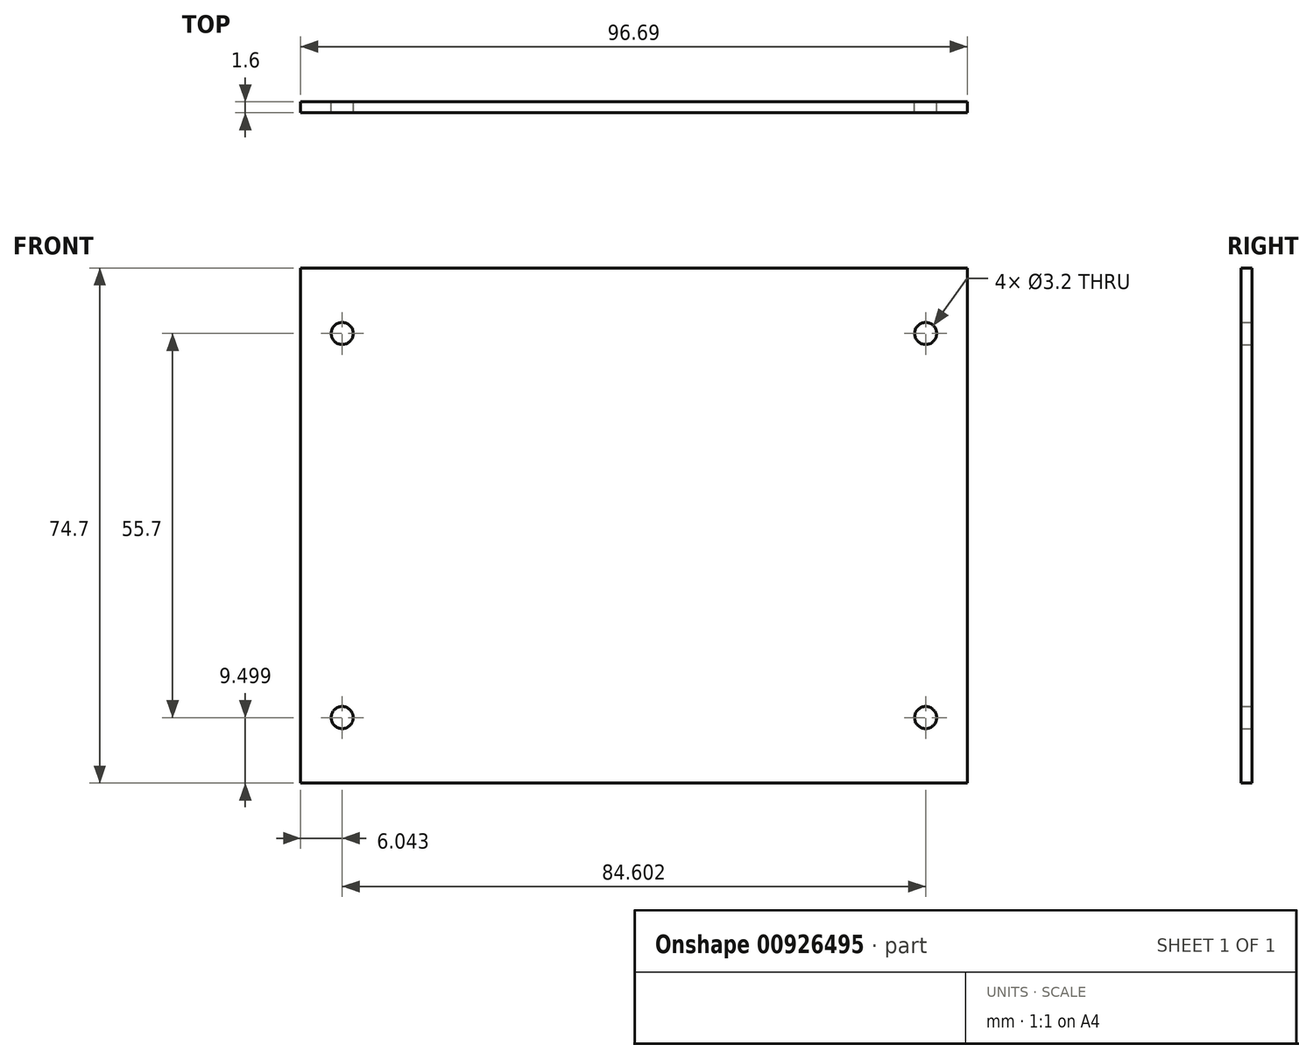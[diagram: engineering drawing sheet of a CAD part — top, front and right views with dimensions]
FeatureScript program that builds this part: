
annotation { "Feature Type Name" : "Feature", "Feature Type Description" : "" }
export const myFeature = defineFeature(function(context is Context, id is Id, definition is map)
    precondition{}
    {
        {
            var Q0;
            Q0=qCreatedBy(makeId("Front.planeOp"),FACE);
            var sketch = newSketch(context, id + "F0", { "sketchPlane" : qUnion([Q0])});
            skLineSegment(sketch, "E0", {"start": v(-1.9, -1.47) * mm, "end": v(-1.9, 1.47) * mm});
            skLineSegment(sketch, "E1", {"start": v(-1.9, 1.47) * mm, "end": v(1.9, 1.47) * mm});
            skLineSegment(sketch, "E2", {"start": v(1.9, 1.47) * mm, "end": v(1.9, -1.47) * mm});
            skLineSegment(sketch, "E3", {"start": v(1.9, -1.47) * mm, "end": v(-1.9, -1.47) * mm});
            skLineSegment(sketch, "E4", {"start": v(-1.73, -1.1) * mm, "end": v(-1.73, -1.1) * mm});
            skLineSegment(sketch, "E5", {"start": v(-1.73, -1.1) * mm, "end": v(-1.73, -1.09) * mm});
            skLineSegment(sketch, "E6", {"start": v(-1.73, -1.09) * mm, "end": v(-1.73, -1.08) * mm});
            skLineSegment(sketch, "E7", {"start": v(-1.73, -1.08) * mm, "end": v(-1.73, -1.08) * mm});
            skLineSegment(sketch, "E8", {"start": v(-1.73, -1.08) * mm, "end": v(-1.72, -1.07) * mm});
            skLineSegment(sketch, "E9", {"start": v(-1.72, -1.07) * mm, "end": v(-1.72, -1.07) * mm});
            skLineSegment(sketch, "E10", {"start": v(-1.72, -1.07) * mm, "end": v(-1.72, -1.06) * mm});
            skLineSegment(sketch, "E11", {"start": v(-1.72, -1.06) * mm, "end": v(-1.72, -1.06) * mm});
            skLineSegment(sketch, "E12", {"start": v(-1.72, -1.06) * mm, "end": v(-1.71, -1.06) * mm});
            skLineSegment(sketch, "E13", {"start": v(-1.71, -1.06) * mm, "end": v(-1.7, -1.05) * mm});
            skLineSegment(sketch, "E14", {"start": v(-1.7, -1.05) * mm, "end": v(-1.7, -1.05) * mm});
            skLineSegment(sketch, "E15", {"start": v(-1.7, -1.05) * mm, "end": v(-1.7, -1.04) * mm});
            skLineSegment(sketch, "E16", {"start": v(-1.7, -1.04) * mm, "end": v(-1.7, -1.04) * mm});
            skLineSegment(sketch, "E17", {"start": v(-1.7, -1.04) * mm, "end": v(-1.69, -1.04) * mm});
            skLineSegment(sketch, "E18", {"start": v(-1.69, -1.04) * mm, "end": v(-1.68, -1.04) * mm});
            skLineSegment(sketch, "E19", {"start": v(-1.68, -1.04) * mm, "end": v(-1.68, -1.03) * mm});
            skLineSegment(sketch, "E20", {"start": v(-1.68, -1.03) * mm, "end": v(-1.67, -1.03) * mm});
            skLineSegment(sketch, "E21", {"start": v(-1.67, -1.03) * mm, "end": v(-1.67, -1.03) * mm});
            skLineSegment(sketch, "E22", {"start": v(-1.67, -1.03) * mm, "end": v(-1.66, -1.03) * mm});
            skLineSegment(sketch, "E23", {"start": v(-1.66, -1.03) * mm, "end": v(-1.66, -1.03) * mm});
            skLineSegment(sketch, "E24", {"start": v(-1.66, -1.03) * mm, "end": v(-1.65, -1.03) * mm});
            skLineSegment(sketch, "E25", {"start": v(-1.65, -1.03) * mm, "end": v(-1.65, -1.04) * mm});
            skLineSegment(sketch, "E26", {"start": v(-1.65, -1.04) * mm, "end": v(-1.64, -1.04) * mm});
            skLineSegment(sketch, "E27", {"start": v(-1.64, -1.04) * mm, "end": v(-1.64, -1.04) * mm});
            skLineSegment(sketch, "E28", {"start": v(-1.64, -1.04) * mm, "end": v(-1.63, -1.04) * mm});
            skLineSegment(sketch, "E29", {"start": v(-1.63, -1.04) * mm, "end": v(-1.63, -1.05) * mm});
            skLineSegment(sketch, "E30", {"start": v(-1.63, -1.05) * mm, "end": v(-1.62, -1.05) * mm});
            skLineSegment(sketch, "E31", {"start": v(-1.62, -1.05) * mm, "end": v(-1.62, -1.05) * mm});
            skLineSegment(sketch, "E32", {"start": v(-1.62, -1.05) * mm, "end": v(-1.62, -1.06) * mm});
            skLineSegment(sketch, "E33", {"start": v(-1.62, -1.06) * mm, "end": v(-1.61, -1.06) * mm});
            skLineSegment(sketch, "E34", {"start": v(-1.61, -1.06) * mm, "end": v(-1.61, -1.07) * mm});
            skLineSegment(sketch, "E35", {"start": v(-1.61, -1.07) * mm, "end": v(-1.6, -1.07) * mm});
            skLineSegment(sketch, "E36", {"start": v(-1.6, -1.07) * mm, "end": v(-1.6, -1.07) * mm});
            skLineSegment(sketch, "E37", {"start": v(-1.6, -1.07) * mm, "end": v(-1.6, -1.08) * mm});
            skLineSegment(sketch, "E38", {"start": v(-1.6, -1.08) * mm, "end": v(-1.6, -1.08) * mm});
            skLineSegment(sketch, "E39", {"start": v(-1.6, -1.08) * mm, "end": v(-1.6, -1.09) * mm});
            skLineSegment(sketch, "E40", {"start": v(-1.6, -1.09) * mm, "end": v(-1.6, -1.1) * mm});
            skLineSegment(sketch, "E41", {"start": v(-1.6, -1.1) * mm, "end": v(-1.6, -1.1) * mm});
            skLineSegment(sketch, "E42", {"start": v(-1.6, -1.1) * mm, "end": v(-1.6, -1.11) * mm});
            skLineSegment(sketch, "E43", {"start": v(-1.6, -1.11) * mm, "end": v(-1.6, -1.12) * mm});
            skLineSegment(sketch, "E44", {"start": v(-1.6, -1.12) * mm, "end": v(-1.6, -1.12) * mm});
            skLineSegment(sketch, "E45", {"start": v(-1.6, -1.12) * mm, "end": v(-1.61, -1.13) * mm});
            skLineSegment(sketch, "E46", {"start": v(-1.61, -1.13) * mm, "end": v(-1.61, -1.13) * mm});
            skLineSegment(sketch, "E47", {"start": v(-1.61, -1.13) * mm, "end": v(-1.62, -1.14) * mm});
            skLineSegment(sketch, "E48", {"start": v(-1.62, -1.14) * mm, "end": v(-1.62, -1.14) * mm});
            skLineSegment(sketch, "E49", {"start": v(-1.62, -1.14) * mm, "end": v(-1.63, -1.15) * mm});
            skLineSegment(sketch, "E50", {"start": v(-1.63, -1.15) * mm, "end": v(-1.63, -1.15) * mm});
            skLineSegment(sketch, "E51", {"start": v(-1.63, -1.15) * mm, "end": v(-1.64, -1.15) * mm});
            skLineSegment(sketch, "E52", {"start": v(-1.64, -1.15) * mm, "end": v(-1.64, -1.15) * mm});
            skLineSegment(sketch, "E53", {"start": v(-1.64, -1.15) * mm, "end": v(-1.64, -1.16) * mm});
            skLineSegment(sketch, "E54", {"start": v(-1.64, -1.16) * mm, "end": v(-1.65, -1.16) * mm});
            skLineSegment(sketch, "E55", {"start": v(-1.65, -1.16) * mm, "end": v(-1.65, -1.16) * mm});
            skLineSegment(sketch, "E56", {"start": v(-1.65, -1.16) * mm, "end": v(-1.66, -1.16) * mm});
            skLineSegment(sketch, "E57", {"start": v(-1.66, -1.16) * mm, "end": v(-1.66, -1.16) * mm});
            skLineSegment(sketch, "E58", {"start": v(-1.66, -1.16) * mm, "end": v(-1.67, -1.16) * mm});
            skLineSegment(sketch, "E59", {"start": v(-1.67, -1.16) * mm, "end": v(-1.67, -1.16) * mm});
            skLineSegment(sketch, "E60", {"start": v(-1.67, -1.16) * mm, "end": v(-1.68, -1.16) * mm});
            skLineSegment(sketch, "E61", {"start": v(-1.68, -1.16) * mm, "end": v(-1.68, -1.16) * mm});
            skLineSegment(sketch, "E62", {"start": v(-1.68, -1.16) * mm, "end": v(-1.69, -1.16) * mm});
            skLineSegment(sketch, "E63", {"start": v(-1.69, -1.16) * mm, "end": v(-1.7, -1.15) * mm});
            skLineSegment(sketch, "E64", {"start": v(-1.7, -1.15) * mm, "end": v(-1.7, -1.15) * mm});
            skLineSegment(sketch, "E65", {"start": v(-1.7, -1.15) * mm, "end": v(-1.7, -1.14) * mm});
            skLineSegment(sketch, "E66", {"start": v(-1.7, -1.14) * mm, "end": v(-1.7, -1.14) * mm});
            skLineSegment(sketch, "E67", {"start": v(-1.7, -1.14) * mm, "end": v(-1.71, -1.14) * mm});
            skLineSegment(sketch, "E68", {"start": v(-1.71, -1.14) * mm, "end": v(-1.72, -1.13) * mm});
            skLineSegment(sketch, "E69", {"start": v(-1.72, -1.13) * mm, "end": v(-1.72, -1.13) * mm});
            skLineSegment(sketch, "E70", {"start": v(-1.72, -1.13) * mm, "end": v(-1.72, -1.12) * mm});
            skLineSegment(sketch, "E71", {"start": v(-1.72, -1.12) * mm, "end": v(-1.73, -1.12) * mm});
            skLineSegment(sketch, "E72", {"start": v(-1.73, -1.12) * mm, "end": v(-1.73, -1.11) * mm});
            skLineSegment(sketch, "E73", {"start": v(-1.73, -1.11) * mm, "end": v(-1.73, -1.1) * mm});
            skLineSegment(sketch, "E74", {"start": v(-1.73, 1.1) * mm, "end": v(-1.73, 1.1) * mm});
            skLineSegment(sketch, "E75", {"start": v(-1.73, 1.1) * mm, "end": v(-1.73, 1.11) * mm});
            skLineSegment(sketch, "E76", {"start": v(-1.73, 1.11) * mm, "end": v(-1.73, 1.12) * mm});
            skLineSegment(sketch, "E77", {"start": v(-1.73, 1.12) * mm, "end": v(-1.72, 1.12) * mm});
            skLineSegment(sketch, "E78", {"start": v(-1.72, 1.12) * mm, "end": v(-1.72, 1.13) * mm});
            skLineSegment(sketch, "E79", {"start": v(-1.72, 1.13) * mm, "end": v(-1.72, 1.13) * mm});
            skLineSegment(sketch, "E80", {"start": v(-1.72, 1.13) * mm, "end": v(-1.71, 1.14) * mm});
            skLineSegment(sketch, "E81", {"start": v(-1.71, 1.14) * mm, "end": v(-1.7, 1.14) * mm});
            skLineSegment(sketch, "E82", {"start": v(-1.7, 1.14) * mm, "end": v(-1.7, 1.14) * mm});
            skLineSegment(sketch, "E83", {"start": v(-1.7, 1.14) * mm, "end": v(-1.7, 1.15) * mm});
            skLineSegment(sketch, "E84", {"start": v(-1.7, 1.15) * mm, "end": v(-1.7, 1.15) * mm});
            skLineSegment(sketch, "E85", {"start": v(-1.7, 1.15) * mm, "end": v(-1.69, 1.16) * mm});
            skLineSegment(sketch, "E86", {"start": v(-1.69, 1.16) * mm, "end": v(-1.68, 1.16) * mm});
            skLineSegment(sketch, "E87", {"start": v(-1.68, 1.16) * mm, "end": v(-1.68, 1.16) * mm});
            skLineSegment(sketch, "E88", {"start": v(-1.68, 1.16) * mm, "end": v(-1.67, 1.16) * mm});
            skLineSegment(sketch, "E89", {"start": v(-1.67, 1.16) * mm, "end": v(-1.67, 1.16) * mm});
            skLineSegment(sketch, "E90", {"start": v(-1.67, 1.16) * mm, "end": v(-1.66, 1.16) * mm});
            skLineSegment(sketch, "E91", {"start": v(-1.66, 1.16) * mm, "end": v(-1.66, 1.16) * mm});
            skLineSegment(sketch, "E92", {"start": v(-1.66, 1.16) * mm, "end": v(-1.65, 1.16) * mm});
            skLineSegment(sketch, "E93", {"start": v(-1.65, 1.16) * mm, "end": v(-1.65, 1.16) * mm});
            skLineSegment(sketch, "E94", {"start": v(-1.65, 1.16) * mm, "end": v(-1.64, 1.16) * mm});
            skLineSegment(sketch, "E95", {"start": v(-1.64, 1.16) * mm, "end": v(-1.64, 1.15) * mm});
            skLineSegment(sketch, "E96", {"start": v(-1.64, 1.15) * mm, "end": v(-1.64, 1.15) * mm});
            skLineSegment(sketch, "E97", {"start": v(-1.64, 1.15) * mm, "end": v(-1.63, 1.15) * mm});
            skLineSegment(sketch, "E98", {"start": v(-1.63, 1.15) * mm, "end": v(-1.63, 1.15) * mm});
            skLineSegment(sketch, "E99", {"start": v(-1.63, 1.15) * mm, "end": v(-1.62, 1.14) * mm});
            skLineSegment(sketch, "E100", {"start": v(-1.62, 1.14) * mm, "end": v(-1.62, 1.14) * mm});
            skLineSegment(sketch, "E101", {"start": v(-1.62, 1.14) * mm, "end": v(-1.61, 1.13) * mm});
            skLineSegment(sketch, "E102", {"start": v(-1.61, 1.13) * mm, "end": v(-1.61, 1.13) * mm});
            skLineSegment(sketch, "E103", {"start": v(-1.61, 1.13) * mm, "end": v(-1.6, 1.12) * mm});
            skLineSegment(sketch, "E104", {"start": v(-1.6, 1.12) * mm, "end": v(-1.6, 1.12) * mm});
            skLineSegment(sketch, "E105", {"start": v(-1.6, 1.12) * mm, "end": v(-1.6, 1.11) * mm});
            skLineSegment(sketch, "E106", {"start": v(-1.6, 1.11) * mm, "end": v(-1.6, 1.1) * mm});
            skLineSegment(sketch, "E107", {"start": v(-1.6, 1.1) * mm, "end": v(-1.6, 1.1) * mm});
            skLineSegment(sketch, "E108", {"start": v(-1.6, 1.1) * mm, "end": v(-1.6, 1.09) * mm});
            skLineSegment(sketch, "E109", {"start": v(-1.6, 1.09) * mm, "end": v(-1.6, 1.08) * mm});
            skLineSegment(sketch, "E110", {"start": v(-1.6, 1.08) * mm, "end": v(-1.6, 1.08) * mm});
            skLineSegment(sketch, "E111", {"start": v(-1.6, 1.08) * mm, "end": v(-1.6, 1.07) * mm});
            skLineSegment(sketch, "E112", {"start": v(-1.6, 1.07) * mm, "end": v(-1.6, 1.07) * mm});
            skLineSegment(sketch, "E113", {"start": v(-1.6, 1.07) * mm, "end": v(-1.61, 1.07) * mm});
            skLineSegment(sketch, "E114", {"start": v(-1.61, 1.07) * mm, "end": v(-1.61, 1.06) * mm});
            skLineSegment(sketch, "E115", {"start": v(-1.61, 1.06) * mm, "end": v(-1.62, 1.06) * mm});
            skLineSegment(sketch, "E116", {"start": v(-1.62, 1.06) * mm, "end": v(-1.62, 1.05) * mm});
            skLineSegment(sketch, "E117", {"start": v(-1.62, 1.05) * mm, "end": v(-1.62, 1.05) * mm});
            skLineSegment(sketch, "E118", {"start": v(-1.62, 1.05) * mm, "end": v(-1.63, 1.05) * mm});
            skLineSegment(sketch, "E119", {"start": v(-1.63, 1.05) * mm, "end": v(-1.63, 1.04) * mm});
            skLineSegment(sketch, "E120", {"start": v(-1.63, 1.04) * mm, "end": v(-1.64, 1.04) * mm});
            skLineSegment(sketch, "E121", {"start": v(-1.64, 1.04) * mm, "end": v(-1.64, 1.04) * mm});
            skLineSegment(sketch, "E122", {"start": v(-1.64, 1.04) * mm, "end": v(-1.65, 1.04) * mm});
            skLineSegment(sketch, "E123", {"start": v(-1.65, 1.04) * mm, "end": v(-1.65, 1.03) * mm});
            skLineSegment(sketch, "E124", {"start": v(-1.65, 1.03) * mm, "end": v(-1.66, 1.03) * mm});
            skLineSegment(sketch, "E125", {"start": v(-1.66, 1.03) * mm, "end": v(-1.66, 1.03) * mm});
            skLineSegment(sketch, "E126", {"start": v(-1.66, 1.03) * mm, "end": v(-1.67, 1.03) * mm});
            skLineSegment(sketch, "E127", {"start": v(-1.67, 1.03) * mm, "end": v(-1.67, 1.03) * mm});
            skLineSegment(sketch, "E128", {"start": v(-1.67, 1.03) * mm, "end": v(-1.68, 1.03) * mm});
            skLineSegment(sketch, "E129", {"start": v(-1.68, 1.03) * mm, "end": v(-1.68, 1.04) * mm});
            skLineSegment(sketch, "E130", {"start": v(-1.68, 1.04) * mm, "end": v(-1.69, 1.04) * mm});
            skLineSegment(sketch, "E131", {"start": v(-1.69, 1.04) * mm, "end": v(-1.7, 1.04) * mm});
            skLineSegment(sketch, "E132", {"start": v(-1.7, 1.04) * mm, "end": v(-1.7, 1.04) * mm});
            skLineSegment(sketch, "E133", {"start": v(-1.7, 1.04) * mm, "end": v(-1.7, 1.05) * mm});
            skLineSegment(sketch, "E134", {"start": v(-1.7, 1.05) * mm, "end": v(-1.7, 1.05) * mm});
            skLineSegment(sketch, "E135", {"start": v(-1.7, 1.05) * mm, "end": v(-1.71, 1.06) * mm});
            skLineSegment(sketch, "E136", {"start": v(-1.71, 1.06) * mm, "end": v(-1.72, 1.06) * mm});
            skLineSegment(sketch, "E137", {"start": v(-1.72, 1.06) * mm, "end": v(-1.72, 1.06) * mm});
            skLineSegment(sketch, "E138", {"start": v(-1.72, 1.06) * mm, "end": v(-1.72, 1.07) * mm});
            skLineSegment(sketch, "E139", {"start": v(-1.72, 1.07) * mm, "end": v(-1.72, 1.07) * mm});
            skLineSegment(sketch, "E140", {"start": v(-1.72, 1.07) * mm, "end": v(-1.73, 1.08) * mm});
            skLineSegment(sketch, "E141", {"start": v(-1.73, 1.08) * mm, "end": v(-1.73, 1.08) * mm});
            skLineSegment(sketch, "E142", {"start": v(-1.73, 1.08) * mm, "end": v(-1.73, 1.09) * mm});
            skLineSegment(sketch, "E143", {"start": v(-1.73, 1.09) * mm, "end": v(-1.73, 1.1) * mm});
            skLineSegment(sketch, "E144", {"start": v(1.6, 1.1) * mm, "end": v(1.6, 1.1) * mm});
            skLineSegment(sketch, "E145", {"start": v(1.6, 1.1) * mm, "end": v(1.6, 1.11) * mm});
            skLineSegment(sketch, "E146", {"start": v(1.6, 1.11) * mm, "end": v(1.6, 1.12) * mm});
            skLineSegment(sketch, "E147", {"start": v(1.6, 1.12) * mm, "end": v(1.6, 1.12) * mm});
            skLineSegment(sketch, "E148", {"start": v(1.6, 1.12) * mm, "end": v(1.6, 1.13) * mm});
            skLineSegment(sketch, "E149", {"start": v(1.6, 1.13) * mm, "end": v(1.61, 1.13) * mm});
            skLineSegment(sketch, "E150", {"start": v(1.61, 1.13) * mm, "end": v(1.61, 1.13) * mm});
            skLineSegment(sketch, "E151", {"start": v(1.61, 1.13) * mm, "end": v(1.62, 1.14) * mm});
            skLineSegment(sketch, "E152", {"start": v(1.62, 1.14) * mm, "end": v(1.62, 1.14) * mm});
            skLineSegment(sketch, "E153", {"start": v(1.62, 1.14) * mm, "end": v(1.63, 1.14) * mm});
            skLineSegment(sketch, "E154", {"start": v(1.63, 1.14) * mm, "end": v(1.63, 1.15) * mm});
            skLineSegment(sketch, "E155", {"start": v(1.63, 1.15) * mm, "end": v(1.63, 1.15) * mm});
            skLineSegment(sketch, "E156", {"start": v(1.63, 1.15) * mm, "end": v(1.64, 1.15) * mm});
            skLineSegment(sketch, "E157", {"start": v(1.64, 1.15) * mm, "end": v(1.64, 1.16) * mm});
            skLineSegment(sketch, "E158", {"start": v(1.64, 1.16) * mm, "end": v(1.65, 1.16) * mm});
            skLineSegment(sketch, "E159", {"start": v(1.65, 1.16) * mm, "end": v(1.65, 1.16) * mm});
            skLineSegment(sketch, "E160", {"start": v(1.65, 1.16) * mm, "end": v(1.66, 1.16) * mm});
            skLineSegment(sketch, "E161", {"start": v(1.66, 1.16) * mm, "end": v(1.66, 1.16) * mm});
            skLineSegment(sketch, "E162", {"start": v(1.66, 1.16) * mm, "end": v(1.67, 1.16) * mm});
            skLineSegment(sketch, "E163", {"start": v(1.67, 1.16) * mm, "end": v(1.67, 1.16) * mm});
            skLineSegment(sketch, "E164", {"start": v(1.67, 1.16) * mm, "end": v(1.68, 1.16) * mm});
            skLineSegment(sketch, "E165", {"start": v(1.68, 1.16) * mm, "end": v(1.68, 1.16) * mm});
            skLineSegment(sketch, "E166", {"start": v(1.68, 1.16) * mm, "end": v(1.69, 1.16) * mm});
            skLineSegment(sketch, "E167", {"start": v(1.69, 1.16) * mm, "end": v(1.7, 1.15) * mm});
            skLineSegment(sketch, "E168", {"start": v(1.7, 1.15) * mm, "end": v(1.7, 1.15) * mm});
            skLineSegment(sketch, "E169", {"start": v(1.7, 1.15) * mm, "end": v(1.7, 1.14) * mm});
            skLineSegment(sketch, "E170", {"start": v(1.7, 1.14) * mm, "end": v(1.71, 1.14) * mm});
            skLineSegment(sketch, "E171", {"start": v(1.71, 1.14) * mm, "end": v(1.71, 1.14) * mm});
            skLineSegment(sketch, "E172", {"start": v(1.71, 1.14) * mm, "end": v(1.72, 1.13) * mm});
            skLineSegment(sketch, "E173", {"start": v(1.72, 1.13) * mm, "end": v(1.72, 1.13) * mm});
            skLineSegment(sketch, "E174", {"start": v(1.72, 1.13) * mm, "end": v(1.72, 1.12) * mm});
            skLineSegment(sketch, "E175", {"start": v(1.72, 1.12) * mm, "end": v(1.72, 1.12) * mm});
            skLineSegment(sketch, "E176", {"start": v(1.72, 1.12) * mm, "end": v(1.73, 1.11) * mm});
            skLineSegment(sketch, "E177", {"start": v(1.73, 1.11) * mm, "end": v(1.73, 1.1) * mm});
            skLineSegment(sketch, "E178", {"start": v(1.73, 1.1) * mm, "end": v(1.73, 1.1) * mm});
            skLineSegment(sketch, "E179", {"start": v(1.73, 1.1) * mm, "end": v(1.73, 1.09) * mm});
            skLineSegment(sketch, "E180", {"start": v(1.73, 1.09) * mm, "end": v(1.73, 1.08) * mm});
            skLineSegment(sketch, "E181", {"start": v(1.73, 1.08) * mm, "end": v(1.73, 1.08) * mm});
            skLineSegment(sketch, "E182", {"start": v(1.73, 1.08) * mm, "end": v(1.72, 1.07) * mm});
            skLineSegment(sketch, "E183", {"start": v(1.72, 1.07) * mm, "end": v(1.72, 1.07) * mm});
            skLineSegment(sketch, "E184", {"start": v(1.72, 1.07) * mm, "end": v(1.72, 1.06) * mm});
            skLineSegment(sketch, "E185", {"start": v(1.72, 1.06) * mm, "end": v(1.71, 1.06) * mm});
            skLineSegment(sketch, "E186", {"start": v(1.71, 1.06) * mm, "end": v(1.71, 1.05) * mm});
            skLineSegment(sketch, "E187", {"start": v(1.71, 1.05) * mm, "end": v(1.7, 1.05) * mm});
            skLineSegment(sketch, "E188", {"start": v(1.7, 1.05) * mm, "end": v(1.7, 1.05) * mm});
            skLineSegment(sketch, "E189", {"start": v(1.7, 1.05) * mm, "end": v(1.7, 1.04) * mm});
            skLineSegment(sketch, "E190", {"start": v(1.7, 1.04) * mm, "end": v(1.7, 1.04) * mm});
            skLineSegment(sketch, "E191", {"start": v(1.7, 1.04) * mm, "end": v(1.69, 1.04) * mm});
            skLineSegment(sketch, "E192", {"start": v(1.69, 1.04) * mm, "end": v(1.68, 1.04) * mm});
            skLineSegment(sketch, "E193", {"start": v(1.68, 1.04) * mm, "end": v(1.68, 1.03) * mm});
            skLineSegment(sketch, "E194", {"start": v(1.68, 1.03) * mm, "end": v(1.67, 1.03) * mm});
            skLineSegment(sketch, "E195", {"start": v(1.67, 1.03) * mm, "end": v(1.67, 1.03) * mm});
            skLineSegment(sketch, "E196", {"start": v(1.67, 1.03) * mm, "end": v(1.66, 1.03) * mm});
            skLineSegment(sketch, "E197", {"start": v(1.66, 1.03) * mm, "end": v(1.66, 1.03) * mm});
            skLineSegment(sketch, "E198", {"start": v(1.66, 1.03) * mm, "end": v(1.65, 1.03) * mm});
            skLineSegment(sketch, "E199", {"start": v(1.65, 1.03) * mm, "end": v(1.65, 1.04) * mm});
            skLineSegment(sketch, "E200", {"start": v(1.65, 1.04) * mm, "end": v(1.64, 1.04) * mm});
            skLineSegment(sketch, "E201", {"start": v(1.64, 1.04) * mm, "end": v(1.64, 1.04) * mm});
            skLineSegment(sketch, "E202", {"start": v(1.64, 1.04) * mm, "end": v(1.63, 1.04) * mm});
            skLineSegment(sketch, "E203", {"start": v(1.63, 1.04) * mm, "end": v(1.63, 1.05) * mm});
            skLineSegment(sketch, "E204", {"start": v(1.63, 1.05) * mm, "end": v(1.63, 1.05) * mm});
            skLineSegment(sketch, "E205", {"start": v(1.63, 1.05) * mm, "end": v(1.62, 1.05) * mm});
            skLineSegment(sketch, "E206", {"start": v(1.62, 1.05) * mm, "end": v(1.62, 1.06) * mm});
            skLineSegment(sketch, "E207", {"start": v(1.62, 1.06) * mm, "end": v(1.61, 1.06) * mm});
            skLineSegment(sketch, "E208", {"start": v(1.61, 1.06) * mm, "end": v(1.61, 1.06) * mm});
            skLineSegment(sketch, "E209", {"start": v(1.61, 1.06) * mm, "end": v(1.6, 1.07) * mm});
            skLineSegment(sketch, "E210", {"start": v(1.6, 1.07) * mm, "end": v(1.6, 1.07) * mm});
            skLineSegment(sketch, "E211", {"start": v(1.6, 1.07) * mm, "end": v(1.6, 1.08) * mm});
            skLineSegment(sketch, "E212", {"start": v(1.6, 1.08) * mm, "end": v(1.6, 1.08) * mm});
            skLineSegment(sketch, "E213", {"start": v(1.6, 1.08) * mm, "end": v(1.6, 1.09) * mm});
            skLineSegment(sketch, "E214", {"start": v(1.6, 1.09) * mm, "end": v(1.6, 1.1) * mm});
            skLineSegment(sketch, "E215", {"start": v(1.6, -1.1) * mm, "end": v(1.6, -1.1) * mm});
            skLineSegment(sketch, "E216", {"start": v(1.6, -1.1) * mm, "end": v(1.6, -1.09) * mm});
            skLineSegment(sketch, "E217", {"start": v(1.6, -1.09) * mm, "end": v(1.6, -1.08) * mm});
            skLineSegment(sketch, "E218", {"start": v(1.6, -1.08) * mm, "end": v(1.6, -1.08) * mm});
            skLineSegment(sketch, "E219", {"start": v(1.6, -1.08) * mm, "end": v(1.6, -1.07) * mm});
            skLineSegment(sketch, "E220", {"start": v(1.6, -1.07) * mm, "end": v(1.6, -1.07) * mm});
            skLineSegment(sketch, "E221", {"start": v(1.6, -1.07) * mm, "end": v(1.61, -1.06) * mm});
            skLineSegment(sketch, "E222", {"start": v(1.61, -1.06) * mm, "end": v(1.61, -1.06) * mm});
            skLineSegment(sketch, "E223", {"start": v(1.61, -1.06) * mm, "end": v(1.62, -1.06) * mm});
            skLineSegment(sketch, "E224", {"start": v(1.62, -1.06) * mm, "end": v(1.62, -1.05) * mm});
            skLineSegment(sketch, "E225", {"start": v(1.62, -1.05) * mm, "end": v(1.63, -1.05) * mm});
            skLineSegment(sketch, "E226", {"start": v(1.63, -1.05) * mm, "end": v(1.63, -1.05) * mm});
            skLineSegment(sketch, "E227", {"start": v(1.63, -1.05) * mm, "end": v(1.63, -1.04) * mm});
            skLineSegment(sketch, "E228", {"start": v(1.63, -1.04) * mm, "end": v(1.64, -1.04) * mm});
            skLineSegment(sketch, "E229", {"start": v(1.64, -1.04) * mm, "end": v(1.64, -1.04) * mm});
            skLineSegment(sketch, "E230", {"start": v(1.64, -1.04) * mm, "end": v(1.65, -1.04) * mm});
            skLineSegment(sketch, "E231", {"start": v(1.65, -1.04) * mm, "end": v(1.65, -1.03) * mm});
            skLineSegment(sketch, "E232", {"start": v(1.65, -1.03) * mm, "end": v(1.66, -1.03) * mm});
            skLineSegment(sketch, "E233", {"start": v(1.66, -1.03) * mm, "end": v(1.66, -1.03) * mm});
            skLineSegment(sketch, "E234", {"start": v(1.66, -1.03) * mm, "end": v(1.67, -1.03) * mm});
            skLineSegment(sketch, "E235", {"start": v(1.67, -1.03) * mm, "end": v(1.67, -1.03) * mm});
            skLineSegment(sketch, "E236", {"start": v(1.67, -1.03) * mm, "end": v(1.68, -1.03) * mm});
            skLineSegment(sketch, "E237", {"start": v(1.68, -1.03) * mm, "end": v(1.68, -1.04) * mm});
            skLineSegment(sketch, "E238", {"start": v(1.68, -1.04) * mm, "end": v(1.69, -1.04) * mm});
            skLineSegment(sketch, "E239", {"start": v(1.69, -1.04) * mm, "end": v(1.7, -1.04) * mm});
            skLineSegment(sketch, "E240", {"start": v(1.7, -1.04) * mm, "end": v(1.7, -1.04) * mm});
            skLineSegment(sketch, "E241", {"start": v(1.7, -1.04) * mm, "end": v(1.7, -1.05) * mm});
            skLineSegment(sketch, "E242", {"start": v(1.7, -1.05) * mm, "end": v(1.7, -1.05) * mm});
            skLineSegment(sketch, "E243", {"start": v(1.7, -1.05) * mm, "end": v(1.71, -1.05) * mm});
            skLineSegment(sketch, "E244", {"start": v(1.71, -1.05) * mm, "end": v(1.71, -1.06) * mm});
            skLineSegment(sketch, "E245", {"start": v(1.71, -1.06) * mm, "end": v(1.72, -1.06) * mm});
            skLineSegment(sketch, "E246", {"start": v(1.72, -1.06) * mm, "end": v(1.72, -1.07) * mm});
            skLineSegment(sketch, "E247", {"start": v(1.72, -1.07) * mm, "end": v(1.72, -1.07) * mm});
            skLineSegment(sketch, "E248", {"start": v(1.72, -1.07) * mm, "end": v(1.73, -1.08) * mm});
            skLineSegment(sketch, "E249", {"start": v(1.73, -1.08) * mm, "end": v(1.73, -1.08) * mm});
            skLineSegment(sketch, "E250", {"start": v(1.73, -1.08) * mm, "end": v(1.73, -1.09) * mm});
            skLineSegment(sketch, "E251", {"start": v(1.73, -1.09) * mm, "end": v(1.73, -1.1) * mm});
            skLineSegment(sketch, "E252", {"start": v(1.73, -1.1) * mm, "end": v(1.73, -1.1) * mm});
            skLineSegment(sketch, "E253", {"start": v(1.73, -1.1) * mm, "end": v(1.73, -1.11) * mm});
            skLineSegment(sketch, "E254", {"start": v(1.73, -1.11) * mm, "end": v(1.72, -1.12) * mm});
            skLineSegment(sketch, "E255", {"start": v(1.72, -1.12) * mm, "end": v(1.72, -1.12) * mm});
            skLineSegment(sketch, "E256", {"start": v(1.72, -1.12) * mm, "end": v(1.72, -1.13) * mm});
            skLineSegment(sketch, "E257", {"start": v(1.72, -1.13) * mm, "end": v(1.72, -1.13) * mm});
            skLineSegment(sketch, "E258", {"start": v(1.72, -1.13) * mm, "end": v(1.71, -1.14) * mm});
            skLineSegment(sketch, "E259", {"start": v(1.71, -1.14) * mm, "end": v(1.71, -1.14) * mm});
            skLineSegment(sketch, "E260", {"start": v(1.71, -1.14) * mm, "end": v(1.7, -1.14) * mm});
            skLineSegment(sketch, "E261", {"start": v(1.7, -1.14) * mm, "end": v(1.7, -1.15) * mm});
            skLineSegment(sketch, "E262", {"start": v(1.7, -1.15) * mm, "end": v(1.7, -1.15) * mm});
            skLineSegment(sketch, "E263", {"start": v(1.7, -1.15) * mm, "end": v(1.69, -1.16) * mm});
            skLineSegment(sketch, "E264", {"start": v(1.69, -1.16) * mm, "end": v(1.68, -1.16) * mm});
            skLineSegment(sketch, "E265", {"start": v(1.68, -1.16) * mm, "end": v(1.68, -1.16) * mm});
            skLineSegment(sketch, "E266", {"start": v(1.68, -1.16) * mm, "end": v(1.67, -1.16) * mm});
            skLineSegment(sketch, "E267", {"start": v(1.67, -1.16) * mm, "end": v(1.67, -1.16) * mm});
            skLineSegment(sketch, "E268", {"start": v(1.67, -1.16) * mm, "end": v(1.66, -1.16) * mm});
            skLineSegment(sketch, "E269", {"start": v(1.66, -1.16) * mm, "end": v(1.66, -1.16) * mm});
            skLineSegment(sketch, "E270", {"start": v(1.66, -1.16) * mm, "end": v(1.65, -1.16) * mm});
            skLineSegment(sketch, "E271", {"start": v(1.65, -1.16) * mm, "end": v(1.65, -1.16) * mm});
            skLineSegment(sketch, "E272", {"start": v(1.65, -1.16) * mm, "end": v(1.64, -1.16) * mm});
            skLineSegment(sketch, "E273", {"start": v(1.64, -1.16) * mm, "end": v(1.64, -1.15) * mm});
            skLineSegment(sketch, "E274", {"start": v(1.64, -1.15) * mm, "end": v(1.63, -1.15) * mm});
            skLineSegment(sketch, "E275", {"start": v(1.63, -1.15) * mm, "end": v(1.63, -1.15) * mm});
            skLineSegment(sketch, "E276", {"start": v(1.63, -1.15) * mm, "end": v(1.63, -1.14) * mm});
            skLineSegment(sketch, "E277", {"start": v(1.63, -1.14) * mm, "end": v(1.62, -1.14) * mm});
            skLineSegment(sketch, "E278", {"start": v(1.62, -1.14) * mm, "end": v(1.62, -1.14) * mm});
            skLineSegment(sketch, "E279", {"start": v(1.62, -1.14) * mm, "end": v(1.61, -1.13) * mm});
            skLineSegment(sketch, "E280", {"start": v(1.61, -1.13) * mm, "end": v(1.61, -1.13) * mm});
            skLineSegment(sketch, "E281", {"start": v(1.61, -1.13) * mm, "end": v(1.6, -1.13) * mm});
            skLineSegment(sketch, "E282", {"start": v(1.6, -1.13) * mm, "end": v(1.6, -1.12) * mm});
            skLineSegment(sketch, "E283", {"start": v(1.6, -1.12) * mm, "end": v(1.6, -1.12) * mm});
            skLineSegment(sketch, "E284", {"start": v(1.6, -1.12) * mm, "end": v(1.6, -1.11) * mm});
            skLineSegment(sketch, "E285", {"start": v(1.6, -1.11) * mm, "end": v(1.6, -1.1) * mm});
            skLineSegment(sketch, "E286", {"start": v(1.37, -0.95) * mm, "end": v(1.27, -0.95) * mm});
            skLineSegment(sketch, "E287", {"start": v(1.27, -0.95) * mm, "end": v(1.27, -0.89) * mm});
            skLineSegment(sketch, "E288", {"start": v(1.27, -0.89) * mm, "end": v(1.27, -0.82) * mm});
            skLineSegment(sketch, "E289", {"start": v(1.27, -0.82) * mm, "end": v(1.27, -0.69) * mm});
            skLineSegment(sketch, "E290", {"start": v(1.27, -0.69) * mm, "end": v(1.27, -0.62) * mm});
            skLineSegment(sketch, "E291", {"start": v(1.27, -0.62) * mm, "end": v(1.27, -0.55) * mm});
            skLineSegment(sketch, "E292", {"start": v(1.27, -0.55) * mm, "end": v(1.01, -0.55) * mm});
            skLineSegment(sketch, "E293", {"start": v(1.01, -0.55) * mm, "end": v(1, -0.55) * mm});
            skLineSegment(sketch, "E294", {"start": v(1, -0.55) * mm, "end": v(1, -0.95) * mm});
            skLineSegment(sketch, "E295", {"start": v(1, -0.95) * mm, "end": v(1.01, -0.95) * mm});
            skLineSegment(sketch, "E296", {"start": v(1.01, -0.95) * mm, "end": v(1.27, -0.95) * mm});
            skLineSegment(sketch, "E297", {"start": v(1.37, -0.95) * mm, "end": v(1.37, -0.55) * mm});
            skLineSegment(sketch, "E298", {"start": v(1.37, -0.55) * mm, "end": v(1.27, -0.55) * mm});
            skLineSegment(sketch, "E299", {"start": v(1.14, -0.65) * mm, "end": v(1.14, -0.65) * mm});
            skLineSegment(sketch, "E300", {"start": v(1.14, -0.65) * mm, "end": v(1.14, -0.64) * mm});
            skLineSegment(sketch, "E301", {"start": v(1.14, -0.64) * mm, "end": v(1.14, -0.64) * mm});
            skLineSegment(sketch, "E302", {"start": v(1.14, -0.64) * mm, "end": v(1.14, -0.63) * mm});
            skLineSegment(sketch, "E303", {"start": v(1.14, -0.63) * mm, "end": v(1.15, -0.63) * mm});
            skLineSegment(sketch, "E304", {"start": v(1.15, -0.63) * mm, "end": v(1.15, -0.62) * mm});
            skLineSegment(sketch, "E305", {"start": v(1.15, -0.62) * mm, "end": v(1.15, -0.62) * mm});
            skLineSegment(sketch, "E306", {"start": v(1.15, -0.62) * mm, "end": v(1.15, -0.61) * mm});
            skLineSegment(sketch, "E307", {"start": v(1.15, -0.61) * mm, "end": v(1.16, -0.61) * mm});
            skLineSegment(sketch, "E308", {"start": v(1.16, -0.61) * mm, "end": v(1.16, -0.6) * mm});
            skLineSegment(sketch, "E309", {"start": v(1.16, -0.6) * mm, "end": v(1.16, -0.6) * mm});
            skLineSegment(sketch, "E310", {"start": v(1.16, -0.6) * mm, "end": v(1.17, -0.6) * mm});
            skLineSegment(sketch, "E311", {"start": v(1.17, -0.6) * mm, "end": v(1.17, -0.6) * mm});
            skLineSegment(sketch, "E312", {"start": v(1.17, -0.6) * mm, "end": v(1.18, -0.6) * mm});
            skLineSegment(sketch, "E313", {"start": v(1.18, -0.6) * mm, "end": v(1.18, -0.6) * mm});
            skLineSegment(sketch, "E314", {"start": v(1.18, -0.6) * mm, "end": v(1.19, -0.6) * mm});
            skLineSegment(sketch, "E315", {"start": v(1.19, -0.6) * mm, "end": v(1.2, -0.6) * mm});
            skLineSegment(sketch, "E316", {"start": v(1.2, -0.6) * mm, "end": v(1.2, -0.6) * mm});
            skLineSegment(sketch, "E317", {"start": v(1.2, -0.6) * mm, "end": v(1.21, -0.6) * mm});
            skLineSegment(sketch, "E318", {"start": v(1.21, -0.6) * mm, "end": v(1.22, -0.6) * mm});
            skLineSegment(sketch, "E319", {"start": v(1.22, -0.6) * mm, "end": v(1.22, -0.6) * mm});
            skLineSegment(sketch, "E320", {"start": v(1.22, -0.6) * mm, "end": v(1.23, -0.6) * mm});
            skLineSegment(sketch, "E321", {"start": v(1.23, -0.6) * mm, "end": v(1.23, -0.6) * mm});
            skLineSegment(sketch, "E322", {"start": v(1.23, -0.6) * mm, "end": v(1.24, -0.6) * mm});
            skLineSegment(sketch, "E323", {"start": v(1.24, -0.6) * mm, "end": v(1.24, -0.6) * mm});
            skLineSegment(sketch, "E324", {"start": v(1.24, -0.6) * mm, "end": v(1.25, -0.61) * mm});
            skLineSegment(sketch, "E325", {"start": v(1.25, -0.61) * mm, "end": v(1.25, -0.62) * mm});
            skLineSegment(sketch, "E326", {"start": v(1.25, -0.62) * mm, "end": v(1.25, -0.62) * mm});
            skLineSegment(sketch, "E327", {"start": v(1.25, -0.62) * mm, "end": v(1.26, -0.63) * mm});
            skLineSegment(sketch, "E328", {"start": v(1.26, -0.63) * mm, "end": v(1.26, -0.63) * mm});
            skLineSegment(sketch, "E329", {"start": v(1.26, -0.63) * mm, "end": v(1.26, -0.64) * mm});
            skLineSegment(sketch, "E330", {"start": v(1.26, -0.64) * mm, "end": v(1.26, -0.64) * mm});
            skLineSegment(sketch, "E331", {"start": v(1.26, -0.64) * mm, "end": v(1.26, -0.65) * mm});
            skLineSegment(sketch, "E332", {"start": v(1.26, -0.65) * mm, "end": v(1.26, -0.65) * mm});
            skLineSegment(sketch, "E333", {"start": v(1.26, -0.65) * mm, "end": v(1.26, -0.66) * mm});
            skLineSegment(sketch, "E334", {"start": v(1.26, -0.66) * mm, "end": v(1.26, -0.66) * mm});
            skLineSegment(sketch, "E335", {"start": v(1.26, -0.66) * mm, "end": v(1.26, -0.67) * mm});
            skLineSegment(sketch, "E336", {"start": v(1.26, -0.67) * mm, "end": v(1.26, -0.67) * mm});
            skLineSegment(sketch, "E337", {"start": v(1.26, -0.67) * mm, "end": v(1.25, -0.68) * mm});
            skLineSegment(sketch, "E338", {"start": v(1.25, -0.68) * mm, "end": v(1.25, -0.68) * mm});
            skLineSegment(sketch, "E339", {"start": v(1.25, -0.68) * mm, "end": v(1.25, -0.69) * mm});
            skLineSegment(sketch, "E340", {"start": v(1.25, -0.69) * mm, "end": v(1.24, -0.7) * mm});
            skLineSegment(sketch, "E341", {"start": v(1.24, -0.7) * mm, "end": v(1.24, -0.7) * mm});
            skLineSegment(sketch, "E342", {"start": v(1.24, -0.7) * mm, "end": v(1.23, -0.7) * mm});
            skLineSegment(sketch, "E343", {"start": v(1.23, -0.7) * mm, "end": v(1.23, -0.7) * mm});
            skLineSegment(sketch, "E344", {"start": v(1.23, -0.7) * mm, "end": v(1.22, -0.7) * mm});
            skLineSegment(sketch, "E345", {"start": v(1.22, -0.7) * mm, "end": v(1.22, -0.7) * mm});
            skLineSegment(sketch, "E346", {"start": v(1.22, -0.7) * mm, "end": v(1.21, -0.7) * mm});
            skLineSegment(sketch, "E347", {"start": v(1.21, -0.7) * mm, "end": v(1.2, -0.7) * mm});
            skLineSegment(sketch, "E348", {"start": v(1.2, -0.7) * mm, "end": v(1.2, -0.7) * mm});
            skLineSegment(sketch, "E349", {"start": v(1.2, -0.7) * mm, "end": v(1.19, -0.7) * mm});
            skLineSegment(sketch, "E350", {"start": v(1.19, -0.7) * mm, "end": v(1.18, -0.7) * mm});
            skLineSegment(sketch, "E351", {"start": v(1.18, -0.7) * mm, "end": v(1.18, -0.7) * mm});
            skLineSegment(sketch, "E352", {"start": v(1.18, -0.7) * mm, "end": v(1.17, -0.7) * mm});
            skLineSegment(sketch, "E353", {"start": v(1.17, -0.7) * mm, "end": v(1.17, -0.7) * mm});
            skLineSegment(sketch, "E354", {"start": v(1.17, -0.7) * mm, "end": v(1.16, -0.7) * mm});
            skLineSegment(sketch, "E355", {"start": v(1.16, -0.7) * mm, "end": v(1.16, -0.7) * mm});
            skLineSegment(sketch, "E356", {"start": v(1.16, -0.7) * mm, "end": v(1.16, -0.69) * mm});
            skLineSegment(sketch, "E357", {"start": v(1.16, -0.69) * mm, "end": v(1.15, -0.69) * mm});
            skLineSegment(sketch, "E358", {"start": v(1.15, -0.69) * mm, "end": v(1.15, -0.68) * mm});
            skLineSegment(sketch, "E359", {"start": v(1.15, -0.68) * mm, "end": v(1.15, -0.68) * mm});
            skLineSegment(sketch, "E360", {"start": v(1.15, -0.68) * mm, "end": v(1.15, -0.67) * mm});
            skLineSegment(sketch, "E361", {"start": v(1.15, -0.67) * mm, "end": v(1.14, -0.67) * mm});
            skLineSegment(sketch, "E362", {"start": v(1.14, -0.67) * mm, "end": v(1.14, -0.66) * mm});
            skLineSegment(sketch, "E363", {"start": v(1.14, -0.66) * mm, "end": v(1.14, -0.66) * mm});
            skLineSegment(sketch, "E364", {"start": v(1.14, -0.66) * mm, "end": v(1.14, -0.65) * mm});
            skLineSegment(sketch, "E365", {"start": v(1.04, -0.65) * mm, "end": v(1.04, -0.65) * mm});
            skLineSegment(sketch, "E366", {"start": v(1.04, -0.65) * mm, "end": v(1.04, -0.64) * mm});
            skLineSegment(sketch, "E367", {"start": v(1.04, -0.64) * mm, "end": v(1.04, -0.64) * mm});
            skLineSegment(sketch, "E368", {"start": v(1.04, -0.64) * mm, "end": v(1.05, -0.64) * mm});
            skLineSegment(sketch, "E369", {"start": v(1.05, -0.64) * mm, "end": v(1.05, -0.64) * mm});
            skLineSegment(sketch, "E370", {"start": v(1.05, -0.64) * mm, "end": v(1.05, -0.63) * mm});
            skLineSegment(sketch, "E371", {"start": v(1.05, -0.63) * mm, "end": v(1.05, -0.63) * mm});
            skLineSegment(sketch, "E372", {"start": v(1.05, -0.63) * mm, "end": v(1.06, -0.63) * mm});
            skLineSegment(sketch, "E373", {"start": v(1.06, -0.63) * mm, "end": v(1.06, -0.63) * mm});
            skLineSegment(sketch, "E374", {"start": v(1.06, -0.63) * mm, "end": v(1.07, -0.63) * mm});
            skLineSegment(sketch, "E375", {"start": v(1.07, -0.63) * mm, "end": v(1.07, -0.63) * mm});
            skLineSegment(sketch, "E376", {"start": v(1.07, -0.63) * mm, "end": v(1.08, -0.63) * mm});
            skLineSegment(sketch, "E377", {"start": v(1.08, -0.63) * mm, "end": v(1.08, -0.64) * mm});
            skLineSegment(sketch, "E378", {"start": v(1.08, -0.64) * mm, "end": v(1.08, -0.64) * mm});
            skLineSegment(sketch, "E379", {"start": v(1.08, -0.64) * mm, "end": v(1.08, -0.65) * mm});
            skLineSegment(sketch, "E380", {"start": v(1.08, -0.65) * mm, "end": v(1.08, -0.65) * mm});
            skLineSegment(sketch, "E381", {"start": v(1.08, -0.65) * mm, "end": v(1.08, -0.66) * mm});
            skLineSegment(sketch, "E382", {"start": v(1.08, -0.66) * mm, "end": v(1.08, -0.66) * mm});
            skLineSegment(sketch, "E383", {"start": v(1.08, -0.66) * mm, "end": v(1.08, -0.67) * mm});
            skLineSegment(sketch, "E384", {"start": v(1.08, -0.67) * mm, "end": v(1.07, -0.67) * mm});
            skLineSegment(sketch, "E385", {"start": v(1.07, -0.67) * mm, "end": v(1.07, -0.67) * mm});
            skLineSegment(sketch, "E386", {"start": v(1.07, -0.67) * mm, "end": v(1.06, -0.67) * mm});
            skLineSegment(sketch, "E387", {"start": v(1.06, -0.67) * mm, "end": v(1.06, -0.67) * mm});
            skLineSegment(sketch, "E388", {"start": v(1.06, -0.67) * mm, "end": v(1.05, -0.67) * mm});
            skLineSegment(sketch, "E389", {"start": v(1.05, -0.67) * mm, "end": v(1.05, -0.67) * mm});
            skLineSegment(sketch, "E390", {"start": v(1.05, -0.67) * mm, "end": v(1.05, -0.66) * mm});
            skLineSegment(sketch, "E391", {"start": v(1.05, -0.66) * mm, "end": v(1.05, -0.66) * mm});
            skLineSegment(sketch, "E392", {"start": v(1.05, -0.66) * mm, "end": v(1.04, -0.66) * mm});
            skLineSegment(sketch, "E393", {"start": v(1.04, -0.66) * mm, "end": v(1.04, -0.66) * mm});
            skLineSegment(sketch, "E394", {"start": v(1.04, -0.66) * mm, "end": v(1.04, -0.65) * mm});
            skLineSegment(sketch, "E395", {"start": v(1.01, -0.55) * mm, "end": v(1.01, -0.95) * mm});
            skLineSegment(sketch, "E396", {"start": v(1.04, -0.85) * mm, "end": v(1.04, -0.85) * mm});
            skLineSegment(sketch, "E397", {"start": v(1.04, -0.85) * mm, "end": v(1.04, -0.84) * mm});
            skLineSegment(sketch, "E398", {"start": v(1.04, -0.84) * mm, "end": v(1.04, -0.84) * mm});
            skLineSegment(sketch, "E399", {"start": v(1.04, -0.84) * mm, "end": v(1.05, -0.84) * mm});
            skLineSegment(sketch, "E400", {"start": v(1.05, -0.84) * mm, "end": v(1.05, -0.84) * mm});
            skLineSegment(sketch, "E401", {"start": v(1.05, -0.84) * mm, "end": v(1.05, -0.83) * mm});
            skLineSegment(sketch, "E402", {"start": v(1.05, -0.83) * mm, "end": v(1.05, -0.83) * mm});
            skLineSegment(sketch, "E403", {"start": v(1.05, -0.83) * mm, "end": v(1.06, -0.83) * mm});
            skLineSegment(sketch, "E404", {"start": v(1.06, -0.83) * mm, "end": v(1.06, -0.83) * mm});
            skLineSegment(sketch, "E405", {"start": v(1.06, -0.83) * mm, "end": v(1.07, -0.83) * mm});
            skLineSegment(sketch, "E406", {"start": v(1.07, -0.83) * mm, "end": v(1.07, -0.83) * mm});
            skLineSegment(sketch, "E407", {"start": v(1.07, -0.83) * mm, "end": v(1.08, -0.83) * mm});
            skLineSegment(sketch, "E408", {"start": v(1.08, -0.83) * mm, "end": v(1.08, -0.84) * mm});
            skLineSegment(sketch, "E409", {"start": v(1.08, -0.84) * mm, "end": v(1.08, -0.84) * mm});
            skLineSegment(sketch, "E410", {"start": v(1.08, -0.84) * mm, "end": v(1.08, -0.85) * mm});
            skLineSegment(sketch, "E411", {"start": v(1.08, -0.85) * mm, "end": v(1.08, -0.85) * mm});
            skLineSegment(sketch, "E412", {"start": v(1.08, -0.85) * mm, "end": v(1.08, -0.86) * mm});
            skLineSegment(sketch, "E413", {"start": v(1.08, -0.86) * mm, "end": v(1.08, -0.86) * mm});
            skLineSegment(sketch, "E414", {"start": v(1.08, -0.86) * mm, "end": v(1.08, -0.87) * mm});
            skLineSegment(sketch, "E415", {"start": v(1.08, -0.87) * mm, "end": v(1.07, -0.87) * mm});
            skLineSegment(sketch, "E416", {"start": v(1.07, -0.87) * mm, "end": v(1.07, -0.87) * mm});
            skLineSegment(sketch, "E417", {"start": v(1.07, -0.87) * mm, "end": v(1.06, -0.87) * mm});
            skLineSegment(sketch, "E418", {"start": v(1.06, -0.87) * mm, "end": v(1.06, -0.87) * mm});
            skLineSegment(sketch, "E419", {"start": v(1.06, -0.87) * mm, "end": v(1.05, -0.87) * mm});
            skLineSegment(sketch, "E420", {"start": v(1.05, -0.87) * mm, "end": v(1.05, -0.87) * mm});
            skLineSegment(sketch, "E421", {"start": v(1.05, -0.87) * mm, "end": v(1.05, -0.86) * mm});
            skLineSegment(sketch, "E422", {"start": v(1.05, -0.86) * mm, "end": v(1.05, -0.86) * mm});
            skLineSegment(sketch, "E423", {"start": v(1.05, -0.86) * mm, "end": v(1.04, -0.86) * mm});
            skLineSegment(sketch, "E424", {"start": v(1.04, -0.86) * mm, "end": v(1.04, -0.86) * mm});
            skLineSegment(sketch, "E425", {"start": v(1.04, -0.86) * mm, "end": v(1.04, -0.85) * mm});
            skLineSegment(sketch, "E426", {"start": v(1.14, -0.85) * mm, "end": v(1.14, -0.85) * mm});
            skLineSegment(sketch, "E427", {"start": v(1.14, -0.85) * mm, "end": v(1.14, -0.84) * mm});
            skLineSegment(sketch, "E428", {"start": v(1.14, -0.84) * mm, "end": v(1.14, -0.84) * mm});
            skLineSegment(sketch, "E429", {"start": v(1.14, -0.84) * mm, "end": v(1.14, -0.83) * mm});
            skLineSegment(sketch, "E430", {"start": v(1.14, -0.83) * mm, "end": v(1.15, -0.83) * mm});
            skLineSegment(sketch, "E431", {"start": v(1.15, -0.83) * mm, "end": v(1.15, -0.82) * mm});
            skLineSegment(sketch, "E432", {"start": v(1.15, -0.82) * mm, "end": v(1.15, -0.82) * mm});
            skLineSegment(sketch, "E433", {"start": v(1.15, -0.82) * mm, "end": v(1.15, -0.81) * mm});
            skLineSegment(sketch, "E434", {"start": v(1.15, -0.81) * mm, "end": v(1.16, -0.81) * mm});
            skLineSegment(sketch, "E435", {"start": v(1.16, -0.81) * mm, "end": v(1.16, -0.8) * mm});
            skLineSegment(sketch, "E436", {"start": v(1.16, -0.8) * mm, "end": v(1.16, -0.8) * mm});
            skLineSegment(sketch, "E437", {"start": v(1.16, -0.8) * mm, "end": v(1.17, -0.8) * mm});
            skLineSegment(sketch, "E438", {"start": v(1.17, -0.8) * mm, "end": v(1.17, -0.8) * mm});
            skLineSegment(sketch, "E439", {"start": v(1.17, -0.8) * mm, "end": v(1.18, -0.8) * mm});
            skLineSegment(sketch, "E440", {"start": v(1.18, -0.8) * mm, "end": v(1.18, -0.8) * mm});
            skLineSegment(sketch, "E441", {"start": v(1.18, -0.8) * mm, "end": v(1.19, -0.8) * mm});
            skLineSegment(sketch, "E442", {"start": v(1.19, -0.8) * mm, "end": v(1.2, -0.8) * mm});
            skLineSegment(sketch, "E443", {"start": v(1.2, -0.8) * mm, "end": v(1.2, -0.8) * mm});
            skLineSegment(sketch, "E444", {"start": v(1.2, -0.8) * mm, "end": v(1.21, -0.8) * mm});
            skLineSegment(sketch, "E445", {"start": v(1.21, -0.8) * mm, "end": v(1.22, -0.8) * mm});
            skLineSegment(sketch, "E446", {"start": v(1.22, -0.8) * mm, "end": v(1.22, -0.8) * mm});
            skLineSegment(sketch, "E447", {"start": v(1.22, -0.8) * mm, "end": v(1.23, -0.8) * mm});
            skLineSegment(sketch, "E448", {"start": v(1.23, -0.8) * mm, "end": v(1.23, -0.8) * mm});
            skLineSegment(sketch, "E449", {"start": v(1.23, -0.8) * mm, "end": v(1.24, -0.8) * mm});
            skLineSegment(sketch, "E450", {"start": v(1.24, -0.8) * mm, "end": v(1.24, -0.8) * mm});
            skLineSegment(sketch, "E451", {"start": v(1.24, -0.8) * mm, "end": v(1.25, -0.81) * mm});
            skLineSegment(sketch, "E452", {"start": v(1.25, -0.81) * mm, "end": v(1.25, -0.82) * mm});
            skLineSegment(sketch, "E453", {"start": v(1.25, -0.82) * mm, "end": v(1.25, -0.82) * mm});
            skLineSegment(sketch, "E454", {"start": v(1.25, -0.82) * mm, "end": v(1.26, -0.83) * mm});
            skLineSegment(sketch, "E455", {"start": v(1.26, -0.83) * mm, "end": v(1.26, -0.83) * mm});
            skLineSegment(sketch, "E456", {"start": v(1.26, -0.83) * mm, "end": v(1.26, -0.84) * mm});
            skLineSegment(sketch, "E457", {"start": v(1.26, -0.84) * mm, "end": v(1.26, -0.84) * mm});
            skLineSegment(sketch, "E458", {"start": v(1.26, -0.84) * mm, "end": v(1.26, -0.85) * mm});
            skLineSegment(sketch, "E459", {"start": v(1.26, -0.85) * mm, "end": v(1.26, -0.85) * mm});
            skLineSegment(sketch, "E460", {"start": v(1.26, -0.85) * mm, "end": v(1.26, -0.86) * mm});
            skLineSegment(sketch, "E461", {"start": v(1.26, -0.86) * mm, "end": v(1.26, -0.86) * mm});
            skLineSegment(sketch, "E462", {"start": v(1.26, -0.86) * mm, "end": v(1.26, -0.87) * mm});
            skLineSegment(sketch, "E463", {"start": v(1.26, -0.87) * mm, "end": v(1.26, -0.87) * mm});
            skLineSegment(sketch, "E464", {"start": v(1.26, -0.87) * mm, "end": v(1.25, -0.88) * mm});
            skLineSegment(sketch, "E465", {"start": v(1.25, -0.88) * mm, "end": v(1.25, -0.88) * mm});
            skLineSegment(sketch, "E466", {"start": v(1.25, -0.88) * mm, "end": v(1.25, -0.89) * mm});
            skLineSegment(sketch, "E467", {"start": v(1.25, -0.89) * mm, "end": v(1.24, -0.9) * mm});
            skLineSegment(sketch, "E468", {"start": v(1.24, -0.9) * mm, "end": v(1.24, -0.9) * mm});
            skLineSegment(sketch, "E469", {"start": v(1.24, -0.9) * mm, "end": v(1.23, -0.9) * mm});
            skLineSegment(sketch, "E470", {"start": v(1.23, -0.9) * mm, "end": v(1.23, -0.9) * mm});
            skLineSegment(sketch, "E471", {"start": v(1.23, -0.9) * mm, "end": v(1.22, -0.9) * mm});
            skLineSegment(sketch, "E472", {"start": v(1.22, -0.9) * mm, "end": v(1.22, -0.9) * mm});
            skLineSegment(sketch, "E473", {"start": v(1.22, -0.9) * mm, "end": v(1.21, -0.9) * mm});
            skLineSegment(sketch, "E474", {"start": v(1.21, -0.9) * mm, "end": v(1.2, -0.9) * mm});
            skLineSegment(sketch, "E475", {"start": v(1.2, -0.9) * mm, "end": v(1.2, -0.9) * mm});
            skLineSegment(sketch, "E476", {"start": v(1.2, -0.9) * mm, "end": v(1.19, -0.9) * mm});
            skLineSegment(sketch, "E477", {"start": v(1.19, -0.9) * mm, "end": v(1.18, -0.9) * mm});
            skLineSegment(sketch, "E478", {"start": v(1.18, -0.9) * mm, "end": v(1.18, -0.9) * mm});
            skLineSegment(sketch, "E479", {"start": v(1.18, -0.9) * mm, "end": v(1.17, -0.9) * mm});
            skLineSegment(sketch, "E480", {"start": v(1.17, -0.9) * mm, "end": v(1.17, -0.9) * mm});
            skLineSegment(sketch, "E481", {"start": v(1.17, -0.9) * mm, "end": v(1.16, -0.9) * mm});
            skLineSegment(sketch, "E482", {"start": v(1.16, -0.9) * mm, "end": v(1.16, -0.9) * mm});
            skLineSegment(sketch, "E483", {"start": v(1.16, -0.9) * mm, "end": v(1.16, -0.89) * mm});
            skLineSegment(sketch, "E484", {"start": v(1.16, -0.89) * mm, "end": v(1.15, -0.89) * mm});
            skLineSegment(sketch, "E485", {"start": v(1.15, -0.89) * mm, "end": v(1.15, -0.88) * mm});
            skLineSegment(sketch, "E486", {"start": v(1.15, -0.88) * mm, "end": v(1.15, -0.88) * mm});
            skLineSegment(sketch, "E487", {"start": v(1.15, -0.88) * mm, "end": v(1.15, -0.87) * mm});
            skLineSegment(sketch, "E488", {"start": v(1.15, -0.87) * mm, "end": v(1.14, -0.87) * mm});
            skLineSegment(sketch, "E489", {"start": v(1.14, -0.87) * mm, "end": v(1.14, -0.86) * mm});
            skLineSegment(sketch, "E490", {"start": v(1.14, -0.86) * mm, "end": v(1.14, -0.86) * mm});
            skLineSegment(sketch, "E491", {"start": v(1.14, -0.86) * mm, "end": v(1.14, -0.85) * mm});
            skLineSegment(sketch, "E492", {"start": v(1.4, -0.82) * mm, "end": v(1.41, -0.83) * mm});
            skLineSegment(sketch, "E493", {"start": v(1.4, -0.82) * mm, "end": v(1.4, -0.8) * mm});
            skLineSegment(sketch, "E494", {"start": v(1.4, -0.8) * mm, "end": v(1.41, -0.8) * mm});
            skLineSegment(sketch, "E495", {"start": v(1.41, -0.8) * mm, "end": v(1.42, -0.8) * mm});
            skLineSegment(sketch, "E496", {"start": v(1.42, -0.8) * mm, "end": v(1.45, -0.83) * mm});
            skLineSegment(sketch, "E497", {"start": v(1.45, -0.83) * mm, "end": v(1.45, -0.8) * mm});
            skLineSegment(sketch, "E498", {"start": v(1.44, -0.78) * mm, "end": v(1.45, -0.77) * mm});
            skLineSegment(sketch, "E499", {"start": v(1.45, -0.77) * mm, "end": v(1.45, -0.76) * mm});
            skLineSegment(sketch, "E500", {"start": v(1.45, -0.76) * mm, "end": v(1.44, -0.75) * mm});
            skLineSegment(sketch, "E501", {"start": v(1.44, -0.75) * mm, "end": v(1.43, -0.75) * mm});
            skLineSegment(sketch, "E502", {"start": v(1.43, -0.75) * mm, "end": v(1.43, -0.76) * mm});
            skLineSegment(sketch, "E503", {"start": v(1.43, -0.76) * mm, "end": v(1.43, -0.77) * mm});
            skLineSegment(sketch, "E504", {"start": v(1.43, -0.76) * mm, "end": v(1.42, -0.75) * mm});
            skLineSegment(sketch, "E505", {"start": v(1.42, -0.75) * mm, "end": v(1.41, -0.75) * mm});
            skLineSegment(sketch, "E506", {"start": v(1.41, -0.75) * mm, "end": v(1.4, -0.76) * mm});
            skLineSegment(sketch, "E507", {"start": v(1.4, -0.76) * mm, "end": v(1.4, -0.77) * mm});
            skLineSegment(sketch, "E508", {"start": v(1.4, -0.77) * mm, "end": v(1.41, -0.78) * mm});
            skLineSegment(sketch, "E509", {"start": v(1.41, -0.73) * mm, "end": v(1.4, -0.73) * mm});
            skLineSegment(sketch, "E510", {"start": v(1.4, -0.73) * mm, "end": v(1.4, -0.71) * mm});
            skLineSegment(sketch, "E511", {"start": v(1.4, -0.71) * mm, "end": v(1.41, -0.7) * mm});
            skLineSegment(sketch, "E512", {"start": v(1.41, -0.7) * mm, "end": v(1.44, -0.73) * mm});
            skLineSegment(sketch, "E513", {"start": v(1.44, -0.73) * mm, "end": v(1.45, -0.73) * mm});
            skLineSegment(sketch, "E514", {"start": v(1.45, -0.73) * mm, "end": v(1.45, -0.71) * mm});
            skLineSegment(sketch, "E515", {"start": v(1.45, -0.71) * mm, "end": v(1.44, -0.7) * mm});
            skLineSegment(sketch, "E516", {"start": v(1.44, -0.7) * mm, "end": v(1.41, -0.7) * mm});
            skLineSegment(sketch, "E517", {"start": v(1.4, -0.69) * mm, "end": v(1.43, -0.69) * mm});
            skLineSegment(sketch, "E518", {"start": v(1.43, -0.69) * mm, "end": v(1.45, -0.67) * mm});
            skLineSegment(sketch, "E519", {"start": v(1.45, -0.67) * mm, "end": v(1.43, -0.66) * mm});
            skLineSegment(sketch, "E520", {"start": v(1.43, -0.66) * mm, "end": v(1.4, -0.66) * mm});
            skLineSegment(sketch, "E521", {"start": v(1.41, -0.73) * mm, "end": v(1.44, -0.73) * mm});
            skLineSegment(sketch, "E522", {"start": v(1.53, -0.25) * mm, "end": v(1.5, -0.23) * mm});
            skLineSegment(sketch, "E523", {"start": v(1.5, -0.23) * mm, "end": v(1.5, -0.18) * mm});
            skLineSegment(sketch, "E524", {"start": v(1.5, -0.18) * mm, "end": v(1.53, -0.15) * mm});
            skLineSegment(sketch, "E525", {"start": v(1.53, -0.15) * mm, "end": v(1.5, -0.13) * mm});
            skLineSegment(sketch, "E526", {"start": v(1.5, -0.13) * mm, "end": v(1.5, -0.08) * mm});
            skLineSegment(sketch, "E527", {"start": v(1.5, -0.08) * mm, "end": v(1.53, -0.05) * mm});
            skLineSegment(sketch, "E528", {"start": v(1.53, -0.05) * mm, "end": v(1.5, -0.03) * mm});
            skLineSegment(sketch, "E529", {"start": v(1.5, -0.03) * mm, "end": v(1.5, 0.02) * mm});
            skLineSegment(sketch, "E530", {"start": v(1.5, 0.02) * mm, "end": v(1.53, 0.05) * mm});
            skLineSegment(sketch, "E531", {"start": v(1.53, 0.05) * mm, "end": v(1.5, 0.07) * mm});
            skLineSegment(sketch, "E532", {"start": v(1.5, 0.07) * mm, "end": v(1.5, 0.12) * mm});
            skLineSegment(sketch, "E533", {"start": v(1.5, 0.12) * mm, "end": v(1.53, 0.15) * mm});
            skLineSegment(sketch, "E534", {"start": v(1.53, 0.15) * mm, "end": v(1.5, 0.17) * mm});
            skLineSegment(sketch, "E535", {"start": v(1.5, 0.17) * mm, "end": v(1.5, 0.22) * mm});
            skLineSegment(sketch, "E536", {"start": v(1.5, 0.22) * mm, "end": v(1.53, 0.25) * mm});
            skLineSegment(sketch, "E537", {"start": v(1.53, 0.25) * mm, "end": v(1.68, 0.25) * mm});
            skLineSegment(sketch, "E538", {"start": v(1.68, 0.25) * mm, "end": v(1.7, 0.22) * mm});
            skLineSegment(sketch, "E539", {"start": v(1.7, 0.22) * mm, "end": v(1.7, 0.17) * mm});
            skLineSegment(sketch, "E540", {"start": v(1.7, 0.17) * mm, "end": v(1.68, 0.15) * mm});
            skLineSegment(sketch, "E541", {"start": v(1.68, 0.15) * mm, "end": v(1.7, 0.12) * mm});
            skLineSegment(sketch, "E542", {"start": v(1.7, 0.12) * mm, "end": v(1.7, 0.07) * mm});
            skLineSegment(sketch, "E543", {"start": v(1.7, 0.07) * mm, "end": v(1.68, 0.05) * mm});
            skLineSegment(sketch, "E544", {"start": v(1.68, 0.05) * mm, "end": v(1.7, 0.02) * mm});
            skLineSegment(sketch, "E545", {"start": v(1.7, 0.02) * mm, "end": v(1.7, -0.03) * mm});
            skLineSegment(sketch, "E546", {"start": v(1.7, -0.03) * mm, "end": v(1.68, -0.05) * mm});
            skLineSegment(sketch, "E547", {"start": v(1.68, -0.05) * mm, "end": v(1.7, -0.08) * mm});
            skLineSegment(sketch, "E548", {"start": v(1.7, -0.08) * mm, "end": v(1.7, -0.13) * mm});
            skLineSegment(sketch, "E549", {"start": v(1.7, -0.13) * mm, "end": v(1.68, -0.15) * mm});
            skLineSegment(sketch, "E550", {"start": v(1.68, -0.15) * mm, "end": v(1.7, -0.18) * mm});
            skLineSegment(sketch, "E551", {"start": v(1.7, -0.18) * mm, "end": v(1.7, -0.23) * mm});
            skLineSegment(sketch, "E552", {"start": v(1.7, -0.23) * mm, "end": v(1.68, -0.25) * mm});
            skLineSegment(sketch, "E553", {"start": v(1.68, -0.25) * mm, "end": v(1.53, -0.25) * mm});
            skLineSegment(sketch, "E554", {"start": v(1.74, -0.1) * mm, "end": v(1.74, -0.08) * mm});
            skLineSegment(sketch, "E555", {"start": v(1.74, -0.08) * mm, "end": v(1.75, -0.08) * mm});
            skLineSegment(sketch, "E556", {"start": v(1.75, -0.08) * mm, "end": v(1.76, -0.08) * mm});
            skLineSegment(sketch, "E557", {"start": v(1.76, -0.08) * mm, "end": v(1.77, -0.08) * mm});
            skLineSegment(sketch, "E558", {"start": v(1.77, -0.08) * mm, "end": v(1.77, -0.1) * mm});
            skLineSegment(sketch, "E559", {"start": v(1.79, -0.1) * mm, "end": v(1.74, -0.1) * mm});
            skLineSegment(sketch, "E560", {"start": v(1.77, -0.1) * mm, "end": v(1.79, -0.08) * mm});
            skLineSegment(sketch, "E561", {"start": v(1.78, -0.06) * mm, "end": v(1.79, -0.05) * mm});
            skLineSegment(sketch, "E562", {"start": v(1.79, -0.05) * mm, "end": v(1.79, -0.04) * mm});
            skLineSegment(sketch, "E563", {"start": v(1.79, -0.04) * mm, "end": v(1.78, -0.03) * mm});
            skLineSegment(sketch, "E564", {"start": v(1.78, -0.03) * mm, "end": v(1.77, -0.03) * mm});
            skLineSegment(sketch, "E565", {"start": v(1.77, -0.03) * mm, "end": v(1.76, -0.04) * mm});
            skLineSegment(sketch, "E566", {"start": v(1.76, -0.04) * mm, "end": v(1.76, -0.05) * mm});
            skLineSegment(sketch, "E567", {"start": v(1.76, -0.05) * mm, "end": v(1.76, -0.06) * mm});
            skLineSegment(sketch, "E568", {"start": v(1.76, -0.06) * mm, "end": v(1.75, -0.06) * mm});
            skLineSegment(sketch, "E569", {"start": v(1.75, -0.06) * mm, "end": v(1.74, -0.05) * mm});
            skLineSegment(sketch, "E570", {"start": v(1.74, -0.05) * mm, "end": v(1.74, -0.04) * mm});
            skLineSegment(sketch, "E571", {"start": v(1.74, -0.04) * mm, "end": v(1.75, -0.03) * mm});
            skLineSegment(sketch, "E572", {"start": v(1.75, -0.01) * mm, "end": v(1.74, 0) * mm});
            skLineSegment(sketch, "E573", {"start": v(1.74, 0) * mm, "end": v(1.74, 0) * mm});
            skLineSegment(sketch, "E574", {"start": v(1.74, 0) * mm, "end": v(1.75, 0.01) * mm});
            skLineSegment(sketch, "E575", {"start": v(1.75, 0.01) * mm, "end": v(1.76, 0.01) * mm});
            skLineSegment(sketch, "E576", {"start": v(1.76, 0.01) * mm, "end": v(1.79, -0.01) * mm});
            skLineSegment(sketch, "E577", {"start": v(1.79, -0.01) * mm, "end": v(1.79, 0.01) * mm});
            skLineSegment(sketch, "E578", {"start": v(1.78, 0.03) * mm, "end": v(1.79, 0.04) * mm});
            skLineSegment(sketch, "E579", {"start": v(1.79, 0.04) * mm, "end": v(1.79, 0.05) * mm});
            skLineSegment(sketch, "E580", {"start": v(1.79, 0.05) * mm, "end": v(1.78, 0.06) * mm});
            skLineSegment(sketch, "E581", {"start": v(1.78, 0.06) * mm, "end": v(1.77, 0.06) * mm});
            skLineSegment(sketch, "E582", {"start": v(1.77, 0.06) * mm, "end": v(1.76, 0.05) * mm});
            skLineSegment(sketch, "E583", {"start": v(1.76, 0.05) * mm, "end": v(1.76, 0.05) * mm});
            skLineSegment(sketch, "E584", {"start": v(1.76, 0.05) * mm, "end": v(1.76, 0.06) * mm});
            skLineSegment(sketch, "E585", {"start": v(1.76, 0.06) * mm, "end": v(1.75, 0.06) * mm});
            skLineSegment(sketch, "E586", {"start": v(1.75, 0.06) * mm, "end": v(1.74, 0.05) * mm});
            skLineSegment(sketch, "E587", {"start": v(1.74, 0.05) * mm, "end": v(1.74, 0.04) * mm});
            skLineSegment(sketch, "E588", {"start": v(1.74, 0.04) * mm, "end": v(1.75, 0.03) * mm});
            skLineSegment(sketch, "E589", {"start": v(1.75, 0.08) * mm, "end": v(1.74, 0.08) * mm});
            skLineSegment(sketch, "E590", {"start": v(1.74, 0.08) * mm, "end": v(1.74, 0.1) * mm});
            skLineSegment(sketch, "E591", {"start": v(1.74, 0.1) * mm, "end": v(1.75, 0.1) * mm});
            skLineSegment(sketch, "E592", {"start": v(1.75, 0.1) * mm, "end": v(1.76, 0.1) * mm});
            skLineSegment(sketch, "E593", {"start": v(1.76, 0.1) * mm, "end": v(1.79, 0.08) * mm});
            skLineSegment(sketch, "E594", {"start": v(1.79, 0.08) * mm, "end": v(1.79, 0.1) * mm});
            skLineSegment(sketch, "E595", {"start": v(1.4, 0.78) * mm, "end": v(1.4, 0.86) * mm});
            skLineSegment(sketch, "E596", {"start": v(1.4, 0.86) * mm, "end": v(1.4, 0.86) * mm});
            skLineSegment(sketch, "E597", {"start": v(1.4, 0.86) * mm, "end": v(1.39, 0.86) * mm});
            skLineSegment(sketch, "E598", {"start": v(1.39, 0.86) * mm, "end": v(1.38, 0.86) * mm});
            skLineSegment(sketch, "E599", {"start": v(1.38, 0.86) * mm, "end": v(1.38, 0.86) * mm});
            skLineSegment(sketch, "E600", {"start": v(1.38, 0.86) * mm, "end": v(1.38, 0.87) * mm});
            skLineSegment(sketch, "E601", {"start": v(1.38, 0.87) * mm, "end": v(1.37, 0.87) * mm});
            skLineSegment(sketch, "E602", {"start": v(1.37, 0.87) * mm, "end": v(1.37, 0.87) * mm});
            skLineSegment(sketch, "E603", {"start": v(1.37, 0.87) * mm, "end": v(1.37, 0.88) * mm});
            skLineSegment(sketch, "E604", {"start": v(1.37, 0.88) * mm, "end": v(1.36, 0.88) * mm});
            skLineSegment(sketch, "E605", {"start": v(1.36, 0.88) * mm, "end": v(1.36, 0.88) * mm});
            skLineSegment(sketch, "E606", {"start": v(1.36, 0.88) * mm, "end": v(1.36, 0.89) * mm});
            skLineSegment(sketch, "E607", {"start": v(1.36, 0.89) * mm, "end": v(1.36, 0.9) * mm});
            skLineSegment(sketch, "E608", {"start": v(1.36, 0.9) * mm, "end": v(1.36, 0.9) * mm});
            skLineSegment(sketch, "E609", {"start": v(1.36, 0.9) * mm, "end": v(1.36, 0.91) * mm});
            skLineSegment(sketch, "E610", {"start": v(1.36, 0.91) * mm, "end": v(1.36, 0.92) * mm});
            skLineSegment(sketch, "E611", {"start": v(1.36, 0.92) * mm, "end": v(1.36, 0.92) * mm});
            skLineSegment(sketch, "E612", {"start": v(1.36, 0.92) * mm, "end": v(1.37, 0.92) * mm});
            skLineSegment(sketch, "E613", {"start": v(1.37, 0.92) * mm, "end": v(1.37, 0.93) * mm});
            skLineSegment(sketch, "E614", {"start": v(1.37, 0.93) * mm, "end": v(1.37, 0.93) * mm});
            skLineSegment(sketch, "E615", {"start": v(1.37, 0.93) * mm, "end": v(1.38, 0.93) * mm});
            skLineSegment(sketch, "E616", {"start": v(1.38, 0.93) * mm, "end": v(1.38, 0.94) * mm});
            skLineSegment(sketch, "E617", {"start": v(1.38, 0.94) * mm, "end": v(1.38, 0.94) * mm});
            skLineSegment(sketch, "E618", {"start": v(1.38, 0.94) * mm, "end": v(1.39, 0.94) * mm});
            skLineSegment(sketch, "E619", {"start": v(1.39, 0.94) * mm, "end": v(1.4, 0.94) * mm});
            skLineSegment(sketch, "E620", {"start": v(1.4, 0.94) * mm, "end": v(1.4, 0.94) * mm});
            skLineSegment(sketch, "E621", {"start": v(1.4, 0.94) * mm, "end": v(1.4, 1.01) * mm});
            skLineSegment(sketch, "E622", {"start": v(1.4, 1.01) * mm, "end": v(0.6, 1.01) * mm});
            skLineSegment(sketch, "E623", {"start": v(0.6, 1.01) * mm, "end": v(0.6, 0.78) * mm});
            skLineSegment(sketch, "E624", {"start": v(0.6, 0.78) * mm, "end": v(1.4, 0.78) * mm});
            skLineSegment(sketch, "E625", {"start": v(1.32, 1.13) * mm, "end": v(1.32, 1.15) * mm});
            skLineSegment(sketch, "E626", {"start": v(1.33, 1.14) * mm, "end": v(1.31, 1.14) * mm});
            skLineSegment(sketch, "E627", {"start": v(1.31, 1.16) * mm, "end": v(1.33, 1.16) * mm});
            skLineSegment(sketch, "E628", {"start": v(1.33, 1.16) * mm, "end": v(1.33, 1.2) * mm});
            skLineSegment(sketch, "E629", {"start": v(1.33, 1.2) * mm, "end": v(1.33, 1.24) * mm});
            skLineSegment(sketch, "E630", {"start": v(1.33, 1.24) * mm, "end": v(1.31, 1.24) * mm});
            skLineSegment(sketch, "E631", {"start": v(1.31, 1.24) * mm, "end": v(1.31, 1.16) * mm});
            skLineSegment(sketch, "E632", {"start": v(1.28, 1.14) * mm, "end": v(1.26, 1.14) * mm});
            skLineSegment(sketch, "E633", {"start": v(1.28, 1.2) * mm, "end": v(1.24, 1.2) * mm});
            skLineSegment(sketch, "E634", {"start": v(1.22, 1.2) * mm, "end": v(1.22, 1.2) * mm});
            skLineSegment(sketch, "E635", {"start": v(1.22, 1.2) * mm, "end": v(1.22, 1.21) * mm});
            skLineSegment(sketch, "E636", {"start": v(1.22, 1.21) * mm, "end": v(1.22, 1.22) * mm});
            skLineSegment(sketch, "E637", {"start": v(1.22, 1.22) * mm, "end": v(1.22, 1.22) * mm});
            skLineSegment(sketch, "E638", {"start": v(1.22, 1.22) * mm, "end": v(1.22, 1.23) * mm});
            skLineSegment(sketch, "E639", {"start": v(1.22, 1.23) * mm, "end": v(1.22, 1.23) * mm});
            skLineSegment(sketch, "E640", {"start": v(1.22, 1.23) * mm, "end": v(1.22, 1.24) * mm});
            skLineSegment(sketch, "E641", {"start": v(1.22, 1.24) * mm, "end": v(1.23, 1.24) * mm});
            skLineSegment(sketch, "E642", {"start": v(1.23, 1.24) * mm, "end": v(1.23, 1.25) * mm});
            skLineSegment(sketch, "E643", {"start": v(1.23, 1.25) * mm, "end": v(1.23, 1.25) * mm});
            skLineSegment(sketch, "E644", {"start": v(1.23, 1.25) * mm, "end": v(1.24, 1.26) * mm});
            skLineSegment(sketch, "E645", {"start": v(1.24, 1.26) * mm, "end": v(1.24, 1.26) * mm});
            skLineSegment(sketch, "E646", {"start": v(1.24, 1.26) * mm, "end": v(1.25, 1.27) * mm});
            skLineSegment(sketch, "E647", {"start": v(1.25, 1.27) * mm, "end": v(1.25, 1.27) * mm});
            skLineSegment(sketch, "E648", {"start": v(1.25, 1.27) * mm, "end": v(1.26, 1.27) * mm});
            skLineSegment(sketch, "E649", {"start": v(1.26, 1.27) * mm, "end": v(1.26, 1.28) * mm});
            skLineSegment(sketch, "E650", {"start": v(1.26, 1.28) * mm, "end": v(1.27, 1.28) * mm});
            skLineSegment(sketch, "E651", {"start": v(1.27, 1.28) * mm, "end": v(1.27, 1.28) * mm});
            skLineSegment(sketch, "E652", {"start": v(1.27, 1.28) * mm, "end": v(1.28, 1.28) * mm});
            skLineSegment(sketch, "E653", {"start": v(1.28, 1.28) * mm, "end": v(1.28, 1.28) * mm});
            skLineSegment(sketch, "E654", {"start": v(1.28, 1.28) * mm, "end": v(1.29, 1.28) * mm});
            skLineSegment(sketch, "E655", {"start": v(1.29, 1.28) * mm, "end": v(1.3, 1.28) * mm});
            skLineSegment(sketch, "E656", {"start": v(1.3, 1.28) * mm, "end": v(1.3, 1.28) * mm});
            skLineSegment(sketch, "E657", {"start": v(1.3, 1.28) * mm, "end": v(1.31, 1.28) * mm});
            skLineSegment(sketch, "E658", {"start": v(1.31, 1.28) * mm, "end": v(1.32, 1.28) * mm});
            skLineSegment(sketch, "E659", {"start": v(1.32, 1.28) * mm, "end": v(1.32, 1.28) * mm});
            skLineSegment(sketch, "E660", {"start": v(1.32, 1.28) * mm, "end": v(1.33, 1.28) * mm});
            skLineSegment(sketch, "E661", {"start": v(1.33, 1.28) * mm, "end": v(1.33, 1.28) * mm});
            skLineSegment(sketch, "E662", {"start": v(1.33, 1.28) * mm, "end": v(1.34, 1.28) * mm});
            skLineSegment(sketch, "E663", {"start": v(1.34, 1.28) * mm, "end": v(1.34, 1.27) * mm});
            skLineSegment(sketch, "E664", {"start": v(1.34, 1.27) * mm, "end": v(1.35, 1.27) * mm});
            skLineSegment(sketch, "E665", {"start": v(1.35, 1.27) * mm, "end": v(1.35, 1.27) * mm});
            skLineSegment(sketch, "E666", {"start": v(1.35, 1.27) * mm, "end": v(1.36, 1.26) * mm});
            skLineSegment(sketch, "E667", {"start": v(1.36, 1.26) * mm, "end": v(1.36, 1.26) * mm});
            skLineSegment(sketch, "E668", {"start": v(1.36, 1.26) * mm, "end": v(1.37, 1.25) * mm});
            skLineSegment(sketch, "E669", {"start": v(1.37, 1.25) * mm, "end": v(1.37, 1.25) * mm});
            skLineSegment(sketch, "E670", {"start": v(1.37, 1.25) * mm, "end": v(1.37, 1.24) * mm});
            skLineSegment(sketch, "E671", {"start": v(1.37, 1.24) * mm, "end": v(1.38, 1.24) * mm});
            skLineSegment(sketch, "E672", {"start": v(1.38, 1.24) * mm, "end": v(1.38, 1.23) * mm});
            skLineSegment(sketch, "E673", {"start": v(1.38, 1.23) * mm, "end": v(1.38, 1.23) * mm});
            skLineSegment(sketch, "E674", {"start": v(1.38, 1.23) * mm, "end": v(1.38, 1.22) * mm});
            skLineSegment(sketch, "E675", {"start": v(1.38, 1.22) * mm, "end": v(1.38, 1.22) * mm});
            skLineSegment(sketch, "E676", {"start": v(1.38, 1.22) * mm, "end": v(1.38, 1.21) * mm});
            skLineSegment(sketch, "E677", {"start": v(1.38, 1.21) * mm, "end": v(1.38, 1.2) * mm});
            skLineSegment(sketch, "E678", {"start": v(1.38, 1.2) * mm, "end": v(1.39, 1.2) * mm});
            skLineSegment(sketch, "E679", {"start": v(1.39, 1.2) * mm, "end": v(1.38, 1.2) * mm});
            skLineSegment(sketch, "E680", {"start": v(1.38, 1.2) * mm, "end": v(1.38, 1.19) * mm});
            skLineSegment(sketch, "E681", {"start": v(1.38, 1.19) * mm, "end": v(1.38, 1.18) * mm});
            skLineSegment(sketch, "E682", {"start": v(1.38, 1.18) * mm, "end": v(1.38, 1.18) * mm});
            skLineSegment(sketch, "E683", {"start": v(1.38, 1.18) * mm, "end": v(1.38, 1.17) * mm});
            skLineSegment(sketch, "E684", {"start": v(1.38, 1.17) * mm, "end": v(1.38, 1.17) * mm});
            skLineSegment(sketch, "E685", {"start": v(1.38, 1.17) * mm, "end": v(1.38, 1.16) * mm});
            skLineSegment(sketch, "E686", {"start": v(1.38, 1.16) * mm, "end": v(1.37, 1.16) * mm});
            skLineSegment(sketch, "E687", {"start": v(1.37, 1.16) * mm, "end": v(1.37, 1.15) * mm});
            skLineSegment(sketch, "E688", {"start": v(1.37, 1.15) * mm, "end": v(1.37, 1.15) * mm});
            skLineSegment(sketch, "E689", {"start": v(1.37, 1.15) * mm, "end": v(1.36, 1.14) * mm});
            skLineSegment(sketch, "E690", {"start": v(1.36, 1.14) * mm, "end": v(1.36, 1.14) * mm});
            skLineSegment(sketch, "E691", {"start": v(1.36, 1.14) * mm, "end": v(1.35, 1.13) * mm});
            skLineSegment(sketch, "E692", {"start": v(1.35, 1.13) * mm, "end": v(1.35, 1.13) * mm});
            skLineSegment(sketch, "E693", {"start": v(1.35, 1.13) * mm, "end": v(1.34, 1.13) * mm});
            skLineSegment(sketch, "E694", {"start": v(1.34, 1.13) * mm, "end": v(1.34, 1.12) * mm});
            skLineSegment(sketch, "E695", {"start": v(1.34, 1.12) * mm, "end": v(1.33, 1.12) * mm});
            skLineSegment(sketch, "E696", {"start": v(1.33, 1.12) * mm, "end": v(1.33, 1.12) * mm});
            skLineSegment(sketch, "E697", {"start": v(1.33, 1.12) * mm, "end": v(1.32, 1.12) * mm});
            skLineSegment(sketch, "E698", {"start": v(1.32, 1.12) * mm, "end": v(1.32, 1.12) * mm});
            skLineSegment(sketch, "E699", {"start": v(1.32, 1.12) * mm, "end": v(1.31, 1.12) * mm});
            skLineSegment(sketch, "E700", {"start": v(1.31, 1.12) * mm, "end": v(1.3, 1.12) * mm});
            skLineSegment(sketch, "E701", {"start": v(1.3, 1.12) * mm, "end": v(1.3, 1.11) * mm});
            skLineSegment(sketch, "E702", {"start": v(1.3, 1.11) * mm, "end": v(1.3, 1.12) * mm});
            skLineSegment(sketch, "E703", {"start": v(1.3, 1.12) * mm, "end": v(1.29, 1.12) * mm});
            skLineSegment(sketch, "E704", {"start": v(1.29, 1.12) * mm, "end": v(1.28, 1.12) * mm});
            skLineSegment(sketch, "E705", {"start": v(1.28, 1.12) * mm, "end": v(1.28, 1.12) * mm});
            skLineSegment(sketch, "E706", {"start": v(1.28, 1.12) * mm, "end": v(1.27, 1.12) * mm});
            skLineSegment(sketch, "E707", {"start": v(1.27, 1.12) * mm, "end": v(1.27, 1.12) * mm});
            skLineSegment(sketch, "E708", {"start": v(1.27, 1.12) * mm, "end": v(1.26, 1.12) * mm});
            skLineSegment(sketch, "E709", {"start": v(1.26, 1.12) * mm, "end": v(1.26, 1.13) * mm});
            skLineSegment(sketch, "E710", {"start": v(1.26, 1.13) * mm, "end": v(1.25, 1.13) * mm});
            skLineSegment(sketch, "E711", {"start": v(1.25, 1.13) * mm, "end": v(1.25, 1.13) * mm});
            skLineSegment(sketch, "E712", {"start": v(1.25, 1.13) * mm, "end": v(1.24, 1.14) * mm});
            skLineSegment(sketch, "E713", {"start": v(1.24, 1.14) * mm, "end": v(1.24, 1.14) * mm});
            skLineSegment(sketch, "E714", {"start": v(1.24, 1.14) * mm, "end": v(1.23, 1.15) * mm});
            skLineSegment(sketch, "E715", {"start": v(1.23, 1.15) * mm, "end": v(1.23, 1.15) * mm});
            skLineSegment(sketch, "E716", {"start": v(1.23, 1.15) * mm, "end": v(1.23, 1.16) * mm});
            skLineSegment(sketch, "E717", {"start": v(1.23, 1.16) * mm, "end": v(1.22, 1.16) * mm});
            skLineSegment(sketch, "E718", {"start": v(1.22, 1.16) * mm, "end": v(1.22, 1.17) * mm});
            skLineSegment(sketch, "E719", {"start": v(1.22, 1.17) * mm, "end": v(1.22, 1.17) * mm});
            skLineSegment(sketch, "E720", {"start": v(1.22, 1.17) * mm, "end": v(1.22, 1.18) * mm});
            skLineSegment(sketch, "E721", {"start": v(1.22, 1.18) * mm, "end": v(1.22, 1.18) * mm});
            skLineSegment(sketch, "E722", {"start": v(1.22, 1.18) * mm, "end": v(1.22, 1.19) * mm});
            skLineSegment(sketch, "E723", {"start": v(1.22, 1.19) * mm, "end": v(1.22, 1.2) * mm});
            skLineSegment(sketch, "E724", {"start": v(1.16, 1.2) * mm, "end": v(1.13, 1.2) * mm});
            skLineSegment(sketch, "E725", {"start": v(1.13, 1.2) * mm, "end": v(1.13, 1.16) * mm});
            skLineSegment(sketch, "E726", {"start": v(1.13, 1.16) * mm, "end": v(1.11, 1.16) * mm});
            skLineSegment(sketch, "E727", {"start": v(1.11, 1.16) * mm, "end": v(1.11, 1.24) * mm});
            skLineSegment(sketch, "E728", {"start": v(1.11, 1.24) * mm, "end": v(1.13, 1.24) * mm});
            skLineSegment(sketch, "E729", {"start": v(1.13, 1.24) * mm, "end": v(1.13, 1.2) * mm});
            skLineSegment(sketch, "E730", {"start": v(1.01, 1.2) * mm, "end": v(1.02, 1.2) * mm});
            skLineSegment(sketch, "E731", {"start": v(1.02, 1.2) * mm, "end": v(1.02, 1.21) * mm});
            skLineSegment(sketch, "E732", {"start": v(1.02, 1.21) * mm, "end": v(1.02, 1.22) * mm});
            skLineSegment(sketch, "E733", {"start": v(1.02, 1.22) * mm, "end": v(1.02, 1.22) * mm});
            skLineSegment(sketch, "E734", {"start": v(1.02, 1.22) * mm, "end": v(1.02, 1.23) * mm});
            skLineSegment(sketch, "E735", {"start": v(1.02, 1.23) * mm, "end": v(1.02, 1.23) * mm});
            skLineSegment(sketch, "E736", {"start": v(1.02, 1.23) * mm, "end": v(1.02, 1.24) * mm});
            skLineSegment(sketch, "E737", {"start": v(1.02, 1.24) * mm, "end": v(1.03, 1.24) * mm});
            skLineSegment(sketch, "E738", {"start": v(1.03, 1.24) * mm, "end": v(1.03, 1.25) * mm});
            skLineSegment(sketch, "E739", {"start": v(1.03, 1.25) * mm, "end": v(1.03, 1.25) * mm});
            skLineSegment(sketch, "E740", {"start": v(1.03, 1.25) * mm, "end": v(1.04, 1.26) * mm});
            skLineSegment(sketch, "E741", {"start": v(1.04, 1.26) * mm, "end": v(1.04, 1.26) * mm});
            skLineSegment(sketch, "E742", {"start": v(1.04, 1.26) * mm, "end": v(1.05, 1.27) * mm});
            skLineSegment(sketch, "E743", {"start": v(1.05, 1.27) * mm, "end": v(1.05, 1.27) * mm});
            skLineSegment(sketch, "E744", {"start": v(1.05, 1.27) * mm, "end": v(1.06, 1.27) * mm});
            skLineSegment(sketch, "E745", {"start": v(1.06, 1.27) * mm, "end": v(1.06, 1.28) * mm});
            skLineSegment(sketch, "E746", {"start": v(1.06, 1.28) * mm, "end": v(1.07, 1.28) * mm});
            skLineSegment(sketch, "E747", {"start": v(1.07, 1.28) * mm, "end": v(1.07, 1.28) * mm});
            skLineSegment(sketch, "E748", {"start": v(1.07, 1.28) * mm, "end": v(1.08, 1.28) * mm});
            skLineSegment(sketch, "E749", {"start": v(1.08, 1.28) * mm, "end": v(1.08, 1.28) * mm});
            skLineSegment(sketch, "E750", {"start": v(1.08, 1.28) * mm, "end": v(1.09, 1.28) * mm});
            skLineSegment(sketch, "E751", {"start": v(1.09, 1.28) * mm, "end": v(1.1, 1.28) * mm});
            skLineSegment(sketch, "E752", {"start": v(1.1, 1.28) * mm, "end": v(1.1, 1.28) * mm});
            skLineSegment(sketch, "E753", {"start": v(1.1, 1.28) * mm, "end": v(1.11, 1.28) * mm});
            skLineSegment(sketch, "E754", {"start": v(1.11, 1.28) * mm, "end": v(1.12, 1.28) * mm});
            skLineSegment(sketch, "E755", {"start": v(1.12, 1.28) * mm, "end": v(1.12, 1.28) * mm});
            skLineSegment(sketch, "E756", {"start": v(1.12, 1.28) * mm, "end": v(1.13, 1.28) * mm});
            skLineSegment(sketch, "E757", {"start": v(1.13, 1.28) * mm, "end": v(1.13, 1.28) * mm});
            skLineSegment(sketch, "E758", {"start": v(1.13, 1.28) * mm, "end": v(1.14, 1.28) * mm});
            skLineSegment(sketch, "E759", {"start": v(1.14, 1.28) * mm, "end": v(1.14, 1.27) * mm});
            skLineSegment(sketch, "E760", {"start": v(1.14, 1.27) * mm, "end": v(1.15, 1.27) * mm});
            skLineSegment(sketch, "E761", {"start": v(1.15, 1.27) * mm, "end": v(1.15, 1.27) * mm});
            skLineSegment(sketch, "E762", {"start": v(1.15, 1.27) * mm, "end": v(1.16, 1.26) * mm});
            skLineSegment(sketch, "E763", {"start": v(1.16, 1.26) * mm, "end": v(1.16, 1.26) * mm});
            skLineSegment(sketch, "E764", {"start": v(1.16, 1.26) * mm, "end": v(1.17, 1.25) * mm});
            skLineSegment(sketch, "E765", {"start": v(1.17, 1.25) * mm, "end": v(1.17, 1.25) * mm});
            skLineSegment(sketch, "E766", {"start": v(1.17, 1.25) * mm, "end": v(1.17, 1.24) * mm});
            skLineSegment(sketch, "E767", {"start": v(1.17, 1.24) * mm, "end": v(1.18, 1.24) * mm});
            skLineSegment(sketch, "E768", {"start": v(1.18, 1.24) * mm, "end": v(1.18, 1.23) * mm});
            skLineSegment(sketch, "E769", {"start": v(1.18, 1.23) * mm, "end": v(1.18, 1.23) * mm});
            skLineSegment(sketch, "E770", {"start": v(1.18, 1.23) * mm, "end": v(1.18, 1.22) * mm});
            skLineSegment(sketch, "E771", {"start": v(1.18, 1.22) * mm, "end": v(1.18, 1.22) * mm});
            skLineSegment(sketch, "E772", {"start": v(1.18, 1.22) * mm, "end": v(1.18, 1.21) * mm});
            skLineSegment(sketch, "E773", {"start": v(1.18, 1.21) * mm, "end": v(1.18, 1.2) * mm});
            skLineSegment(sketch, "E774", {"start": v(1.18, 1.2) * mm, "end": v(1.18, 1.2) * mm});
            skLineSegment(sketch, "E775", {"start": v(1.18, 1.2) * mm, "end": v(1.18, 1.19) * mm});
            skLineSegment(sketch, "E776", {"start": v(1.18, 1.19) * mm, "end": v(1.18, 1.18) * mm});
            skLineSegment(sketch, "E777", {"start": v(1.18, 1.18) * mm, "end": v(1.18, 1.18) * mm});
            skLineSegment(sketch, "E778", {"start": v(1.18, 1.18) * mm, "end": v(1.18, 1.17) * mm});
            skLineSegment(sketch, "E779", {"start": v(1.18, 1.17) * mm, "end": v(1.18, 1.17) * mm});
            skLineSegment(sketch, "E780", {"start": v(1.18, 1.17) * mm, "end": v(1.18, 1.16) * mm});
            skLineSegment(sketch, "E781", {"start": v(1.18, 1.16) * mm, "end": v(1.17, 1.16) * mm});
            skLineSegment(sketch, "E782", {"start": v(1.17, 1.16) * mm, "end": v(1.17, 1.15) * mm});
            skLineSegment(sketch, "E783", {"start": v(1.17, 1.15) * mm, "end": v(1.17, 1.15) * mm});
            skLineSegment(sketch, "E784", {"start": v(1.17, 1.15) * mm, "end": v(1.16, 1.14) * mm});
            skLineSegment(sketch, "E785", {"start": v(1.16, 1.14) * mm, "end": v(1.16, 1.14) * mm});
            skLineSegment(sketch, "E786", {"start": v(1.16, 1.14) * mm, "end": v(1.15, 1.13) * mm});
            skLineSegment(sketch, "E787", {"start": v(1.15, 1.13) * mm, "end": v(1.15, 1.13) * mm});
            skLineSegment(sketch, "E788", {"start": v(1.15, 1.13) * mm, "end": v(1.14, 1.13) * mm});
            skLineSegment(sketch, "E789", {"start": v(1.14, 1.13) * mm, "end": v(1.14, 1.12) * mm});
            skLineSegment(sketch, "E790", {"start": v(1.14, 1.12) * mm, "end": v(1.13, 1.12) * mm});
            skLineSegment(sketch, "E791", {"start": v(1.13, 1.12) * mm, "end": v(1.13, 1.12) * mm});
            skLineSegment(sketch, "E792", {"start": v(1.13, 1.12) * mm, "end": v(1.12, 1.12) * mm});
            skLineSegment(sketch, "E793", {"start": v(1.12, 1.12) * mm, "end": v(1.12, 1.12) * mm});
            skLineSegment(sketch, "E794", {"start": v(1.12, 1.12) * mm, "end": v(1.11, 1.12) * mm});
            skLineSegment(sketch, "E795", {"start": v(1.11, 1.12) * mm, "end": v(1.1, 1.12) * mm});
            skLineSegment(sketch, "E796", {"start": v(1.1, 1.12) * mm, "end": v(1.1, 1.11) * mm});
            skLineSegment(sketch, "E797", {"start": v(1.1, 1.11) * mm, "end": v(1.1, 1.12) * mm});
            skLineSegment(sketch, "E798", {"start": v(1.1, 1.12) * mm, "end": v(1.09, 1.12) * mm});
            skLineSegment(sketch, "E799", {"start": v(1.09, 1.12) * mm, "end": v(1.08, 1.12) * mm});
            skLineSegment(sketch, "E800", {"start": v(1.08, 1.12) * mm, "end": v(1.08, 1.12) * mm});
            skLineSegment(sketch, "E801", {"start": v(1.08, 1.12) * mm, "end": v(1.07, 1.12) * mm});
            skLineSegment(sketch, "E802", {"start": v(1.07, 1.12) * mm, "end": v(1.07, 1.12) * mm});
            skLineSegment(sketch, "E803", {"start": v(1.07, 1.12) * mm, "end": v(1.06, 1.12) * mm});
            skLineSegment(sketch, "E804", {"start": v(1.06, 1.12) * mm, "end": v(1.06, 1.13) * mm});
            skLineSegment(sketch, "E805", {"start": v(1.06, 1.13) * mm, "end": v(1.05, 1.13) * mm});
            skLineSegment(sketch, "E806", {"start": v(1.05, 1.13) * mm, "end": v(1.05, 1.13) * mm});
            skLineSegment(sketch, "E807", {"start": v(1.05, 1.13) * mm, "end": v(1.04, 1.14) * mm});
            skLineSegment(sketch, "E808", {"start": v(1.04, 1.14) * mm, "end": v(1.04, 1.14) * mm});
            skLineSegment(sketch, "E809", {"start": v(1.04, 1.14) * mm, "end": v(1.03, 1.15) * mm});
            skLineSegment(sketch, "E810", {"start": v(1.03, 1.15) * mm, "end": v(1.03, 1.15) * mm});
            skLineSegment(sketch, "E811", {"start": v(1.03, 1.15) * mm, "end": v(1.03, 1.16) * mm});
            skLineSegment(sketch, "E812", {"start": v(1.03, 1.16) * mm, "end": v(1.02, 1.16) * mm});
            skLineSegment(sketch, "E813", {"start": v(1.02, 1.16) * mm, "end": v(1.02, 1.17) * mm});
            skLineSegment(sketch, "E814", {"start": v(1.02, 1.17) * mm, "end": v(1.02, 1.17) * mm});
            skLineSegment(sketch, "E815", {"start": v(1.02, 1.17) * mm, "end": v(1.02, 1.18) * mm});
            skLineSegment(sketch, "E816", {"start": v(1.02, 1.18) * mm, "end": v(1.02, 1.18) * mm});
            skLineSegment(sketch, "E817", {"start": v(1.02, 1.18) * mm, "end": v(1.02, 1.19) * mm});
            skLineSegment(sketch, "E818", {"start": v(1.02, 1.19) * mm, "end": v(1.02, 1.2) * mm});
            skLineSegment(sketch, "E819", {"start": v(1.02, 1.2) * mm, "end": v(1.01, 1.2) * mm});
            skLineSegment(sketch, "E820", {"start": v(1.04, 1.2) * mm, "end": v(1.07, 1.2) * mm});
            skLineSegment(sketch, "E821", {"start": v(1.09, 1.14) * mm, "end": v(1.07, 1.14) * mm});
            skLineSegment(sketch, "E822", {"start": v(1.11, 1.14) * mm, "end": v(1.13, 1.14) * mm});
            skLineSegment(sketch, "E823", {"start": v(1.12, 1.15) * mm, "end": v(1.12, 1.13) * mm});
            skLineSegment(sketch, "E824", {"start": v(0.96, 1.2) * mm, "end": v(0.93, 1.2) * mm});
            skLineSegment(sketch, "E825", {"start": v(0.93, 1.2) * mm, "end": v(0.93, 1.16) * mm});
            skLineSegment(sketch, "E826", {"start": v(0.93, 1.16) * mm, "end": v(0.9, 1.16) * mm});
            skLineSegment(sketch, "E827", {"start": v(0.9, 1.16) * mm, "end": v(0.9, 1.24) * mm});
            skLineSegment(sketch, "E828", {"start": v(0.9, 1.24) * mm, "end": v(0.93, 1.24) * mm});
            skLineSegment(sketch, "E829", {"start": v(0.93, 1.24) * mm, "end": v(0.93, 1.2) * mm});
            skLineSegment(sketch, "E830", {"start": v(0.82, 1.2) * mm, "end": v(0.82, 1.2) * mm});
            skLineSegment(sketch, "E831", {"start": v(0.82, 1.2) * mm, "end": v(0.82, 1.21) * mm});
            skLineSegment(sketch, "E832", {"start": v(0.82, 1.21) * mm, "end": v(0.82, 1.22) * mm});
            skLineSegment(sketch, "E833", {"start": v(0.82, 1.22) * mm, "end": v(0.82, 1.22) * mm});
            skLineSegment(sketch, "E834", {"start": v(0.82, 1.22) * mm, "end": v(0.82, 1.23) * mm});
            skLineSegment(sketch, "E835", {"start": v(0.82, 1.23) * mm, "end": v(0.82, 1.23) * mm});
            skLineSegment(sketch, "E836", {"start": v(0.82, 1.23) * mm, "end": v(0.82, 1.24) * mm});
            skLineSegment(sketch, "E837", {"start": v(0.82, 1.24) * mm, "end": v(0.83, 1.24) * mm});
            skLineSegment(sketch, "E838", {"start": v(0.83, 1.24) * mm, "end": v(0.83, 1.25) * mm});
            skLineSegment(sketch, "E839", {"start": v(0.83, 1.25) * mm, "end": v(0.83, 1.25) * mm});
            skLineSegment(sketch, "E840", {"start": v(0.83, 1.25) * mm, "end": v(0.84, 1.26) * mm});
            skLineSegment(sketch, "E841", {"start": v(0.84, 1.26) * mm, "end": v(0.84, 1.26) * mm});
            skLineSegment(sketch, "E842", {"start": v(0.84, 1.26) * mm, "end": v(0.85, 1.27) * mm});
            skLineSegment(sketch, "E843", {"start": v(0.85, 1.27) * mm, "end": v(0.85, 1.27) * mm});
            skLineSegment(sketch, "E844", {"start": v(0.85, 1.27) * mm, "end": v(0.86, 1.27) * mm});
            skLineSegment(sketch, "E845", {"start": v(0.86, 1.27) * mm, "end": v(0.86, 1.28) * mm});
            skLineSegment(sketch, "E846", {"start": v(0.86, 1.28) * mm, "end": v(0.87, 1.28) * mm});
            skLineSegment(sketch, "E847", {"start": v(0.87, 1.28) * mm, "end": v(0.87, 1.28) * mm});
            skLineSegment(sketch, "E848", {"start": v(0.87, 1.28) * mm, "end": v(0.88, 1.28) * mm});
            skLineSegment(sketch, "E849", {"start": v(0.88, 1.28) * mm, "end": v(0.88, 1.28) * mm});
            skLineSegment(sketch, "E850", {"start": v(0.88, 1.28) * mm, "end": v(0.89, 1.28) * mm});
            skLineSegment(sketch, "E851", {"start": v(0.89, 1.28) * mm, "end": v(0.9, 1.28) * mm});
            skLineSegment(sketch, "E852", {"start": v(0.9, 1.28) * mm, "end": v(0.9, 1.28) * mm});
            skLineSegment(sketch, "E853", {"start": v(0.9, 1.28) * mm, "end": v(0.91, 1.28) * mm});
            skLineSegment(sketch, "E854", {"start": v(0.91, 1.28) * mm, "end": v(0.92, 1.28) * mm});
            skLineSegment(sketch, "E855", {"start": v(0.92, 1.28) * mm, "end": v(0.92, 1.28) * mm});
            skLineSegment(sketch, "E856", {"start": v(0.92, 1.28) * mm, "end": v(0.93, 1.28) * mm});
            skLineSegment(sketch, "E857", {"start": v(0.93, 1.28) * mm, "end": v(0.93, 1.28) * mm});
            skLineSegment(sketch, "E858", {"start": v(0.93, 1.28) * mm, "end": v(0.94, 1.28) * mm});
            skLineSegment(sketch, "E859", {"start": v(0.94, 1.28) * mm, "end": v(0.94, 1.27) * mm});
            skLineSegment(sketch, "E860", {"start": v(0.94, 1.27) * mm, "end": v(0.95, 1.27) * mm});
            skLineSegment(sketch, "E861", {"start": v(0.95, 1.27) * mm, "end": v(0.95, 1.27) * mm});
            skLineSegment(sketch, "E862", {"start": v(0.95, 1.27) * mm, "end": v(0.96, 1.26) * mm});
            skLineSegment(sketch, "E863", {"start": v(0.96, 1.26) * mm, "end": v(0.96, 1.26) * mm});
            skLineSegment(sketch, "E864", {"start": v(0.96, 1.26) * mm, "end": v(0.97, 1.25) * mm});
            skLineSegment(sketch, "E865", {"start": v(0.97, 1.25) * mm, "end": v(0.97, 1.25) * mm});
            skLineSegment(sketch, "E866", {"start": v(0.97, 1.25) * mm, "end": v(0.97, 1.24) * mm});
            skLineSegment(sketch, "E867", {"start": v(0.97, 1.24) * mm, "end": v(0.98, 1.24) * mm});
            skLineSegment(sketch, "E868", {"start": v(0.98, 1.24) * mm, "end": v(0.98, 1.23) * mm});
            skLineSegment(sketch, "E869", {"start": v(0.98, 1.23) * mm, "end": v(0.98, 1.23) * mm});
            skLineSegment(sketch, "E870", {"start": v(0.98, 1.23) * mm, "end": v(0.98, 1.22) * mm});
            skLineSegment(sketch, "E871", {"start": v(0.98, 1.22) * mm, "end": v(0.98, 1.22) * mm});
            skLineSegment(sketch, "E872", {"start": v(0.98, 1.22) * mm, "end": v(0.98, 1.21) * mm});
            skLineSegment(sketch, "E873", {"start": v(0.98, 1.21) * mm, "end": v(0.98, 1.2) * mm});
            skLineSegment(sketch, "E874", {"start": v(0.98, 1.2) * mm, "end": v(0.99, 1.2) * mm});
            skLineSegment(sketch, "E875", {"start": v(0.99, 1.2) * mm, "end": v(0.98, 1.2) * mm});
            skLineSegment(sketch, "E876", {"start": v(0.98, 1.2) * mm, "end": v(0.98, 1.19) * mm});
            skLineSegment(sketch, "E877", {"start": v(0.98, 1.19) * mm, "end": v(0.98, 1.18) * mm});
            skLineSegment(sketch, "E878", {"start": v(0.98, 1.18) * mm, "end": v(0.98, 1.18) * mm});
            skLineSegment(sketch, "E879", {"start": v(0.98, 1.18) * mm, "end": v(0.98, 1.17) * mm});
            skLineSegment(sketch, "E880", {"start": v(0.98, 1.17) * mm, "end": v(0.98, 1.17) * mm});
            skLineSegment(sketch, "E881", {"start": v(0.98, 1.17) * mm, "end": v(0.98, 1.16) * mm});
            skLineSegment(sketch, "E882", {"start": v(0.98, 1.16) * mm, "end": v(0.97, 1.16) * mm});
            skLineSegment(sketch, "E883", {"start": v(0.97, 1.16) * mm, "end": v(0.97, 1.15) * mm});
            skLineSegment(sketch, "E884", {"start": v(0.97, 1.15) * mm, "end": v(0.97, 1.15) * mm});
            skLineSegment(sketch, "E885", {"start": v(0.97, 1.15) * mm, "end": v(0.96, 1.14) * mm});
            skLineSegment(sketch, "E886", {"start": v(0.96, 1.14) * mm, "end": v(0.96, 1.14) * mm});
            skLineSegment(sketch, "E887", {"start": v(0.96, 1.14) * mm, "end": v(0.95, 1.13) * mm});
            skLineSegment(sketch, "E888", {"start": v(0.95, 1.13) * mm, "end": v(0.95, 1.13) * mm});
            skLineSegment(sketch, "E889", {"start": v(0.95, 1.13) * mm, "end": v(0.94, 1.13) * mm});
            skLineSegment(sketch, "E890", {"start": v(0.94, 1.13) * mm, "end": v(0.94, 1.12) * mm});
            skLineSegment(sketch, "E891", {"start": v(0.94, 1.12) * mm, "end": v(0.93, 1.12) * mm});
            skLineSegment(sketch, "E892", {"start": v(0.93, 1.12) * mm, "end": v(0.93, 1.12) * mm});
            skLineSegment(sketch, "E893", {"start": v(0.93, 1.12) * mm, "end": v(0.92, 1.12) * mm});
            skLineSegment(sketch, "E894", {"start": v(0.92, 1.12) * mm, "end": v(0.92, 1.12) * mm});
            skLineSegment(sketch, "E895", {"start": v(0.92, 1.12) * mm, "end": v(0.91, 1.12) * mm});
            skLineSegment(sketch, "E896", {"start": v(0.91, 1.12) * mm, "end": v(0.9, 1.12) * mm});
            skLineSegment(sketch, "E897", {"start": v(0.9, 1.12) * mm, "end": v(0.9, 1.11) * mm});
            skLineSegment(sketch, "E898", {"start": v(0.9, 1.11) * mm, "end": v(0.9, 1.12) * mm});
            skLineSegment(sketch, "E899", {"start": v(0.9, 1.12) * mm, "end": v(0.89, 1.12) * mm});
            skLineSegment(sketch, "E900", {"start": v(0.89, 1.12) * mm, "end": v(0.88, 1.12) * mm});
            skLineSegment(sketch, "E901", {"start": v(0.88, 1.12) * mm, "end": v(0.88, 1.12) * mm});
            skLineSegment(sketch, "E902", {"start": v(0.88, 1.12) * mm, "end": v(0.87, 1.12) * mm});
            skLineSegment(sketch, "E903", {"start": v(0.87, 1.12) * mm, "end": v(0.87, 1.12) * mm});
            skLineSegment(sketch, "E904", {"start": v(0.87, 1.12) * mm, "end": v(0.86, 1.12) * mm});
            skLineSegment(sketch, "E905", {"start": v(0.86, 1.12) * mm, "end": v(0.86, 1.13) * mm});
            skLineSegment(sketch, "E906", {"start": v(0.86, 1.13) * mm, "end": v(0.85, 1.13) * mm});
            skLineSegment(sketch, "E907", {"start": v(0.85, 1.13) * mm, "end": v(0.85, 1.13) * mm});
            skLineSegment(sketch, "E908", {"start": v(0.85, 1.13) * mm, "end": v(0.84, 1.14) * mm});
            skLineSegment(sketch, "E909", {"start": v(0.84, 1.14) * mm, "end": v(0.84, 1.14) * mm});
            skLineSegment(sketch, "E910", {"start": v(0.84, 1.14) * mm, "end": v(0.83, 1.15) * mm});
            skLineSegment(sketch, "E911", {"start": v(0.83, 1.15) * mm, "end": v(0.83, 1.15) * mm});
            skLineSegment(sketch, "E912", {"start": v(0.83, 1.15) * mm, "end": v(0.83, 1.16) * mm});
            skLineSegment(sketch, "E913", {"start": v(0.83, 1.16) * mm, "end": v(0.82, 1.16) * mm});
            skLineSegment(sketch, "E914", {"start": v(0.82, 1.16) * mm, "end": v(0.82, 1.17) * mm});
            skLineSegment(sketch, "E915", {"start": v(0.82, 1.17) * mm, "end": v(0.82, 1.17) * mm});
            skLineSegment(sketch, "E916", {"start": v(0.82, 1.17) * mm, "end": v(0.82, 1.18) * mm});
            skLineSegment(sketch, "E917", {"start": v(0.82, 1.18) * mm, "end": v(0.82, 1.18) * mm});
            skLineSegment(sketch, "E918", {"start": v(0.82, 1.18) * mm, "end": v(0.82, 1.19) * mm});
            skLineSegment(sketch, "E919", {"start": v(0.82, 1.19) * mm, "end": v(0.82, 1.2) * mm});
            skLineSegment(sketch, "E920", {"start": v(0.84, 1.2) * mm, "end": v(0.88, 1.2) * mm});
            skLineSegment(sketch, "E921", {"start": v(0.89, 1.14) * mm, "end": v(0.86, 1.14) * mm});
            skLineSegment(sketch, "E922", {"start": v(0.9, 1.14) * mm, "end": v(0.93, 1.14) * mm});
            skLineSegment(sketch, "E923", {"start": v(0.92, 1.15) * mm, "end": v(0.92, 1.13) * mm});
            skLineSegment(sketch, "E924", {"start": v(0.76, 1.2) * mm, "end": v(0.73, 1.2) * mm});
            skLineSegment(sketch, "E925", {"start": v(0.73, 1.2) * mm, "end": v(0.73, 1.16) * mm});
            skLineSegment(sketch, "E926", {"start": v(0.73, 1.16) * mm, "end": v(0.71, 1.16) * mm});
            skLineSegment(sketch, "E927", {"start": v(0.71, 1.16) * mm, "end": v(0.71, 1.24) * mm});
            skLineSegment(sketch, "E928", {"start": v(0.71, 1.24) * mm, "end": v(0.73, 1.24) * mm});
            skLineSegment(sketch, "E929", {"start": v(0.73, 1.24) * mm, "end": v(0.73, 1.2) * mm});
            skLineSegment(sketch, "E930", {"start": v(0.61, 1.2) * mm, "end": v(0.62, 1.2) * mm});
            skLineSegment(sketch, "E931", {"start": v(0.62, 1.2) * mm, "end": v(0.62, 1.21) * mm});
            skLineSegment(sketch, "E932", {"start": v(0.62, 1.21) * mm, "end": v(0.62, 1.22) * mm});
            skLineSegment(sketch, "E933", {"start": v(0.62, 1.22) * mm, "end": v(0.62, 1.22) * mm});
            skLineSegment(sketch, "E934", {"start": v(0.62, 1.22) * mm, "end": v(0.62, 1.23) * mm});
            skLineSegment(sketch, "E935", {"start": v(0.62, 1.23) * mm, "end": v(0.62, 1.23) * mm});
            skLineSegment(sketch, "E936", {"start": v(0.62, 1.23) * mm, "end": v(0.62, 1.24) * mm});
            skLineSegment(sketch, "E937", {"start": v(0.62, 1.24) * mm, "end": v(0.63, 1.24) * mm});
            skLineSegment(sketch, "E938", {"start": v(0.63, 1.24) * mm, "end": v(0.63, 1.25) * mm});
            skLineSegment(sketch, "E939", {"start": v(0.63, 1.25) * mm, "end": v(0.63, 1.25) * mm});
            skLineSegment(sketch, "E940", {"start": v(0.63, 1.25) * mm, "end": v(0.64, 1.26) * mm});
            skLineSegment(sketch, "E941", {"start": v(0.64, 1.26) * mm, "end": v(0.64, 1.26) * mm});
            skLineSegment(sketch, "E942", {"start": v(0.64, 1.26) * mm, "end": v(0.65, 1.27) * mm});
            skLineSegment(sketch, "E943", {"start": v(0.65, 1.27) * mm, "end": v(0.65, 1.27) * mm});
            skLineSegment(sketch, "E944", {"start": v(0.65, 1.27) * mm, "end": v(0.66, 1.27) * mm});
            skLineSegment(sketch, "E945", {"start": v(0.66, 1.27) * mm, "end": v(0.66, 1.28) * mm});
            skLineSegment(sketch, "E946", {"start": v(0.66, 1.28) * mm, "end": v(0.67, 1.28) * mm});
            skLineSegment(sketch, "E947", {"start": v(0.67, 1.28) * mm, "end": v(0.67, 1.28) * mm});
            skLineSegment(sketch, "E948", {"start": v(0.67, 1.28) * mm, "end": v(0.68, 1.28) * mm});
            skLineSegment(sketch, "E949", {"start": v(0.68, 1.28) * mm, "end": v(0.68, 1.28) * mm});
            skLineSegment(sketch, "E950", {"start": v(0.68, 1.28) * mm, "end": v(0.69, 1.28) * mm});
            skLineSegment(sketch, "E951", {"start": v(0.69, 1.28) * mm, "end": v(0.7, 1.28) * mm});
            skLineSegment(sketch, "E952", {"start": v(0.7, 1.28) * mm, "end": v(0.7, 1.28) * mm});
            skLineSegment(sketch, "E953", {"start": v(0.7, 1.28) * mm, "end": v(0.71, 1.28) * mm});
            skLineSegment(sketch, "E954", {"start": v(0.71, 1.28) * mm, "end": v(0.72, 1.28) * mm});
            skLineSegment(sketch, "E955", {"start": v(0.72, 1.28) * mm, "end": v(0.72, 1.28) * mm});
            skLineSegment(sketch, "E956", {"start": v(0.72, 1.28) * mm, "end": v(0.73, 1.28) * mm});
            skLineSegment(sketch, "E957", {"start": v(0.73, 1.28) * mm, "end": v(0.73, 1.28) * mm});
            skLineSegment(sketch, "E958", {"start": v(0.73, 1.28) * mm, "end": v(0.74, 1.28) * mm});
            skLineSegment(sketch, "E959", {"start": v(0.74, 1.28) * mm, "end": v(0.74, 1.27) * mm});
            skLineSegment(sketch, "E960", {"start": v(0.74, 1.27) * mm, "end": v(0.75, 1.27) * mm});
            skLineSegment(sketch, "E961", {"start": v(0.75, 1.27) * mm, "end": v(0.75, 1.27) * mm});
            skLineSegment(sketch, "E962", {"start": v(0.75, 1.27) * mm, "end": v(0.76, 1.26) * mm});
            skLineSegment(sketch, "E963", {"start": v(0.76, 1.26) * mm, "end": v(0.76, 1.26) * mm});
            skLineSegment(sketch, "E964", {"start": v(0.76, 1.26) * mm, "end": v(0.77, 1.25) * mm});
            skLineSegment(sketch, "E965", {"start": v(0.77, 1.25) * mm, "end": v(0.77, 1.25) * mm});
            skLineSegment(sketch, "E966", {"start": v(0.77, 1.25) * mm, "end": v(0.77, 1.24) * mm});
            skLineSegment(sketch, "E967", {"start": v(0.77, 1.24) * mm, "end": v(0.78, 1.24) * mm});
            skLineSegment(sketch, "E968", {"start": v(0.78, 1.24) * mm, "end": v(0.78, 1.23) * mm});
            skLineSegment(sketch, "E969", {"start": v(0.78, 1.23) * mm, "end": v(0.78, 1.23) * mm});
            skLineSegment(sketch, "E970", {"start": v(0.78, 1.23) * mm, "end": v(0.78, 1.22) * mm});
            skLineSegment(sketch, "E971", {"start": v(0.78, 1.22) * mm, "end": v(0.78, 1.22) * mm});
            skLineSegment(sketch, "E972", {"start": v(0.78, 1.22) * mm, "end": v(0.78, 1.21) * mm});
            skLineSegment(sketch, "E973", {"start": v(0.78, 1.21) * mm, "end": v(0.78, 1.2) * mm});
            skLineSegment(sketch, "E974", {"start": v(0.78, 1.2) * mm, "end": v(0.78, 1.2) * mm});
            skLineSegment(sketch, "E975", {"start": v(0.78, 1.2) * mm, "end": v(0.78, 1.19) * mm});
            skLineSegment(sketch, "E976", {"start": v(0.78, 1.19) * mm, "end": v(0.78, 1.18) * mm});
            skLineSegment(sketch, "E977", {"start": v(0.78, 1.18) * mm, "end": v(0.78, 1.18) * mm});
            skLineSegment(sketch, "E978", {"start": v(0.78, 1.18) * mm, "end": v(0.78, 1.17) * mm});
            skLineSegment(sketch, "E979", {"start": v(0.78, 1.17) * mm, "end": v(0.78, 1.17) * mm});
            skLineSegment(sketch, "E980", {"start": v(0.78, 1.17) * mm, "end": v(0.78, 1.16) * mm});
            skLineSegment(sketch, "E981", {"start": v(0.78, 1.16) * mm, "end": v(0.77, 1.16) * mm});
            skLineSegment(sketch, "E982", {"start": v(0.77, 1.16) * mm, "end": v(0.77, 1.15) * mm});
            skLineSegment(sketch, "E983", {"start": v(0.77, 1.15) * mm, "end": v(0.77, 1.15) * mm});
            skLineSegment(sketch, "E984", {"start": v(0.77, 1.15) * mm, "end": v(0.76, 1.14) * mm});
            skLineSegment(sketch, "E985", {"start": v(0.76, 1.14) * mm, "end": v(0.76, 1.14) * mm});
            skLineSegment(sketch, "E986", {"start": v(0.76, 1.14) * mm, "end": v(0.75, 1.13) * mm});
            skLineSegment(sketch, "E987", {"start": v(0.75, 1.13) * mm, "end": v(0.75, 1.13) * mm});
            skLineSegment(sketch, "E988", {"start": v(0.75, 1.13) * mm, "end": v(0.74, 1.13) * mm});
            skLineSegment(sketch, "E989", {"start": v(0.74, 1.13) * mm, "end": v(0.74, 1.12) * mm});
            skLineSegment(sketch, "E990", {"start": v(0.74, 1.12) * mm, "end": v(0.73, 1.12) * mm});
            skLineSegment(sketch, "E991", {"start": v(0.73, 1.12) * mm, "end": v(0.73, 1.12) * mm});
            skLineSegment(sketch, "E992", {"start": v(0.73, 1.12) * mm, "end": v(0.72, 1.12) * mm});
            skLineSegment(sketch, "E993", {"start": v(0.72, 1.12) * mm, "end": v(0.72, 1.12) * mm});
            skLineSegment(sketch, "E994", {"start": v(0.72, 1.12) * mm, "end": v(0.71, 1.12) * mm});
            skLineSegment(sketch, "E995", {"start": v(0.71, 1.12) * mm, "end": v(0.7, 1.12) * mm});
            skLineSegment(sketch, "E996", {"start": v(0.7, 1.12) * mm, "end": v(0.7, 1.11) * mm});
            skLineSegment(sketch, "E997", {"start": v(0.7, 1.11) * mm, "end": v(0.7, 1.12) * mm});
            skLineSegment(sketch, "E998", {"start": v(0.7, 1.12) * mm, "end": v(0.69, 1.12) * mm});
            skLineSegment(sketch, "E999", {"start": v(0.69, 1.12) * mm, "end": v(0.68, 1.12) * mm});
            skLineSegment(sketch, "E1000", {"start": v(0.68, 1.12) * mm, "end": v(0.68, 1.12) * mm});
            skLineSegment(sketch, "E1001", {"start": v(0.68, 1.12) * mm, "end": v(0.67, 1.12) * mm});
            skLineSegment(sketch, "E1002", {"start": v(0.67, 1.12) * mm, "end": v(0.67, 1.12) * mm});
            skLineSegment(sketch, "E1003", {"start": v(0.67, 1.12) * mm, "end": v(0.66, 1.12) * mm});
            skLineSegment(sketch, "E1004", {"start": v(0.66, 1.12) * mm, "end": v(0.66, 1.13) * mm});
            skLineSegment(sketch, "E1005", {"start": v(0.66, 1.13) * mm, "end": v(0.65, 1.13) * mm});
            skLineSegment(sketch, "E1006", {"start": v(0.65, 1.13) * mm, "end": v(0.65, 1.13) * mm});
            skLineSegment(sketch, "E1007", {"start": v(0.65, 1.13) * mm, "end": v(0.64, 1.14) * mm});
            skLineSegment(sketch, "E1008", {"start": v(0.64, 1.14) * mm, "end": v(0.64, 1.14) * mm});
            skLineSegment(sketch, "E1009", {"start": v(0.64, 1.14) * mm, "end": v(0.63, 1.15) * mm});
            skLineSegment(sketch, "E1010", {"start": v(0.63, 1.15) * mm, "end": v(0.63, 1.15) * mm});
            skLineSegment(sketch, "E1011", {"start": v(0.63, 1.15) * mm, "end": v(0.63, 1.16) * mm});
            skLineSegment(sketch, "E1012", {"start": v(0.63, 1.16) * mm, "end": v(0.62, 1.16) * mm});
            skLineSegment(sketch, "E1013", {"start": v(0.62, 1.16) * mm, "end": v(0.62, 1.17) * mm});
            skLineSegment(sketch, "E1014", {"start": v(0.62, 1.17) * mm, "end": v(0.62, 1.17) * mm});
            skLineSegment(sketch, "E1015", {"start": v(0.62, 1.17) * mm, "end": v(0.62, 1.18) * mm});
            skLineSegment(sketch, "E1016", {"start": v(0.62, 1.18) * mm, "end": v(0.62, 1.18) * mm});
            skLineSegment(sketch, "E1017", {"start": v(0.62, 1.18) * mm, "end": v(0.62, 1.19) * mm});
            skLineSegment(sketch, "E1018", {"start": v(0.62, 1.19) * mm, "end": v(0.62, 1.2) * mm});
            skLineSegment(sketch, "E1019", {"start": v(0.62, 1.2) * mm, "end": v(0.61, 1.2) * mm});
            skLineSegment(sketch, "E1020", {"start": v(0.64, 1.2) * mm, "end": v(0.68, 1.2) * mm});
            skLineSegment(sketch, "E1021", {"start": v(0.68, 1.14) * mm, "end": v(0.66, 1.14) * mm});
            skLineSegment(sketch, "E1022", {"start": v(0.71, 1.14) * mm, "end": v(0.73, 1.14) * mm});
            skLineSegment(sketch, "E1023", {"start": v(0.72, 1.15) * mm, "end": v(0.72, 1.13) * mm});
            skLineSegment(sketch, "E1024", {"start": v(0.5, 1) * mm, "end": v(-0.4, 1) * mm});
            skLineSegment(sketch, "E1025", {"start": v(-0.4, 1) * mm, "end": v(-0.4, 0.92) * mm});
            skLineSegment(sketch, "E1026", {"start": v(-0.4, 0.94) * mm, "end": v(-0.4, 0.75) * mm});
            skLineSegment(sketch, "E1027", {"start": v(-0.4, 0.75) * mm, "end": v(-0.4, 0.75) * mm});
            skLineSegment(sketch, "E1028", {"start": v(-0.4, 0.75) * mm, "end": v(-0.4, 0.73) * mm});
            skLineSegment(sketch, "E1029", {"start": v(-0.4, 0.73) * mm, "end": v(-0.4, 0.73) * mm});
            skLineSegment(sketch, "E1030", {"start": v(-0.4, 0.73) * mm, "end": v(-0.41, 0.73) * mm});
            skLineSegment(sketch, "E1031", {"start": v(-0.41, 0.73) * mm, "end": v(-0.41, 0.73) * mm});
            skLineSegment(sketch, "E1032", {"start": v(-0.41, 0.73) * mm, "end": v(-0.42, 0.72) * mm});
            skLineSegment(sketch, "E1033", {"start": v(-0.42, 0.72) * mm, "end": v(-0.48, 0.72) * mm});
            skLineSegment(sketch, "E1034", {"start": v(-0.48, 0.72) * mm, "end": v(-0.49, 0.73) * mm});
            skLineSegment(sketch, "E1035", {"start": v(-0.49, 0.73) * mm, "end": v(-0.49, 0.73) * mm});
            skLineSegment(sketch, "E1036", {"start": v(-0.49, 0.73) * mm, "end": v(-0.5, 0.73) * mm});
            skLineSegment(sketch, "E1037", {"start": v(-0.5, 0.73) * mm, "end": v(-0.5, 0.73) * mm});
            skLineSegment(sketch, "E1038", {"start": v(-0.5, 0.73) * mm, "end": v(-0.5, 0.75) * mm});
            skLineSegment(sketch, "E1039", {"start": v(-0.5, 0.75) * mm, "end": v(-0.49, 0.75) * mm});
            skLineSegment(sketch, "E1040", {"start": v(-0.49, 0.75) * mm, "end": v(-0.49, 0.94) * mm});
            skLineSegment(sketch, "E1041", {"start": v(-0.49, 0.94) * mm, "end": v(-0.5, 0.95) * mm});
            skLineSegment(sketch, "E1042", {"start": v(-0.5, 0.95) * mm, "end": v(-0.5, 0.96) * mm});
            skLineSegment(sketch, "E1043", {"start": v(-0.5, 0.96) * mm, "end": v(-0.5, 0.95) * mm});
            skLineSegment(sketch, "E1044", {"start": v(-0.5, 0.95) * mm, "end": v(-0.51, 0.94) * mm});
            skLineSegment(sketch, "E1045", {"start": v(-0.51, 0.94) * mm, "end": v(-0.51, 0.75) * mm});
            skLineSegment(sketch, "E1046", {"start": v(-0.51, 0.75) * mm, "end": v(-0.5, 0.75) * mm});
            skLineSegment(sketch, "E1047", {"start": v(-0.5, 0.75) * mm, "end": v(-0.5, 0.73) * mm});
            skLineSegment(sketch, "E1048", {"start": v(-0.5, 0.73) * mm, "end": v(-0.51, 0.73) * mm});
            skLineSegment(sketch, "E1049", {"start": v(-0.51, 0.73) * mm, "end": v(-0.51, 0.73) * mm});
            skLineSegment(sketch, "E1050", {"start": v(-0.51, 0.73) * mm, "end": v(-0.51, 0.72) * mm});
            skLineSegment(sketch, "E1051", {"start": v(-0.51, 0.72) * mm, "end": v(-0.58, 0.72) * mm});
            skLineSegment(sketch, "E1052", {"start": v(-0.58, 0.72) * mm, "end": v(-0.59, 0.73) * mm});
            skLineSegment(sketch, "E1053", {"start": v(-0.59, 0.73) * mm, "end": v(-0.59, 0.73) * mm});
            skLineSegment(sketch, "E1054", {"start": v(-0.59, 0.73) * mm, "end": v(-0.6, 0.73) * mm});
            skLineSegment(sketch, "E1055", {"start": v(-0.6, 0.73) * mm, "end": v(-0.6, 0.73) * mm});
            skLineSegment(sketch, "E1056", {"start": v(-0.6, 0.73) * mm, "end": v(-0.6, 0.75) * mm});
            skLineSegment(sketch, "E1057", {"start": v(-0.6, 0.75) * mm, "end": v(-0.6, 0.75) * mm});
            skLineSegment(sketch, "E1058", {"start": v(-0.6, 0.75) * mm, "end": v(-0.6, 0.94) * mm});
            skLineSegment(sketch, "E1059", {"start": v(-0.6, 0.94) * mm, "end": v(-0.6, 0.95) * mm});
            skLineSegment(sketch, "E1060", {"start": v(-0.6, 0.95) * mm, "end": v(-0.6, 0.96) * mm});
            skLineSegment(sketch, "E1061", {"start": v(-0.6, 0.96) * mm, "end": v(-0.6, 0.95) * mm});
            skLineSegment(sketch, "E1062", {"start": v(-0.6, 0.95) * mm, "end": v(-0.6, 0.94) * mm});
            skLineSegment(sketch, "E1063", {"start": v(-0.6, 0.94) * mm, "end": v(-0.6, 0.75) * mm});
            skLineSegment(sketch, "E1064", {"start": v(-0.6, 0.75) * mm, "end": v(-0.6, 0.73) * mm});
            skLineSegment(sketch, "E1065", {"start": v(-0.6, 0.73) * mm, "end": v(-0.61, 0.73) * mm});
            skLineSegment(sketch, "E1066", {"start": v(-0.61, 0.73) * mm, "end": v(-0.61, 0.73) * mm});
            skLineSegment(sketch, "E1067", {"start": v(-0.61, 0.73) * mm, "end": v(-0.61, 0.72) * mm});
            skLineSegment(sketch, "E1068", {"start": v(-0.61, 0.72) * mm, "end": v(-0.69, 0.72) * mm});
            skLineSegment(sketch, "E1069", {"start": v(-0.69, 0.72) * mm, "end": v(-0.69, 0.73) * mm});
            skLineSegment(sketch, "E1070", {"start": v(-0.69, 0.73) * mm, "end": v(-0.69, 0.73) * mm});
            skLineSegment(sketch, "E1071", {"start": v(-0.69, 0.73) * mm, "end": v(-0.7, 0.73) * mm});
            skLineSegment(sketch, "E1072", {"start": v(-0.7, 0.73) * mm, "end": v(-0.7, 0.73) * mm});
            skLineSegment(sketch, "E1073", {"start": v(-0.7, 0.73) * mm, "end": v(-0.7, 0.75) * mm});
            skLineSegment(sketch, "E1074", {"start": v(-0.7, 0.75) * mm, "end": v(-0.69, 0.75) * mm});
            skLineSegment(sketch, "E1075", {"start": v(-0.69, 0.75) * mm, "end": v(-0.69, 0.94) * mm});
            skLineSegment(sketch, "E1076", {"start": v(-0.69, 0.94) * mm, "end": v(-0.7, 0.95) * mm});
            skLineSegment(sketch, "E1077", {"start": v(-0.7, 0.95) * mm, "end": v(-0.7, 0.96) * mm});
            skLineSegment(sketch, "E1078", {"start": v(-0.7, 0.96) * mm, "end": v(-0.7, 0.95) * mm});
            skLineSegment(sketch, "E1079", {"start": v(-0.7, 0.95) * mm, "end": v(-0.71, 0.94) * mm});
            skLineSegment(sketch, "E1080", {"start": v(-0.71, 0.94) * mm, "end": v(-0.71, 0.75) * mm});
            skLineSegment(sketch, "E1081", {"start": v(-0.71, 0.75) * mm, "end": v(-0.7, 0.75) * mm});
            skLineSegment(sketch, "E1082", {"start": v(-0.7, 0.75) * mm, "end": v(-0.7, 0.73) * mm});
            skLineSegment(sketch, "E1083", {"start": v(-0.7, 0.73) * mm, "end": v(-0.71, 0.73) * mm});
            skLineSegment(sketch, "E1084", {"start": v(-0.71, 0.73) * mm, "end": v(-0.71, 0.73) * mm});
            skLineSegment(sketch, "E1085", {"start": v(-0.71, 0.73) * mm, "end": v(-0.72, 0.72) * mm});
            skLineSegment(sketch, "E1086", {"start": v(-0.72, 0.72) * mm, "end": v(-0.78, 0.72) * mm});
            skLineSegment(sketch, "E1087", {"start": v(-0.78, 0.72) * mm, "end": v(-0.79, 0.73) * mm});
            skLineSegment(sketch, "E1088", {"start": v(-0.79, 0.73) * mm, "end": v(-0.79, 0.73) * mm});
            skLineSegment(sketch, "E1089", {"start": v(-0.79, 0.73) * mm, "end": v(-0.8, 0.73) * mm});
            skLineSegment(sketch, "E1090", {"start": v(-0.8, 0.73) * mm, "end": v(-0.8, 0.73) * mm});
            skLineSegment(sketch, "E1091", {"start": v(-0.8, 0.73) * mm, "end": v(-0.8, 0.75) * mm});
            skLineSegment(sketch, "E1092", {"start": v(-0.8, 0.75) * mm, "end": v(-0.79, 0.75) * mm});
            skLineSegment(sketch, "E1093", {"start": v(-0.79, 0.75) * mm, "end": v(-0.79, 0.94) * mm});
            skLineSegment(sketch, "E1094", {"start": v(-0.79, 0.94) * mm, "end": v(-0.8, 0.95) * mm});
            skLineSegment(sketch, "E1095", {"start": v(-0.8, 0.95) * mm, "end": v(-0.8, 0.96) * mm});
            skLineSegment(sketch, "E1096", {"start": v(-0.8, 0.96) * mm, "end": v(-0.8, 0.95) * mm});
            skLineSegment(sketch, "E1097", {"start": v(-0.8, 0.95) * mm, "end": v(-0.81, 0.94) * mm});
            skLineSegment(sketch, "E1098", {"start": v(-0.81, 0.94) * mm, "end": v(-0.81, 0.75) * mm});
            skLineSegment(sketch, "E1099", {"start": v(-0.81, 0.75) * mm, "end": v(-0.8, 0.75) * mm});
            skLineSegment(sketch, "E1100", {"start": v(-0.8, 0.75) * mm, "end": v(-0.8, 0.73) * mm});
            skLineSegment(sketch, "E1101", {"start": v(-0.8, 0.73) * mm, "end": v(-0.81, 0.73) * mm});
            skLineSegment(sketch, "E1102", {"start": v(-0.81, 0.73) * mm, "end": v(-0.81, 0.73) * mm});
            skLineSegment(sketch, "E1103", {"start": v(-0.81, 0.73) * mm, "end": v(-0.81, 0.72) * mm});
            skLineSegment(sketch, "E1104", {"start": v(-0.81, 0.72) * mm, "end": v(-0.89, 0.72) * mm});
            skLineSegment(sketch, "E1105", {"start": v(-0.89, 0.72) * mm, "end": v(-0.89, 0.73) * mm});
            skLineSegment(sketch, "E1106", {"start": v(-0.89, 0.73) * mm, "end": v(-0.89, 0.73) * mm});
            skLineSegment(sketch, "E1107", {"start": v(-0.89, 0.73) * mm, "end": v(-0.9, 0.73) * mm});
            skLineSegment(sketch, "E1108", {"start": v(-0.9, 0.73) * mm, "end": v(-0.9, 0.73) * mm});
            skLineSegment(sketch, "E1109", {"start": v(-0.9, 0.73) * mm, "end": v(-0.9, 0.75) * mm});
            skLineSegment(sketch, "E1110", {"start": v(-0.9, 0.75) * mm, "end": v(-0.89, 0.75) * mm});
            skLineSegment(sketch, "E1111", {"start": v(-0.89, 0.75) * mm, "end": v(-0.89, 0.94) * mm});
            skLineSegment(sketch, "E1112", {"start": v(-0.89, 0.94) * mm, "end": v(-0.9, 0.95) * mm});
            skLineSegment(sketch, "E1113", {"start": v(-0.9, 0.95) * mm, "end": v(-0.9, 0.96) * mm});
            skLineSegment(sketch, "E1114", {"start": v(-0.9, 0.96) * mm, "end": v(-0.9, 0.95) * mm});
            skLineSegment(sketch, "E1115", {"start": v(-0.9, 0.95) * mm, "end": v(-0.9, 0.94) * mm});
            skLineSegment(sketch, "E1116", {"start": v(-0.9, 0.94) * mm, "end": v(-0.9, 0.75) * mm});
            skLineSegment(sketch, "E1117", {"start": v(-0.9, 0.75) * mm, "end": v(-0.9, 0.75) * mm});
            skLineSegment(sketch, "E1118", {"start": v(-0.9, 0.75) * mm, "end": v(-0.9, 0.73) * mm});
            skLineSegment(sketch, "E1119", {"start": v(-0.9, 0.73) * mm, "end": v(-0.91, 0.73) * mm});
            skLineSegment(sketch, "E1120", {"start": v(-0.91, 0.73) * mm, "end": v(-0.91, 0.73) * mm});
            skLineSegment(sketch, "E1121", {"start": v(-0.91, 0.73) * mm, "end": v(-0.91, 0.72) * mm});
            skLineSegment(sketch, "E1122", {"start": v(-0.91, 0.72) * mm, "end": v(-0.98, 0.72) * mm});
            skLineSegment(sketch, "E1123", {"start": v(-0.98, 0.72) * mm, "end": v(-0.99, 0.73) * mm});
            skLineSegment(sketch, "E1124", {"start": v(-0.99, 0.73) * mm, "end": v(-0.99, 0.73) * mm});
            skLineSegment(sketch, "E1125", {"start": v(-0.99, 0.73) * mm, "end": v(-1, 0.73) * mm});
            skLineSegment(sketch, "E1126", {"start": v(-1, 0.73) * mm, "end": v(-1, 0.73) * mm});
            skLineSegment(sketch, "E1127", {"start": v(-1, 0.73) * mm, "end": v(-1, 0.75) * mm});
            skLineSegment(sketch, "E1128", {"start": v(-1, 0.75) * mm, "end": v(-0.99, 0.75) * mm});
            skLineSegment(sketch, "E1129", {"start": v(-0.99, 0.75) * mm, "end": v(-0.99, 0.94) * mm});
            skLineSegment(sketch, "E1130", {"start": v(-0.99, 0.94) * mm, "end": v(-1, 0.95) * mm});
            skLineSegment(sketch, "E1131", {"start": v(-1, 0.95) * mm, "end": v(-1, 0.96) * mm});
            skLineSegment(sketch, "E1132", {"start": v(-1, 0.96) * mm, "end": v(-1, 0.97) * mm});
            skLineSegment(sketch, "E1133", {"start": v(-1, 0.97) * mm, "end": v(-1, 0.97) * mm});
            skLineSegment(sketch, "E1134", {"start": v(-1, 0.97) * mm, "end": v(-0.99, 0.97) * mm});
            skLineSegment(sketch, "E1135", {"start": v(-0.99, 0.97) * mm, "end": v(-0.99, 0.97) * mm});
            skLineSegment(sketch, "E1136", {"start": v(-0.99, 0.97) * mm, "end": v(-0.98, 0.97) * mm});
            skLineSegment(sketch, "E1137", {"start": v(-0.98, 0.97) * mm, "end": v(-0.91, 0.97) * mm});
            skLineSegment(sketch, "E1138", {"start": v(-0.91, 0.97) * mm, "end": v(-0.91, 0.97) * mm});
            skLineSegment(sketch, "E1139", {"start": v(-0.91, 0.97) * mm, "end": v(-0.9, 0.97) * mm});
            skLineSegment(sketch, "E1140", {"start": v(-0.9, 0.97) * mm, "end": v(-0.9, 0.97) * mm});
            skLineSegment(sketch, "E1141", {"start": v(-0.9, 0.97) * mm, "end": v(-0.9, 0.96) * mm});
            skLineSegment(sketch, "E1142", {"start": v(-0.9, 0.96) * mm, "end": v(-0.9, 0.97) * mm});
            skLineSegment(sketch, "E1143", {"start": v(-0.9, 0.97) * mm, "end": v(-0.89, 0.97) * mm});
            skLineSegment(sketch, "E1144", {"start": v(-0.89, 0.97) * mm, "end": v(-0.89, 0.97) * mm});
            skLineSegment(sketch, "E1145", {"start": v(-0.89, 0.97) * mm, "end": v(-0.81, 0.97) * mm});
            skLineSegment(sketch, "E1146", {"start": v(-0.81, 0.97) * mm, "end": v(-0.81, 0.97) * mm});
            skLineSegment(sketch, "E1147", {"start": v(-0.81, 0.97) * mm, "end": v(-0.8, 0.97) * mm});
            skLineSegment(sketch, "E1148", {"start": v(-0.8, 0.97) * mm, "end": v(-0.8, 0.97) * mm});
            skLineSegment(sketch, "E1149", {"start": v(-0.8, 0.97) * mm, "end": v(-0.8, 0.96) * mm});
            skLineSegment(sketch, "E1150", {"start": v(-0.8, 0.96) * mm, "end": v(-0.8, 0.97) * mm});
            skLineSegment(sketch, "E1151", {"start": v(-0.8, 0.97) * mm, "end": v(-0.79, 0.97) * mm});
            skLineSegment(sketch, "E1152", {"start": v(-0.79, 0.97) * mm, "end": v(-0.79, 0.97) * mm});
            skLineSegment(sketch, "E1153", {"start": v(-0.79, 0.97) * mm, "end": v(-0.78, 0.97) * mm});
            skLineSegment(sketch, "E1154", {"start": v(-0.78, 0.97) * mm, "end": v(-0.72, 0.97) * mm});
            skLineSegment(sketch, "E1155", {"start": v(-0.72, 0.97) * mm, "end": v(-0.71, 0.97) * mm});
            skLineSegment(sketch, "E1156", {"start": v(-0.71, 0.97) * mm, "end": v(-0.71, 0.97) * mm});
            skLineSegment(sketch, "E1157", {"start": v(-0.71, 0.97) * mm, "end": v(-0.7, 0.97) * mm});
            skLineSegment(sketch, "E1158", {"start": v(-0.7, 0.97) * mm, "end": v(-0.7, 0.97) * mm});
            skLineSegment(sketch, "E1159", {"start": v(-0.7, 0.97) * mm, "end": v(-0.7, 0.96) * mm});
            skLineSegment(sketch, "E1160", {"start": v(-0.7, 0.96) * mm, "end": v(-0.7, 0.97) * mm});
            skLineSegment(sketch, "E1161", {"start": v(-0.7, 0.97) * mm, "end": v(-0.69, 0.97) * mm});
            skLineSegment(sketch, "E1162", {"start": v(-0.69, 0.97) * mm, "end": v(-0.69, 0.97) * mm});
            skLineSegment(sketch, "E1163", {"start": v(-0.69, 0.97) * mm, "end": v(-0.61, 0.97) * mm});
            skLineSegment(sketch, "E1164", {"start": v(-0.61, 0.97) * mm, "end": v(-0.61, 0.97) * mm});
            skLineSegment(sketch, "E1165", {"start": v(-0.61, 0.97) * mm, "end": v(-0.6, 0.97) * mm});
            skLineSegment(sketch, "E1166", {"start": v(-0.6, 0.97) * mm, "end": v(-0.6, 0.97) * mm});
            skLineSegment(sketch, "E1167", {"start": v(-0.6, 0.97) * mm, "end": v(-0.6, 0.96) * mm});
            skLineSegment(sketch, "E1168", {"start": v(-0.6, 0.96) * mm, "end": v(-0.6, 0.97) * mm});
            skLineSegment(sketch, "E1169", {"start": v(-0.6, 0.97) * mm, "end": v(-0.59, 0.97) * mm});
            skLineSegment(sketch, "E1170", {"start": v(-0.59, 0.97) * mm, "end": v(-0.59, 0.97) * mm});
            skLineSegment(sketch, "E1171", {"start": v(-0.59, 0.97) * mm, "end": v(-0.58, 0.97) * mm});
            skLineSegment(sketch, "E1172", {"start": v(-0.58, 0.97) * mm, "end": v(-0.51, 0.97) * mm});
            skLineSegment(sketch, "E1173", {"start": v(-0.51, 0.97) * mm, "end": v(-0.51, 0.97) * mm});
            skLineSegment(sketch, "E1174", {"start": v(-0.51, 0.97) * mm, "end": v(-0.5, 0.97) * mm});
            skLineSegment(sketch, "E1175", {"start": v(-0.5, 0.97) * mm, "end": v(-0.5, 0.97) * mm});
            skLineSegment(sketch, "E1176", {"start": v(-0.5, 0.97) * mm, "end": v(-0.5, 0.96) * mm});
            skLineSegment(sketch, "E1177", {"start": v(-0.5, 0.96) * mm, "end": v(-0.5, 0.97) * mm});
            skLineSegment(sketch, "E1178", {"start": v(-0.5, 0.97) * mm, "end": v(-0.49, 0.97) * mm});
            skLineSegment(sketch, "E1179", {"start": v(-0.49, 0.97) * mm, "end": v(-0.49, 0.97) * mm});
            skLineSegment(sketch, "E1180", {"start": v(-0.49, 0.97) * mm, "end": v(-0.48, 0.97) * mm});
            skLineSegment(sketch, "E1181", {"start": v(-0.48, 0.97) * mm, "end": v(-0.42, 0.97) * mm});
            skLineSegment(sketch, "E1182", {"start": v(-0.42, 0.97) * mm, "end": v(-0.41, 0.97) * mm});
            skLineSegment(sketch, "E1183", {"start": v(-0.41, 0.97) * mm, "end": v(-0.41, 0.97) * mm});
            skLineSegment(sketch, "E1184", {"start": v(-0.41, 0.97) * mm, "end": v(-0.4, 0.97) * mm});
            skLineSegment(sketch, "E1185", {"start": v(-0.4, 0.97) * mm, "end": v(-0.4, 0.97) * mm});
            skLineSegment(sketch, "E1186", {"start": v(-0.4, 0.97) * mm, "end": v(-0.4, 0.96) * mm});
            skLineSegment(sketch, "E1187", {"start": v(-0.4, 0.96) * mm, "end": v(-0.4, 0.95) * mm});
            skLineSegment(sketch, "E1188", {"start": v(-0.4, 0.95) * mm, "end": v(-0.4, 0.94) * mm});
            skLineSegment(sketch, "E1189", {"start": v(-0.4, 0.92) * mm, "end": v(-0.4, 0.92) * mm});
            skLineSegment(sketch, "E1190", {"start": v(-0.4, 0.92) * mm, "end": v(-0.39, 0.92) * mm});
            skLineSegment(sketch, "E1191", {"start": v(-0.39, 0.92) * mm, "end": v(-0.39, 0.92) * mm});
            skLineSegment(sketch, "E1192", {"start": v(-0.39, 0.92) * mm, "end": v(-0.38, 0.92) * mm});
            skLineSegment(sketch, "E1193", {"start": v(-0.38, 0.92) * mm, "end": v(-0.38, 0.92) * mm});
            skLineSegment(sketch, "E1194", {"start": v(-0.38, 0.92) * mm, "end": v(-0.38, 0.91) * mm});
            skLineSegment(sketch, "E1195", {"start": v(-0.38, 0.91) * mm, "end": v(-0.38, 0.91) * mm});
            skLineSegment(sketch, "E1196", {"start": v(-0.38, 0.91) * mm, "end": v(-0.38, 0.9) * mm});
            skLineSegment(sketch, "E1197", {"start": v(-0.38, 0.9) * mm, "end": v(-0.38, 0.9) * mm});
            skLineSegment(sketch, "E1198", {"start": v(-0.38, 0.9) * mm, "end": v(-0.38, 0.89) * mm});
            skLineSegment(sketch, "E1199", {"start": v(-0.38, 0.89) * mm, "end": v(-0.38, 0.89) * mm});
            skLineSegment(sketch, "E1200", {"start": v(-0.38, 0.89) * mm, "end": v(-0.38, 0.88) * mm});
            skLineSegment(sketch, "E1201", {"start": v(-0.38, 0.88) * mm, "end": v(-0.38, 0.88) * mm});
            skLineSegment(sketch, "E1202", {"start": v(-0.38, 0.88) * mm, "end": v(-0.39, 0.88) * mm});
            skLineSegment(sketch, "E1203", {"start": v(-0.39, 0.88) * mm, "end": v(-0.39, 0.88) * mm});
            skLineSegment(sketch, "E1204", {"start": v(-0.39, 0.88) * mm, "end": v(-0.4, 0.88) * mm});
            skLineSegment(sketch, "E1205", {"start": v(-0.4, 0.88) * mm, "end": v(-0.4, 0.88) * mm});
            skLineSegment(sketch, "E1206", {"start": v(-0.4, 0.88) * mm, "end": v(-0.4, 0.87) * mm});
            skLineSegment(sketch, "E1207", {"start": v(-0.4, 0.87) * mm, "end": v(-0.4, 0.8) * mm});
            skLineSegment(sketch, "E1208", {"start": v(-0.4, 0.8) * mm, "end": v(0.5, 0.8) * mm});
            skLineSegment(sketch, "E1209", {"start": v(0.5, 0.8) * mm, "end": v(0.5, 1) * mm});
            skLineSegment(sketch, "E1210", {"start": v(0.38, 1.2) * mm, "end": v(0.33, 1.2) * mm});
            skLineSegment(sketch, "E1211", {"start": v(0.33, 1.2) * mm, "end": v(0.3, 1.22) * mm});
            skLineSegment(sketch, "E1212", {"start": v(0.3, 1.22) * mm, "end": v(0.28, 1.2) * mm});
            skLineSegment(sketch, "E1213", {"start": v(0.28, 1.2) * mm, "end": v(0.22, 1.2) * mm});
            skLineSegment(sketch, "E1214", {"start": v(0.22, 1.2) * mm, "end": v(0.2, 1.22) * mm});
            skLineSegment(sketch, "E1215", {"start": v(0.2, 1.22) * mm, "end": v(0.18, 1.2) * mm});
            skLineSegment(sketch, "E1216", {"start": v(0.18, 1.2) * mm, "end": v(0.13, 1.2) * mm});
            skLineSegment(sketch, "E1217", {"start": v(0.13, 1.2) * mm, "end": v(0.1, 1.22) * mm});
            skLineSegment(sketch, "E1218", {"start": v(0.1, 1.22) * mm, "end": v(0.07, 1.2) * mm});
            skLineSegment(sketch, "E1219", {"start": v(0.07, 1.2) * mm, "end": v(0.03, 1.2) * mm});
            skLineSegment(sketch, "E1220", {"start": v(0.03, 1.2) * mm, "end": v(0, 1.22) * mm});
            skLineSegment(sketch, "E1221", {"start": v(0, 1.22) * mm, "end": v(-0.02, 1.2) * mm});
            skLineSegment(sketch, "E1222", {"start": v(-0.02, 1.2) * mm, "end": v(-0.07, 1.2) * mm});
            skLineSegment(sketch, "E1223", {"start": v(-0.07, 1.2) * mm, "end": v(-0.1, 1.22) * mm});
            skLineSegment(sketch, "E1224", {"start": v(-0.1, 1.22) * mm, "end": v(-0.1, 1.27) * mm});
            skLineSegment(sketch, "E1225", {"start": v(-0.1, 1.27) * mm, "end": v(-0.12, 1.3) * mm});
            skLineSegment(sketch, "E1226", {"start": v(-0.12, 1.3) * mm, "end": v(-0.18, 1.3) * mm});
            skLineSegment(sketch, "E1227", {"start": v(-0.18, 1.3) * mm, "end": v(-0.2, 1.27) * mm});
            skLineSegment(sketch, "E1228", {"start": v(-0.2, 1.27) * mm, "end": v(-0.22, 1.3) * mm});
            skLineSegment(sketch, "E1229", {"start": v(-0.22, 1.3) * mm, "end": v(-0.27, 1.3) * mm});
            skLineSegment(sketch, "E1230", {"start": v(-0.27, 1.3) * mm, "end": v(-0.3, 1.27) * mm});
            skLineSegment(sketch, "E1231", {"start": v(-0.3, 1.27) * mm, "end": v(-0.33, 1.3) * mm});
            skLineSegment(sketch, "E1232", {"start": v(-0.33, 1.3) * mm, "end": v(-0.38, 1.3) * mm});
            skLineSegment(sketch, "E1233", {"start": v(-0.38, 1.3) * mm, "end": v(-0.4, 1.27) * mm});
            skLineSegment(sketch, "E1234", {"start": v(-0.4, 1.27) * mm, "end": v(-0.4, 1.22) * mm});
            skLineSegment(sketch, "E1235", {"start": v(-0.4, 1.22) * mm, "end": v(-0.38, 1.2) * mm});
            skLineSegment(sketch, "E1236", {"start": v(-0.38, 1.2) * mm, "end": v(-0.33, 1.2) * mm});
            skLineSegment(sketch, "E1237", {"start": v(-0.33, 1.2) * mm, "end": v(-0.3, 1.22) * mm});
            skLineSegment(sketch, "E1238", {"start": v(-0.3, 1.22) * mm, "end": v(-0.27, 1.2) * mm});
            skLineSegment(sketch, "E1239", {"start": v(-0.27, 1.2) * mm, "end": v(-0.22, 1.2) * mm});
            skLineSegment(sketch, "E1240", {"start": v(-0.22, 1.2) * mm, "end": v(-0.2, 1.22) * mm});
            skLineSegment(sketch, "E1241", {"start": v(-0.2, 1.22) * mm, "end": v(-0.18, 1.2) * mm});
            skLineSegment(sketch, "E1242", {"start": v(-0.18, 1.2) * mm, "end": v(-0.12, 1.2) * mm});
            skLineSegment(sketch, "E1243", {"start": v(-0.12, 1.2) * mm, "end": v(-0.1, 1.22) * mm});
            skLineSegment(sketch, "E1244", {"start": v(-0.1, 1.27) * mm, "end": v(-0.07, 1.3) * mm});
            skLineSegment(sketch, "E1245", {"start": v(-0.07, 1.3) * mm, "end": v(-0.02, 1.3) * mm});
            skLineSegment(sketch, "E1246", {"start": v(-0.02, 1.3) * mm, "end": v(0, 1.27) * mm});
            skLineSegment(sketch, "E1247", {"start": v(0, 1.27) * mm, "end": v(0.03, 1.3) * mm});
            skLineSegment(sketch, "E1248", {"start": v(0.03, 1.3) * mm, "end": v(0.07, 1.3) * mm});
            skLineSegment(sketch, "E1249", {"start": v(0.07, 1.3) * mm, "end": v(0.1, 1.27) * mm});
            skLineSegment(sketch, "E1250", {"start": v(0.1, 1.27) * mm, "end": v(0.13, 1.3) * mm});
            skLineSegment(sketch, "E1251", {"start": v(0.13, 1.3) * mm, "end": v(0.18, 1.3) * mm});
            skLineSegment(sketch, "E1252", {"start": v(0.18, 1.3) * mm, "end": v(0.2, 1.27) * mm});
            skLineSegment(sketch, "E1253", {"start": v(0.2, 1.27) * mm, "end": v(0.22, 1.3) * mm});
            skLineSegment(sketch, "E1254", {"start": v(0.22, 1.3) * mm, "end": v(0.28, 1.3) * mm});
            skLineSegment(sketch, "E1255", {"start": v(0.28, 1.3) * mm, "end": v(0.3, 1.27) * mm});
            skLineSegment(sketch, "E1256", {"start": v(0.3, 1.27) * mm, "end": v(0.33, 1.3) * mm});
            skLineSegment(sketch, "E1257", {"start": v(0.33, 1.3) * mm, "end": v(0.38, 1.3) * mm});
            skLineSegment(sketch, "E1258", {"start": v(0.38, 1.3) * mm, "end": v(0.4, 1.27) * mm});
            skLineSegment(sketch, "E1259", {"start": v(0.4, 1.27) * mm, "end": v(0.4, 1.22) * mm});
            skLineSegment(sketch, "E1260", {"start": v(0.4, 1.22) * mm, "end": v(0.38, 1.2) * mm});
            skLineSegment(sketch, "E1261", {"start": v(0.23, 1.34) * mm, "end": v(0.22, 1.33) * mm});
            skLineSegment(sketch, "E1262", {"start": v(0.22, 1.33) * mm, "end": v(0.2, 1.33) * mm});
            skLineSegment(sketch, "E1263", {"start": v(0.2, 1.33) * mm, "end": v(0.2, 1.34) * mm});
            skLineSegment(sketch, "E1264", {"start": v(0.2, 1.36) * mm, "end": v(0.22, 1.36) * mm});
            skLineSegment(sketch, "E1265", {"start": v(0.22, 1.36) * mm, "end": v(0.23, 1.35) * mm});
            skLineSegment(sketch, "E1266", {"start": v(0.23, 1.35) * mm, "end": v(0.23, 1.34) * mm});
            skLineSegment(sketch, "E1267", {"start": v(0.2, 1.36) * mm, "end": v(0.2, 1.36) * mm});
            skLineSegment(sketch, "E1268", {"start": v(0.2, 1.36) * mm, "end": v(0.2, 1.37) * mm});
            skLineSegment(sketch, "E1269", {"start": v(0.2, 1.37) * mm, "end": v(0.2, 1.38) * mm});
            skLineSegment(sketch, "E1270", {"start": v(0.2, 1.38) * mm, "end": v(0.22, 1.38) * mm});
            skLineSegment(sketch, "E1271", {"start": v(0.22, 1.38) * mm, "end": v(0.23, 1.37) * mm});
            skLineSegment(sketch, "E1272", {"start": v(0.18, 1.37) * mm, "end": v(0.18, 1.34) * mm});
            skLineSegment(sketch, "E1273", {"start": v(0.18, 1.34) * mm, "end": v(0.18, 1.33) * mm});
            skLineSegment(sketch, "E1274", {"start": v(0.18, 1.33) * mm, "end": v(0.16, 1.33) * mm});
            skLineSegment(sketch, "E1275", {"start": v(0.16, 1.33) * mm, "end": v(0.16, 1.38) * mm});
            skLineSegment(sketch, "E1276", {"start": v(0.16, 1.38) * mm, "end": v(0.18, 1.38) * mm});
            skLineSegment(sketch, "E1277", {"start": v(0.18, 1.38) * mm, "end": v(0.18, 1.37) * mm});
            skLineSegment(sketch, "E1278", {"start": v(0.14, 1.38) * mm, "end": v(0.1, 1.38) * mm});
            skLineSegment(sketch, "E1279", {"start": v(0.1, 1.38) * mm, "end": v(0.1, 1.33) * mm});
            skLineSegment(sketch, "E1280", {"start": v(0.1, 1.33) * mm, "end": v(0.14, 1.33) * mm});
            skLineSegment(sketch, "E1281", {"start": v(0.12, 1.36) * mm, "end": v(0.1, 1.36) * mm});
            skLineSegment(sketch, "E1282", {"start": v(0.1, 1.33) * mm, "end": v(0.06, 1.33) * mm});
            skLineSegment(sketch, "E1283", {"start": v(0.06, 1.33) * mm, "end": v(0.06, 1.38) * mm});
            skLineSegment(sketch, "E1284", {"start": v(-0.17, 1.37) * mm, "end": v(-0.17, 1.34) * mm});
            skLineSegment(sketch, "E1285", {"start": v(-0.17, 1.34) * mm, "end": v(-0.18, 1.33) * mm});
            skLineSegment(sketch, "E1286", {"start": v(-0.18, 1.33) * mm, "end": v(-0.2, 1.33) * mm});
            skLineSegment(sketch, "E1287", {"start": v(-0.2, 1.33) * mm, "end": v(-0.2, 1.34) * mm});
            skLineSegment(sketch, "E1288", {"start": v(-0.2, 1.34) * mm, "end": v(-0.2, 1.37) * mm});
            skLineSegment(sketch, "E1289", {"start": v(-0.2, 1.37) * mm, "end": v(-0.2, 1.38) * mm});
            skLineSegment(sketch, "E1290", {"start": v(-0.2, 1.38) * mm, "end": v(-0.18, 1.38) * mm});
            skLineSegment(sketch, "E1291", {"start": v(-0.18, 1.38) * mm, "end": v(-0.17, 1.37) * mm});
            skLineSegment(sketch, "E1292", {"start": v(-0.22, 1.38) * mm, "end": v(-0.23, 1.38) * mm});
            skLineSegment(sketch, "E1293", {"start": v(-0.23, 1.38) * mm, "end": v(-0.23, 1.33) * mm});
            skLineSegment(sketch, "E1294", {"start": v(-0.23, 1.33) * mm, "end": v(-0.22, 1.33) * mm});
            skLineSegment(sketch, "E1295", {"start": v(-0.25, 1.36) * mm, "end": v(-0.25, 1.37) * mm});
            skLineSegment(sketch, "E1296", {"start": v(-0.25, 1.37) * mm, "end": v(-0.26, 1.38) * mm});
            skLineSegment(sketch, "E1297", {"start": v(-0.26, 1.38) * mm, "end": v(-0.28, 1.38) * mm});
            skLineSegment(sketch, "E1298", {"start": v(-0.28, 1.38) * mm, "end": v(-0.28, 1.33) * mm});
            skLineSegment(sketch, "E1299", {"start": v(-0.28, 1.35) * mm, "end": v(-0.26, 1.35) * mm});
            skLineSegment(sketch, "E1300", {"start": v(-0.26, 1.35) * mm, "end": v(-0.25, 1.36) * mm});
            skLineSegment(sketch, "E1301", {"start": v(-0.3, 1.36) * mm, "end": v(-0.31, 1.36) * mm});
            skLineSegment(sketch, "E1302", {"start": v(-0.3, 1.36) * mm, "end": v(-0.3, 1.34) * mm});
            skLineSegment(sketch, "E1303", {"start": v(-0.3, 1.34) * mm, "end": v(-0.3, 1.33) * mm});
            skLineSegment(sketch, "E1304", {"start": v(-0.3, 1.33) * mm, "end": v(-0.32, 1.33) * mm});
            skLineSegment(sketch, "E1305", {"start": v(-0.32, 1.33) * mm, "end": v(-0.33, 1.34) * mm});
            skLineSegment(sketch, "E1306", {"start": v(-0.33, 1.34) * mm, "end": v(-0.33, 1.37) * mm});
            skLineSegment(sketch, "E1307", {"start": v(-0.33, 1.37) * mm, "end": v(-0.32, 1.38) * mm});
            skLineSegment(sketch, "E1308", {"start": v(-0.32, 1.38) * mm, "end": v(-0.3, 1.38) * mm});
            skLineSegment(sketch, "E1309", {"start": v(-0.3, 1.38) * mm, "end": v(-0.3, 1.37) * mm});
            skLineSegment(sketch, "E1310", {"start": v(-0.4, 1.29) * mm, "end": v(-0.4, 1.3) * mm});
            skLineSegment(sketch, "E1311", {"start": v(-0.4, 1.3) * mm, "end": v(-0.49, 1.3) * mm});
            skLineSegment(sketch, "E1312", {"start": v(-0.49, 1.3) * mm, "end": v(-0.5, 1.29) * mm});
            skLineSegment(sketch, "E1313", {"start": v(-0.5, 1.29) * mm, "end": v(-0.51, 1.3) * mm});
            skLineSegment(sketch, "E1314", {"start": v(-0.51, 1.3) * mm, "end": v(-0.6, 1.3) * mm});
            skLineSegment(sketch, "E1315", {"start": v(-0.6, 1.3) * mm, "end": v(-0.6, 1.29) * mm});
            skLineSegment(sketch, "E1316", {"start": v(-0.6, 1.29) * mm, "end": v(-0.6, 1.2) * mm});
            skLineSegment(sketch, "E1317", {"start": v(-0.6, 1.2) * mm, "end": v(-0.6, 1.2) * mm});
            skLineSegment(sketch, "E1318", {"start": v(-0.6, 1.2) * mm, "end": v(-0.51, 1.2) * mm});
            skLineSegment(sketch, "E1319", {"start": v(-0.51, 1.2) * mm, "end": v(-0.5, 1.2) * mm});
            skLineSegment(sketch, "E1320", {"start": v(-0.5, 1.2) * mm, "end": v(-0.49, 1.2) * mm});
            skLineSegment(sketch, "E1321", {"start": v(-0.49, 1.2) * mm, "end": v(-0.4, 1.2) * mm});
            skLineSegment(sketch, "E1322", {"start": v(-0.4, 1.2) * mm, "end": v(-0.4, 1.2) * mm});
            skLineSegment(sketch, "E1323", {"start": v(-0.4, 1.2) * mm, "end": v(-0.4, 1.29) * mm});
            skLineSegment(sketch, "E1324", {"start": v(-0.45, 1.33) * mm, "end": v(-0.45, 1.38) * mm});
            skLineSegment(sketch, "E1325", {"start": v(-0.44, 1.38) * mm, "end": v(-0.46, 1.38) * mm});
            skLineSegment(sketch, "E1326", {"start": v(-0.48, 1.37) * mm, "end": v(-0.49, 1.38) * mm});
            skLineSegment(sketch, "E1327", {"start": v(-0.49, 1.38) * mm, "end": v(-0.5, 1.38) * mm});
            skLineSegment(sketch, "E1328", {"start": v(-0.5, 1.38) * mm, "end": v(-0.51, 1.37) * mm});
            skLineSegment(sketch, "E1329", {"start": v(-0.51, 1.37) * mm, "end": v(-0.51, 1.36) * mm});
            skLineSegment(sketch, "E1330", {"start": v(-0.51, 1.36) * mm, "end": v(-0.5, 1.36) * mm});
            skLineSegment(sketch, "E1331", {"start": v(-0.5, 1.36) * mm, "end": v(-0.49, 1.36) * mm});
            skLineSegment(sketch, "E1332", {"start": v(-0.49, 1.36) * mm, "end": v(-0.48, 1.35) * mm});
            skLineSegment(sketch, "E1333", {"start": v(-0.48, 1.35) * mm, "end": v(-0.48, 1.34) * mm});
            skLineSegment(sketch, "E1334", {"start": v(-0.48, 1.34) * mm, "end": v(-0.49, 1.33) * mm});
            skLineSegment(sketch, "E1335", {"start": v(-0.49, 1.33) * mm, "end": v(-0.5, 1.33) * mm});
            skLineSegment(sketch, "E1336", {"start": v(-0.5, 1.33) * mm, "end": v(-0.51, 1.34) * mm});
            skLineSegment(sketch, "E1337", {"start": v(-0.53, 1.33) * mm, "end": v(-0.54, 1.35) * mm});
            skLineSegment(sketch, "E1338", {"start": v(-0.53, 1.35) * mm, "end": v(-0.56, 1.35) * mm});
            skLineSegment(sketch, "E1339", {"start": v(-0.56, 1.33) * mm, "end": v(-0.56, 1.38) * mm});
            skLineSegment(sketch, "E1340", {"start": v(-0.56, 1.38) * mm, "end": v(-0.53, 1.38) * mm});
            skLineSegment(sketch, "E1341", {"start": v(-0.53, 1.38) * mm, "end": v(-0.53, 1.37) * mm});
            skLineSegment(sketch, "E1342", {"start": v(-0.53, 1.37) * mm, "end": v(-0.53, 1.36) * mm});
            skLineSegment(sketch, "E1343", {"start": v(-0.53, 1.36) * mm, "end": v(-0.53, 1.35) * mm});
            skLineSegment(sketch, "E1344", {"start": v(-1.01, 0.93) * mm, "end": v(-1.01, 0.77) * mm});
            skLineSegment(sketch, "E1345", {"start": v(-1.01, 0.77) * mm, "end": v(-1.01, 0.77) * mm});
            skLineSegment(sketch, "E1346", {"start": v(-1.01, 0.77) * mm, "end": v(-1.01, 0.76) * mm});
            skLineSegment(sketch, "E1347", {"start": v(-1.01, 0.76) * mm, "end": v(-1.01, 0.76) * mm});
            skLineSegment(sketch, "E1348", {"start": v(-1.01, 0.76) * mm, "end": v(-1.02, 0.76) * mm});
            skLineSegment(sketch, "E1349", {"start": v(-1.02, 0.76) * mm, "end": v(-1.02, 0.76) * mm});
            skLineSegment(sketch, "E1350", {"start": v(-1.02, 0.76) * mm, "end": v(-1.08, 0.76) * mm});
            skLineSegment(sketch, "E1351", {"start": v(-1.08, 0.76) * mm, "end": v(-1.08, 0.76) * mm});
            skLineSegment(sketch, "E1352", {"start": v(-1.08, 0.76) * mm, "end": v(-1.09, 0.76) * mm});
            skLineSegment(sketch, "E1353", {"start": v(-1.09, 0.76) * mm, "end": v(-1.09, 0.76) * mm});
            skLineSegment(sketch, "E1354", {"start": v(-1.09, 0.76) * mm, "end": v(-1.09, 0.77) * mm});
            skLineSegment(sketch, "E1355", {"start": v(-1.09, 0.77) * mm, "end": v(-1.09, 0.77) * mm});
            skLineSegment(sketch, "E1356", {"start": v(-1.09, 0.77) * mm, "end": v(-1.09, 0.93) * mm});
            skLineSegment(sketch, "E1357", {"start": v(-1.09, 0.93) * mm, "end": v(-1.09, 0.93) * mm});
            skLineSegment(sketch, "E1358", {"start": v(-1.09, 0.93) * mm, "end": v(-1.09, 0.94) * mm});
            skLineSegment(sketch, "E1359", {"start": v(-1.09, 0.94) * mm, "end": v(-1.09, 0.94) * mm});
            skLineSegment(sketch, "E1360", {"start": v(-1.09, 0.94) * mm, "end": v(-1.08, 0.94) * mm});
            skLineSegment(sketch, "E1361", {"start": v(-1.08, 0.94) * mm, "end": v(-1.08, 0.94) * mm});
            skLineSegment(sketch, "E1362", {"start": v(-1.08, 0.94) * mm, "end": v(-1.02, 0.94) * mm});
            skLineSegment(sketch, "E1363", {"start": v(-1.02, 0.94) * mm, "end": v(-1.02, 0.94) * mm});
            skLineSegment(sketch, "E1364", {"start": v(-1.02, 0.94) * mm, "end": v(-1.01, 0.94) * mm});
            skLineSegment(sketch, "E1365", {"start": v(-1.01, 0.94) * mm, "end": v(-1.01, 0.94) * mm});
            skLineSegment(sketch, "E1366", {"start": v(-1.01, 0.94) * mm, "end": v(-1.01, 0.93) * mm});
            skLineSegment(sketch, "E1367", {"start": v(-1.01, 0.93) * mm, "end": v(-1.01, 0.93) * mm});
            skLineSegment(sketch, "E1368", {"start": v(-1.05, 0.87) * mm, "end": v(-1.05, 0.85) * mm});
            skLineSegment(sketch, "E1369", {"start": v(-1.05, 0.85) * mm, "end": v(-1.07, 0.85) * mm});
            skLineSegment(sketch, "E1370", {"start": v(-1.05, 0.85) * mm, "end": v(-1.07, 0.8) * mm});
            skLineSegment(sketch, "E1371", {"start": v(-1.07, 0.8) * mm, "end": v(-1.02, 0.8) * mm});
            skLineSegment(sketch, "E1372", {"start": v(-1.02, 0.8) * mm, "end": v(-1.05, 0.85) * mm});
            skLineSegment(sketch, "E1373", {"start": v(-1.05, 0.85) * mm, "end": v(-1.02, 0.85) * mm});
            skLineSegment(sketch, "E1374", {"start": v(-1.05, 0.85) * mm, "end": v(-1.05, 0.79) * mm});
            skLineSegment(sketch, "E1375", {"start": v(-1.1, 0.77) * mm, "end": v(-1.1, 0.93) * mm});
            skLineSegment(sketch, "E1376", {"start": v(-1.1, 0.93) * mm, "end": v(-1.11, 0.93) * mm});
            skLineSegment(sketch, "E1377", {"start": v(-1.11, 0.93) * mm, "end": v(-1.11, 0.93) * mm});
            skLineSegment(sketch, "E1378", {"start": v(-1.11, 0.93) * mm, "end": v(-1.11, 0.94) * mm});
            skLineSegment(sketch, "E1379", {"start": v(-1.11, 0.94) * mm, "end": v(-1.11, 0.94) * mm});
            skLineSegment(sketch, "E1380", {"start": v(-1.11, 0.94) * mm, "end": v(-1.12, 0.94) * mm});
            skLineSegment(sketch, "E1381", {"start": v(-1.12, 0.94) * mm, "end": v(-1.12, 0.94) * mm});
            skLineSegment(sketch, "E1382", {"start": v(-1.12, 0.94) * mm, "end": v(-1.18, 0.94) * mm});
            skLineSegment(sketch, "E1383", {"start": v(-1.18, 0.94) * mm, "end": v(-1.18, 0.94) * mm});
            skLineSegment(sketch, "E1384", {"start": v(-1.18, 0.94) * mm, "end": v(-1.19, 0.94) * mm});
            skLineSegment(sketch, "E1385", {"start": v(-1.19, 0.94) * mm, "end": v(-1.19, 0.94) * mm});
            skLineSegment(sketch, "E1386", {"start": v(-1.19, 0.94) * mm, "end": v(-1.19, 0.93) * mm});
            skLineSegment(sketch, "E1387", {"start": v(-1.19, 0.93) * mm, "end": v(-1.19, 0.93) * mm});
            skLineSegment(sketch, "E1388", {"start": v(-1.19, 0.93) * mm, "end": v(-1.19, 0.77) * mm});
            skLineSegment(sketch, "E1389", {"start": v(-1.2, 0.77) * mm, "end": v(-1.2, 0.93) * mm});
            skLineSegment(sketch, "E1390", {"start": v(-1.2, 0.93) * mm, "end": v(-1.3, 0.93) * mm});
            skLineSegment(sketch, "E1391", {"start": v(-1.3, 0.93) * mm, "end": v(-1.3, 0.77) * mm});
            skLineSegment(sketch, "E1392", {"start": v(-1.3, 0.77) * mm, "end": v(-1.2, 0.77) * mm});
            skLineSegment(sketch, "E1393", {"start": v(-1.19, 0.77) * mm, "end": v(-1.19, 0.77) * mm});
            skLineSegment(sketch, "E1394", {"start": v(-1.19, 0.77) * mm, "end": v(-1.19, 0.76) * mm});
            skLineSegment(sketch, "E1395", {"start": v(-1.19, 0.76) * mm, "end": v(-1.19, 0.76) * mm});
            skLineSegment(sketch, "E1396", {"start": v(-1.19, 0.76) * mm, "end": v(-1.18, 0.76) * mm});
            skLineSegment(sketch, "E1397", {"start": v(-1.18, 0.76) * mm, "end": v(-1.18, 0.76) * mm});
            skLineSegment(sketch, "E1398", {"start": v(-1.18, 0.76) * mm, "end": v(-1.12, 0.76) * mm});
            skLineSegment(sketch, "E1399", {"start": v(-1.12, 0.76) * mm, "end": v(-1.12, 0.76) * mm});
            skLineSegment(sketch, "E1400", {"start": v(-1.12, 0.76) * mm, "end": v(-1.11, 0.76) * mm});
            skLineSegment(sketch, "E1401", {"start": v(-1.11, 0.76) * mm, "end": v(-1.11, 0.76) * mm});
            skLineSegment(sketch, "E1402", {"start": v(-1.11, 0.76) * mm, "end": v(-1.11, 0.77) * mm});
            skLineSegment(sketch, "E1403", {"start": v(-1.11, 0.77) * mm, "end": v(-1.11, 0.77) * mm});
            skLineSegment(sketch, "E1404", {"start": v(-1.11, 0.77) * mm, "end": v(-1.1, 0.77) * mm});
            skLineSegment(sketch, "E1405", {"start": v(-1.13, 0.8) * mm, "end": v(-1.15, 0.85) * mm});
            skLineSegment(sketch, "E1406", {"start": v(-1.15, 0.85) * mm, "end": v(-1.17, 0.85) * mm});
            skLineSegment(sketch, "E1407", {"start": v(-1.15, 0.85) * mm, "end": v(-1.13, 0.85) * mm});
            skLineSegment(sketch, "E1408", {"start": v(-1.15, 0.85) * mm, "end": v(-1.17, 0.8) * mm});
            skLineSegment(sketch, "E1409", {"start": v(-1.17, 0.8) * mm, "end": v(-1.13, 0.8) * mm});
            skLineSegment(sketch, "E1410", {"start": v(-1.15, 0.79) * mm, "end": v(-1.15, 0.85) * mm});
            skLineSegment(sketch, "E1411", {"start": v(-1.15, 0.85) * mm, "end": v(-1.15, 0.87) * mm});
            skLineSegment(sketch, "E1412", {"start": v(-1.23, 0.85) * mm, "end": v(-1.25, 0.85) * mm});
            skLineSegment(sketch, "E1413", {"start": v(-1.25, 0.85) * mm, "end": v(-1.27, 0.85) * mm});
            skLineSegment(sketch, "E1414", {"start": v(-1.25, 0.85) * mm, "end": v(-1.27, 0.8) * mm});
            skLineSegment(sketch, "E1415", {"start": v(-1.27, 0.8) * mm, "end": v(-1.23, 0.8) * mm});
            skLineSegment(sketch, "E1416", {"start": v(-1.23, 0.8) * mm, "end": v(-1.25, 0.85) * mm});
            skLineSegment(sketch, "E1417", {"start": v(-1.25, 0.85) * mm, "end": v(-1.25, 0.79) * mm});
            skLineSegment(sketch, "E1418", {"start": v(-1.23, 0.84) * mm, "end": v(-1.23, 0.85) * mm});
            skLineSegment(sketch, "E1419", {"start": v(-1.25, 0.85) * mm, "end": v(-1.25, 0.87) * mm});
            skLineSegment(sketch, "E1420", {"start": v(-1.39, 0.55) * mm, "end": v(-1.48, 0.55) * mm});
            skLineSegment(sketch, "E1421", {"start": v(-1.48, 0.55) * mm, "end": v(-1.74, 0.55) * mm});
            skLineSegment(sketch, "E1422", {"start": v(-1.74, 0.55) * mm, "end": v(-1.75, 0.55) * mm});
            skLineSegment(sketch, "E1423", {"start": v(-1.75, 0.55) * mm, "end": v(-1.75, 0.15) * mm});
            skLineSegment(sketch, "E1424", {"start": v(-1.75, 0.15) * mm, "end": v(-1.74, 0.15) * mm});
            skLineSegment(sketch, "E1425", {"start": v(-1.74, 0.15) * mm, "end": v(-1.48, 0.15) * mm});
            skLineSegment(sketch, "E1426", {"start": v(-1.48, 0.15) * mm, "end": v(-1.39, 0.15) * mm});
            skLineSegment(sketch, "E1427", {"start": v(-1.39, 0.15) * mm, "end": v(-1.39, 0.55) * mm});
            skLineSegment(sketch, "E1428", {"start": v(-1.48, 0.55) * mm, "end": v(-1.48, 0.48) * mm});
            skLineSegment(sketch, "E1429", {"start": v(-1.48, 0.48) * mm, "end": v(-1.48, 0.41) * mm});
            skLineSegment(sketch, "E1430", {"start": v(-1.48, 0.41) * mm, "end": v(-1.48, 0.28) * mm});
            skLineSegment(sketch, "E1431", {"start": v(-1.48, 0.28) * mm, "end": v(-1.48, 0.21) * mm});
            skLineSegment(sketch, "E1432", {"start": v(-1.48, 0.21) * mm, "end": v(-1.48, 0.15) * mm});
            skLineSegment(sketch, "E1433", {"start": v(-1.6, 0.25) * mm, "end": v(-1.6, 0.25) * mm});
            skLineSegment(sketch, "E1434", {"start": v(-1.6, 0.25) * mm, "end": v(-1.6, 0.26) * mm});
            skLineSegment(sketch, "E1435", {"start": v(-1.6, 0.26) * mm, "end": v(-1.6, 0.26) * mm});
            skLineSegment(sketch, "E1436", {"start": v(-1.6, 0.26) * mm, "end": v(-1.6, 0.27) * mm});
            skLineSegment(sketch, "E1437", {"start": v(-1.6, 0.27) * mm, "end": v(-1.6, 0.27) * mm});
            skLineSegment(sketch, "E1438", {"start": v(-1.6, 0.27) * mm, "end": v(-1.6, 0.28) * mm});
            skLineSegment(sketch, "E1439", {"start": v(-1.6, 0.28) * mm, "end": v(-1.6, 0.28) * mm});
            skLineSegment(sketch, "E1440", {"start": v(-1.6, 0.28) * mm, "end": v(-1.6, 0.29) * mm});
            skLineSegment(sketch, "E1441", {"start": v(-1.6, 0.29) * mm, "end": v(-1.6, 0.29) * mm});
            skLineSegment(sketch, "E1442", {"start": v(-1.6, 0.29) * mm, "end": v(-1.6, 0.3) * mm});
            skLineSegment(sketch, "E1443", {"start": v(-1.6, 0.3) * mm, "end": v(-1.59, 0.3) * mm});
            skLineSegment(sketch, "E1444", {"start": v(-1.59, 0.3) * mm, "end": v(-1.58, 0.3) * mm});
            skLineSegment(sketch, "E1445", {"start": v(-1.58, 0.3) * mm, "end": v(-1.58, 0.3) * mm});
            skLineSegment(sketch, "E1446", {"start": v(-1.58, 0.3) * mm, "end": v(-1.57, 0.3) * mm});
            skLineSegment(sketch, "E1447", {"start": v(-1.57, 0.3) * mm, "end": v(-1.57, 0.3) * mm});
            skLineSegment(sketch, "E1448", {"start": v(-1.57, 0.3) * mm, "end": v(-1.56, 0.3) * mm});
            skLineSegment(sketch, "E1449", {"start": v(-1.56, 0.3) * mm, "end": v(-1.56, 0.3) * mm});
            skLineSegment(sketch, "E1450", {"start": v(-1.56, 0.3) * mm, "end": v(-1.55, 0.3) * mm});
            skLineSegment(sketch, "E1451", {"start": v(-1.55, 0.3) * mm, "end": v(-1.55, 0.3) * mm});
            skLineSegment(sketch, "E1452", {"start": v(-1.55, 0.3) * mm, "end": v(-1.54, 0.3) * mm});
            skLineSegment(sketch, "E1453", {"start": v(-1.54, 0.3) * mm, "end": v(-1.54, 0.3) * mm});
            skLineSegment(sketch, "E1454", {"start": v(-1.54, 0.3) * mm, "end": v(-1.53, 0.3) * mm});
            skLineSegment(sketch, "E1455", {"start": v(-1.53, 0.3) * mm, "end": v(-1.53, 0.3) * mm});
            skLineSegment(sketch, "E1456", {"start": v(-1.53, 0.3) * mm, "end": v(-1.52, 0.3) * mm});
            skLineSegment(sketch, "E1457", {"start": v(-1.52, 0.3) * mm, "end": v(-1.52, 0.3) * mm});
            skLineSegment(sketch, "E1458", {"start": v(-1.52, 0.3) * mm, "end": v(-1.51, 0.3) * mm});
            skLineSegment(sketch, "E1459", {"start": v(-1.51, 0.3) * mm, "end": v(-1.5, 0.3) * mm});
            skLineSegment(sketch, "E1460", {"start": v(-1.5, 0.3) * mm, "end": v(-1.5, 0.29) * mm});
            skLineSegment(sketch, "E1461", {"start": v(-1.5, 0.29) * mm, "end": v(-1.5, 0.28) * mm});
            skLineSegment(sketch, "E1462", {"start": v(-1.5, 0.28) * mm, "end": v(-1.5, 0.28) * mm});
            skLineSegment(sketch, "E1463", {"start": v(-1.5, 0.28) * mm, "end": v(-1.5, 0.27) * mm});
            skLineSegment(sketch, "E1464", {"start": v(-1.5, 0.27) * mm, "end": v(-1.5, 0.27) * mm});
            skLineSegment(sketch, "E1465", {"start": v(-1.5, 0.27) * mm, "end": v(-1.5, 0.26) * mm});
            skLineSegment(sketch, "E1466", {"start": v(-1.5, 0.26) * mm, "end": v(-1.5, 0.26) * mm});
            skLineSegment(sketch, "E1467", {"start": v(-1.5, 0.26) * mm, "end": v(-1.5, 0.25) * mm});
            skLineSegment(sketch, "E1468", {"start": v(-1.5, 0.25) * mm, "end": v(-1.5, 0.25) * mm});
            skLineSegment(sketch, "E1469", {"start": v(-1.5, 0.25) * mm, "end": v(-1.5, 0.24) * mm});
            skLineSegment(sketch, "E1470", {"start": v(-1.5, 0.24) * mm, "end": v(-1.5, 0.24) * mm});
            skLineSegment(sketch, "E1471", {"start": v(-1.5, 0.24) * mm, "end": v(-1.5, 0.23) * mm});
            skLineSegment(sketch, "E1472", {"start": v(-1.5, 0.23) * mm, "end": v(-1.5, 0.23) * mm});
            skLineSegment(sketch, "E1473", {"start": v(-1.5, 0.23) * mm, "end": v(-1.5, 0.22) * mm});
            skLineSegment(sketch, "E1474", {"start": v(-1.5, 0.22) * mm, "end": v(-1.5, 0.22) * mm});
            skLineSegment(sketch, "E1475", {"start": v(-1.5, 0.22) * mm, "end": v(-1.5, 0.21) * mm});
            skLineSegment(sketch, "E1476", {"start": v(-1.5, 0.21) * mm, "end": v(-1.5, 0.2) * mm});
            skLineSegment(sketch, "E1477", {"start": v(-1.5, 0.2) * mm, "end": v(-1.51, 0.2) * mm});
            skLineSegment(sketch, "E1478", {"start": v(-1.51, 0.2) * mm, "end": v(-1.52, 0.2) * mm});
            skLineSegment(sketch, "E1479", {"start": v(-1.52, 0.2) * mm, "end": v(-1.52, 0.2) * mm});
            skLineSegment(sketch, "E1480", {"start": v(-1.52, 0.2) * mm, "end": v(-1.53, 0.2) * mm});
            skLineSegment(sketch, "E1481", {"start": v(-1.53, 0.2) * mm, "end": v(-1.53, 0.2) * mm});
            skLineSegment(sketch, "E1482", {"start": v(-1.53, 0.2) * mm, "end": v(-1.54, 0.2) * mm});
            skLineSegment(sketch, "E1483", {"start": v(-1.54, 0.2) * mm, "end": v(-1.54, 0.2) * mm});
            skLineSegment(sketch, "E1484", {"start": v(-1.54, 0.2) * mm, "end": v(-1.55, 0.2) * mm});
            skLineSegment(sketch, "E1485", {"start": v(-1.55, 0.2) * mm, "end": v(-1.55, 0.2) * mm});
            skLineSegment(sketch, "E1486", {"start": v(-1.55, 0.2) * mm, "end": v(-1.56, 0.2) * mm});
            skLineSegment(sketch, "E1487", {"start": v(-1.56, 0.2) * mm, "end": v(-1.56, 0.2) * mm});
            skLineSegment(sketch, "E1488", {"start": v(-1.56, 0.2) * mm, "end": v(-1.57, 0.2) * mm});
            skLineSegment(sketch, "E1489", {"start": v(-1.57, 0.2) * mm, "end": v(-1.57, 0.2) * mm});
            skLineSegment(sketch, "E1490", {"start": v(-1.57, 0.2) * mm, "end": v(-1.58, 0.2) * mm});
            skLineSegment(sketch, "E1491", {"start": v(-1.58, 0.2) * mm, "end": v(-1.58, 0.2) * mm});
            skLineSegment(sketch, "E1492", {"start": v(-1.58, 0.2) * mm, "end": v(-1.59, 0.2) * mm});
            skLineSegment(sketch, "E1493", {"start": v(-1.59, 0.2) * mm, "end": v(-1.6, 0.2) * mm});
            skLineSegment(sketch, "E1494", {"start": v(-1.6, 0.2) * mm, "end": v(-1.6, 0.21) * mm});
            skLineSegment(sketch, "E1495", {"start": v(-1.6, 0.21) * mm, "end": v(-1.6, 0.21) * mm});
            skLineSegment(sketch, "E1496", {"start": v(-1.6, 0.21) * mm, "end": v(-1.6, 0.22) * mm});
            skLineSegment(sketch, "E1497", {"start": v(-1.6, 0.22) * mm, "end": v(-1.6, 0.22) * mm});
            skLineSegment(sketch, "E1498", {"start": v(-1.6, 0.22) * mm, "end": v(-1.6, 0.23) * mm});
            skLineSegment(sketch, "E1499", {"start": v(-1.6, 0.23) * mm, "end": v(-1.6, 0.23) * mm});
            skLineSegment(sketch, "E1500", {"start": v(-1.6, 0.23) * mm, "end": v(-1.6, 0.24) * mm});
            skLineSegment(sketch, "E1501", {"start": v(-1.6, 0.24) * mm, "end": v(-1.6, 0.24) * mm});
            skLineSegment(sketch, "E1502", {"start": v(-1.6, 0.24) * mm, "end": v(-1.6, 0.25) * mm});
            skLineSegment(sketch, "E1503", {"start": v(-1.7, 0.25) * mm, "end": v(-1.7, 0.25) * mm});
            skLineSegment(sketch, "E1504", {"start": v(-1.7, 0.25) * mm, "end": v(-1.7, 0.26) * mm});
            skLineSegment(sketch, "E1505", {"start": v(-1.7, 0.26) * mm, "end": v(-1.7, 0.26) * mm});
            skLineSegment(sketch, "E1506", {"start": v(-1.7, 0.26) * mm, "end": v(-1.7, 0.27) * mm});
            skLineSegment(sketch, "E1507", {"start": v(-1.7, 0.27) * mm, "end": v(-1.7, 0.27) * mm});
            skLineSegment(sketch, "E1508", {"start": v(-1.7, 0.27) * mm, "end": v(-1.69, 0.27) * mm});
            skLineSegment(sketch, "E1509", {"start": v(-1.69, 0.27) * mm, "end": v(-1.68, 0.27) * mm});
            skLineSegment(sketch, "E1510", {"start": v(-1.68, 0.27) * mm, "end": v(-1.68, 0.27) * mm});
            skLineSegment(sketch, "E1511", {"start": v(-1.68, 0.27) * mm, "end": v(-1.67, 0.27) * mm});
            skLineSegment(sketch, "E1512", {"start": v(-1.67, 0.27) * mm, "end": v(-1.67, 0.26) * mm});
            skLineSegment(sketch, "E1513", {"start": v(-1.67, 0.26) * mm, "end": v(-1.67, 0.26) * mm});
            skLineSegment(sketch, "E1514", {"start": v(-1.67, 0.26) * mm, "end": v(-1.67, 0.25) * mm});
            skLineSegment(sketch, "E1515", {"start": v(-1.67, 0.25) * mm, "end": v(-1.67, 0.25) * mm});
            skLineSegment(sketch, "E1516", {"start": v(-1.67, 0.25) * mm, "end": v(-1.67, 0.24) * mm});
            skLineSegment(sketch, "E1517", {"start": v(-1.67, 0.24) * mm, "end": v(-1.67, 0.24) * mm});
            skLineSegment(sketch, "E1518", {"start": v(-1.67, 0.24) * mm, "end": v(-1.67, 0.23) * mm});
            skLineSegment(sketch, "E1519", {"start": v(-1.67, 0.23) * mm, "end": v(-1.68, 0.23) * mm});
            skLineSegment(sketch, "E1520", {"start": v(-1.68, 0.23) * mm, "end": v(-1.68, 0.23) * mm});
            skLineSegment(sketch, "E1521", {"start": v(-1.68, 0.23) * mm, "end": v(-1.69, 0.23) * mm});
            skLineSegment(sketch, "E1522", {"start": v(-1.69, 0.23) * mm, "end": v(-1.7, 0.23) * mm});
            skLineSegment(sketch, "E1523", {"start": v(-1.7, 0.23) * mm, "end": v(-1.7, 0.23) * mm});
            skLineSegment(sketch, "E1524", {"start": v(-1.7, 0.23) * mm, "end": v(-1.7, 0.24) * mm});
            skLineSegment(sketch, "E1525", {"start": v(-1.7, 0.24) * mm, "end": v(-1.7, 0.24) * mm});
            skLineSegment(sketch, "E1526", {"start": v(-1.7, 0.24) * mm, "end": v(-1.7, 0.25) * mm});
            skLineSegment(sketch, "E1527", {"start": v(-1.74, 0.15) * mm, "end": v(-1.74, 0.55) * mm});
            skLineSegment(sketch, "E1528", {"start": v(-1.7, 0.45) * mm, "end": v(-1.7, 0.45) * mm});
            skLineSegment(sketch, "E1529", {"start": v(-1.7, 0.45) * mm, "end": v(-1.7, 0.46) * mm});
            skLineSegment(sketch, "E1530", {"start": v(-1.7, 0.46) * mm, "end": v(-1.7, 0.46) * mm});
            skLineSegment(sketch, "E1531", {"start": v(-1.7, 0.46) * mm, "end": v(-1.7, 0.47) * mm});
            skLineSegment(sketch, "E1532", {"start": v(-1.7, 0.47) * mm, "end": v(-1.7, 0.47) * mm});
            skLineSegment(sketch, "E1533", {"start": v(-1.7, 0.47) * mm, "end": v(-1.69, 0.47) * mm});
            skLineSegment(sketch, "E1534", {"start": v(-1.69, 0.47) * mm, "end": v(-1.68, 0.47) * mm});
            skLineSegment(sketch, "E1535", {"start": v(-1.68, 0.47) * mm, "end": v(-1.68, 0.47) * mm});
            skLineSegment(sketch, "E1536", {"start": v(-1.68, 0.47) * mm, "end": v(-1.67, 0.47) * mm});
            skLineSegment(sketch, "E1537", {"start": v(-1.67, 0.47) * mm, "end": v(-1.67, 0.46) * mm});
            skLineSegment(sketch, "E1538", {"start": v(-1.67, 0.46) * mm, "end": v(-1.67, 0.46) * mm});
            skLineSegment(sketch, "E1539", {"start": v(-1.67, 0.46) * mm, "end": v(-1.67, 0.45) * mm});
            skLineSegment(sketch, "E1540", {"start": v(-1.67, 0.45) * mm, "end": v(-1.67, 0.45) * mm});
            skLineSegment(sketch, "E1541", {"start": v(-1.67, 0.45) * mm, "end": v(-1.67, 0.44) * mm});
            skLineSegment(sketch, "E1542", {"start": v(-1.67, 0.44) * mm, "end": v(-1.67, 0.44) * mm});
            skLineSegment(sketch, "E1543", {"start": v(-1.67, 0.44) * mm, "end": v(-1.67, 0.43) * mm});
            skLineSegment(sketch, "E1544", {"start": v(-1.67, 0.43) * mm, "end": v(-1.68, 0.43) * mm});
            skLineSegment(sketch, "E1545", {"start": v(-1.68, 0.43) * mm, "end": v(-1.68, 0.43) * mm});
            skLineSegment(sketch, "E1546", {"start": v(-1.68, 0.43) * mm, "end": v(-1.69, 0.43) * mm});
            skLineSegment(sketch, "E1547", {"start": v(-1.69, 0.43) * mm, "end": v(-1.7, 0.43) * mm});
            skLineSegment(sketch, "E1548", {"start": v(-1.7, 0.43) * mm, "end": v(-1.7, 0.43) * mm});
            skLineSegment(sketch, "E1549", {"start": v(-1.7, 0.43) * mm, "end": v(-1.7, 0.44) * mm});
            skLineSegment(sketch, "E1550", {"start": v(-1.7, 0.44) * mm, "end": v(-1.7, 0.44) * mm});
            skLineSegment(sketch, "E1551", {"start": v(-1.7, 0.44) * mm, "end": v(-1.7, 0.45) * mm});
            skLineSegment(sketch, "E1552", {"start": v(-1.6, 0.45) * mm, "end": v(-1.6, 0.45) * mm});
            skLineSegment(sketch, "E1553", {"start": v(-1.6, 0.45) * mm, "end": v(-1.6, 0.46) * mm});
            skLineSegment(sketch, "E1554", {"start": v(-1.6, 0.46) * mm, "end": v(-1.6, 0.46) * mm});
            skLineSegment(sketch, "E1555", {"start": v(-1.6, 0.46) * mm, "end": v(-1.6, 0.47) * mm});
            skLineSegment(sketch, "E1556", {"start": v(-1.6, 0.47) * mm, "end": v(-1.6, 0.47) * mm});
            skLineSegment(sketch, "E1557", {"start": v(-1.6, 0.47) * mm, "end": v(-1.6, 0.48) * mm});
            skLineSegment(sketch, "E1558", {"start": v(-1.6, 0.48) * mm, "end": v(-1.6, 0.48) * mm});
            skLineSegment(sketch, "E1559", {"start": v(-1.6, 0.48) * mm, "end": v(-1.6, 0.49) * mm});
            skLineSegment(sketch, "E1560", {"start": v(-1.6, 0.49) * mm, "end": v(-1.6, 0.49) * mm});
            skLineSegment(sketch, "E1561", {"start": v(-1.6, 0.49) * mm, "end": v(-1.6, 0.5) * mm});
            skLineSegment(sketch, "E1562", {"start": v(-1.6, 0.5) * mm, "end": v(-1.59, 0.5) * mm});
            skLineSegment(sketch, "E1563", {"start": v(-1.59, 0.5) * mm, "end": v(-1.58, 0.5) * mm});
            skLineSegment(sketch, "E1564", {"start": v(-1.58, 0.5) * mm, "end": v(-1.58, 0.5) * mm});
            skLineSegment(sketch, "E1565", {"start": v(-1.58, 0.5) * mm, "end": v(-1.57, 0.5) * mm});
            skLineSegment(sketch, "E1566", {"start": v(-1.57, 0.5) * mm, "end": v(-1.57, 0.5) * mm});
            skLineSegment(sketch, "E1567", {"start": v(-1.57, 0.5) * mm, "end": v(-1.56, 0.5) * mm});
            skLineSegment(sketch, "E1568", {"start": v(-1.56, 0.5) * mm, "end": v(-1.56, 0.5) * mm});
            skLineSegment(sketch, "E1569", {"start": v(-1.56, 0.5) * mm, "end": v(-1.55, 0.5) * mm});
            skLineSegment(sketch, "E1570", {"start": v(-1.55, 0.5) * mm, "end": v(-1.55, 0.5) * mm});
            skLineSegment(sketch, "E1571", {"start": v(-1.55, 0.5) * mm, "end": v(-1.54, 0.5) * mm});
            skLineSegment(sketch, "E1572", {"start": v(-1.54, 0.5) * mm, "end": v(-1.54, 0.5) * mm});
            skLineSegment(sketch, "E1573", {"start": v(-1.54, 0.5) * mm, "end": v(-1.53, 0.5) * mm});
            skLineSegment(sketch, "E1574", {"start": v(-1.53, 0.5) * mm, "end": v(-1.53, 0.5) * mm});
            skLineSegment(sketch, "E1575", {"start": v(-1.53, 0.5) * mm, "end": v(-1.52, 0.5) * mm});
            skLineSegment(sketch, "E1576", {"start": v(-1.52, 0.5) * mm, "end": v(-1.52, 0.5) * mm});
            skLineSegment(sketch, "E1577", {"start": v(-1.52, 0.5) * mm, "end": v(-1.51, 0.5) * mm});
            skLineSegment(sketch, "E1578", {"start": v(-1.51, 0.5) * mm, "end": v(-1.5, 0.5) * mm});
            skLineSegment(sketch, "E1579", {"start": v(-1.5, 0.5) * mm, "end": v(-1.5, 0.49) * mm});
            skLineSegment(sketch, "E1580", {"start": v(-1.5, 0.49) * mm, "end": v(-1.5, 0.48) * mm});
            skLineSegment(sketch, "E1581", {"start": v(-1.5, 0.48) * mm, "end": v(-1.5, 0.48) * mm});
            skLineSegment(sketch, "E1582", {"start": v(-1.5, 0.48) * mm, "end": v(-1.5, 0.47) * mm});
            skLineSegment(sketch, "E1583", {"start": v(-1.5, 0.47) * mm, "end": v(-1.5, 0.47) * mm});
            skLineSegment(sketch, "E1584", {"start": v(-1.5, 0.47) * mm, "end": v(-1.5, 0.46) * mm});
            skLineSegment(sketch, "E1585", {"start": v(-1.5, 0.46) * mm, "end": v(-1.5, 0.46) * mm});
            skLineSegment(sketch, "E1586", {"start": v(-1.5, 0.46) * mm, "end": v(-1.5, 0.45) * mm});
            skLineSegment(sketch, "E1587", {"start": v(-1.5, 0.45) * mm, "end": v(-1.5, 0.45) * mm});
            skLineSegment(sketch, "E1588", {"start": v(-1.5, 0.45) * mm, "end": v(-1.5, 0.44) * mm});
            skLineSegment(sketch, "E1589", {"start": v(-1.5, 0.44) * mm, "end": v(-1.5, 0.44) * mm});
            skLineSegment(sketch, "E1590", {"start": v(-1.5, 0.44) * mm, "end": v(-1.5, 0.43) * mm});
            skLineSegment(sketch, "E1591", {"start": v(-1.5, 0.43) * mm, "end": v(-1.5, 0.43) * mm});
            skLineSegment(sketch, "E1592", {"start": v(-1.5, 0.43) * mm, "end": v(-1.5, 0.42) * mm});
            skLineSegment(sketch, "E1593", {"start": v(-1.5, 0.42) * mm, "end": v(-1.5, 0.42) * mm});
            skLineSegment(sketch, "E1594", {"start": v(-1.5, 0.42) * mm, "end": v(-1.5, 0.41) * mm});
            skLineSegment(sketch, "E1595", {"start": v(-1.5, 0.41) * mm, "end": v(-1.5, 0.4) * mm});
            skLineSegment(sketch, "E1596", {"start": v(-1.5, 0.4) * mm, "end": v(-1.51, 0.4) * mm});
            skLineSegment(sketch, "E1597", {"start": v(-1.51, 0.4) * mm, "end": v(-1.52, 0.4) * mm});
            skLineSegment(sketch, "E1598", {"start": v(-1.52, 0.4) * mm, "end": v(-1.52, 0.4) * mm});
            skLineSegment(sketch, "E1599", {"start": v(-1.52, 0.4) * mm, "end": v(-1.53, 0.4) * mm});
            skLineSegment(sketch, "E1600", {"start": v(-1.53, 0.4) * mm, "end": v(-1.53, 0.4) * mm});
            skLineSegment(sketch, "E1601", {"start": v(-1.53, 0.4) * mm, "end": v(-1.54, 0.4) * mm});
            skLineSegment(sketch, "E1602", {"start": v(-1.54, 0.4) * mm, "end": v(-1.54, 0.4) * mm});
            skLineSegment(sketch, "E1603", {"start": v(-1.54, 0.4) * mm, "end": v(-1.55, 0.4) * mm});
            skLineSegment(sketch, "E1604", {"start": v(-1.55, 0.4) * mm, "end": v(-1.55, 0.4) * mm});
            skLineSegment(sketch, "E1605", {"start": v(-1.55, 0.4) * mm, "end": v(-1.56, 0.4) * mm});
            skLineSegment(sketch, "E1606", {"start": v(-1.56, 0.4) * mm, "end": v(-1.56, 0.4) * mm});
            skLineSegment(sketch, "E1607", {"start": v(-1.56, 0.4) * mm, "end": v(-1.57, 0.4) * mm});
            skLineSegment(sketch, "E1608", {"start": v(-1.57, 0.4) * mm, "end": v(-1.57, 0.4) * mm});
            skLineSegment(sketch, "E1609", {"start": v(-1.57, 0.4) * mm, "end": v(-1.58, 0.4) * mm});
            skLineSegment(sketch, "E1610", {"start": v(-1.58, 0.4) * mm, "end": v(-1.58, 0.4) * mm});
            skLineSegment(sketch, "E1611", {"start": v(-1.58, 0.4) * mm, "end": v(-1.59, 0.4) * mm});
            skLineSegment(sketch, "E1612", {"start": v(-1.59, 0.4) * mm, "end": v(-1.6, 0.4) * mm});
            skLineSegment(sketch, "E1613", {"start": v(-1.6, 0.4) * mm, "end": v(-1.6, 0.41) * mm});
            skLineSegment(sketch, "E1614", {"start": v(-1.6, 0.41) * mm, "end": v(-1.6, 0.41) * mm});
            skLineSegment(sketch, "E1615", {"start": v(-1.6, 0.41) * mm, "end": v(-1.6, 0.42) * mm});
            skLineSegment(sketch, "E1616", {"start": v(-1.6, 0.42) * mm, "end": v(-1.6, 0.42) * mm});
            skLineSegment(sketch, "E1617", {"start": v(-1.6, 0.42) * mm, "end": v(-1.6, 0.43) * mm});
            skLineSegment(sketch, "E1618", {"start": v(-1.6, 0.43) * mm, "end": v(-1.6, 0.43) * mm});
            skLineSegment(sketch, "E1619", {"start": v(-1.6, 0.43) * mm, "end": v(-1.6, 0.44) * mm});
            skLineSegment(sketch, "E1620", {"start": v(-1.6, 0.44) * mm, "end": v(-1.6, 0.44) * mm});
            skLineSegment(sketch, "E1621", {"start": v(-1.6, 0.44) * mm, "end": v(-1.6, 0.45) * mm});
            skLineSegment(sketch, "E1622", {"start": v(-1.34, 0.34) * mm, "end": v(-1.34, 0.34) * mm});
            skLineSegment(sketch, "E1623", {"start": v(-1.32, 0.34) * mm, "end": v(-1.3, 0.34) * mm});
            skLineSegment(sketch, "E1624", {"start": v(-1.3, 0.35) * mm, "end": v(-1.3, 0.34) * mm});
            skLineSegment(sketch, "E1625", {"start": v(-1.3, 0.32) * mm, "end": v(-1.31, 0.32) * mm});
            skLineSegment(sketch, "E1626", {"start": v(-1.31, 0.32) * mm, "end": v(-1.32, 0.31) * mm});
            skLineSegment(sketch, "E1627", {"start": v(-1.32, 0.31) * mm, "end": v(-1.32, 0.3) * mm});
            skLineSegment(sketch, "E1628", {"start": v(-1.32, 0.3) * mm, "end": v(-1.31, 0.29) * mm});
            skLineSegment(sketch, "E1629", {"start": v(-1.31, 0.29) * mm, "end": v(-1.3, 0.29) * mm});
            skLineSegment(sketch, "E1630", {"start": v(-1.3, 0.29) * mm, "end": v(-1.3, 0.3) * mm});
            skLineSegment(sketch, "E1631", {"start": v(-1.3, 0.3) * mm, "end": v(-1.3, 0.31) * mm});
            skLineSegment(sketch, "E1632", {"start": v(-1.3, 0.31) * mm, "end": v(-1.3, 0.32) * mm});
            skLineSegment(sketch, "E1633", {"start": v(-1.32, 0.34) * mm, "end": v(-1.32, 0.34) * mm});
            skLineSegment(sketch, "E1634", {"start": v(-1.34, 0.37) * mm, "end": v(-1.34, 0.37) * mm});
            skLineSegment(sketch, "E1635", {"start": v(-1.34, 0.37) * mm, "end": v(-1.3, 0.37) * mm});
            skLineSegment(sketch, "E1636", {"start": v(-1.3, 0.37) * mm, "end": v(-1.3, 0.38) * mm});
            skLineSegment(sketch, "E1637", {"start": v(-1.3, 0.4) * mm, "end": v(-1.31, 0.4) * mm});
            skLineSegment(sketch, "E1638", {"start": v(-1.31, 0.4) * mm, "end": v(-1.32, 0.4) * mm});
            skLineSegment(sketch, "E1639", {"start": v(-1.32, 0.4) * mm, "end": v(-1.32, 0.42) * mm});
            skLineSegment(sketch, "E1640", {"start": v(-1.32, 0.42) * mm, "end": v(-1.31, 0.43) * mm});
            skLineSegment(sketch, "E1641", {"start": v(-1.31, 0.43) * mm, "end": v(-1.3, 0.43) * mm});
            skLineSegment(sketch, "E1642", {"start": v(-1.3, 0.43) * mm, "end": v(-1.3, 0.4) * mm});
            skLineSegment(sketch, "E1643", {"start": v(-1.3, 0.4) * mm, "end": v(-1.3, 0.4) * mm});
            skLineSegment(sketch, "E1644", {"start": v(-1.3, 0.4) * mm, "end": v(-1.3, 0.42) * mm});
            skLineSegment(sketch, "E1645", {"start": v(-1.3, 0.44) * mm, "end": v(-1.32, 0.44) * mm});
            skLineSegment(sketch, "E1646", {"start": v(-1.3, 0.44) * mm, "end": v(-1.32, 0.46) * mm});
            skLineSegment(sketch, "E1647", {"start": v(-1.32, 0.46) * mm, "end": v(-1.32, 0.46) * mm});
            skLineSegment(sketch, "E1648", {"start": v(-1.19, 0.33) * mm, "end": v(-1.19, 0.17) * mm});
            skLineSegment(sketch, "E1649", {"start": v(-1.19, 0.17) * mm, "end": v(-1.19, 0.17) * mm});
            skLineSegment(sketch, "E1650", {"start": v(-1.19, 0.17) * mm, "end": v(-1.19, 0.16) * mm});
            skLineSegment(sketch, "E1651", {"start": v(-1.19, 0.16) * mm, "end": v(-1.19, 0.16) * mm});
            skLineSegment(sketch, "E1652", {"start": v(-1.19, 0.16) * mm, "end": v(-1.18, 0.16) * mm});
            skLineSegment(sketch, "E1653", {"start": v(-1.18, 0.16) * mm, "end": v(-1.18, 0.16) * mm});
            skLineSegment(sketch, "E1654", {"start": v(-1.18, 0.16) * mm, "end": v(-1.12, 0.16) * mm});
            skLineSegment(sketch, "E1655", {"start": v(-1.12, 0.16) * mm, "end": v(-1.12, 0.16) * mm});
            skLineSegment(sketch, "E1656", {"start": v(-1.12, 0.16) * mm, "end": v(-1.11, 0.16) * mm});
            skLineSegment(sketch, "E1657", {"start": v(-1.11, 0.16) * mm, "end": v(-1.11, 0.16) * mm});
            skLineSegment(sketch, "E1658", {"start": v(-1.11, 0.16) * mm, "end": v(-1.11, 0.17) * mm});
            skLineSegment(sketch, "E1659", {"start": v(-1.11, 0.17) * mm, "end": v(-1.11, 0.17) * mm});
            skLineSegment(sketch, "E1660", {"start": v(-1.11, 0.17) * mm, "end": v(-1.1, 0.17) * mm});
            skLineSegment(sketch, "E1661", {"start": v(-1.1, 0.17) * mm, "end": v(-1.1, 0.33) * mm});
            skLineSegment(sketch, "E1662", {"start": v(-1.1, 0.33) * mm, "end": v(-1.11, 0.33) * mm});
            skLineSegment(sketch, "E1663", {"start": v(-1.11, 0.33) * mm, "end": v(-1.11, 0.33) * mm});
            skLineSegment(sketch, "E1664", {"start": v(-1.11, 0.33) * mm, "end": v(-1.11, 0.34) * mm});
            skLineSegment(sketch, "E1665", {"start": v(-1.11, 0.34) * mm, "end": v(-1.11, 0.34) * mm});
            skLineSegment(sketch, "E1666", {"start": v(-1.11, 0.34) * mm, "end": v(-1.12, 0.34) * mm});
            skLineSegment(sketch, "E1667", {"start": v(-1.12, 0.34) * mm, "end": v(-1.12, 0.34) * mm});
            skLineSegment(sketch, "E1668", {"start": v(-1.12, 0.34) * mm, "end": v(-1.18, 0.34) * mm});
            skLineSegment(sketch, "E1669", {"start": v(-1.18, 0.34) * mm, "end": v(-1.18, 0.34) * mm});
            skLineSegment(sketch, "E1670", {"start": v(-1.18, 0.34) * mm, "end": v(-1.19, 0.34) * mm});
            skLineSegment(sketch, "E1671", {"start": v(-1.19, 0.34) * mm, "end": v(-1.19, 0.34) * mm});
            skLineSegment(sketch, "E1672", {"start": v(-1.19, 0.34) * mm, "end": v(-1.19, 0.33) * mm});
            skLineSegment(sketch, "E1673", {"start": v(-1.19, 0.33) * mm, "end": v(-1.19, 0.33) * mm});
            skLineSegment(sketch, "E1674", {"start": v(-1.15, 0.27) * mm, "end": v(-1.15, 0.25) * mm});
            skLineSegment(sketch, "E1675", {"start": v(-1.15, 0.25) * mm, "end": v(-1.17, 0.25) * mm});
            skLineSegment(sketch, "E1676", {"start": v(-1.15, 0.25) * mm, "end": v(-1.13, 0.25) * mm});
            skLineSegment(sketch, "E1677", {"start": v(-1.15, 0.25) * mm, "end": v(-1.17, 0.2) * mm});
            skLineSegment(sketch, "E1678", {"start": v(-1.17, 0.2) * mm, "end": v(-1.13, 0.2) * mm});
            skLineSegment(sketch, "E1679", {"start": v(-1.13, 0.2) * mm, "end": v(-1.15, 0.25) * mm});
            skLineSegment(sketch, "E1680", {"start": v(-1.15, 0.25) * mm, "end": v(-1.15, 0.19) * mm});
            skLineSegment(sketch, "E1681", {"start": v(-1.09, 0.17) * mm, "end": v(-1.09, 0.33) * mm});
            skLineSegment(sketch, "E1682", {"start": v(-1.09, 0.33) * mm, "end": v(-1.09, 0.33) * mm});
            skLineSegment(sketch, "E1683", {"start": v(-1.09, 0.33) * mm, "end": v(-1.09, 0.34) * mm});
            skLineSegment(sketch, "E1684", {"start": v(-1.09, 0.34) * mm, "end": v(-1.09, 0.34) * mm});
            skLineSegment(sketch, "E1685", {"start": v(-1.09, 0.34) * mm, "end": v(-1.08, 0.34) * mm});
            skLineSegment(sketch, "E1686", {"start": v(-1.08, 0.34) * mm, "end": v(-1.08, 0.34) * mm});
            skLineSegment(sketch, "E1687", {"start": v(-1.08, 0.34) * mm, "end": v(-1.02, 0.34) * mm});
            skLineSegment(sketch, "E1688", {"start": v(-1.02, 0.34) * mm, "end": v(-1.02, 0.34) * mm});
            skLineSegment(sketch, "E1689", {"start": v(-1.02, 0.34) * mm, "end": v(-1.01, 0.34) * mm});
            skLineSegment(sketch, "E1690", {"start": v(-1.01, 0.34) * mm, "end": v(-1.01, 0.34) * mm});
            skLineSegment(sketch, "E1691", {"start": v(-1.01, 0.34) * mm, "end": v(-1.01, 0.33) * mm});
            skLineSegment(sketch, "E1692", {"start": v(-1.01, 0.33) * mm, "end": v(-1.01, 0.33) * mm});
            skLineSegment(sketch, "E1693", {"start": v(-1.01, 0.33) * mm, "end": v(-1.01, 0.17) * mm});
            skLineSegment(sketch, "E1694", {"start": v(-1.01, 0.17) * mm, "end": v(-1.01, 0.17) * mm});
            skLineSegment(sketch, "E1695", {"start": v(-1.01, 0.17) * mm, "end": v(-1.01, 0.16) * mm});
            skLineSegment(sketch, "E1696", {"start": v(-1.01, 0.16) * mm, "end": v(-1.01, 0.16) * mm});
            skLineSegment(sketch, "E1697", {"start": v(-1.01, 0.16) * mm, "end": v(-1.02, 0.16) * mm});
            skLineSegment(sketch, "E1698", {"start": v(-1.02, 0.16) * mm, "end": v(-1.02, 0.16) * mm});
            skLineSegment(sketch, "E1699", {"start": v(-1.02, 0.16) * mm, "end": v(-1.08, 0.16) * mm});
            skLineSegment(sketch, "E1700", {"start": v(-1.08, 0.16) * mm, "end": v(-1.08, 0.16) * mm});
            skLineSegment(sketch, "E1701", {"start": v(-1.08, 0.16) * mm, "end": v(-1.09, 0.16) * mm});
            skLineSegment(sketch, "E1702", {"start": v(-1.09, 0.16) * mm, "end": v(-1.09, 0.16) * mm});
            skLineSegment(sketch, "E1703", {"start": v(-1.09, 0.16) * mm, "end": v(-1.09, 0.17) * mm});
            skLineSegment(sketch, "E1704", {"start": v(-1.09, 0.17) * mm, "end": v(-1.09, 0.17) * mm});
            skLineSegment(sketch, "E1705", {"start": v(-1.05, 0.19) * mm, "end": v(-1.05, 0.25) * mm});
            skLineSegment(sketch, "E1706", {"start": v(-1.05, 0.25) * mm, "end": v(-1.07, 0.25) * mm});
            skLineSegment(sketch, "E1707", {"start": v(-1.05, 0.25) * mm, "end": v(-1.07, 0.2) * mm});
            skLineSegment(sketch, "E1708", {"start": v(-1.07, 0.2) * mm, "end": v(-1.02, 0.2) * mm});
            skLineSegment(sketch, "E1709", {"start": v(-1.02, 0.2) * mm, "end": v(-1.05, 0.25) * mm});
            skLineSegment(sketch, "E1710", {"start": v(-1.05, 0.25) * mm, "end": v(-1.02, 0.25) * mm});
            skLineSegment(sketch, "E1711", {"start": v(-1.05, 0.25) * mm, "end": v(-1.05, 0.27) * mm});
            skLineSegment(sketch, "E1712", {"start": v(-0.9, 0.18) * mm, "end": v(-0.9, 0.41) * mm});
            skLineSegment(sketch, "E1713", {"start": v(-0.9, 0.41) * mm, "end": v(-0.5, 0.41) * mm});
            skLineSegment(sketch, "E1714", {"start": v(-0.5, 0.41) * mm, "end": v(-0.5, 0.34) * mm});
            skLineSegment(sketch, "E1715", {"start": v(-0.5, 0.34) * mm, "end": v(-0.5, 0.34) * mm});
            skLineSegment(sketch, "E1716", {"start": v(-0.5, 0.34) * mm, "end": v(-0.51, 0.34) * mm});
            skLineSegment(sketch, "E1717", {"start": v(-0.51, 0.34) * mm, "end": v(-0.52, 0.34) * mm});
            skLineSegment(sketch, "E1718", {"start": v(-0.52, 0.34) * mm, "end": v(-0.52, 0.34) * mm});
            skLineSegment(sketch, "E1719", {"start": v(-0.52, 0.34) * mm, "end": v(-0.52, 0.33) * mm});
            skLineSegment(sketch, "E1720", {"start": v(-0.52, 0.33) * mm, "end": v(-0.53, 0.33) * mm});
            skLineSegment(sketch, "E1721", {"start": v(-0.53, 0.33) * mm, "end": v(-0.53, 0.33) * mm});
            skLineSegment(sketch, "E1722", {"start": v(-0.53, 0.33) * mm, "end": v(-0.53, 0.32) * mm});
            skLineSegment(sketch, "E1723", {"start": v(-0.53, 0.32) * mm, "end": v(-0.54, 0.32) * mm});
            skLineSegment(sketch, "E1724", {"start": v(-0.54, 0.32) * mm, "end": v(-0.54, 0.32) * mm});
            skLineSegment(sketch, "E1725", {"start": v(-0.54, 0.32) * mm, "end": v(-0.54, 0.31) * mm});
            skLineSegment(sketch, "E1726", {"start": v(-0.54, 0.31) * mm, "end": v(-0.54, 0.3) * mm});
            skLineSegment(sketch, "E1727", {"start": v(-0.54, 0.3) * mm, "end": v(-0.54, 0.3) * mm});
            skLineSegment(sketch, "E1728", {"start": v(-0.54, 0.3) * mm, "end": v(-0.54, 0.29) * mm});
            skLineSegment(sketch, "E1729", {"start": v(-0.54, 0.29) * mm, "end": v(-0.54, 0.28) * mm});
            skLineSegment(sketch, "E1730", {"start": v(-0.54, 0.28) * mm, "end": v(-0.54, 0.28) * mm});
            skLineSegment(sketch, "E1731", {"start": v(-0.54, 0.28) * mm, "end": v(-0.53, 0.28) * mm});
            skLineSegment(sketch, "E1732", {"start": v(-0.53, 0.28) * mm, "end": v(-0.53, 0.27) * mm});
            skLineSegment(sketch, "E1733", {"start": v(-0.53, 0.27) * mm, "end": v(-0.53, 0.27) * mm});
            skLineSegment(sketch, "E1734", {"start": v(-0.53, 0.27) * mm, "end": v(-0.52, 0.27) * mm});
            skLineSegment(sketch, "E1735", {"start": v(-0.52, 0.27) * mm, "end": v(-0.52, 0.26) * mm});
            skLineSegment(sketch, "E1736", {"start": v(-0.52, 0.26) * mm, "end": v(-0.52, 0.26) * mm});
            skLineSegment(sketch, "E1737", {"start": v(-0.52, 0.26) * mm, "end": v(-0.51, 0.26) * mm});
            skLineSegment(sketch, "E1738", {"start": v(-0.51, 0.26) * mm, "end": v(-0.5, 0.26) * mm});
            skLineSegment(sketch, "E1739", {"start": v(-0.5, 0.26) * mm, "end": v(-0.5, 0.26) * mm});
            skLineSegment(sketch, "E1740", {"start": v(-0.5, 0.26) * mm, "end": v(-0.5, 0.18) * mm});
            skLineSegment(sketch, "E1741", {"start": v(-0.5, 0.18) * mm, "end": v(-0.9, 0.18) * mm});
            skLineSegment(sketch, "E1742", {"start": v(-0.87, 0) * mm, "end": v(-1.03, 0) * mm});
            skLineSegment(sketch, "E1743", {"start": v(-1.03, 0) * mm, "end": v(-1.03, -0.1) * mm});
            skLineSegment(sketch, "E1744", {"start": v(-1.03, -0.1) * mm, "end": v(-0.87, -0.1) * mm});
            skLineSegment(sketch, "E1745", {"start": v(-0.87, -0.1) * mm, "end": v(-0.87, 0) * mm});
            skLineSegment(sketch, "E1746", {"start": v(-0.92, -0.05) * mm, "end": v(-0.95, -0.05) * mm});
            skLineSegment(sketch, "E1747", {"start": v(-0.95, -0.05) * mm, "end": v(-0.95, -0.08) * mm});
            skLineSegment(sketch, "E1748", {"start": v(-0.95, -0.08) * mm, "end": v(-0.96, -0.08) * mm});
            skLineSegment(sketch, "E1749", {"start": v(-0.95, -0.05) * mm, "end": v(-0.99, -0.08) * mm});
            skLineSegment(sketch, "E1750", {"start": v(-0.99, -0.08) * mm, "end": v(-0.99, -0.03) * mm});
            skLineSegment(sketch, "E1751", {"start": v(-0.99, -0.03) * mm, "end": v(-0.95, -0.05) * mm});
            skLineSegment(sketch, "E1752", {"start": v(-0.95, -0.05) * mm, "end": v(-0.95, -0.03) * mm});
            skLineSegment(sketch, "E1753", {"start": v(-0.95, -0.05) * mm, "end": v(-1.01, -0.05) * mm});
            skLineSegment(sketch, "E1754", {"start": v(-1.03, -0.1) * mm, "end": v(-1.03, -0.2) * mm});
            skLineSegment(sketch, "E1755", {"start": v(-1.03, -0.2) * mm, "end": v(-0.87, -0.2) * mm});
            skLineSegment(sketch, "E1756", {"start": v(-0.87, -0.2) * mm, "end": v(-0.87, -0.1) * mm});
            skLineSegment(sketch, "E1757", {"start": v(-0.87, -0.1) * mm, "end": v(-1.03, -0.1) * mm});
            skLineSegment(sketch, "E1758", {"start": v(-0.99, -0.13) * mm, "end": v(-0.95, -0.15) * mm});
            skLineSegment(sketch, "E1759", {"start": v(-0.95, -0.15) * mm, "end": v(-0.95, -0.18) * mm});
            skLineSegment(sketch, "E1760", {"start": v(-0.95, -0.18) * mm, "end": v(-0.96, -0.18) * mm});
            skLineSegment(sketch, "E1761", {"start": v(-0.95, -0.15) * mm, "end": v(-0.99, -0.18) * mm});
            skLineSegment(sketch, "E1762", {"start": v(-0.99, -0.18) * mm, "end": v(-0.99, -0.13) * mm});
            skLineSegment(sketch, "E1763", {"start": v(-1.01, -0.15) * mm, "end": v(-0.95, -0.15) * mm});
            skLineSegment(sketch, "E1764", {"start": v(-0.95, -0.15) * mm, "end": v(-0.95, -0.13) * mm});
            skLineSegment(sketch, "E1765", {"start": v(-0.95, -0.15) * mm, "end": v(-0.92, -0.15) * mm});
            skLineSegment(sketch, "E1766", {"start": v(-1.3, -0.15) * mm, "end": v(-1.3, -0.16) * mm});
            skLineSegment(sketch, "E1767", {"start": v(-1.3, -0.16) * mm, "end": v(-1.33, -0.16) * mm});
            skLineSegment(sketch, "E1768", {"start": v(-1.32, -0.17) * mm, "end": v(-1.32, -0.15) * mm});
            skLineSegment(sketch, "E1769", {"start": v(-1.31, -0.18) * mm, "end": v(-1.3, -0.18) * mm});
            skLineSegment(sketch, "E1770", {"start": v(-1.3, -0.18) * mm, "end": v(-1.3, -0.2) * mm});
            skLineSegment(sketch, "E1771", {"start": v(-1.3, -0.2) * mm, "end": v(-1.3, -0.21) * mm});
            skLineSegment(sketch, "E1772", {"start": v(-1.3, -0.21) * mm, "end": v(-1.3, -0.2) * mm});
            skLineSegment(sketch, "E1773", {"start": v(-1.3, -0.2) * mm, "end": v(-1.3, -0.18) * mm});
            skLineSegment(sketch, "E1774", {"start": v(-1.31, -0.18) * mm, "end": v(-1.32, -0.19) * mm});
            skLineSegment(sketch, "E1775", {"start": v(-1.32, -0.19) * mm, "end": v(-1.32, -0.2) * mm});
            skLineSegment(sketch, "E1776", {"start": v(-1.32, -0.23) * mm, "end": v(-1.32, -0.24) * mm});
            skLineSegment(sketch, "E1777", {"start": v(-1.33, -0.24) * mm, "end": v(-1.3, -0.24) * mm});
            skLineSegment(sketch, "E1778", {"start": v(-1.3, -0.24) * mm, "end": v(-1.3, -0.23) * mm});
            skLineSegment(sketch, "E1779", {"start": v(-1.3, -0.26) * mm, "end": v(-1.3, -0.27) * mm});
            skLineSegment(sketch, "E1780", {"start": v(-1.3, -0.27) * mm, "end": v(-1.3, -0.28) * mm});
            skLineSegment(sketch, "E1781", {"start": v(-1.3, -0.28) * mm, "end": v(-1.31, -0.29) * mm});
            skLineSegment(sketch, "E1782", {"start": v(-1.31, -0.29) * mm, "end": v(-1.32, -0.28) * mm});
            skLineSegment(sketch, "E1783", {"start": v(-1.32, -0.28) * mm, "end": v(-1.32, -0.26) * mm});
            skLineSegment(sketch, "E1784", {"start": v(-1.3, -0.27) * mm, "end": v(-1.3, -0.29) * mm});
            skLineSegment(sketch, "E1785", {"start": v(-1.3, -0.3) * mm, "end": v(-1.31, -0.3) * mm});
            skLineSegment(sketch, "E1786", {"start": v(-1.31, -0.3) * mm, "end": v(-1.32, -0.31) * mm});
            skLineSegment(sketch, "E1787", {"start": v(-1.32, -0.31) * mm, "end": v(-1.32, -0.33) * mm});
            skLineSegment(sketch, "E1788", {"start": v(-1.32, -0.33) * mm, "end": v(-1.31, -0.33) * mm});
            skLineSegment(sketch, "E1789", {"start": v(-1.31, -0.33) * mm, "end": v(-1.3, -0.33) * mm});
            skLineSegment(sketch, "E1790", {"start": v(-1.3, -0.33) * mm, "end": v(-1.3, -0.33) * mm});
            skLineSegment(sketch, "E1791", {"start": v(-1.3, -0.33) * mm, "end": v(-1.3, -0.31) * mm});
            skLineSegment(sketch, "E1792", {"start": v(-1.3, -0.31) * mm, "end": v(-1.3, -0.3) * mm});
            skLineSegment(sketch, "E1793", {"start": v(-1.3, -0.35) * mm, "end": v(-1.31, -0.35) * mm});
            skLineSegment(sketch, "E1794", {"start": v(-1.31, -0.35) * mm, "end": v(-1.32, -0.36) * mm});
            skLineSegment(sketch, "E1795", {"start": v(-1.32, -0.36) * mm, "end": v(-1.31, -0.37) * mm});
            skLineSegment(sketch, "E1796", {"start": v(-1.31, -0.37) * mm, "end": v(-1.3, -0.37) * mm});
            skLineSegment(sketch, "E1797", {"start": v(-1.3, -0.38) * mm, "end": v(-1.32, -0.38) * mm});
            skLineSegment(sketch, "E1798", {"start": v(-1.32, -0.38) * mm, "end": v(-1.32, -0.37) * mm});
            skLineSegment(sketch, "E1799", {"start": v(-1.32, -0.37) * mm, "end": v(-1.31, -0.37) * mm});
            skLineSegment(sketch, "E1800", {"start": v(-1.32, -0.4) * mm, "end": v(-1.32, -0.4) * mm});
            skLineSegment(sketch, "E1801", {"start": v(-1.32, -0.4) * mm, "end": v(-1.3, -0.42) * mm});
            skLineSegment(sketch, "E1802", {"start": v(-1.3, -0.42) * mm, "end": v(-1.32, -0.42) * mm});
            skLineSegment(sketch, "E1803", {"start": v(-1.31, -0.44) * mm, "end": v(-1.3, -0.44) * mm});
            skLineSegment(sketch, "E1804", {"start": v(-1.3, -0.44) * mm, "end": v(-1.3, -0.46) * mm});
            skLineSegment(sketch, "E1805", {"start": v(-1.31, -0.46) * mm, "end": v(-1.32, -0.46) * mm});
            skLineSegment(sketch, "E1806", {"start": v(-1.32, -0.46) * mm, "end": v(-1.32, -0.44) * mm});
            skLineSegment(sketch, "E1807", {"start": v(-1.32, -0.44) * mm, "end": v(-1.31, -0.44) * mm});
            skLineSegment(sketch, "E1808", {"start": v(-1.3, -0.46) * mm, "end": v(-1.3, -0.46) * mm});
            skLineSegment(sketch, "E1809", {"start": v(-1.3, -0.46) * mm, "end": v(-1.31, -0.46) * mm});
            skLineSegment(sketch, "E1810", {"start": v(-1.31, -0.48) * mm, "end": v(-1.3, -0.48) * mm});
            skLineSegment(sketch, "E1811", {"start": v(-1.31, -0.48) * mm, "end": v(-1.32, -0.49) * mm});
            skLineSegment(sketch, "E1812", {"start": v(-1.32, -0.49) * mm, "end": v(-1.32, -0.5) * mm});
            skLineSegment(sketch, "E1813", {"start": v(-1.32, -0.5) * mm, "end": v(-1.31, -0.51) * mm});
            skLineSegment(sketch, "E1814", {"start": v(-1.34, -0.51) * mm, "end": v(-1.3, -0.51) * mm});
            skLineSegment(sketch, "E1815", {"start": v(-1.3, -0.54) * mm, "end": v(-1.34, -0.54) * mm});
            skLineSegment(sketch, "E1816", {"start": v(-1.34, -0.56) * mm, "end": v(-1.34, -0.53) * mm});
            skLineSegment(sketch, "E1817", {"start": v(-1.39, -0.55) * mm, "end": v(-1.48, -0.55) * mm});
            skLineSegment(sketch, "E1818", {"start": v(-1.48, -0.55) * mm, "end": v(-1.48, -0.49) * mm});
            skLineSegment(sketch, "E1819", {"start": v(-1.48, -0.49) * mm, "end": v(-1.48, -0.42) * mm});
            skLineSegment(sketch, "E1820", {"start": v(-1.48, -0.42) * mm, "end": v(-1.48, -0.29) * mm});
            skLineSegment(sketch, "E1821", {"start": v(-1.48, -0.29) * mm, "end": v(-1.48, -0.22) * mm});
            skLineSegment(sketch, "E1822", {"start": v(-1.48, -0.22) * mm, "end": v(-1.48, -0.15) * mm});
            skLineSegment(sketch, "E1823", {"start": v(-1.48, -0.15) * mm, "end": v(-1.74, -0.15) * mm});
            skLineSegment(sketch, "E1824", {"start": v(-1.74, -0.15) * mm, "end": v(-1.75, -0.15) * mm});
            skLineSegment(sketch, "E1825", {"start": v(-1.75, -0.15) * mm, "end": v(-1.75, -0.55) * mm});
            skLineSegment(sketch, "E1826", {"start": v(-1.75, -0.55) * mm, "end": v(-1.74, -0.55) * mm});
            skLineSegment(sketch, "E1827", {"start": v(-1.74, -0.55) * mm, "end": v(-1.48, -0.55) * mm});
            skLineSegment(sketch, "E1828", {"start": v(-1.39, -0.55) * mm, "end": v(-1.39, -0.15) * mm});
            skLineSegment(sketch, "E1829", {"start": v(-1.39, -0.15) * mm, "end": v(-1.48, -0.15) * mm});
            skLineSegment(sketch, "E1830", {"start": v(-1.6, -0.25) * mm, "end": v(-1.6, -0.25) * mm});
            skLineSegment(sketch, "E1831", {"start": v(-1.6, -0.25) * mm, "end": v(-1.6, -0.24) * mm});
            skLineSegment(sketch, "E1832", {"start": v(-1.6, -0.24) * mm, "end": v(-1.6, -0.24) * mm});
            skLineSegment(sketch, "E1833", {"start": v(-1.6, -0.24) * mm, "end": v(-1.6, -0.23) * mm});
            skLineSegment(sketch, "E1834", {"start": v(-1.6, -0.23) * mm, "end": v(-1.6, -0.23) * mm});
            skLineSegment(sketch, "E1835", {"start": v(-1.6, -0.23) * mm, "end": v(-1.6, -0.22) * mm});
            skLineSegment(sketch, "E1836", {"start": v(-1.6, -0.22) * mm, "end": v(-1.6, -0.22) * mm});
            skLineSegment(sketch, "E1837", {"start": v(-1.6, -0.22) * mm, "end": v(-1.6, -0.21) * mm});
            skLineSegment(sketch, "E1838", {"start": v(-1.6, -0.21) * mm, "end": v(-1.6, -0.21) * mm});
            skLineSegment(sketch, "E1839", {"start": v(-1.6, -0.21) * mm, "end": v(-1.6, -0.2) * mm});
            skLineSegment(sketch, "E1840", {"start": v(-1.6, -0.2) * mm, "end": v(-1.59, -0.2) * mm});
            skLineSegment(sketch, "E1841", {"start": v(-1.59, -0.2) * mm, "end": v(-1.58, -0.2) * mm});
            skLineSegment(sketch, "E1842", {"start": v(-1.58, -0.2) * mm, "end": v(-1.58, -0.2) * mm});
            skLineSegment(sketch, "E1843", {"start": v(-1.58, -0.2) * mm, "end": v(-1.57, -0.2) * mm});
            skLineSegment(sketch, "E1844", {"start": v(-1.57, -0.2) * mm, "end": v(-1.57, -0.2) * mm});
            skLineSegment(sketch, "E1845", {"start": v(-1.57, -0.2) * mm, "end": v(-1.56, -0.2) * mm});
            skLineSegment(sketch, "E1846", {"start": v(-1.56, -0.2) * mm, "end": v(-1.56, -0.2) * mm});
            skLineSegment(sketch, "E1847", {"start": v(-1.56, -0.2) * mm, "end": v(-1.55, -0.2) * mm});
            skLineSegment(sketch, "E1848", {"start": v(-1.55, -0.2) * mm, "end": v(-1.55, -0.2) * mm});
            skLineSegment(sketch, "E1849", {"start": v(-1.55, -0.2) * mm, "end": v(-1.54, -0.2) * mm});
            skLineSegment(sketch, "E1850", {"start": v(-1.54, -0.2) * mm, "end": v(-1.54, -0.2) * mm});
            skLineSegment(sketch, "E1851", {"start": v(-1.54, -0.2) * mm, "end": v(-1.53, -0.2) * mm});
            skLineSegment(sketch, "E1852", {"start": v(-1.53, -0.2) * mm, "end": v(-1.53, -0.2) * mm});
            skLineSegment(sketch, "E1853", {"start": v(-1.53, -0.2) * mm, "end": v(-1.52, -0.2) * mm});
            skLineSegment(sketch, "E1854", {"start": v(-1.52, -0.2) * mm, "end": v(-1.52, -0.2) * mm});
            skLineSegment(sketch, "E1855", {"start": v(-1.52, -0.2) * mm, "end": v(-1.51, -0.2) * mm});
            skLineSegment(sketch, "E1856", {"start": v(-1.51, -0.2) * mm, "end": v(-1.5, -0.2) * mm});
            skLineSegment(sketch, "E1857", {"start": v(-1.5, -0.2) * mm, "end": v(-1.5, -0.21) * mm});
            skLineSegment(sketch, "E1858", {"start": v(-1.5, -0.21) * mm, "end": v(-1.5, -0.22) * mm});
            skLineSegment(sketch, "E1859", {"start": v(-1.5, -0.22) * mm, "end": v(-1.5, -0.22) * mm});
            skLineSegment(sketch, "E1860", {"start": v(-1.5, -0.22) * mm, "end": v(-1.5, -0.23) * mm});
            skLineSegment(sketch, "E1861", {"start": v(-1.5, -0.23) * mm, "end": v(-1.5, -0.23) * mm});
            skLineSegment(sketch, "E1862", {"start": v(-1.5, -0.23) * mm, "end": v(-1.5, -0.24) * mm});
            skLineSegment(sketch, "E1863", {"start": v(-1.5, -0.24) * mm, "end": v(-1.5, -0.24) * mm});
            skLineSegment(sketch, "E1864", {"start": v(-1.5, -0.24) * mm, "end": v(-1.5, -0.25) * mm});
            skLineSegment(sketch, "E1865", {"start": v(-1.5, -0.25) * mm, "end": v(-1.5, -0.25) * mm});
            skLineSegment(sketch, "E1866", {"start": v(-1.5, -0.25) * mm, "end": v(-1.5, -0.26) * mm});
            skLineSegment(sketch, "E1867", {"start": v(-1.5, -0.26) * mm, "end": v(-1.5, -0.26) * mm});
            skLineSegment(sketch, "E1868", {"start": v(-1.5, -0.26) * mm, "end": v(-1.5, -0.27) * mm});
            skLineSegment(sketch, "E1869", {"start": v(-1.5, -0.27) * mm, "end": v(-1.5, -0.27) * mm});
            skLineSegment(sketch, "E1870", {"start": v(-1.5, -0.27) * mm, "end": v(-1.5, -0.28) * mm});
            skLineSegment(sketch, "E1871", {"start": v(-1.5, -0.28) * mm, "end": v(-1.5, -0.28) * mm});
            skLineSegment(sketch, "E1872", {"start": v(-1.5, -0.28) * mm, "end": v(-1.5, -0.29) * mm});
            skLineSegment(sketch, "E1873", {"start": v(-1.5, -0.29) * mm, "end": v(-1.5, -0.3) * mm});
            skLineSegment(sketch, "E1874", {"start": v(-1.5, -0.3) * mm, "end": v(-1.51, -0.3) * mm});
            skLineSegment(sketch, "E1875", {"start": v(-1.51, -0.3) * mm, "end": v(-1.52, -0.3) * mm});
            skLineSegment(sketch, "E1876", {"start": v(-1.52, -0.3) * mm, "end": v(-1.52, -0.3) * mm});
            skLineSegment(sketch, "E1877", {"start": v(-1.52, -0.3) * mm, "end": v(-1.53, -0.3) * mm});
            skLineSegment(sketch, "E1878", {"start": v(-1.53, -0.3) * mm, "end": v(-1.53, -0.3) * mm});
            skLineSegment(sketch, "E1879", {"start": v(-1.53, -0.3) * mm, "end": v(-1.54, -0.3) * mm});
            skLineSegment(sketch, "E1880", {"start": v(-1.54, -0.3) * mm, "end": v(-1.54, -0.3) * mm});
            skLineSegment(sketch, "E1881", {"start": v(-1.54, -0.3) * mm, "end": v(-1.55, -0.3) * mm});
            skLineSegment(sketch, "E1882", {"start": v(-1.55, -0.3) * mm, "end": v(-1.55, -0.3) * mm});
            skLineSegment(sketch, "E1883", {"start": v(-1.55, -0.3) * mm, "end": v(-1.56, -0.3) * mm});
            skLineSegment(sketch, "E1884", {"start": v(-1.56, -0.3) * mm, "end": v(-1.56, -0.3) * mm});
            skLineSegment(sketch, "E1885", {"start": v(-1.56, -0.3) * mm, "end": v(-1.57, -0.3) * mm});
            skLineSegment(sketch, "E1886", {"start": v(-1.57, -0.3) * mm, "end": v(-1.57, -0.3) * mm});
            skLineSegment(sketch, "E1887", {"start": v(-1.57, -0.3) * mm, "end": v(-1.58, -0.3) * mm});
            skLineSegment(sketch, "E1888", {"start": v(-1.58, -0.3) * mm, "end": v(-1.58, -0.3) * mm});
            skLineSegment(sketch, "E1889", {"start": v(-1.58, -0.3) * mm, "end": v(-1.59, -0.3) * mm});
            skLineSegment(sketch, "E1890", {"start": v(-1.59, -0.3) * mm, "end": v(-1.6, -0.3) * mm});
            skLineSegment(sketch, "E1891", {"start": v(-1.6, -0.3) * mm, "end": v(-1.6, -0.29) * mm});
            skLineSegment(sketch, "E1892", {"start": v(-1.6, -0.29) * mm, "end": v(-1.6, -0.29) * mm});
            skLineSegment(sketch, "E1893", {"start": v(-1.6, -0.29) * mm, "end": v(-1.6, -0.28) * mm});
            skLineSegment(sketch, "E1894", {"start": v(-1.6, -0.28) * mm, "end": v(-1.6, -0.28) * mm});
            skLineSegment(sketch, "E1895", {"start": v(-1.6, -0.28) * mm, "end": v(-1.6, -0.27) * mm});
            skLineSegment(sketch, "E1896", {"start": v(-1.6, -0.27) * mm, "end": v(-1.6, -0.27) * mm});
            skLineSegment(sketch, "E1897", {"start": v(-1.6, -0.27) * mm, "end": v(-1.6, -0.26) * mm});
            skLineSegment(sketch, "E1898", {"start": v(-1.6, -0.26) * mm, "end": v(-1.6, -0.26) * mm});
            skLineSegment(sketch, "E1899", {"start": v(-1.6, -0.26) * mm, "end": v(-1.6, -0.25) * mm});
            skLineSegment(sketch, "E1900", {"start": v(-1.7, -0.25) * mm, "end": v(-1.7, -0.25) * mm});
            skLineSegment(sketch, "E1901", {"start": v(-1.7, -0.25) * mm, "end": v(-1.7, -0.24) * mm});
            skLineSegment(sketch, "E1902", {"start": v(-1.7, -0.24) * mm, "end": v(-1.7, -0.24) * mm});
            skLineSegment(sketch, "E1903", {"start": v(-1.7, -0.24) * mm, "end": v(-1.7, -0.23) * mm});
            skLineSegment(sketch, "E1904", {"start": v(-1.7, -0.23) * mm, "end": v(-1.7, -0.23) * mm});
            skLineSegment(sketch, "E1905", {"start": v(-1.7, -0.23) * mm, "end": v(-1.69, -0.23) * mm});
            skLineSegment(sketch, "E1906", {"start": v(-1.69, -0.23) * mm, "end": v(-1.68, -0.23) * mm});
            skLineSegment(sketch, "E1907", {"start": v(-1.68, -0.23) * mm, "end": v(-1.68, -0.23) * mm});
            skLineSegment(sketch, "E1908", {"start": v(-1.68, -0.23) * mm, "end": v(-1.67, -0.23) * mm});
            skLineSegment(sketch, "E1909", {"start": v(-1.67, -0.23) * mm, "end": v(-1.67, -0.24) * mm});
            skLineSegment(sketch, "E1910", {"start": v(-1.67, -0.24) * mm, "end": v(-1.67, -0.24) * mm});
            skLineSegment(sketch, "E1911", {"start": v(-1.67, -0.24) * mm, "end": v(-1.67, -0.25) * mm});
            skLineSegment(sketch, "E1912", {"start": v(-1.67, -0.25) * mm, "end": v(-1.67, -0.25) * mm});
            skLineSegment(sketch, "E1913", {"start": v(-1.67, -0.25) * mm, "end": v(-1.67, -0.26) * mm});
            skLineSegment(sketch, "E1914", {"start": v(-1.67, -0.26) * mm, "end": v(-1.67, -0.26) * mm});
            skLineSegment(sketch, "E1915", {"start": v(-1.67, -0.26) * mm, "end": v(-1.67, -0.27) * mm});
            skLineSegment(sketch, "E1916", {"start": v(-1.67, -0.27) * mm, "end": v(-1.68, -0.27) * mm});
            skLineSegment(sketch, "E1917", {"start": v(-1.68, -0.27) * mm, "end": v(-1.68, -0.27) * mm});
            skLineSegment(sketch, "E1918", {"start": v(-1.68, -0.27) * mm, "end": v(-1.69, -0.27) * mm});
            skLineSegment(sketch, "E1919", {"start": v(-1.69, -0.27) * mm, "end": v(-1.7, -0.27) * mm});
            skLineSegment(sketch, "E1920", {"start": v(-1.7, -0.27) * mm, "end": v(-1.7, -0.27) * mm});
            skLineSegment(sketch, "E1921", {"start": v(-1.7, -0.27) * mm, "end": v(-1.7, -0.26) * mm});
            skLineSegment(sketch, "E1922", {"start": v(-1.7, -0.26) * mm, "end": v(-1.7, -0.26) * mm});
            skLineSegment(sketch, "E1923", {"start": v(-1.7, -0.26) * mm, "end": v(-1.7, -0.25) * mm});
            skLineSegment(sketch, "E1924", {"start": v(-1.74, -0.15) * mm, "end": v(-1.74, -0.55) * mm});
            skLineSegment(sketch, "E1925", {"start": v(-1.7, -0.45) * mm, "end": v(-1.7, -0.45) * mm});
            skLineSegment(sketch, "E1926", {"start": v(-1.7, -0.45) * mm, "end": v(-1.7, -0.44) * mm});
            skLineSegment(sketch, "E1927", {"start": v(-1.7, -0.44) * mm, "end": v(-1.7, -0.44) * mm});
            skLineSegment(sketch, "E1928", {"start": v(-1.7, -0.44) * mm, "end": v(-1.7, -0.43) * mm});
            skLineSegment(sketch, "E1929", {"start": v(-1.7, -0.43) * mm, "end": v(-1.7, -0.43) * mm});
            skLineSegment(sketch, "E1930", {"start": v(-1.7, -0.43) * mm, "end": v(-1.69, -0.43) * mm});
            skLineSegment(sketch, "E1931", {"start": v(-1.69, -0.43) * mm, "end": v(-1.68, -0.43) * mm});
            skLineSegment(sketch, "E1932", {"start": v(-1.68, -0.43) * mm, "end": v(-1.68, -0.43) * mm});
            skLineSegment(sketch, "E1933", {"start": v(-1.68, -0.43) * mm, "end": v(-1.67, -0.43) * mm});
            skLineSegment(sketch, "E1934", {"start": v(-1.67, -0.43) * mm, "end": v(-1.67, -0.44) * mm});
            skLineSegment(sketch, "E1935", {"start": v(-1.67, -0.44) * mm, "end": v(-1.67, -0.44) * mm});
            skLineSegment(sketch, "E1936", {"start": v(-1.67, -0.44) * mm, "end": v(-1.67, -0.45) * mm});
            skLineSegment(sketch, "E1937", {"start": v(-1.67, -0.45) * mm, "end": v(-1.67, -0.45) * mm});
            skLineSegment(sketch, "E1938", {"start": v(-1.67, -0.45) * mm, "end": v(-1.67, -0.46) * mm});
            skLineSegment(sketch, "E1939", {"start": v(-1.67, -0.46) * mm, "end": v(-1.67, -0.46) * mm});
            skLineSegment(sketch, "E1940", {"start": v(-1.67, -0.46) * mm, "end": v(-1.67, -0.47) * mm});
            skLineSegment(sketch, "E1941", {"start": v(-1.67, -0.47) * mm, "end": v(-1.68, -0.47) * mm});
            skLineSegment(sketch, "E1942", {"start": v(-1.68, -0.47) * mm, "end": v(-1.68, -0.47) * mm});
            skLineSegment(sketch, "E1943", {"start": v(-1.68, -0.47) * mm, "end": v(-1.69, -0.47) * mm});
            skLineSegment(sketch, "E1944", {"start": v(-1.69, -0.47) * mm, "end": v(-1.7, -0.47) * mm});
            skLineSegment(sketch, "E1945", {"start": v(-1.7, -0.47) * mm, "end": v(-1.7, -0.47) * mm});
            skLineSegment(sketch, "E1946", {"start": v(-1.7, -0.47) * mm, "end": v(-1.7, -0.46) * mm});
            skLineSegment(sketch, "E1947", {"start": v(-1.7, -0.46) * mm, "end": v(-1.7, -0.46) * mm});
            skLineSegment(sketch, "E1948", {"start": v(-1.7, -0.46) * mm, "end": v(-1.7, -0.45) * mm});
            skLineSegment(sketch, "E1949", {"start": v(-1.6, -0.45) * mm, "end": v(-1.6, -0.45) * mm});
            skLineSegment(sketch, "E1950", {"start": v(-1.6, -0.45) * mm, "end": v(-1.6, -0.44) * mm});
            skLineSegment(sketch, "E1951", {"start": v(-1.6, -0.44) * mm, "end": v(-1.6, -0.44) * mm});
            skLineSegment(sketch, "E1952", {"start": v(-1.6, -0.44) * mm, "end": v(-1.6, -0.43) * mm});
            skLineSegment(sketch, "E1953", {"start": v(-1.6, -0.43) * mm, "end": v(-1.6, -0.43) * mm});
            skLineSegment(sketch, "E1954", {"start": v(-1.6, -0.43) * mm, "end": v(-1.6, -0.42) * mm});
            skLineSegment(sketch, "E1955", {"start": v(-1.6, -0.42) * mm, "end": v(-1.6, -0.42) * mm});
            skLineSegment(sketch, "E1956", {"start": v(-1.6, -0.42) * mm, "end": v(-1.6, -0.41) * mm});
            skLineSegment(sketch, "E1957", {"start": v(-1.6, -0.41) * mm, "end": v(-1.6, -0.41) * mm});
            skLineSegment(sketch, "E1958", {"start": v(-1.6, -0.41) * mm, "end": v(-1.6, -0.4) * mm});
            skLineSegment(sketch, "E1959", {"start": v(-1.6, -0.4) * mm, "end": v(-1.59, -0.4) * mm});
            skLineSegment(sketch, "E1960", {"start": v(-1.59, -0.4) * mm, "end": v(-1.58, -0.4) * mm});
            skLineSegment(sketch, "E1961", {"start": v(-1.58, -0.4) * mm, "end": v(-1.58, -0.4) * mm});
            skLineSegment(sketch, "E1962", {"start": v(-1.58, -0.4) * mm, "end": v(-1.57, -0.4) * mm});
            skLineSegment(sketch, "E1963", {"start": v(-1.57, -0.4) * mm, "end": v(-1.57, -0.4) * mm});
            skLineSegment(sketch, "E1964", {"start": v(-1.57, -0.4) * mm, "end": v(-1.56, -0.4) * mm});
            skLineSegment(sketch, "E1965", {"start": v(-1.56, -0.4) * mm, "end": v(-1.56, -0.4) * mm});
            skLineSegment(sketch, "E1966", {"start": v(-1.56, -0.4) * mm, "end": v(-1.55, -0.4) * mm});
            skLineSegment(sketch, "E1967", {"start": v(-1.55, -0.4) * mm, "end": v(-1.55, -0.4) * mm});
            skLineSegment(sketch, "E1968", {"start": v(-1.55, -0.4) * mm, "end": v(-1.54, -0.4) * mm});
            skLineSegment(sketch, "E1969", {"start": v(-1.54, -0.4) * mm, "end": v(-1.54, -0.4) * mm});
            skLineSegment(sketch, "E1970", {"start": v(-1.54, -0.4) * mm, "end": v(-1.53, -0.4) * mm});
            skLineSegment(sketch, "E1971", {"start": v(-1.53, -0.4) * mm, "end": v(-1.53, -0.4) * mm});
            skLineSegment(sketch, "E1972", {"start": v(-1.53, -0.4) * mm, "end": v(-1.52, -0.4) * mm});
            skLineSegment(sketch, "E1973", {"start": v(-1.52, -0.4) * mm, "end": v(-1.52, -0.4) * mm});
            skLineSegment(sketch, "E1974", {"start": v(-1.52, -0.4) * mm, "end": v(-1.51, -0.4) * mm});
            skLineSegment(sketch, "E1975", {"start": v(-1.51, -0.4) * mm, "end": v(-1.5, -0.4) * mm});
            skLineSegment(sketch, "E1976", {"start": v(-1.5, -0.4) * mm, "end": v(-1.5, -0.41) * mm});
            skLineSegment(sketch, "E1977", {"start": v(-1.5, -0.41) * mm, "end": v(-1.5, -0.42) * mm});
            skLineSegment(sketch, "E1978", {"start": v(-1.5, -0.42) * mm, "end": v(-1.5, -0.42) * mm});
            skLineSegment(sketch, "E1979", {"start": v(-1.5, -0.42) * mm, "end": v(-1.5, -0.43) * mm});
            skLineSegment(sketch, "E1980", {"start": v(-1.5, -0.43) * mm, "end": v(-1.5, -0.43) * mm});
            skLineSegment(sketch, "E1981", {"start": v(-1.5, -0.43) * mm, "end": v(-1.5, -0.44) * mm});
            skLineSegment(sketch, "E1982", {"start": v(-1.5, -0.44) * mm, "end": v(-1.5, -0.44) * mm});
            skLineSegment(sketch, "E1983", {"start": v(-1.5, -0.44) * mm, "end": v(-1.5, -0.45) * mm});
            skLineSegment(sketch, "E1984", {"start": v(-1.5, -0.45) * mm, "end": v(-1.5, -0.45) * mm});
            skLineSegment(sketch, "E1985", {"start": v(-1.5, -0.45) * mm, "end": v(-1.5, -0.46) * mm});
            skLineSegment(sketch, "E1986", {"start": v(-1.5, -0.46) * mm, "end": v(-1.5, -0.46) * mm});
            skLineSegment(sketch, "E1987", {"start": v(-1.5, -0.46) * mm, "end": v(-1.5, -0.47) * mm});
            skLineSegment(sketch, "E1988", {"start": v(-1.5, -0.47) * mm, "end": v(-1.5, -0.47) * mm});
            skLineSegment(sketch, "E1989", {"start": v(-1.5, -0.47) * mm, "end": v(-1.5, -0.48) * mm});
            skLineSegment(sketch, "E1990", {"start": v(-1.5, -0.48) * mm, "end": v(-1.5, -0.48) * mm});
            skLineSegment(sketch, "E1991", {"start": v(-1.5, -0.48) * mm, "end": v(-1.5, -0.49) * mm});
            skLineSegment(sketch, "E1992", {"start": v(-1.5, -0.49) * mm, "end": v(-1.5, -0.5) * mm});
            skLineSegment(sketch, "E1993", {"start": v(-1.5, -0.5) * mm, "end": v(-1.51, -0.5) * mm});
            skLineSegment(sketch, "E1994", {"start": v(-1.51, -0.5) * mm, "end": v(-1.52, -0.5) * mm});
            skLineSegment(sketch, "E1995", {"start": v(-1.52, -0.5) * mm, "end": v(-1.52, -0.5) * mm});
            skLineSegment(sketch, "E1996", {"start": v(-1.52, -0.5) * mm, "end": v(-1.53, -0.5) * mm});
            skLineSegment(sketch, "E1997", {"start": v(-1.53, -0.5) * mm, "end": v(-1.53, -0.5) * mm});
            skLineSegment(sketch, "E1998", {"start": v(-1.53, -0.5) * mm, "end": v(-1.54, -0.5) * mm});
            skLineSegment(sketch, "E1999", {"start": v(-1.54, -0.5) * mm, "end": v(-1.54, -0.5) * mm});
            skLineSegment(sketch, "E2000", {"start": v(-1.54, -0.5) * mm, "end": v(-1.55, -0.5) * mm});
            skLineSegment(sketch, "E2001", {"start": v(-1.55, -0.5) * mm, "end": v(-1.55, -0.5) * mm});
            skLineSegment(sketch, "E2002", {"start": v(-1.55, -0.5) * mm, "end": v(-1.56, -0.5) * mm});
            skLineSegment(sketch, "E2003", {"start": v(-1.56, -0.5) * mm, "end": v(-1.56, -0.5) * mm});
            skLineSegment(sketch, "E2004", {"start": v(-1.56, -0.5) * mm, "end": v(-1.57, -0.5) * mm});
            skLineSegment(sketch, "E2005", {"start": v(-1.57, -0.5) * mm, "end": v(-1.57, -0.5) * mm});
            skLineSegment(sketch, "E2006", {"start": v(-1.57, -0.5) * mm, "end": v(-1.58, -0.5) * mm});
            skLineSegment(sketch, "E2007", {"start": v(-1.58, -0.5) * mm, "end": v(-1.58, -0.5) * mm});
            skLineSegment(sketch, "E2008", {"start": v(-1.58, -0.5) * mm, "end": v(-1.59, -0.5) * mm});
            skLineSegment(sketch, "E2009", {"start": v(-1.59, -0.5) * mm, "end": v(-1.6, -0.5) * mm});
            skLineSegment(sketch, "E2010", {"start": v(-1.6, -0.5) * mm, "end": v(-1.6, -0.49) * mm});
            skLineSegment(sketch, "E2011", {"start": v(-1.6, -0.49) * mm, "end": v(-1.6, -0.49) * mm});
            skLineSegment(sketch, "E2012", {"start": v(-1.6, -0.49) * mm, "end": v(-1.6, -0.48) * mm});
            skLineSegment(sketch, "E2013", {"start": v(-1.6, -0.48) * mm, "end": v(-1.6, -0.48) * mm});
            skLineSegment(sketch, "E2014", {"start": v(-1.6, -0.48) * mm, "end": v(-1.6, -0.47) * mm});
            skLineSegment(sketch, "E2015", {"start": v(-1.6, -0.47) * mm, "end": v(-1.6, -0.47) * mm});
            skLineSegment(sketch, "E2016", {"start": v(-1.6, -0.47) * mm, "end": v(-1.6, -0.46) * mm});
            skLineSegment(sketch, "E2017", {"start": v(-1.6, -0.46) * mm, "end": v(-1.6, -0.46) * mm});
            skLineSegment(sketch, "E2018", {"start": v(-1.6, -0.46) * mm, "end": v(-1.6, -0.45) * mm});
            skLineSegment(sketch, "E2019", {"start": v(-0.9, -0.47) * mm, "end": v(-0.9, -0.63) * mm});
            skLineSegment(sketch, "E2020", {"start": v(-0.9, -0.63) * mm, "end": v(-0.8, -0.63) * mm});
            skLineSegment(sketch, "E2021", {"start": v(-0.8, -0.63) * mm, "end": v(-0.8, -0.47) * mm});
            skLineSegment(sketch, "E2022", {"start": v(-0.8, -0.47) * mm, "end": v(-0.9, -0.47) * mm});
            skLineSegment(sketch, "E2023", {"start": v(-0.85, -0.53) * mm, "end": v(-0.85, -0.55) * mm});
            skLineSegment(sketch, "E2024", {"start": v(-0.85, -0.55) * mm, "end": v(-0.88, -0.55) * mm});
            skLineSegment(sketch, "E2025", {"start": v(-0.85, -0.55) * mm, "end": v(-0.82, -0.55) * mm});
            skLineSegment(sketch, "E2026", {"start": v(-0.85, -0.55) * mm, "end": v(-0.88, -0.6) * mm});
            skLineSegment(sketch, "E2027", {"start": v(-0.88, -0.6) * mm, "end": v(-0.82, -0.6) * mm});
            skLineSegment(sketch, "E2028", {"start": v(-0.82, -0.6) * mm, "end": v(-0.85, -0.55) * mm});
            skLineSegment(sketch, "E2029", {"start": v(-0.85, -0.55) * mm, "end": v(-0.85, -0.61) * mm});
            skLineSegment(sketch, "E2030", {"start": v(-0.7, -0.63) * mm, "end": v(-0.6, -0.63) * mm});
            skLineSegment(sketch, "E2031", {"start": v(-0.6, -0.63) * mm, "end": v(-0.6, -0.47) * mm});
            skLineSegment(sketch, "E2032", {"start": v(-0.6, -0.47) * mm, "end": v(-0.7, -0.47) * mm});
            skLineSegment(sketch, "E2033", {"start": v(-0.7, -0.47) * mm, "end": v(-0.7, -0.63) * mm});
            skLineSegment(sketch, "E2034", {"start": v(-0.68, -0.6) * mm, "end": v(-0.65, -0.55) * mm});
            skLineSegment(sketch, "E2035", {"start": v(-0.65, -0.55) * mm, "end": v(-0.68, -0.55) * mm});
            skLineSegment(sketch, "E2036", {"start": v(-0.65, -0.55) * mm, "end": v(-0.62, -0.6) * mm});
            skLineSegment(sketch, "E2037", {"start": v(-0.62, -0.6) * mm, "end": v(-0.68, -0.6) * mm});
            skLineSegment(sketch, "E2038", {"start": v(-0.65, -0.61) * mm, "end": v(-0.65, -0.55) * mm});
            skLineSegment(sketch, "E2039", {"start": v(-0.65, -0.55) * mm, "end": v(-0.62, -0.55) * mm});
            skLineSegment(sketch, "E2040", {"start": v(-0.65, -0.55) * mm, "end": v(-0.65, -0.53) * mm});
            skLineSegment(sketch, "E2041", {"start": v(-0.6, -0.97) * mm, "end": v(-0.7, -0.97) * mm});
            skLineSegment(sketch, "E2042", {"start": v(-0.7, -0.97) * mm, "end": v(-0.7, -1.13) * mm});
            skLineSegment(sketch, "E2043", {"start": v(-0.7, -1.13) * mm, "end": v(-0.6, -1.13) * mm});
            skLineSegment(sketch, "E2044", {"start": v(-0.6, -1.13) * mm, "end": v(-0.6, -0.97) * mm});
            skLineSegment(sketch, "E2045", {"start": v(-0.65, -1.03) * mm, "end": v(-0.65, -1.05) * mm});
            skLineSegment(sketch, "E2046", {"start": v(-0.65, -1.05) * mm, "end": v(-0.68, -1.05) * mm});
            skLineSegment(sketch, "E2047", {"start": v(-0.65, -1.05) * mm, "end": v(-0.68, -1.1) * mm});
            skLineSegment(sketch, "E2048", {"start": v(-0.68, -1.1) * mm, "end": v(-0.62, -1.1) * mm});
            skLineSegment(sketch, "E2049", {"start": v(-0.62, -1.1) * mm, "end": v(-0.65, -1.05) * mm});
            skLineSegment(sketch, "E2050", {"start": v(-0.65, -1.05) * mm, "end": v(-0.62, -1.05) * mm});
            skLineSegment(sketch, "E2051", {"start": v(-0.65, -1.05) * mm, "end": v(-0.65, -1.11) * mm});
            skLineSegment(sketch, "E2052", {"start": v(-0.8, -1.13) * mm, "end": v(-0.8, -0.97) * mm});
            skLineSegment(sketch, "E2053", {"start": v(-0.8, -0.97) * mm, "end": v(-0.9, -0.97) * mm});
            skLineSegment(sketch, "E2054", {"start": v(-0.9, -0.97) * mm, "end": v(-0.9, -1.13) * mm});
            skLineSegment(sketch, "E2055", {"start": v(-0.9, -1.13) * mm, "end": v(-0.8, -1.13) * mm});
            skLineSegment(sketch, "E2056", {"start": v(-0.82, -1.1) * mm, "end": v(-0.88, -1.1) * mm});
            skLineSegment(sketch, "E2057", {"start": v(-0.88, -1.1) * mm, "end": v(-0.85, -1.05) * mm});
            skLineSegment(sketch, "E2058", {"start": v(-0.85, -1.05) * mm, "end": v(-0.88, -1.05) * mm});
            skLineSegment(sketch, "E2059", {"start": v(-0.85, -1.05) * mm, "end": v(-0.82, -1.05) * mm});
            skLineSegment(sketch, "E2060", {"start": v(-0.85, -1.05) * mm, "end": v(-0.85, -1.03) * mm});
            skLineSegment(sketch, "E2061", {"start": v(-0.85, -1.05) * mm, "end": v(-0.82, -1.1) * mm});
            skLineSegment(sketch, "E2062", {"start": v(-0.85, -1.11) * mm, "end": v(-0.85, -1.05) * mm});
            skLineSegment(sketch, "E2063", {"start": v(0.47, 0.2) * mm, "end": v(0.49, 0.2) * mm});
            skLineSegment(sketch, "E2064", {"start": v(0.49, 0.2) * mm, "end": v(0.49, 0.3) * mm});
            skLineSegment(sketch, "E2065", {"start": v(0.49, 0.3) * mm, "end": v(0.47, 0.3) * mm});
            skLineSegment(sketch, "E2066", {"start": v(0.47, 0.3) * mm, "end": v(0.47, 0.25) * mm});
            skLineSegment(sketch, "E2067", {"start": v(0.47, 0.25) * mm, "end": v(0.47, 0.2) * mm});
            skLineSegment(sketch, "E2068", {"start": v(0.47, 0.25) * mm, "end": v(0.43, 0.25) * mm});
            skLineSegment(sketch, "E2069", {"start": v(0.43, 0.28) * mm, "end": v(0.43, 0.3) * mm});
            skLineSegment(sketch, "E2070", {"start": v(0.43, 0.3) * mm, "end": v(0.43, 0.31) * mm});
            skLineSegment(sketch, "E2071", {"start": v(0.43, 0.3) * mm, "end": v(0.45, 0.3) * mm});
            skLineSegment(sketch, "E2072", {"start": v(0.43, 0.3) * mm, "end": v(0.42, 0.3) * mm});
            skLineSegment(sketch, "E2073", {"start": v(0.39, 0.25) * mm, "end": v(0.4, 0.26) * mm});
            skLineSegment(sketch, "E2074", {"start": v(0.4, 0.26) * mm, "end": v(0.4, 0.26) * mm});
            skLineSegment(sketch, "E2075", {"start": v(0.4, 0.26) * mm, "end": v(0.4, 0.27) * mm});
            skLineSegment(sketch, "E2076", {"start": v(0.4, 0.27) * mm, "end": v(0.4, 0.28) * mm});
            skLineSegment(sketch, "E2077", {"start": v(0.4, 0.28) * mm, "end": v(0.4, 0.28) * mm});
            skLineSegment(sketch, "E2078", {"start": v(0.4, 0.28) * mm, "end": v(0.4, 0.29) * mm});
            skLineSegment(sketch, "E2079", {"start": v(0.4, 0.29) * mm, "end": v(0.4, 0.3) * mm});
            skLineSegment(sketch, "E2080", {"start": v(0.4, 0.3) * mm, "end": v(0.4, 0.3) * mm});
            skLineSegment(sketch, "E2081", {"start": v(0.4, 0.3) * mm, "end": v(0.4, 0.31) * mm});
            skLineSegment(sketch, "E2082", {"start": v(0.4, 0.31) * mm, "end": v(0.41, 0.32) * mm});
            skLineSegment(sketch, "E2083", {"start": v(0.41, 0.32) * mm, "end": v(0.42, 0.32) * mm});
            skLineSegment(sketch, "E2084", {"start": v(0.42, 0.32) * mm, "end": v(0.42, 0.33) * mm});
            skLineSegment(sketch, "E2085", {"start": v(0.42, 0.33) * mm, "end": v(0.43, 0.33) * mm});
            skLineSegment(sketch, "E2086", {"start": v(0.43, 0.33) * mm, "end": v(0.43, 0.34) * mm});
            skLineSegment(sketch, "E2087", {"start": v(0.43, 0.34) * mm, "end": v(0.44, 0.34) * mm});
            skLineSegment(sketch, "E2088", {"start": v(0.44, 0.34) * mm, "end": v(0.44, 0.34) * mm});
            skLineSegment(sketch, "E2089", {"start": v(0.44, 0.34) * mm, "end": v(0.45, 0.35) * mm});
            skLineSegment(sketch, "E2090", {"start": v(0.45, 0.35) * mm, "end": v(0.45, 0.35) * mm});
            skLineSegment(sketch, "E2091", {"start": v(0.45, 0.35) * mm, "end": v(0.46, 0.35) * mm});
            skLineSegment(sketch, "E2092", {"start": v(0.46, 0.35) * mm, "end": v(0.47, 0.35) * mm});
            skLineSegment(sketch, "E2093", {"start": v(0.47, 0.35) * mm, "end": v(0.47, 0.36) * mm});
            skLineSegment(sketch, "E2094", {"start": v(0.47, 0.36) * mm, "end": v(0.48, 0.36) * mm});
            skLineSegment(sketch, "E2095", {"start": v(0.48, 0.36) * mm, "end": v(0.49, 0.36) * mm});
            skLineSegment(sketch, "E2096", {"start": v(0.49, 0.36) * mm, "end": v(0.5, 0.36) * mm});
            skLineSegment(sketch, "E2097", {"start": v(0.5, 0.36) * mm, "end": v(0.5, 0.36) * mm});
            skLineSegment(sketch, "E2098", {"start": v(0.5, 0.36) * mm, "end": v(0.51, 0.36) * mm});
            skLineSegment(sketch, "E2099", {"start": v(0.51, 0.36) * mm, "end": v(0.52, 0.36) * mm});
            skLineSegment(sketch, "E2100", {"start": v(0.52, 0.36) * mm, "end": v(0.52, 0.36) * mm});
            skLineSegment(sketch, "E2101", {"start": v(0.52, 0.36) * mm, "end": v(0.53, 0.36) * mm});
            skLineSegment(sketch, "E2102", {"start": v(0.53, 0.36) * mm, "end": v(0.54, 0.35) * mm});
            skLineSegment(sketch, "E2103", {"start": v(0.54, 0.35) * mm, "end": v(0.54, 0.35) * mm});
            skLineSegment(sketch, "E2104", {"start": v(0.54, 0.35) * mm, "end": v(0.55, 0.35) * mm});
            skLineSegment(sketch, "E2105", {"start": v(0.55, 0.35) * mm, "end": v(0.55, 0.35) * mm});
            skLineSegment(sketch, "E2106", {"start": v(0.55, 0.35) * mm, "end": v(0.56, 0.34) * mm});
            skLineSegment(sketch, "E2107", {"start": v(0.56, 0.34) * mm, "end": v(0.57, 0.34) * mm});
            skLineSegment(sketch, "E2108", {"start": v(0.57, 0.34) * mm, "end": v(0.57, 0.33) * mm});
            skLineSegment(sketch, "E2109", {"start": v(0.57, 0.33) * mm, "end": v(0.58, 0.33) * mm});
            skLineSegment(sketch, "E2110", {"start": v(0.58, 0.33) * mm, "end": v(0.58, 0.32) * mm});
            skLineSegment(sketch, "E2111", {"start": v(0.58, 0.32) * mm, "end": v(0.59, 0.32) * mm});
            skLineSegment(sketch, "E2112", {"start": v(0.59, 0.32) * mm, "end": v(0.59, 0.31) * mm});
            skLineSegment(sketch, "E2113", {"start": v(0.59, 0.31) * mm, "end": v(0.6, 0.3) * mm});
            skLineSegment(sketch, "E2114", {"start": v(0.6, 0.3) * mm, "end": v(0.6, 0.3) * mm});
            skLineSegment(sketch, "E2115", {"start": v(0.6, 0.3) * mm, "end": v(0.6, 0.29) * mm});
            skLineSegment(sketch, "E2116", {"start": v(0.6, 0.29) * mm, "end": v(0.6, 0.28) * mm});
            skLineSegment(sketch, "E2117", {"start": v(0.6, 0.28) * mm, "end": v(0.6, 0.27) * mm});
            skLineSegment(sketch, "E2118", {"start": v(0.6, 0.27) * mm, "end": v(0.6, 0.27) * mm});
            skLineSegment(sketch, "E2119", {"start": v(0.6, 0.27) * mm, "end": v(0.6, 0.26) * mm});
            skLineSegment(sketch, "E2120", {"start": v(0.6, 0.26) * mm, "end": v(0.61, 0.25) * mm});
            skLineSegment(sketch, "E2121", {"start": v(0.61, 0.25) * mm, "end": v(0.61, 0.25) * mm});
            skLineSegment(sketch, "E2122", {"start": v(0.61, 0.25) * mm, "end": v(0.6, 0.24) * mm});
            skLineSegment(sketch, "E2123", {"start": v(0.6, 0.24) * mm, "end": v(0.6, 0.23) * mm});
            skLineSegment(sketch, "E2124", {"start": v(0.6, 0.23) * mm, "end": v(0.6, 0.23) * mm});
            skLineSegment(sketch, "E2125", {"start": v(0.6, 0.23) * mm, "end": v(0.6, 0.22) * mm});
            skLineSegment(sketch, "E2126", {"start": v(0.6, 0.22) * mm, "end": v(0.6, 0.21) * mm});
            skLineSegment(sketch, "E2127", {"start": v(0.6, 0.21) * mm, "end": v(0.6, 0.2) * mm});
            skLineSegment(sketch, "E2128", {"start": v(0.6, 0.2) * mm, "end": v(0.6, 0.2) * mm});
            skLineSegment(sketch, "E2129", {"start": v(0.6, 0.2) * mm, "end": v(0.59, 0.19) * mm});
            skLineSegment(sketch, "E2130", {"start": v(0.59, 0.19) * mm, "end": v(0.59, 0.18) * mm});
            skLineSegment(sketch, "E2131", {"start": v(0.59, 0.18) * mm, "end": v(0.58, 0.18) * mm});
            skLineSegment(sketch, "E2132", {"start": v(0.58, 0.18) * mm, "end": v(0.58, 0.17) * mm});
            skLineSegment(sketch, "E2133", {"start": v(0.58, 0.17) * mm, "end": v(0.57, 0.17) * mm});
            skLineSegment(sketch, "E2134", {"start": v(0.57, 0.17) * mm, "end": v(0.57, 0.16) * mm});
            skLineSegment(sketch, "E2135", {"start": v(0.57, 0.16) * mm, "end": v(0.56, 0.16) * mm});
            skLineSegment(sketch, "E2136", {"start": v(0.56, 0.16) * mm, "end": v(0.55, 0.15) * mm});
            skLineSegment(sketch, "E2137", {"start": v(0.55, 0.15) * mm, "end": v(0.55, 0.15) * mm});
            skLineSegment(sketch, "E2138", {"start": v(0.55, 0.15) * mm, "end": v(0.54, 0.15) * mm});
            skLineSegment(sketch, "E2139", {"start": v(0.54, 0.15) * mm, "end": v(0.54, 0.15) * mm});
            skLineSegment(sketch, "E2140", {"start": v(0.54, 0.15) * mm, "end": v(0.53, 0.14) * mm});
            skLineSegment(sketch, "E2141", {"start": v(0.53, 0.14) * mm, "end": v(0.52, 0.14) * mm});
            skLineSegment(sketch, "E2142", {"start": v(0.52, 0.14) * mm, "end": v(0.52, 0.14) * mm});
            skLineSegment(sketch, "E2143", {"start": v(0.52, 0.14) * mm, "end": v(0.51, 0.14) * mm});
            skLineSegment(sketch, "E2144", {"start": v(0.51, 0.14) * mm, "end": v(0.5, 0.14) * mm});
            skLineSegment(sketch, "E2145", {"start": v(0.5, 0.14) * mm, "end": v(0.5, 0.14) * mm});
            skLineSegment(sketch, "E2146", {"start": v(0.5, 0.14) * mm, "end": v(0.49, 0.14) * mm});
            skLineSegment(sketch, "E2147", {"start": v(0.49, 0.14) * mm, "end": v(0.48, 0.14) * mm});
            skLineSegment(sketch, "E2148", {"start": v(0.48, 0.14) * mm, "end": v(0.47, 0.14) * mm});
            skLineSegment(sketch, "E2149", {"start": v(0.47, 0.14) * mm, "end": v(0.47, 0.15) * mm});
            skLineSegment(sketch, "E2150", {"start": v(0.47, 0.15) * mm, "end": v(0.46, 0.15) * mm});
            skLineSegment(sketch, "E2151", {"start": v(0.46, 0.15) * mm, "end": v(0.45, 0.15) * mm});
            skLineSegment(sketch, "E2152", {"start": v(0.45, 0.15) * mm, "end": v(0.45, 0.15) * mm});
            skLineSegment(sketch, "E2153", {"start": v(0.45, 0.15) * mm, "end": v(0.44, 0.16) * mm});
            skLineSegment(sketch, "E2154", {"start": v(0.44, 0.16) * mm, "end": v(0.44, 0.16) * mm});
            skLineSegment(sketch, "E2155", {"start": v(0.44, 0.16) * mm, "end": v(0.43, 0.16) * mm});
            skLineSegment(sketch, "E2156", {"start": v(0.43, 0.16) * mm, "end": v(0.43, 0.17) * mm});
            skLineSegment(sketch, "E2157", {"start": v(0.43, 0.17) * mm, "end": v(0.42, 0.17) * mm});
            skLineSegment(sketch, "E2158", {"start": v(0.42, 0.17) * mm, "end": v(0.42, 0.18) * mm});
            skLineSegment(sketch, "E2159", {"start": v(0.42, 0.18) * mm, "end": v(0.41, 0.18) * mm});
            skLineSegment(sketch, "E2160", {"start": v(0.41, 0.18) * mm, "end": v(0.4, 0.19) * mm});
            skLineSegment(sketch, "E2161", {"start": v(0.4, 0.19) * mm, "end": v(0.4, 0.2) * mm});
            skLineSegment(sketch, "E2162", {"start": v(0.4, 0.2) * mm, "end": v(0.4, 0.2) * mm});
            skLineSegment(sketch, "E2163", {"start": v(0.4, 0.2) * mm, "end": v(0.4, 0.21) * mm});
            skLineSegment(sketch, "E2164", {"start": v(0.4, 0.21) * mm, "end": v(0.4, 0.22) * mm});
            skLineSegment(sketch, "E2165", {"start": v(0.4, 0.22) * mm, "end": v(0.4, 0.22) * mm});
            skLineSegment(sketch, "E2166", {"start": v(0.4, 0.22) * mm, "end": v(0.4, 0.23) * mm});
            skLineSegment(sketch, "E2167", {"start": v(0.4, 0.23) * mm, "end": v(0.4, 0.24) * mm});
            skLineSegment(sketch, "E2168", {"start": v(0.4, 0.24) * mm, "end": v(0.4, 0.24) * mm});
            skLineSegment(sketch, "E2169", {"start": v(0.4, 0.24) * mm, "end": v(0.39, 0.25) * mm});
            skLineSegment(sketch, "E2170", {"start": v(0.3, 0.25) * mm, "end": v(0.3, 0.23) * mm});
            skLineSegment(sketch, "E2171", {"start": v(0.3, 0.23) * mm, "end": v(0.3, 0.23) * mm});
            skLineSegment(sketch, "E2172", {"start": v(0.3, 0.23) * mm, "end": v(0.29, 0.23) * mm});
            skLineSegment(sketch, "E2173", {"start": v(0.29, 0.23) * mm, "end": v(0.29, 0.23) * mm});
            skLineSegment(sketch, "E2174", {"start": v(0.29, 0.23) * mm, "end": v(0.28, 0.22) * mm});
            skLineSegment(sketch, "E2175", {"start": v(0.28, 0.22) * mm, "end": v(0.22, 0.22) * mm});
            skLineSegment(sketch, "E2176", {"start": v(0.22, 0.22) * mm, "end": v(0.21, 0.23) * mm});
            skLineSegment(sketch, "E2177", {"start": v(0.21, 0.23) * mm, "end": v(0.21, 0.23) * mm});
            skLineSegment(sketch, "E2178", {"start": v(0.21, 0.23) * mm, "end": v(0.2, 0.23) * mm});
            skLineSegment(sketch, "E2179", {"start": v(0.2, 0.23) * mm, "end": v(0.2, 0.23) * mm});
            skLineSegment(sketch, "E2180", {"start": v(0.2, 0.23) * mm, "end": v(0.2, 0.25) * mm});
            skLineSegment(sketch, "E2181", {"start": v(0.2, 0.25) * mm, "end": v(0.21, 0.25) * mm});
            skLineSegment(sketch, "E2182", {"start": v(0.21, 0.25) * mm, "end": v(0.21, 0.44) * mm});
            skLineSegment(sketch, "E2183", {"start": v(0.21, 0.44) * mm, "end": v(0.2, 0.45) * mm});
            skLineSegment(sketch, "E2184", {"start": v(0.2, 0.45) * mm, "end": v(0.2, 0.46) * mm});
            skLineSegment(sketch, "E2185", {"start": v(0.2, 0.46) * mm, "end": v(0.2, 0.45) * mm});
            skLineSegment(sketch, "E2186", {"start": v(0.2, 0.45) * mm, "end": v(0.2, 0.44) * mm});
            skLineSegment(sketch, "E2187", {"start": v(0.2, 0.44) * mm, "end": v(0.2, 0.25) * mm});
            skLineSegment(sketch, "E2188", {"start": v(0.2, 0.25) * mm, "end": v(0.2, 0.25) * mm});
            skLineSegment(sketch, "E2189", {"start": v(0.2, 0.25) * mm, "end": v(0.2, 0.23) * mm});
            skLineSegment(sketch, "E2190", {"start": v(0.2, 0.23) * mm, "end": v(0.19, 0.23) * mm});
            skLineSegment(sketch, "E2191", {"start": v(0.19, 0.23) * mm, "end": v(0.19, 0.23) * mm});
            skLineSegment(sketch, "E2192", {"start": v(0.19, 0.23) * mm, "end": v(0.18, 0.22) * mm});
            skLineSegment(sketch, "E2193", {"start": v(0.18, 0.22) * mm, "end": v(0.11, 0.22) * mm});
            skLineSegment(sketch, "E2194", {"start": v(0.11, 0.22) * mm, "end": v(0.11, 0.23) * mm});
            skLineSegment(sketch, "E2195", {"start": v(0.11, 0.23) * mm, "end": v(0.11, 0.23) * mm});
            skLineSegment(sketch, "E2196", {"start": v(0.11, 0.23) * mm, "end": v(0.1, 0.23) * mm});
            skLineSegment(sketch, "E2197", {"start": v(0.1, 0.23) * mm, "end": v(0.1, 0.23) * mm});
            skLineSegment(sketch, "E2198", {"start": v(0.1, 0.23) * mm, "end": v(0.1, 0.25) * mm});
            skLineSegment(sketch, "E2199", {"start": v(0.1, 0.25) * mm, "end": v(0.11, 0.25) * mm});
            skLineSegment(sketch, "E2200", {"start": v(0.11, 0.25) * mm, "end": v(0.11, 0.44) * mm});
            skLineSegment(sketch, "E2201", {"start": v(0.11, 0.44) * mm, "end": v(0.1, 0.45) * mm});
            skLineSegment(sketch, "E2202", {"start": v(0.1, 0.45) * mm, "end": v(0.1, 0.46) * mm});
            skLineSegment(sketch, "E2203", {"start": v(0.1, 0.46) * mm, "end": v(0.1, 0.47) * mm});
            skLineSegment(sketch, "E2204", {"start": v(0.1, 0.47) * mm, "end": v(0.1, 0.47) * mm});
            skLineSegment(sketch, "E2205", {"start": v(0.1, 0.47) * mm, "end": v(0.11, 0.47) * mm});
            skLineSegment(sketch, "E2206", {"start": v(0.11, 0.47) * mm, "end": v(0.11, 0.47) * mm});
            skLineSegment(sketch, "E2207", {"start": v(0.11, 0.47) * mm, "end": v(0.18, 0.47) * mm});
            skLineSegment(sketch, "E2208", {"start": v(0.18, 0.47) * mm, "end": v(0.19, 0.47) * mm});
            skLineSegment(sketch, "E2209", {"start": v(0.19, 0.47) * mm, "end": v(0.19, 0.47) * mm});
            skLineSegment(sketch, "E2210", {"start": v(0.19, 0.47) * mm, "end": v(0.2, 0.47) * mm});
            skLineSegment(sketch, "E2211", {"start": v(0.2, 0.47) * mm, "end": v(0.2, 0.47) * mm});
            skLineSegment(sketch, "E2212", {"start": v(0.2, 0.47) * mm, "end": v(0.2, 0.46) * mm});
            skLineSegment(sketch, "E2213", {"start": v(0.2, 0.46) * mm, "end": v(0.2, 0.47) * mm});
            skLineSegment(sketch, "E2214", {"start": v(0.2, 0.47) * mm, "end": v(0.21, 0.47) * mm});
            skLineSegment(sketch, "E2215", {"start": v(0.21, 0.47) * mm, "end": v(0.21, 0.47) * mm});
            skLineSegment(sketch, "E2216", {"start": v(0.21, 0.47) * mm, "end": v(0.22, 0.47) * mm});
            skLineSegment(sketch, "E2217", {"start": v(0.22, 0.47) * mm, "end": v(0.28, 0.47) * mm});
            skLineSegment(sketch, "E2218", {"start": v(0.28, 0.47) * mm, "end": v(0.29, 0.47) * mm});
            skLineSegment(sketch, "E2219", {"start": v(0.29, 0.47) * mm, "end": v(0.29, 0.47) * mm});
            skLineSegment(sketch, "E2220", {"start": v(0.29, 0.47) * mm, "end": v(0.3, 0.47) * mm});
            skLineSegment(sketch, "E2221", {"start": v(0.3, 0.47) * mm, "end": v(0.3, 0.47) * mm});
            skLineSegment(sketch, "E2222", {"start": v(0.3, 0.47) * mm, "end": v(0.3, 0.46) * mm});
            skLineSegment(sketch, "E2223", {"start": v(0.3, 0.46) * mm, "end": v(0.3, 0.45) * mm});
            skLineSegment(sketch, "E2224", {"start": v(0.3, 0.45) * mm, "end": v(0.29, 0.44) * mm});
            skLineSegment(sketch, "E2225", {"start": v(0.29, 0.44) * mm, "end": v(0.29, 0.25) * mm});
            skLineSegment(sketch, "E2226", {"start": v(0.29, 0.25) * mm, "end": v(0.3, 0.25) * mm});
            skLineSegment(sketch, "E2227", {"start": v(0.53, 0.25) * mm, "end": v(0.57, 0.25) * mm});
            skLineSegment(sketch, "E2228", {"start": v(0.77, 0.27) * mm, "end": v(0.8, 0.27) * mm});
            skLineSegment(sketch, "E2229", {"start": v(0.78, 0.25) * mm, "end": v(0.78, 0.28) * mm});
            skLineSegment(sketch, "E2230", {"start": v(0.85, 0.33) * mm, "end": v(0.85, 0.35) * mm});
            skLineSegment(sketch, "E2231", {"start": v(0.85, 0.35) * mm, "end": v(0.85, 0.36) * mm});
            skLineSegment(sketch, "E2232", {"start": v(0.85, 0.36) * mm, "end": v(0.8, 0.36) * mm});
            skLineSegment(sketch, "E2233", {"start": v(0.8, 0.36) * mm, "end": v(0.8, 0.39) * mm});
            skLineSegment(sketch, "E2234", {"start": v(0.8, 0.39) * mm, "end": v(0.9, 0.39) * mm});
            skLineSegment(sketch, "E2235", {"start": v(0.9, 0.39) * mm, "end": v(0.9, 0.36) * mm});
            skLineSegment(sketch, "E2236", {"start": v(0.9, 0.36) * mm, "end": v(0.85, 0.36) * mm});
            skLineSegment(sketch, "E2237", {"start": v(0.68, 0.4) * mm, "end": v(0.68, 0.4) * mm});
            skLineSegment(sketch, "E2238", {"start": v(0.68, 0.4) * mm, "end": v(0.68, 0.42) * mm});
            skLineSegment(sketch, "E2239", {"start": v(0.68, 0.42) * mm, "end": v(0.68, 0.43) * mm});
            skLineSegment(sketch, "E2240", {"start": v(0.68, 0.43) * mm, "end": v(0.68, 0.43) * mm});
            skLineSegment(sketch, "E2241", {"start": v(0.68, 0.43) * mm, "end": v(0.68, 0.44) * mm});
            skLineSegment(sketch, "E2242", {"start": v(0.68, 0.44) * mm, "end": v(0.68, 0.45) * mm});
            skLineSegment(sketch, "E2243", {"start": v(0.68, 0.45) * mm, "end": v(0.69, 0.46) * mm});
            skLineSegment(sketch, "E2244", {"start": v(0.69, 0.46) * mm, "end": v(0.69, 0.47) * mm});
            skLineSegment(sketch, "E2245", {"start": v(0.69, 0.47) * mm, "end": v(0.7, 0.47) * mm});
            skLineSegment(sketch, "E2246", {"start": v(0.7, 0.47) * mm, "end": v(0.7, 0.48) * mm});
            skLineSegment(sketch, "E2247", {"start": v(0.7, 0.48) * mm, "end": v(0.7, 0.49) * mm});
            skLineSegment(sketch, "E2248", {"start": v(0.7, 0.49) * mm, "end": v(0.7, 0.5) * mm});
            skLineSegment(sketch, "E2249", {"start": v(0.7, 0.5) * mm, "end": v(0.7, 0.5) * mm});
            skLineSegment(sketch, "E2250", {"start": v(0.7, 0.5) * mm, "end": v(0.71, 0.51) * mm});
            skLineSegment(sketch, "E2251", {"start": v(0.71, 0.51) * mm, "end": v(0.72, 0.52) * mm});
            skLineSegment(sketch, "E2252", {"start": v(0.72, 0.52) * mm, "end": v(0.73, 0.52) * mm});
            skLineSegment(sketch, "E2253", {"start": v(0.73, 0.52) * mm, "end": v(0.73, 0.53) * mm});
            skLineSegment(sketch, "E2254", {"start": v(0.73, 0.53) * mm, "end": v(0.74, 0.54) * mm});
            skLineSegment(sketch, "E2255", {"start": v(0.74, 0.54) * mm, "end": v(0.75, 0.54) * mm});
            skLineSegment(sketch, "E2256", {"start": v(0.75, 0.54) * mm, "end": v(0.75, 0.55) * mm});
            skLineSegment(sketch, "E2257", {"start": v(0.75, 0.55) * mm, "end": v(0.76, 0.55) * mm});
            skLineSegment(sketch, "E2258", {"start": v(0.76, 0.55) * mm, "end": v(0.77, 0.55) * mm});
            skLineSegment(sketch, "E2259", {"start": v(0.77, 0.55) * mm, "end": v(0.78, 0.56) * mm});
            skLineSegment(sketch, "E2260", {"start": v(0.78, 0.56) * mm, "end": v(0.78, 0.56) * mm});
            skLineSegment(sketch, "E2261", {"start": v(0.78, 0.56) * mm, "end": v(0.8, 0.56) * mm});
            skLineSegment(sketch, "E2262", {"start": v(0.8, 0.56) * mm, "end": v(0.8, 0.57) * mm});
            skLineSegment(sketch, "E2263", {"start": v(0.8, 0.57) * mm, "end": v(0.8, 0.57) * mm});
            skLineSegment(sketch, "E2264", {"start": v(0.8, 0.57) * mm, "end": v(0.82, 0.57) * mm});
            skLineSegment(sketch, "E2265", {"start": v(0.82, 0.57) * mm, "end": v(0.82, 0.57) * mm});
            skLineSegment(sketch, "E2266", {"start": v(0.82, 0.57) * mm, "end": v(0.83, 0.57) * mm});
            skLineSegment(sketch, "E2267", {"start": v(0.83, 0.57) * mm, "end": v(0.84, 0.57) * mm});
            skLineSegment(sketch, "E2268", {"start": v(0.84, 0.57) * mm, "end": v(0.85, 0.57) * mm});
            skLineSegment(sketch, "E2269", {"start": v(0.85, 0.57) * mm, "end": v(0.86, 0.57) * mm});
            skLineSegment(sketch, "E2270", {"start": v(0.86, 0.57) * mm, "end": v(0.87, 0.57) * mm});
            skLineSegment(sketch, "E2271", {"start": v(0.87, 0.57) * mm, "end": v(0.88, 0.57) * mm});
            skLineSegment(sketch, "E2272", {"start": v(0.88, 0.57) * mm, "end": v(0.88, 0.57) * mm});
            skLineSegment(sketch, "E2273", {"start": v(0.88, 0.57) * mm, "end": v(0.9, 0.57) * mm});
            skLineSegment(sketch, "E2274", {"start": v(0.9, 0.57) * mm, "end": v(0.9, 0.57) * mm});
            skLineSegment(sketch, "E2275", {"start": v(0.9, 0.57) * mm, "end": v(0.9, 0.56) * mm});
            skLineSegment(sketch, "E2276", {"start": v(0.9, 0.56) * mm, "end": v(0.92, 0.56) * mm});
            skLineSegment(sketch, "E2277", {"start": v(0.92, 0.56) * mm, "end": v(0.92, 0.56) * mm});
            skLineSegment(sketch, "E2278", {"start": v(0.92, 0.56) * mm, "end": v(0.93, 0.55) * mm});
            skLineSegment(sketch, "E2279", {"start": v(0.93, 0.55) * mm, "end": v(0.94, 0.55) * mm});
            skLineSegment(sketch, "E2280", {"start": v(0.94, 0.55) * mm, "end": v(0.95, 0.55) * mm});
            skLineSegment(sketch, "E2281", {"start": v(0.95, 0.55) * mm, "end": v(0.95, 0.54) * mm});
            skLineSegment(sketch, "E2282", {"start": v(0.95, 0.54) * mm, "end": v(0.96, 0.54) * mm});
            skLineSegment(sketch, "E2283", {"start": v(0.96, 0.54) * mm, "end": v(0.97, 0.53) * mm});
            skLineSegment(sketch, "E2284", {"start": v(0.97, 0.53) * mm, "end": v(0.97, 0.52) * mm});
            skLineSegment(sketch, "E2285", {"start": v(0.97, 0.52) * mm, "end": v(0.98, 0.52) * mm});
            skLineSegment(sketch, "E2286", {"start": v(0.98, 0.52) * mm, "end": v(0.99, 0.51) * mm});
            skLineSegment(sketch, "E2287", {"start": v(0.99, 0.51) * mm, "end": v(1, 0.5) * mm});
            skLineSegment(sketch, "E2288", {"start": v(1, 0.5) * mm, "end": v(1, 0.5) * mm});
            skLineSegment(sketch, "E2289", {"start": v(1, 0.5) * mm, "end": v(1, 0.49) * mm});
            skLineSegment(sketch, "E2290", {"start": v(1, 0.49) * mm, "end": v(1, 0.48) * mm});
            skLineSegment(sketch, "E2291", {"start": v(1, 0.48) * mm, "end": v(1, 0.47) * mm});
            skLineSegment(sketch, "E2292", {"start": v(1, 0.47) * mm, "end": v(1.01, 0.47) * mm});
            skLineSegment(sketch, "E2293", {"start": v(1.01, 0.47) * mm, "end": v(1.01, 0.46) * mm});
            skLineSegment(sketch, "E2294", {"start": v(1.01, 0.46) * mm, "end": v(1.02, 0.45) * mm});
            skLineSegment(sketch, "E2295", {"start": v(1.02, 0.45) * mm, "end": v(1.02, 0.44) * mm});
            skLineSegment(sketch, "E2296", {"start": v(1.02, 0.44) * mm, "end": v(1.02, 0.43) * mm});
            skLineSegment(sketch, "E2297", {"start": v(1.02, 0.43) * mm, "end": v(1.02, 0.43) * mm});
            skLineSegment(sketch, "E2298", {"start": v(1.02, 0.43) * mm, "end": v(1.02, 0.42) * mm});
            skLineSegment(sketch, "E2299", {"start": v(1.02, 0.42) * mm, "end": v(1.02, 0.4) * mm});
            skLineSegment(sketch, "E2300", {"start": v(1.02, 0.4) * mm, "end": v(1.03, 0.4) * mm});
            skLineSegment(sketch, "E2301", {"start": v(1.03, 0.4) * mm, "end": v(1.02, 0.4) * mm});
            skLineSegment(sketch, "E2302", {"start": v(1.02, 0.4) * mm, "end": v(1.02, 0.38) * mm});
            skLineSegment(sketch, "E2303", {"start": v(1.02, 0.38) * mm, "end": v(1.02, 0.37) * mm});
            skLineSegment(sketch, "E2304", {"start": v(1.02, 0.37) * mm, "end": v(1.02, 0.37) * mm});
            skLineSegment(sketch, "E2305", {"start": v(1.02, 0.37) * mm, "end": v(1.02, 0.36) * mm});
            skLineSegment(sketch, "E2306", {"start": v(1.02, 0.36) * mm, "end": v(1.02, 0.35) * mm});
            skLineSegment(sketch, "E2307", {"start": v(1.02, 0.35) * mm, "end": v(1.01, 0.34) * mm});
            skLineSegment(sketch, "E2308", {"start": v(1.01, 0.34) * mm, "end": v(1.01, 0.33) * mm});
            skLineSegment(sketch, "E2309", {"start": v(1.01, 0.33) * mm, "end": v(1, 0.33) * mm});
            skLineSegment(sketch, "E2310", {"start": v(1, 0.33) * mm, "end": v(1, 0.32) * mm});
            skLineSegment(sketch, "E2311", {"start": v(1, 0.32) * mm, "end": v(1, 0.3) * mm});
            skLineSegment(sketch, "E2312", {"start": v(1, 0.3) * mm, "end": v(1, 0.3) * mm});
            skLineSegment(sketch, "E2313", {"start": v(1, 0.3) * mm, "end": v(0.99, 0.29) * mm});
            skLineSegment(sketch, "E2314", {"start": v(0.99, 0.29) * mm, "end": v(0.98, 0.28) * mm});
            skLineSegment(sketch, "E2315", {"start": v(0.98, 0.28) * mm, "end": v(0.97, 0.28) * mm});
            skLineSegment(sketch, "E2316", {"start": v(0.97, 0.28) * mm, "end": v(0.97, 0.27) * mm});
            skLineSegment(sketch, "E2317", {"start": v(0.97, 0.27) * mm, "end": v(0.96, 0.26) * mm});
            skLineSegment(sketch, "E2318", {"start": v(0.96, 0.26) * mm, "end": v(0.95, 0.26) * mm});
            skLineSegment(sketch, "E2319", {"start": v(0.95, 0.26) * mm, "end": v(0.95, 0.25) * mm});
            skLineSegment(sketch, "E2320", {"start": v(0.95, 0.25) * mm, "end": v(0.94, 0.25) * mm});
            skLineSegment(sketch, "E2321", {"start": v(0.94, 0.25) * mm, "end": v(0.93, 0.25) * mm});
            skLineSegment(sketch, "E2322", {"start": v(0.93, 0.25) * mm, "end": v(0.92, 0.24) * mm});
            skLineSegment(sketch, "E2323", {"start": v(0.92, 0.24) * mm, "end": v(0.92, 0.24) * mm});
            skLineSegment(sketch, "E2324", {"start": v(0.92, 0.24) * mm, "end": v(0.9, 0.24) * mm});
            skLineSegment(sketch, "E2325", {"start": v(0.9, 0.24) * mm, "end": v(0.9, 0.23) * mm});
            skLineSegment(sketch, "E2326", {"start": v(0.9, 0.23) * mm, "end": v(0.9, 0.23) * mm});
            skLineSegment(sketch, "E2327", {"start": v(0.9, 0.23) * mm, "end": v(0.88, 0.23) * mm});
            skLineSegment(sketch, "E2328", {"start": v(0.88, 0.23) * mm, "end": v(0.88, 0.23) * mm});
            skLineSegment(sketch, "E2329", {"start": v(0.88, 0.23) * mm, "end": v(0.87, 0.23) * mm});
            skLineSegment(sketch, "E2330", {"start": v(0.87, 0.23) * mm, "end": v(0.86, 0.23) * mm});
            skLineSegment(sketch, "E2331", {"start": v(0.86, 0.23) * mm, "end": v(0.85, 0.22) * mm});
            skLineSegment(sketch, "E2332", {"start": v(0.85, 0.22) * mm, "end": v(0.84, 0.23) * mm});
            skLineSegment(sketch, "E2333", {"start": v(0.84, 0.23) * mm, "end": v(0.83, 0.23) * mm});
            skLineSegment(sketch, "E2334", {"start": v(0.83, 0.23) * mm, "end": v(0.82, 0.23) * mm});
            skLineSegment(sketch, "E2335", {"start": v(0.82, 0.23) * mm, "end": v(0.82, 0.23) * mm});
            skLineSegment(sketch, "E2336", {"start": v(0.82, 0.23) * mm, "end": v(0.8, 0.23) * mm});
            skLineSegment(sketch, "E2337", {"start": v(0.8, 0.23) * mm, "end": v(0.8, 0.23) * mm});
            skLineSegment(sketch, "E2338", {"start": v(0.8, 0.23) * mm, "end": v(0.8, 0.24) * mm});
            skLineSegment(sketch, "E2339", {"start": v(0.8, 0.24) * mm, "end": v(0.78, 0.24) * mm});
            skLineSegment(sketch, "E2340", {"start": v(0.78, 0.24) * mm, "end": v(0.78, 0.24) * mm});
            skLineSegment(sketch, "E2341", {"start": v(0.78, 0.24) * mm, "end": v(0.77, 0.25) * mm});
            skLineSegment(sketch, "E2342", {"start": v(0.77, 0.25) * mm, "end": v(0.76, 0.25) * mm});
            skLineSegment(sketch, "E2343", {"start": v(0.76, 0.25) * mm, "end": v(0.75, 0.25) * mm});
            skLineSegment(sketch, "E2344", {"start": v(0.75, 0.25) * mm, "end": v(0.75, 0.26) * mm});
            skLineSegment(sketch, "E2345", {"start": v(0.75, 0.26) * mm, "end": v(0.74, 0.26) * mm});
            skLineSegment(sketch, "E2346", {"start": v(0.74, 0.26) * mm, "end": v(0.73, 0.27) * mm});
            skLineSegment(sketch, "E2347", {"start": v(0.73, 0.27) * mm, "end": v(0.73, 0.28) * mm});
            skLineSegment(sketch, "E2348", {"start": v(0.73, 0.28) * mm, "end": v(0.72, 0.28) * mm});
            skLineSegment(sketch, "E2349", {"start": v(0.72, 0.28) * mm, "end": v(0.71, 0.29) * mm});
            skLineSegment(sketch, "E2350", {"start": v(0.71, 0.29) * mm, "end": v(0.7, 0.3) * mm});
            skLineSegment(sketch, "E2351", {"start": v(0.7, 0.3) * mm, "end": v(0.7, 0.3) * mm});
            skLineSegment(sketch, "E2352", {"start": v(0.7, 0.3) * mm, "end": v(0.7, 0.32) * mm});
            skLineSegment(sketch, "E2353", {"start": v(0.7, 0.32) * mm, "end": v(0.7, 0.33) * mm});
            skLineSegment(sketch, "E2354", {"start": v(0.7, 0.33) * mm, "end": v(0.69, 0.33) * mm});
            skLineSegment(sketch, "E2355", {"start": v(0.69, 0.33) * mm, "end": v(0.69, 0.34) * mm});
            skLineSegment(sketch, "E2356", {"start": v(0.69, 0.34) * mm, "end": v(0.68, 0.35) * mm});
            skLineSegment(sketch, "E2357", {"start": v(0.68, 0.35) * mm, "end": v(0.68, 0.36) * mm});
            skLineSegment(sketch, "E2358", {"start": v(0.68, 0.36) * mm, "end": v(0.68, 0.37) * mm});
            skLineSegment(sketch, "E2359", {"start": v(0.68, 0.37) * mm, "end": v(0.68, 0.37) * mm});
            skLineSegment(sketch, "E2360", {"start": v(0.68, 0.37) * mm, "end": v(0.68, 0.38) * mm});
            skLineSegment(sketch, "E2361", {"start": v(0.68, 0.38) * mm, "end": v(0.68, 0.4) * mm});
            skLineSegment(sketch, "E2362", {"start": v(0.85, 0.42) * mm, "end": v(0.85, 0.44) * mm});
            skLineSegment(sketch, "E2363", {"start": v(0.85, 0.44) * mm, "end": v(0.85, 0.46) * mm});
            skLineSegment(sketch, "E2364", {"start": v(0, 0.46) * mm, "end": v(0, 0.45) * mm});
            skLineSegment(sketch, "E2365", {"start": v(0, 0.45) * mm, "end": v(-0.01, 0.44) * mm});
            skLineSegment(sketch, "E2366", {"start": v(-0.01, 0.44) * mm, "end": v(-0.01, 0.25) * mm});
            skLineSegment(sketch, "E2367", {"start": v(-0.01, 0.25) * mm, "end": v(0, 0.25) * mm});
            skLineSegment(sketch, "E2368", {"start": v(0, 0.25) * mm, "end": v(0, 0.23) * mm});
            skLineSegment(sketch, "E2369", {"start": v(0, 0.23) * mm, "end": v(0, 0.23) * mm});
            skLineSegment(sketch, "E2370", {"start": v(0, 0.23) * mm, "end": v(-0.01, 0.23) * mm});
            skLineSegment(sketch, "E2371", {"start": v(-0.01, 0.23) * mm, "end": v(-0.01, 0.23) * mm});
            skLineSegment(sketch, "E2372", {"start": v(-0.01, 0.23) * mm, "end": v(-0.01, 0.22) * mm});
            skLineSegment(sketch, "E2373", {"start": v(-0.01, 0.22) * mm, "end": v(-0.08, 0.22) * mm});
            skLineSegment(sketch, "E2374", {"start": v(-0.08, 0.22) * mm, "end": v(-0.09, 0.23) * mm});
            skLineSegment(sketch, "E2375", {"start": v(-0.09, 0.23) * mm, "end": v(-0.09, 0.23) * mm});
            skLineSegment(sketch, "E2376", {"start": v(-0.09, 0.23) * mm, "end": v(-0.1, 0.23) * mm});
            skLineSegment(sketch, "E2377", {"start": v(-0.1, 0.23) * mm, "end": v(-0.1, 0.23) * mm});
            skLineSegment(sketch, "E2378", {"start": v(-0.1, 0.23) * mm, "end": v(-0.1, 0.25) * mm});
            skLineSegment(sketch, "E2379", {"start": v(-0.1, 0.25) * mm, "end": v(-0.1, 0.25) * mm});
            skLineSegment(sketch, "E2380", {"start": v(-0.1, 0.25) * mm, "end": v(-0.1, 0.44) * mm});
            skLineSegment(sketch, "E2381", {"start": v(-0.1, 0.44) * mm, "end": v(-0.1, 0.45) * mm});
            skLineSegment(sketch, "E2382", {"start": v(-0.1, 0.45) * mm, "end": v(-0.1, 0.46) * mm});
            skLineSegment(sketch, "E2383", {"start": v(-0.1, 0.46) * mm, "end": v(-0.1, 0.45) * mm});
            skLineSegment(sketch, "E2384", {"start": v(-0.1, 0.45) * mm, "end": v(-0.1, 0.44) * mm});
            skLineSegment(sketch, "E2385", {"start": v(-0.1, 0.44) * mm, "end": v(-0.1, 0.25) * mm});
            skLineSegment(sketch, "E2386", {"start": v(-0.1, 0.25) * mm, "end": v(-0.1, 0.23) * mm});
            skLineSegment(sketch, "E2387", {"start": v(-0.1, 0.23) * mm, "end": v(-0.11, 0.23) * mm});
            skLineSegment(sketch, "E2388", {"start": v(-0.11, 0.23) * mm, "end": v(-0.11, 0.23) * mm});
            skLineSegment(sketch, "E2389", {"start": v(-0.11, 0.23) * mm, "end": v(-0.11, 0.22) * mm});
            skLineSegment(sketch, "E2390", {"start": v(-0.11, 0.22) * mm, "end": v(-0.19, 0.22) * mm});
            skLineSegment(sketch, "E2391", {"start": v(-0.19, 0.22) * mm, "end": v(-0.19, 0.23) * mm});
            skLineSegment(sketch, "E2392", {"start": v(-0.19, 0.23) * mm, "end": v(-0.19, 0.23) * mm});
            skLineSegment(sketch, "E2393", {"start": v(-0.19, 0.23) * mm, "end": v(-0.2, 0.23) * mm});
            skLineSegment(sketch, "E2394", {"start": v(-0.2, 0.23) * mm, "end": v(-0.2, 0.23) * mm});
            skLineSegment(sketch, "E2395", {"start": v(-0.2, 0.23) * mm, "end": v(-0.2, 0.25) * mm});
            skLineSegment(sketch, "E2396", {"start": v(-0.2, 0.25) * mm, "end": v(-0.19, 0.25) * mm});
            skLineSegment(sketch, "E2397", {"start": v(-0.19, 0.25) * mm, "end": v(-0.19, 0.44) * mm});
            skLineSegment(sketch, "E2398", {"start": v(-0.19, 0.44) * mm, "end": v(-0.2, 0.45) * mm});
            skLineSegment(sketch, "E2399", {"start": v(-0.2, 0.45) * mm, "end": v(-0.2, 0.46) * mm});
            skLineSegment(sketch, "E2400", {"start": v(-0.2, 0.46) * mm, "end": v(-0.2, 0.45) * mm});
            skLineSegment(sketch, "E2401", {"start": v(-0.2, 0.45) * mm, "end": v(-0.2, 0.44) * mm});
            skLineSegment(sketch, "E2402", {"start": v(-0.2, 0.44) * mm, "end": v(-0.2, 0.25) * mm});
            skLineSegment(sketch, "E2403", {"start": v(-0.2, 0.25) * mm, "end": v(-0.2, 0.25) * mm});
            skLineSegment(sketch, "E2404", {"start": v(-0.2, 0.25) * mm, "end": v(-0.2, 0.23) * mm});
            skLineSegment(sketch, "E2405", {"start": v(-0.2, 0.23) * mm, "end": v(-0.21, 0.23) * mm});
            skLineSegment(sketch, "E2406", {"start": v(-0.21, 0.23) * mm, "end": v(-0.21, 0.23) * mm});
            skLineSegment(sketch, "E2407", {"start": v(-0.21, 0.23) * mm, "end": v(-0.22, 0.22) * mm});
            skLineSegment(sketch, "E2408", {"start": v(-0.22, 0.22) * mm, "end": v(-0.28, 0.22) * mm});
            skLineSegment(sketch, "E2409", {"start": v(-0.28, 0.22) * mm, "end": v(-0.29, 0.23) * mm});
            skLineSegment(sketch, "E2410", {"start": v(-0.29, 0.23) * mm, "end": v(-0.29, 0.23) * mm});
            skLineSegment(sketch, "E2411", {"start": v(-0.29, 0.23) * mm, "end": v(-0.3, 0.23) * mm});
            skLineSegment(sketch, "E2412", {"start": v(-0.3, 0.23) * mm, "end": v(-0.3, 0.23) * mm});
            skLineSegment(sketch, "E2413", {"start": v(-0.3, 0.23) * mm, "end": v(-0.3, 0.25) * mm});
            skLineSegment(sketch, "E2414", {"start": v(-0.3, 0.25) * mm, "end": v(-0.3, 0.25) * mm});
            skLineSegment(sketch, "E2415", {"start": v(-0.3, 0.25) * mm, "end": v(-0.3, 0.44) * mm});
            skLineSegment(sketch, "E2416", {"start": v(-0.3, 0.44) * mm, "end": v(-0.3, 0.45) * mm});
            skLineSegment(sketch, "E2417", {"start": v(-0.3, 0.45) * mm, "end": v(-0.3, 0.46) * mm});
            skLineSegment(sketch, "E2418", {"start": v(-0.3, 0.46) * mm, "end": v(-0.3, 0.45) * mm});
            skLineSegment(sketch, "E2419", {"start": v(-0.3, 0.45) * mm, "end": v(-0.31, 0.44) * mm});
            skLineSegment(sketch, "E2420", {"start": v(-0.31, 0.44) * mm, "end": v(-0.31, 0.25) * mm});
            skLineSegment(sketch, "E2421", {"start": v(-0.31, 0.25) * mm, "end": v(-0.3, 0.25) * mm});
            skLineSegment(sketch, "E2422", {"start": v(-0.3, 0.25) * mm, "end": v(-0.3, 0.23) * mm});
            skLineSegment(sketch, "E2423", {"start": v(-0.3, 0.23) * mm, "end": v(-0.31, 0.23) * mm});
            skLineSegment(sketch, "E2424", {"start": v(-0.31, 0.23) * mm, "end": v(-0.31, 0.23) * mm});
            skLineSegment(sketch, "E2425", {"start": v(-0.31, 0.23) * mm, "end": v(-0.31, 0.22) * mm});
            skLineSegment(sketch, "E2426", {"start": v(-0.31, 0.22) * mm, "end": v(-0.39, 0.22) * mm});
            skLineSegment(sketch, "E2427", {"start": v(-0.39, 0.22) * mm, "end": v(-0.39, 0.23) * mm});
            skLineSegment(sketch, "E2428", {"start": v(-0.39, 0.23) * mm, "end": v(-0.39, 0.23) * mm});
            skLineSegment(sketch, "E2429", {"start": v(-0.39, 0.23) * mm, "end": v(-0.4, 0.23) * mm});
            skLineSegment(sketch, "E2430", {"start": v(-0.4, 0.23) * mm, "end": v(-0.4, 0.23) * mm});
            skLineSegment(sketch, "E2431", {"start": v(-0.4, 0.23) * mm, "end": v(-0.4, 0.25) * mm});
            skLineSegment(sketch, "E2432", {"start": v(-0.4, 0.25) * mm, "end": v(-0.39, 0.25) * mm});
            skLineSegment(sketch, "E2433", {"start": v(-0.39, 0.25) * mm, "end": v(-0.39, 0.44) * mm});
            skLineSegment(sketch, "E2434", {"start": v(-0.39, 0.44) * mm, "end": v(-0.4, 0.45) * mm});
            skLineSegment(sketch, "E2435", {"start": v(-0.4, 0.45) * mm, "end": v(-0.4, 0.46) * mm});
            skLineSegment(sketch, "E2436", {"start": v(-0.4, 0.46) * mm, "end": v(-0.4, 0.47) * mm});
            skLineSegment(sketch, "E2437", {"start": v(-0.4, 0.47) * mm, "end": v(-0.4, 0.47) * mm});
            skLineSegment(sketch, "E2438", {"start": v(-0.4, 0.47) * mm, "end": v(-0.39, 0.47) * mm});
            skLineSegment(sketch, "E2439", {"start": v(-0.39, 0.47) * mm, "end": v(-0.39, 0.47) * mm});
            skLineSegment(sketch, "E2440", {"start": v(-0.39, 0.47) * mm, "end": v(-0.31, 0.47) * mm});
            skLineSegment(sketch, "E2441", {"start": v(-0.31, 0.47) * mm, "end": v(-0.31, 0.47) * mm});
            skLineSegment(sketch, "E2442", {"start": v(-0.31, 0.47) * mm, "end": v(-0.3, 0.47) * mm});
            skLineSegment(sketch, "E2443", {"start": v(-0.3, 0.47) * mm, "end": v(-0.3, 0.47) * mm});
            skLineSegment(sketch, "E2444", {"start": v(-0.3, 0.47) * mm, "end": v(-0.3, 0.46) * mm});
            skLineSegment(sketch, "E2445", {"start": v(-0.3, 0.46) * mm, "end": v(-0.3, 0.47) * mm});
            skLineSegment(sketch, "E2446", {"start": v(-0.3, 0.47) * mm, "end": v(-0.29, 0.47) * mm});
            skLineSegment(sketch, "E2447", {"start": v(-0.29, 0.47) * mm, "end": v(-0.29, 0.47) * mm});
            skLineSegment(sketch, "E2448", {"start": v(-0.29, 0.47) * mm, "end": v(-0.28, 0.47) * mm});
            skLineSegment(sketch, "E2449", {"start": v(-0.28, 0.47) * mm, "end": v(-0.22, 0.47) * mm});
            skLineSegment(sketch, "E2450", {"start": v(-0.22, 0.47) * mm, "end": v(-0.21, 0.47) * mm});
            skLineSegment(sketch, "E2451", {"start": v(-0.21, 0.47) * mm, "end": v(-0.21, 0.47) * mm});
            skLineSegment(sketch, "E2452", {"start": v(-0.21, 0.47) * mm, "end": v(-0.2, 0.47) * mm});
            skLineSegment(sketch, "E2453", {"start": v(-0.2, 0.47) * mm, "end": v(-0.2, 0.47) * mm});
            skLineSegment(sketch, "E2454", {"start": v(-0.2, 0.47) * mm, "end": v(-0.2, 0.46) * mm});
            skLineSegment(sketch, "E2455", {"start": v(-0.2, 0.46) * mm, "end": v(-0.2, 0.47) * mm});
            skLineSegment(sketch, "E2456", {"start": v(-0.2, 0.47) * mm, "end": v(-0.19, 0.47) * mm});
            skLineSegment(sketch, "E2457", {"start": v(-0.19, 0.47) * mm, "end": v(-0.19, 0.47) * mm});
            skLineSegment(sketch, "E2458", {"start": v(-0.19, 0.47) * mm, "end": v(-0.11, 0.47) * mm});
            skLineSegment(sketch, "E2459", {"start": v(-0.11, 0.47) * mm, "end": v(-0.11, 0.47) * mm});
            skLineSegment(sketch, "E2460", {"start": v(-0.11, 0.47) * mm, "end": v(-0.1, 0.47) * mm});
            skLineSegment(sketch, "E2461", {"start": v(-0.1, 0.47) * mm, "end": v(-0.1, 0.47) * mm});
            skLineSegment(sketch, "E2462", {"start": v(-0.1, 0.47) * mm, "end": v(-0.1, 0.46) * mm});
            skLineSegment(sketch, "E2463", {"start": v(-0.1, 0.46) * mm, "end": v(-0.1, 0.47) * mm});
            skLineSegment(sketch, "E2464", {"start": v(-0.1, 0.47) * mm, "end": v(-0.09, 0.47) * mm});
            skLineSegment(sketch, "E2465", {"start": v(-0.09, 0.47) * mm, "end": v(-0.09, 0.47) * mm});
            skLineSegment(sketch, "E2466", {"start": v(-0.09, 0.47) * mm, "end": v(-0.08, 0.47) * mm});
            skLineSegment(sketch, "E2467", {"start": v(-0.08, 0.47) * mm, "end": v(-0.01, 0.47) * mm});
            skLineSegment(sketch, "E2468", {"start": v(-0.01, 0.47) * mm, "end": v(-0.01, 0.47) * mm});
            skLineSegment(sketch, "E2469", {"start": v(-0.01, 0.47) * mm, "end": v(0, 0.47) * mm});
            skLineSegment(sketch, "E2470", {"start": v(0, 0.47) * mm, "end": v(0, 0.47) * mm});
            skLineSegment(sketch, "E2471", {"start": v(0, 0.47) * mm, "end": v(0, 0.46) * mm});
            skLineSegment(sketch, "E2472", {"start": v(-1.3, 0.27) * mm, "end": v(-1.3, 0.24) * mm});
            skLineSegment(sketch, "E2473", {"start": v(-1.3, 0.24) * mm, "end": v(-1.34, 0.24) * mm});
            skLineSegment(sketch, "E2474", {"start": v(-1.34, 0.24) * mm, "end": v(-1.34, 0.27) * mm});
            skLineSegment(sketch, "E2475", {"start": v(-1.34, 0.27) * mm, "end": v(-1.33, 0.27) * mm});
            skLineSegment(sketch, "E2476", {"start": v(-1.33, 0.27) * mm, "end": v(-1.32, 0.27) * mm});
            skLineSegment(sketch, "E2477", {"start": v(-1.32, 0.27) * mm, "end": v(-1.31, 0.27) * mm});
            skLineSegment(sketch, "E2478", {"start": v(-1.31, 0.27) * mm, "end": v(-1.31, 0.24) * mm});
            skLineSegment(sketch, "E2479", {"start": v(-1.31, 0.27) * mm, "end": v(-1.3, 0.27) * mm});
            skLineSegment(sketch, "E2480", {"start": v(-1.3, 0.27) * mm, "end": v(-1.3, 0.27) * mm});
            skLineSegment(sketch, "E2481", {"start": v(0.84, -1.36) * mm, "end": v(0.84, -1.38) * mm});
            skLineSegment(sketch, "E2482", {"start": v(0.84, -1.38) * mm, "end": v(0.85, -1.39) * mm});
            skLineSegment(sketch, "E2483", {"start": v(0.85, -1.39) * mm, "end": v(0.87, -1.39) * mm});
            skLineSegment(sketch, "E2484", {"start": v(0.87, -1.36) * mm, "end": v(0.85, -1.36) * mm});
            skLineSegment(sketch, "E2485", {"start": v(0.85, -1.36) * mm, "end": v(0.84, -1.36) * mm});
            skLineSegment(sketch, "E2486", {"start": v(1.33, 1.2) * mm, "end": v(1.36, 1.2) * mm});
            skLineSegment(sketch, "E2487", {"start": v(1.28, 1.3) * mm, "end": v(1.28, 1.3) * mm});
            skLineSegment(sketch, "E2488", {"start": v(1.28, 1.3) * mm, "end": v(1.28, 1.31) * mm});
            skLineSegment(sketch, "E2489", {"start": v(1.28, 1.31) * mm, "end": v(1.28, 1.32) * mm});
            skLineSegment(sketch, "E2490", {"start": v(1.28, 1.32) * mm, "end": v(1.26, 1.32) * mm});
            skLineSegment(sketch, "E2491", {"start": v(1.26, 1.32) * mm, "end": v(1.26, 1.3) * mm});
            skLineSegment(sketch, "E2492", {"start": v(1.26, 1.3) * mm, "end": v(1.26, 1.3) * mm});
            skLineSegment(sketch, "E2493", {"start": v(1.26, 1.3) * mm, "end": v(1.28, 1.3) * mm});
            skLineSegment(sketch, "E2494", {"start": v(1.26, 1.32) * mm, "end": v(1.27, 1.33) * mm});
            skLineSegment(sketch, "E2495", {"start": v(1.27, 1.33) * mm, "end": v(1.28, 1.34) * mm});
            skLineSegment(sketch, "E2496", {"start": v(1.25, 1.33) * mm, "end": v(1.24, 1.34) * mm});
            skLineSegment(sketch, "E2497", {"start": v(1.24, 1.34) * mm, "end": v(1.23, 1.34) * mm});
            skLineSegment(sketch, "E2498", {"start": v(1.23, 1.34) * mm, "end": v(1.22, 1.33) * mm});
            skLineSegment(sketch, "E2499", {"start": v(1.22, 1.33) * mm, "end": v(1.22, 1.3) * mm});
            skLineSegment(sketch, "E2500", {"start": v(1.22, 1.3) * mm, "end": v(1.23, 1.3) * mm});
            skLineSegment(sketch, "E2501", {"start": v(1.23, 1.3) * mm, "end": v(1.24, 1.3) * mm});
            skLineSegment(sketch, "E2502", {"start": v(1.24, 1.3) * mm, "end": v(1.25, 1.3) * mm});
            skLineSegment(sketch, "E2503", {"start": v(1.08, 1.3) * mm, "end": v(1.08, 1.3) * mm});
            skLineSegment(sketch, "E2504", {"start": v(1.08, 1.3) * mm, "end": v(1.06, 1.3) * mm});
            skLineSegment(sketch, "E2505", {"start": v(1.06, 1.3) * mm, "end": v(1.06, 1.3) * mm});
            skLineSegment(sketch, "E2506", {"start": v(1.06, 1.32) * mm, "end": v(1.07, 1.33) * mm});
            skLineSegment(sketch, "E2507", {"start": v(1.07, 1.33) * mm, "end": v(1.08, 1.33) * mm});
            skLineSegment(sketch, "E2508", {"start": v(1.08, 1.33) * mm, "end": v(1.08, 1.32) * mm});
            skLineSegment(sketch, "E2509", {"start": v(1.08, 1.32) * mm, "end": v(1.08, 1.3) * mm});
            skLineSegment(sketch, "E2510", {"start": v(1.06, 1.32) * mm, "end": v(1.06, 1.34) * mm});
            skLineSegment(sketch, "E2511", {"start": v(1.06, 1.34) * mm, "end": v(1.08, 1.34) * mm});
            skLineSegment(sketch, "E2512", {"start": v(1.05, 1.33) * mm, "end": v(1.04, 1.34) * mm});
            skLineSegment(sketch, "E2513", {"start": v(1.04, 1.34) * mm, "end": v(1.03, 1.34) * mm});
            skLineSegment(sketch, "E2514", {"start": v(1.03, 1.34) * mm, "end": v(1.02, 1.33) * mm});
            skLineSegment(sketch, "E2515", {"start": v(1.02, 1.33) * mm, "end": v(1.02, 1.3) * mm});
            skLineSegment(sketch, "E2516", {"start": v(1.02, 1.3) * mm, "end": v(1.03, 1.3) * mm});
            skLineSegment(sketch, "E2517", {"start": v(1.03, 1.3) * mm, "end": v(1.04, 1.3) * mm});
            skLineSegment(sketch, "E2518", {"start": v(1.04, 1.3) * mm, "end": v(1.05, 1.3) * mm});
            skLineSegment(sketch, "E2519", {"start": v(0.88, 1.32) * mm, "end": v(0.86, 1.32) * mm});
            skLineSegment(sketch, "E2520", {"start": v(0.86, 1.32) * mm, "end": v(0.88, 1.34) * mm});
            skLineSegment(sketch, "E2521", {"start": v(0.88, 1.34) * mm, "end": v(0.88, 1.3) * mm});
            skLineSegment(sketch, "E2522", {"start": v(0.85, 1.3) * mm, "end": v(0.84, 1.3) * mm});
            skLineSegment(sketch, "E2523", {"start": v(0.84, 1.3) * mm, "end": v(0.83, 1.3) * mm});
            skLineSegment(sketch, "E2524", {"start": v(0.83, 1.3) * mm, "end": v(0.82, 1.3) * mm});
            skLineSegment(sketch, "E2525", {"start": v(0.82, 1.3) * mm, "end": v(0.82, 1.33) * mm});
            skLineSegment(sketch, "E2526", {"start": v(0.82, 1.33) * mm, "end": v(0.83, 1.34) * mm});
            skLineSegment(sketch, "E2527", {"start": v(0.83, 1.34) * mm, "end": v(0.84, 1.34) * mm});
            skLineSegment(sketch, "E2528", {"start": v(0.84, 1.34) * mm, "end": v(0.85, 1.33) * mm});
            skLineSegment(sketch, "E2529", {"start": v(0.68, 1.33) * mm, "end": v(0.68, 1.33) * mm});
            skLineSegment(sketch, "E2530", {"start": v(0.68, 1.33) * mm, "end": v(0.68, 1.32) * mm});
            skLineSegment(sketch, "E2531", {"start": v(0.68, 1.32) * mm, "end": v(0.68, 1.31) * mm});
            skLineSegment(sketch, "E2532", {"start": v(0.68, 1.31) * mm, "end": v(0.68, 1.3) * mm});
            skLineSegment(sketch, "E2533", {"start": v(0.68, 1.3) * mm, "end": v(0.68, 1.3) * mm});
            skLineSegment(sketch, "E2534", {"start": v(0.68, 1.3) * mm, "end": v(0.66, 1.3) * mm});
            skLineSegment(sketch, "E2535", {"start": v(0.66, 1.3) * mm, "end": v(0.66, 1.3) * mm});
            skLineSegment(sketch, "E2536", {"start": v(0.65, 1.3) * mm, "end": v(0.64, 1.3) * mm});
            skLineSegment(sketch, "E2537", {"start": v(0.64, 1.3) * mm, "end": v(0.63, 1.3) * mm});
            skLineSegment(sketch, "E2538", {"start": v(0.63, 1.3) * mm, "end": v(0.62, 1.3) * mm});
            skLineSegment(sketch, "E2539", {"start": v(0.62, 1.3) * mm, "end": v(0.62, 1.33) * mm});
            skLineSegment(sketch, "E2540", {"start": v(0.62, 1.33) * mm, "end": v(0.63, 1.34) * mm});
            skLineSegment(sketch, "E2541", {"start": v(0.63, 1.34) * mm, "end": v(0.64, 1.34) * mm});
            skLineSegment(sketch, "E2542", {"start": v(0.64, 1.34) * mm, "end": v(0.65, 1.33) * mm});
            skLineSegment(sketch, "E2543", {"start": v(0.66, 1.33) * mm, "end": v(0.66, 1.34) * mm});
            skLineSegment(sketch, "E2544", {"start": v(0.66, 1.34) * mm, "end": v(0.68, 1.34) * mm});
            skLineSegment(sketch, "E2545", {"start": v(0.68, 1.34) * mm, "end": v(0.68, 1.33) * mm});
            skLineSegment(sketch, "E2546", {"start": v(0.68, 1.32) * mm, "end": v(0.67, 1.32) * mm});
            skLineSegment(sketch, "E2547", {"start": v(0.56, 0.95) * mm, "end": v(0.56, 0.92) * mm});
            skLineSegment(sketch, "E2548", {"start": v(0.56, 0.94) * mm, "end": v(0.52, 0.94) * mm});
            skLineSegment(sketch, "E2549", {"start": v(0.52, 0.94) * mm, "end": v(0.53, 0.92) * mm});
            skLineSegment(sketch, "E2550", {"start": v(0.53, 0.91) * mm, "end": v(0.52, 0.9) * mm});
            skLineSegment(sketch, "E2551", {"start": v(0.52, 0.9) * mm, "end": v(0.52, 0.9) * mm});
            skLineSegment(sketch, "E2552", {"start": v(0.52, 0.9) * mm, "end": v(0.53, 0.89) * mm});
            skLineSegment(sketch, "E2553", {"start": v(0.53, 0.89) * mm, "end": v(0.55, 0.89) * mm});
            skLineSegment(sketch, "E2554", {"start": v(0.55, 0.89) * mm, "end": v(0.56, 0.9) * mm});
            skLineSegment(sketch, "E2555", {"start": v(0.56, 0.9) * mm, "end": v(0.56, 0.9) * mm});
            skLineSegment(sketch, "E2556", {"start": v(0.56, 0.9) * mm, "end": v(0.55, 0.91) * mm});
            skLineSegment(sketch, "E2557", {"start": v(0.56, 0.87) * mm, "end": v(0.56, 0.86) * mm});
            skLineSegment(sketch, "E2558", {"start": v(0.56, 0.87) * mm, "end": v(0.52, 0.87) * mm});
            skLineSegment(sketch, "E2559", {"start": v(0.52, 0.86) * mm, "end": v(0.52, 0.87) * mm});
            skLineSegment(sketch, "E2560", {"start": v(0.66, 0.57) * mm, "end": v(0.7, 0.57) * mm});
            skLineSegment(sketch, "E2561", {"start": v(0.7, 0.56) * mm, "end": v(0.7, 0.58) * mm});
            skLineSegment(sketch, "E2562", {"start": v(0.67, 0.56) * mm, "end": v(0.66, 0.57) * mm});
            skLineSegment(sketch, "E2563", {"start": v(0.67, 0.55) * mm, "end": v(0.66, 0.54) * mm});
            skLineSegment(sketch, "E2564", {"start": v(0.66, 0.54) * mm, "end": v(0.66, 0.53) * mm});
            skLineSegment(sketch, "E2565", {"start": v(0.66, 0.53) * mm, "end": v(0.67, 0.52) * mm});
            skLineSegment(sketch, "E2566", {"start": v(0.67, 0.52) * mm, "end": v(0.7, 0.52) * mm});
            skLineSegment(sketch, "E2567", {"start": v(0.7, 0.52) * mm, "end": v(0.7, 0.53) * mm});
            skLineSegment(sketch, "E2568", {"start": v(0.7, 0.53) * mm, "end": v(0.7, 0.54) * mm});
            skLineSegment(sketch, "E2569", {"start": v(0.7, 0.54) * mm, "end": v(0.7, 0.55) * mm});
            skLineSegment(sketch, "E2570", {"start": v(0.39, 0.4) * mm, "end": v(0.39, 0.37) * mm});
            skLineSegment(sketch, "E2571", {"start": v(0.39, 0.37) * mm, "end": v(0.36, 0.4) * mm});
            skLineSegment(sketch, "E2572", {"start": v(0.36, 0.4) * mm, "end": v(0.36, 0.4) * mm});
            skLineSegment(sketch, "E2573", {"start": v(0.36, 0.4) * mm, "end": v(0.35, 0.39) * mm});
            skLineSegment(sketch, "E2574", {"start": v(0.35, 0.39) * mm, "end": v(0.35, 0.37) * mm});
            skLineSegment(sketch, "E2575", {"start": v(0.35, 0.37) * mm, "end": v(0.36, 0.37) * mm});
            skLineSegment(sketch, "E2576", {"start": v(0.36, 0.36) * mm, "end": v(0.35, 0.35) * mm});
            skLineSegment(sketch, "E2577", {"start": v(0.35, 0.35) * mm, "end": v(0.35, 0.34) * mm});
            skLineSegment(sketch, "E2578", {"start": v(0.35, 0.34) * mm, "end": v(0.36, 0.33) * mm});
            skLineSegment(sketch, "E2579", {"start": v(0.36, 0.33) * mm, "end": v(0.38, 0.33) * mm});
            skLineSegment(sketch, "E2580", {"start": v(0.38, 0.33) * mm, "end": v(0.39, 0.34) * mm});
            skLineSegment(sketch, "E2581", {"start": v(0.39, 0.34) * mm, "end": v(0.39, 0.35) * mm});
            skLineSegment(sketch, "E2582", {"start": v(0.39, 0.35) * mm, "end": v(0.38, 0.36) * mm});
            skLineSegment(sketch, "E2583", {"start": v(0.27, 0.36) * mm, "end": v(0.23, 0.36) * mm});
            skLineSegment(sketch, "E2584", {"start": v(0.23, 0.36) * mm, "end": v(0.24, 0.35) * mm});
            skLineSegment(sketch, "E2585", {"start": v(0.25, 0.34) * mm, "end": v(0.26, 0.33) * mm});
            skLineSegment(sketch, "E2586", {"start": v(0.26, 0.33) * mm, "end": v(0.26, 0.31) * mm});
            skLineSegment(sketch, "E2587", {"start": v(0.27, 0.31) * mm, "end": v(0.23, 0.31) * mm});
            skLineSegment(sketch, "E2588", {"start": v(0.23, 0.31) * mm, "end": v(0.23, 0.33) * mm});
            skLineSegment(sketch, "E2589", {"start": v(0.23, 0.33) * mm, "end": v(0.24, 0.34) * mm});
            skLineSegment(sketch, "E2590", {"start": v(0.24, 0.34) * mm, "end": v(0.25, 0.34) * mm});
            skLineSegment(sketch, "E2591", {"start": v(0.26, 0.32) * mm, "end": v(0.27, 0.34) * mm});
            skLineSegment(sketch, "E2592", {"start": v(0.27, 0.35) * mm, "end": v(0.27, 0.37) * mm});
            skLineSegment(sketch, "E2593", {"start": v(0.27, 0.39) * mm, "end": v(0.24, 0.4) * mm});
            skLineSegment(sketch, "E2594", {"start": v(0.24, 0.4) * mm, "end": v(0.24, 0.4) * mm});
            skLineSegment(sketch, "E2595", {"start": v(0.24, 0.4) * mm, "end": v(0.23, 0.4) * mm});
            skLineSegment(sketch, "E2596", {"start": v(0.23, 0.4) * mm, "end": v(0.23, 0.4) * mm});
            skLineSegment(sketch, "E2597", {"start": v(0.23, 0.4) * mm, "end": v(0.24, 0.39) * mm});
            skLineSegment(sketch, "E2598", {"start": v(0.27, 0.39) * mm, "end": v(0.27, 0.4) * mm});
            skLineSegment(sketch, "E2599", {"start": v(0.17, 0.4) * mm, "end": v(0.17, 0.39) * mm});
            skLineSegment(sketch, "E2600", {"start": v(0.17, 0.4) * mm, "end": v(0.13, 0.4) * mm});
            skLineSegment(sketch, "E2601", {"start": v(0.13, 0.4) * mm, "end": v(0.14, 0.39) * mm});
            skLineSegment(sketch, "E2602", {"start": v(0.17, 0.37) * mm, "end": v(0.17, 0.35) * mm});
            skLineSegment(sketch, "E2603", {"start": v(0.17, 0.36) * mm, "end": v(0.13, 0.36) * mm});
            skLineSegment(sketch, "E2604", {"start": v(0.13, 0.36) * mm, "end": v(0.14, 0.35) * mm});
            skLineSegment(sketch, "E2605", {"start": v(0.15, 0.34) * mm, "end": v(0.16, 0.33) * mm});
            skLineSegment(sketch, "E2606", {"start": v(0.16, 0.33) * mm, "end": v(0.16, 0.31) * mm});
            skLineSegment(sketch, "E2607", {"start": v(0.17, 0.31) * mm, "end": v(0.13, 0.31) * mm});
            skLineSegment(sketch, "E2608", {"start": v(0.13, 0.31) * mm, "end": v(0.13, 0.33) * mm});
            skLineSegment(sketch, "E2609", {"start": v(0.13, 0.33) * mm, "end": v(0.14, 0.34) * mm});
            skLineSegment(sketch, "E2610", {"start": v(0.14, 0.34) * mm, "end": v(0.15, 0.34) * mm});
            skLineSegment(sketch, "E2611", {"start": v(0.16, 0.32) * mm, "end": v(0.17, 0.34) * mm});
            skLineSegment(sketch, "E2612", {"start": v(-0.03, 0.34) * mm, "end": v(-0.04, 0.32) * mm});
            skLineSegment(sketch, "E2613", {"start": v(-0.04, 0.33) * mm, "end": v(-0.04, 0.31) * mm});
            skLineSegment(sketch, "E2614", {"start": v(-0.03, 0.31) * mm, "end": v(-0.07, 0.31) * mm});
            skLineSegment(sketch, "E2615", {"start": v(-0.07, 0.31) * mm, "end": v(-0.07, 0.33) * mm});
            skLineSegment(sketch, "E2616", {"start": v(-0.07, 0.33) * mm, "end": v(-0.06, 0.34) * mm});
            skLineSegment(sketch, "E2617", {"start": v(-0.06, 0.34) * mm, "end": v(-0.05, 0.34) * mm});
            skLineSegment(sketch, "E2618", {"start": v(-0.05, 0.34) * mm, "end": v(-0.04, 0.33) * mm});
            skLineSegment(sketch, "E2619", {"start": v(-0.03, 0.35) * mm, "end": v(-0.03, 0.37) * mm});
            skLineSegment(sketch, "E2620", {"start": v(-0.03, 0.36) * mm, "end": v(-0.07, 0.36) * mm});
            skLineSegment(sketch, "E2621", {"start": v(-0.07, 0.36) * mm, "end": v(-0.06, 0.35) * mm});
            skLineSegment(sketch, "E2622", {"start": v(-0.06, 0.39) * mm, "end": v(-0.07, 0.4) * mm});
            skLineSegment(sketch, "E2623", {"start": v(-0.07, 0.4) * mm, "end": v(-0.07, 0.4) * mm});
            skLineSegment(sketch, "E2624", {"start": v(-0.07, 0.4) * mm, "end": v(-0.06, 0.4) * mm});
            skLineSegment(sketch, "E2625", {"start": v(-0.06, 0.4) * mm, "end": v(-0.04, 0.39) * mm});
            skLineSegment(sketch, "E2626", {"start": v(-0.04, 0.39) * mm, "end": v(-0.03, 0.4) * mm});
            skLineSegment(sketch, "E2627", {"start": v(-0.03, 0.4) * mm, "end": v(-0.03, 0.4) * mm});
            skLineSegment(sketch, "E2628", {"start": v(-0.03, 0.4) * mm, "end": v(-0.04, 0.4) * mm});
            skLineSegment(sketch, "E2629", {"start": v(-0.04, 0.4) * mm, "end": v(-0.06, 0.4) * mm});
            skLineSegment(sketch, "E2630", {"start": v(-0.06, 0.39) * mm, "end": v(-0.04, 0.39) * mm});
            skLineSegment(sketch, "E2631", {"start": v(-0.13, 0.37) * mm, "end": v(-0.13, 0.35) * mm});
            skLineSegment(sketch, "E2632", {"start": v(-0.13, 0.35) * mm, "end": v(-0.14, 0.35) * mm});
            skLineSegment(sketch, "E2633", {"start": v(-0.15, 0.35) * mm, "end": v(-0.15, 0.37) * mm});
            skLineSegment(sketch, "E2634", {"start": v(-0.14, 0.37) * mm, "end": v(-0.16, 0.37) * mm});
            skLineSegment(sketch, "E2635", {"start": v(-0.16, 0.37) * mm, "end": v(-0.17, 0.37) * mm});
            skLineSegment(sketch, "E2636", {"start": v(-0.17, 0.37) * mm, "end": v(-0.17, 0.35) * mm});
            skLineSegment(sketch, "E2637", {"start": v(-0.17, 0.35) * mm, "end": v(-0.16, 0.35) * mm});
            skLineSegment(sketch, "E2638", {"start": v(-0.16, 0.35) * mm, "end": v(-0.16, 0.35) * mm});
            skLineSegment(sketch, "E2639", {"start": v(-0.16, 0.35) * mm, "end": v(-0.15, 0.35) * mm});
            skLineSegment(sketch, "E2640", {"start": v(-0.15, 0.34) * mm, "end": v(-0.14, 0.33) * mm});
            skLineSegment(sketch, "E2641", {"start": v(-0.14, 0.33) * mm, "end": v(-0.14, 0.31) * mm});
            skLineSegment(sketch, "E2642", {"start": v(-0.13, 0.31) * mm, "end": v(-0.17, 0.31) * mm});
            skLineSegment(sketch, "E2643", {"start": v(-0.17, 0.31) * mm, "end": v(-0.17, 0.33) * mm});
            skLineSegment(sketch, "E2644", {"start": v(-0.17, 0.33) * mm, "end": v(-0.16, 0.34) * mm});
            skLineSegment(sketch, "E2645", {"start": v(-0.16, 0.34) * mm, "end": v(-0.15, 0.34) * mm});
            skLineSegment(sketch, "E2646", {"start": v(-0.14, 0.32) * mm, "end": v(-0.13, 0.34) * mm});
            skLineSegment(sketch, "E2647", {"start": v(-0.13, 0.37) * mm, "end": v(-0.14, 0.37) * mm});
            skLineSegment(sketch, "E2648", {"start": v(-0.23, 0.37) * mm, "end": v(-0.23, 0.35) * mm});
            skLineSegment(sketch, "E2649", {"start": v(-0.23, 0.35) * mm, "end": v(-0.24, 0.35) * mm});
            skLineSegment(sketch, "E2650", {"start": v(-0.24, 0.35) * mm, "end": v(-0.24, 0.35) * mm});
            skLineSegment(sketch, "E2651", {"start": v(-0.24, 0.35) * mm, "end": v(-0.25, 0.35) * mm});
            skLineSegment(sketch, "E2652", {"start": v(-0.25, 0.35) * mm, "end": v(-0.25, 0.37) * mm});
            skLineSegment(sketch, "E2653", {"start": v(-0.25, 0.37) * mm, "end": v(-0.24, 0.37) * mm});
            skLineSegment(sketch, "E2654", {"start": v(-0.24, 0.37) * mm, "end": v(-0.24, 0.37) * mm});
            skLineSegment(sketch, "E2655", {"start": v(-0.24, 0.37) * mm, "end": v(-0.23, 0.37) * mm});
            skLineSegment(sketch, "E2656", {"start": v(-0.25, 0.37) * mm, "end": v(-0.26, 0.37) * mm});
            skLineSegment(sketch, "E2657", {"start": v(-0.26, 0.37) * mm, "end": v(-0.26, 0.37) * mm});
            skLineSegment(sketch, "E2658", {"start": v(-0.26, 0.37) * mm, "end": v(-0.27, 0.37) * mm});
            skLineSegment(sketch, "E2659", {"start": v(-0.27, 0.37) * mm, "end": v(-0.27, 0.35) * mm});
            skLineSegment(sketch, "E2660", {"start": v(-0.27, 0.35) * mm, "end": v(-0.26, 0.35) * mm});
            skLineSegment(sketch, "E2661", {"start": v(-0.26, 0.35) * mm, "end": v(-0.26, 0.35) * mm});
            skLineSegment(sketch, "E2662", {"start": v(-0.26, 0.35) * mm, "end": v(-0.25, 0.35) * mm});
            skLineSegment(sketch, "E2663", {"start": v(-0.25, 0.34) * mm, "end": v(-0.24, 0.33) * mm});
            skLineSegment(sketch, "E2664", {"start": v(-0.24, 0.33) * mm, "end": v(-0.24, 0.31) * mm});
            skLineSegment(sketch, "E2665", {"start": v(-0.23, 0.31) * mm, "end": v(-0.27, 0.31) * mm});
            skLineSegment(sketch, "E2666", {"start": v(-0.27, 0.31) * mm, "end": v(-0.27, 0.33) * mm});
            skLineSegment(sketch, "E2667", {"start": v(-0.27, 0.33) * mm, "end": v(-0.26, 0.34) * mm});
            skLineSegment(sketch, "E2668", {"start": v(-0.26, 0.34) * mm, "end": v(-0.25, 0.34) * mm});
            skLineSegment(sketch, "E2669", {"start": v(-0.24, 0.32) * mm, "end": v(-0.23, 0.34) * mm});
            skLineSegment(sketch, "E2670", {"start": v(-0.33, 0.34) * mm, "end": v(-0.34, 0.32) * mm});
            skLineSegment(sketch, "E2671", {"start": v(-0.34, 0.33) * mm, "end": v(-0.34, 0.31) * mm});
            skLineSegment(sketch, "E2672", {"start": v(-0.33, 0.31) * mm, "end": v(-0.37, 0.31) * mm});
            skLineSegment(sketch, "E2673", {"start": v(-0.37, 0.31) * mm, "end": v(-0.37, 0.33) * mm});
            skLineSegment(sketch, "E2674", {"start": v(-0.37, 0.33) * mm, "end": v(-0.36, 0.34) * mm});
            skLineSegment(sketch, "E2675", {"start": v(-0.36, 0.34) * mm, "end": v(-0.35, 0.34) * mm});
            skLineSegment(sketch, "E2676", {"start": v(-0.35, 0.34) * mm, "end": v(-0.34, 0.33) * mm});
            skLineSegment(sketch, "E2677", {"start": v(-0.34, 0.35) * mm, "end": v(-0.33, 0.35) * mm});
            skLineSegment(sketch, "E2678", {"start": v(-0.34, 0.35) * mm, "end": v(-0.36, 0.37) * mm});
            skLineSegment(sketch, "E2679", {"start": v(-0.36, 0.37) * mm, "end": v(-0.37, 0.37) * mm});
            skLineSegment(sketch, "E2680", {"start": v(-0.37, 0.37) * mm, "end": v(-0.37, 0.35) * mm});
            skLineSegment(sketch, "E2681", {"start": v(-0.45, 0.35) * mm, "end": v(-0.45, 0.33) * mm});
            skLineSegment(sketch, "E2682", {"start": v(-0.45, 0.34) * mm, "end": v(-0.49, 0.34) * mm});
            skLineSegment(sketch, "E2683", {"start": v(-0.49, 0.34) * mm, "end": v(-0.48, 0.33) * mm});
            skLineSegment(sketch, "E2684", {"start": v(-0.49, 0.31) * mm, "end": v(-0.46, 0.29) * mm});
            skLineSegment(sketch, "E2685", {"start": v(-0.47, 0.3) * mm, "end": v(-0.45, 0.31) * mm});
            skLineSegment(sketch, "E2686", {"start": v(-0.45, 0.29) * mm, "end": v(-0.49, 0.29) * mm});
            skLineSegment(sketch, "E2687", {"start": v(-0.48, 0.28) * mm, "end": v(-0.49, 0.27) * mm});
            skLineSegment(sketch, "E2688", {"start": v(-0.49, 0.27) * mm, "end": v(-0.49, 0.26) * mm});
            skLineSegment(sketch, "E2689", {"start": v(-0.49, 0.26) * mm, "end": v(-0.48, 0.25) * mm});
            skLineSegment(sketch, "E2690", {"start": v(-0.48, 0.25) * mm, "end": v(-0.46, 0.25) * mm});
            skLineSegment(sketch, "E2691", {"start": v(-0.46, 0.25) * mm, "end": v(-0.45, 0.26) * mm});
            skLineSegment(sketch, "E2692", {"start": v(-0.45, 0.26) * mm, "end": v(-0.45, 0.27) * mm});
            skLineSegment(sketch, "E2693", {"start": v(-0.45, 0.27) * mm, "end": v(-0.46, 0.28) * mm});
            skLineSegment(sketch, "E2694", {"start": v(-0.46, 0.28) * mm, "end": v(-0.48, 0.28) * mm});
            skLineSegment(sketch, "E2695", {"start": v(-0.33, -0.09) * mm, "end": v(-0.34, -0.1) * mm});
            skLineSegment(sketch, "E2696", {"start": v(-0.34, -0.1) * mm, "end": v(-0.34, -0.1) * mm});
            skLineSegment(sketch, "E2697", {"start": v(-0.34, -0.1) * mm, "end": v(-0.33, -0.11) * mm});
            skLineSegment(sketch, "E2698", {"start": v(-0.33, -0.12) * mm, "end": v(-0.3, -0.12) * mm});
            skLineSegment(sketch, "E2699", {"start": v(-0.3, -0.12) * mm, "end": v(-0.3, -0.13) * mm});
            skLineSegment(sketch, "E2700", {"start": v(-0.3, -0.13) * mm, "end": v(-0.3, -0.14) * mm});
            skLineSegment(sketch, "E2701", {"start": v(-0.3, -0.14) * mm, "end": v(-0.3, -0.15) * mm});
            skLineSegment(sketch, "E2702", {"start": v(-0.3, -0.15) * mm, "end": v(-0.33, -0.15) * mm});
            skLineSegment(sketch, "E2703", {"start": v(-0.33, -0.15) * mm, "end": v(-0.34, -0.14) * mm});
            skLineSegment(sketch, "E2704", {"start": v(-0.34, -0.14) * mm, "end": v(-0.34, -0.13) * mm});
            skLineSegment(sketch, "E2705", {"start": v(-0.34, -0.13) * mm, "end": v(-0.33, -0.12) * mm});
            skLineSegment(sketch, "E2706", {"start": v(-0.31, -0.14) * mm, "end": v(-0.3, -0.12) * mm});
            skLineSegment(sketch, "E2707", {"start": v(-0.3, -0.11) * mm, "end": v(-0.33, -0.09) * mm});
            skLineSegment(sketch, "E2708", {"start": v(-0.33, -0.09) * mm, "end": v(-0.33, -0.09) * mm});
            skLineSegment(sketch, "E2709", {"start": v(-0.3, -0.09) * mm, "end": v(-0.3, -0.11) * mm});
            skLineSegment(sketch, "E2710", {"start": v(-0.04, -0.1) * mm, "end": v(-0.04, -0.1) * mm});
            skLineSegment(sketch, "E2711", {"start": v(-0.04, -0.1) * mm, "end": v(-0.03, -0.09) * mm});
            skLineSegment(sketch, "E2712", {"start": v(-0.03, -0.09) * mm, "end": v(-0.03, -0.09) * mm});
            skLineSegment(sketch, "E2713", {"start": v(-0.03, -0.09) * mm, "end": v(-0.02, -0.1) * mm});
            skLineSegment(sketch, "E2714", {"start": v(-0.02, -0.1) * mm, "end": v(-0.01, -0.09) * mm});
            skLineSegment(sketch, "E2715", {"start": v(-0.01, -0.09) * mm, "end": v(0, -0.09) * mm});
            skLineSegment(sketch, "E2716", {"start": v(0, -0.09) * mm, "end": v(0, -0.1) * mm});
            skLineSegment(sketch, "E2717", {"start": v(0, -0.1) * mm, "end": v(0, -0.1) * mm});
            skLineSegment(sketch, "E2718", {"start": v(0, -0.1) * mm, "end": v(0, -0.11) * mm});
            skLineSegment(sketch, "E2719", {"start": v(0, -0.12) * mm, "end": v(0, -0.13) * mm});
            skLineSegment(sketch, "E2720", {"start": v(0, -0.13) * mm, "end": v(0, -0.14) * mm});
            skLineSegment(sketch, "E2721", {"start": v(0, -0.14) * mm, "end": v(0, -0.15) * mm});
            skLineSegment(sketch, "E2722", {"start": v(0, -0.15) * mm, "end": v(-0.03, -0.15) * mm});
            skLineSegment(sketch, "E2723", {"start": v(-0.03, -0.15) * mm, "end": v(-0.04, -0.14) * mm});
            skLineSegment(sketch, "E2724", {"start": v(-0.04, -0.14) * mm, "end": v(-0.04, -0.13) * mm});
            skLineSegment(sketch, "E2725", {"start": v(-0.04, -0.13) * mm, "end": v(-0.03, -0.12) * mm});
            skLineSegment(sketch, "E2726", {"start": v(-0.03, -0.12) * mm, "end": v(0, -0.12) * mm});
            skLineSegment(sketch, "E2727", {"start": v(0, -0.12) * mm, "end": v(-0.01, -0.14) * mm});
            skLineSegment(sketch, "E2728", {"start": v(-0.03, -0.11) * mm, "end": v(-0.04, -0.1) * mm});
            skLineSegment(sketch, "E2729", {"start": v(-0.02, -0.1) * mm, "end": v(-0.02, -0.1) * mm});
            skLineSegment(sketch, "E2730", {"start": v(0.26, -0.1) * mm, "end": v(0.28, -0.11) * mm});
            skLineSegment(sketch, "E2731", {"start": v(0.28, -0.11) * mm, "end": v(0.28, -0.09) * mm});
            skLineSegment(sketch, "E2732", {"start": v(0.3, -0.1) * mm, "end": v(0.26, -0.1) * mm});
            skLineSegment(sketch, "E2733", {"start": v(0.27, -0.12) * mm, "end": v(0.26, -0.13) * mm});
            skLineSegment(sketch, "E2734", {"start": v(0.26, -0.13) * mm, "end": v(0.26, -0.14) * mm});
            skLineSegment(sketch, "E2735", {"start": v(0.26, -0.14) * mm, "end": v(0.27, -0.15) * mm});
            skLineSegment(sketch, "E2736", {"start": v(0.27, -0.15) * mm, "end": v(0.3, -0.15) * mm});
            skLineSegment(sketch, "E2737", {"start": v(0.3, -0.15) * mm, "end": v(0.3, -0.14) * mm});
            skLineSegment(sketch, "E2738", {"start": v(0.3, -0.14) * mm, "end": v(0.3, -0.13) * mm});
            skLineSegment(sketch, "E2739", {"start": v(0.3, -0.13) * mm, "end": v(0.3, -0.12) * mm});
            skLineSegment(sketch, "E2740", {"start": v(0.3, -0.12) * mm, "end": v(0.27, -0.12) * mm});
            skLineSegment(sketch, "E2741", {"start": v(0.29, -0.14) * mm, "end": v(0.3, -0.12) * mm});
            skLineSegment(sketch, "E2742", {"start": v(0.56, -0.13) * mm, "end": v(0.57, -0.12) * mm});
            skLineSegment(sketch, "E2743", {"start": v(0.57, -0.12) * mm, "end": v(0.6, -0.12) * mm});
            skLineSegment(sketch, "E2744", {"start": v(0.6, -0.12) * mm, "end": v(0.6, -0.13) * mm});
            skLineSegment(sketch, "E2745", {"start": v(0.6, -0.13) * mm, "end": v(0.6, -0.14) * mm});
            skLineSegment(sketch, "E2746", {"start": v(0.6, -0.14) * mm, "end": v(0.6, -0.15) * mm});
            skLineSegment(sketch, "E2747", {"start": v(0.6, -0.15) * mm, "end": v(0.57, -0.15) * mm});
            skLineSegment(sketch, "E2748", {"start": v(0.57, -0.15) * mm, "end": v(0.56, -0.14) * mm});
            skLineSegment(sketch, "E2749", {"start": v(0.56, -0.14) * mm, "end": v(0.56, -0.13) * mm});
            skLineSegment(sketch, "E2750", {"start": v(0.56, -0.11) * mm, "end": v(0.58, -0.11) * mm});
            skLineSegment(sketch, "E2751", {"start": v(0.58, -0.11) * mm, "end": v(0.57, -0.1) * mm});
            skLineSegment(sketch, "E2752", {"start": v(0.57, -0.1) * mm, "end": v(0.57, -0.1) * mm});
            skLineSegment(sketch, "E2753", {"start": v(0.57, -0.1) * mm, "end": v(0.58, -0.09) * mm});
            skLineSegment(sketch, "E2754", {"start": v(0.58, -0.09) * mm, "end": v(0.6, -0.09) * mm});
            skLineSegment(sketch, "E2755", {"start": v(0.6, -0.09) * mm, "end": v(0.6, -0.1) * mm});
            skLineSegment(sketch, "E2756", {"start": v(0.6, -0.1) * mm, "end": v(0.6, -0.1) * mm});
            skLineSegment(sketch, "E2757", {"start": v(0.6, -0.1) * mm, "end": v(0.6, -0.11) * mm});
            skLineSegment(sketch, "E2758", {"start": v(0.6, -0.12) * mm, "end": v(0.59, -0.14) * mm});
            skLineSegment(sketch, "E2759", {"start": v(0.56, -0.11) * mm, "end": v(0.56, -0.09) * mm});
            skLineSegment(sketch, "E2760", {"start": v(0.96, -0.17) * mm, "end": v(0.96, -0.18) * mm});
            skLineSegment(sketch, "E2761", {"start": v(0.96, -0.18) * mm, "end": v(0.97, -0.19) * mm});
            skLineSegment(sketch, "E2762", {"start": v(0.97, -0.2) * mm, "end": v(0.96, -0.2) * mm});
            skLineSegment(sketch, "E2763", {"start": v(0.96, -0.2) * mm, "end": v(0.96, -0.22) * mm});
            skLineSegment(sketch, "E2764", {"start": v(0.96, -0.22) * mm, "end": v(0.97, -0.22) * mm});
            skLineSegment(sketch, "E2765", {"start": v(0.97, -0.22) * mm, "end": v(1, -0.22) * mm});
            skLineSegment(sketch, "E2766", {"start": v(1, -0.22) * mm, "end": v(1, -0.22) * mm});
            skLineSegment(sketch, "E2767", {"start": v(1, -0.22) * mm, "end": v(1, -0.2) * mm});
            skLineSegment(sketch, "E2768", {"start": v(1, -0.2) * mm, "end": v(1, -0.2) * mm});
            skLineSegment(sketch, "E2769", {"start": v(1, -0.19) * mm, "end": v(1, -0.18) * mm});
            skLineSegment(sketch, "E2770", {"start": v(1, -0.18) * mm, "end": v(1, -0.17) * mm});
            skLineSegment(sketch, "E2771", {"start": v(1, -0.17) * mm, "end": v(1, -0.16) * mm});
            skLineSegment(sketch, "E2772", {"start": v(1, -0.16) * mm, "end": v(0.99, -0.16) * mm});
            skLineSegment(sketch, "E2773", {"start": v(0.99, -0.16) * mm, "end": v(0.98, -0.17) * mm});
            skLineSegment(sketch, "E2774", {"start": v(0.98, -0.17) * mm, "end": v(0.98, -0.17) * mm});
            skLineSegment(sketch, "E2775", {"start": v(0.98, -0.17) * mm, "end": v(0.97, -0.16) * mm});
            skLineSegment(sketch, "E2776", {"start": v(0.97, -0.16) * mm, "end": v(0.97, -0.16) * mm});
            skLineSegment(sketch, "E2777", {"start": v(0.97, -0.16) * mm, "end": v(0.96, -0.17) * mm});
            skLineSegment(sketch, "E2778", {"start": v(0.96, -0.24) * mm, "end": v(0.96, -0.25) * mm});
            skLineSegment(sketch, "E2779", {"start": v(0.96, -0.24) * mm, "end": v(1, -0.24) * mm});
            skLineSegment(sketch, "E2780", {"start": v(1, -0.25) * mm, "end": v(1, -0.24) * mm});
            skLineSegment(sketch, "E2781", {"start": v(1.42, 0.86) * mm, "end": v(1.42, 0.87) * mm});
            skLineSegment(sketch, "E2782", {"start": v(1.42, 0.87) * mm, "end": v(1.46, 0.87) * mm});
            skLineSegment(sketch, "E2783", {"start": v(1.46, 0.86) * mm, "end": v(1.46, 0.87) * mm});
            skLineSegment(sketch, "E2784", {"start": v(1.45, 0.89) * mm, "end": v(1.46, 0.9) * mm});
            skLineSegment(sketch, "E2785", {"start": v(1.46, 0.9) * mm, "end": v(1.46, 0.9) * mm});
            skLineSegment(sketch, "E2786", {"start": v(1.46, 0.9) * mm, "end": v(1.45, 0.91) * mm});
            skLineSegment(sketch, "E2787", {"start": v(1.46, 0.92) * mm, "end": v(1.43, 0.95) * mm});
            skLineSegment(sketch, "E2788", {"start": v(1.43, 0.95) * mm, "end": v(1.43, 0.95) * mm});
            skLineSegment(sketch, "E2789", {"start": v(1.43, 0.95) * mm, "end": v(1.42, 0.94) * mm});
            skLineSegment(sketch, "E2790", {"start": v(1.42, 0.94) * mm, "end": v(1.42, 0.93) * mm});
            skLineSegment(sketch, "E2791", {"start": v(1.42, 0.93) * mm, "end": v(1.43, 0.92) * mm});
            skLineSegment(sketch, "E2792", {"start": v(1.43, 0.91) * mm, "end": v(1.42, 0.9) * mm});
            skLineSegment(sketch, "E2793", {"start": v(1.42, 0.9) * mm, "end": v(1.42, 0.9) * mm});
            skLineSegment(sketch, "E2794", {"start": v(1.42, 0.9) * mm, "end": v(1.43, 0.89) * mm});
            skLineSegment(sketch, "E2795", {"start": v(1.43, 0.89) * mm, "end": v(1.45, 0.89) * mm});
            skLineSegment(sketch, "E2796", {"start": v(1.46, 0.92) * mm, "end": v(1.46, 0.95) * mm});
            skLineSegment(sketch, "E2797", {"start": v(-0.43, 0.87) * mm, "end": v(-0.43, 0.85) * mm});
            skLineSegment(sketch, "E2798", {"start": v(-0.43, 0.85) * mm, "end": v(-0.44, 0.85) * mm});
            skLineSegment(sketch, "E2799", {"start": v(-0.44, 0.85) * mm, "end": v(-0.45, 0.85) * mm});
            skLineSegment(sketch, "E2800", {"start": v(-0.45, 0.85) * mm, "end": v(-0.45, 0.87) * mm});
            skLineSegment(sketch, "E2801", {"start": v(-0.45, 0.87) * mm, "end": v(-0.44, 0.87) * mm});
            skLineSegment(sketch, "E2802", {"start": v(-0.44, 0.87) * mm, "end": v(-0.44, 0.87) * mm});
            skLineSegment(sketch, "E2803", {"start": v(-0.44, 0.87) * mm, "end": v(-0.43, 0.87) * mm});
            skLineSegment(sketch, "E2804", {"start": v(-0.45, 0.85) * mm, "end": v(-0.46, 0.86) * mm});
            skLineSegment(sketch, "E2805", {"start": v(-0.46, 0.86) * mm, "end": v(-0.47, 0.87) * mm});
            skLineSegment(sketch, "E2806", {"start": v(-0.46, 0.84) * mm, "end": v(-0.45, 0.84) * mm});
            skLineSegment(sketch, "E2807", {"start": v(-0.45, 0.84) * mm, "end": v(-0.44, 0.83) * mm});
            skLineSegment(sketch, "E2808", {"start": v(-0.44, 0.83) * mm, "end": v(-0.44, 0.81) * mm});
            skLineSegment(sketch, "E2809", {"start": v(-0.43, 0.81) * mm, "end": v(-0.47, 0.81) * mm});
            skLineSegment(sketch, "E2810", {"start": v(-0.47, 0.81) * mm, "end": v(-0.47, 0.83) * mm});
            skLineSegment(sketch, "E2811", {"start": v(-0.47, 0.83) * mm, "end": v(-0.46, 0.84) * mm});
            skLineSegment(sketch, "E2812", {"start": v(-0.44, 0.82) * mm, "end": v(-0.43, 0.84) * mm});
            skLineSegment(sketch, "E2813", {"start": v(-0.53, 0.84) * mm, "end": v(-0.54, 0.82) * mm});
            skLineSegment(sketch, "E2814", {"start": v(-0.54, 0.83) * mm, "end": v(-0.54, 0.81) * mm});
            skLineSegment(sketch, "E2815", {"start": v(-0.53, 0.81) * mm, "end": v(-0.57, 0.81) * mm});
            skLineSegment(sketch, "E2816", {"start": v(-0.57, 0.81) * mm, "end": v(-0.57, 0.83) * mm});
            skLineSegment(sketch, "E2817", {"start": v(-0.57, 0.83) * mm, "end": v(-0.56, 0.84) * mm});
            skLineSegment(sketch, "E2818", {"start": v(-0.56, 0.84) * mm, "end": v(-0.55, 0.84) * mm});
            skLineSegment(sketch, "E2819", {"start": v(-0.55, 0.84) * mm, "end": v(-0.54, 0.83) * mm});
            skLineSegment(sketch, "E2820", {"start": v(-0.54, 0.85) * mm, "end": v(-0.53, 0.85) * mm});
            skLineSegment(sketch, "E2821", {"start": v(-0.53, 0.85) * mm, "end": v(-0.53, 0.87) * mm});
            skLineSegment(sketch, "E2822", {"start": v(-0.53, 0.87) * mm, "end": v(-0.54, 0.87) * mm});
            skLineSegment(sketch, "E2823", {"start": v(-0.54, 0.87) * mm, "end": v(-0.55, 0.87) * mm});
            skLineSegment(sketch, "E2824", {"start": v(-0.55, 0.87) * mm, "end": v(-0.56, 0.87) * mm});
            skLineSegment(sketch, "E2825", {"start": v(-0.56, 0.87) * mm, "end": v(-0.56, 0.86) * mm});
            skLineSegment(sketch, "E2826", {"start": v(-0.56, 0.86) * mm, "end": v(-0.55, 0.85) * mm});
            skLineSegment(sketch, "E2827", {"start": v(-0.55, 0.85) * mm, "end": v(-0.57, 0.85) * mm});
            skLineSegment(sketch, "E2828", {"start": v(-0.57, 0.85) * mm, "end": v(-0.57, 0.87) * mm});
            skLineSegment(sketch, "E2829", {"start": v(-0.63, 0.87) * mm, "end": v(-0.67, 0.87) * mm});
            skLineSegment(sketch, "E2830", {"start": v(-0.67, 0.87) * mm, "end": v(-0.65, 0.85) * mm});
            skLineSegment(sketch, "E2831", {"start": v(-0.65, 0.85) * mm, "end": v(-0.65, 0.87) * mm});
            skLineSegment(sketch, "E2832", {"start": v(-0.65, 0.84) * mm, "end": v(-0.66, 0.84) * mm});
            skLineSegment(sketch, "E2833", {"start": v(-0.66, 0.84) * mm, "end": v(-0.67, 0.83) * mm});
            skLineSegment(sketch, "E2834", {"start": v(-0.67, 0.83) * mm, "end": v(-0.67, 0.81) * mm});
            skLineSegment(sketch, "E2835", {"start": v(-0.67, 0.81) * mm, "end": v(-0.63, 0.81) * mm});
            skLineSegment(sketch, "E2836", {"start": v(-0.64, 0.81) * mm, "end": v(-0.64, 0.83) * mm});
            skLineSegment(sketch, "E2837", {"start": v(-0.64, 0.83) * mm, "end": v(-0.65, 0.84) * mm});
            skLineSegment(sketch, "E2838", {"start": v(-0.64, 0.82) * mm, "end": v(-0.63, 0.84) * mm});
            skLineSegment(sketch, "E2839", {"start": v(-0.73, 0.84) * mm, "end": v(-0.74, 0.82) * mm});
            skLineSegment(sketch, "E2840", {"start": v(-0.74, 0.83) * mm, "end": v(-0.74, 0.81) * mm});
            skLineSegment(sketch, "E2841", {"start": v(-0.73, 0.81) * mm, "end": v(-0.77, 0.81) * mm});
            skLineSegment(sketch, "E2842", {"start": v(-0.77, 0.81) * mm, "end": v(-0.77, 0.83) * mm});
            skLineSegment(sketch, "E2843", {"start": v(-0.77, 0.83) * mm, "end": v(-0.76, 0.84) * mm});
            skLineSegment(sketch, "E2844", {"start": v(-0.76, 0.84) * mm, "end": v(-0.75, 0.84) * mm});
            skLineSegment(sketch, "E2845", {"start": v(-0.75, 0.84) * mm, "end": v(-0.74, 0.83) * mm});
            skLineSegment(sketch, "E2846", {"start": v(-0.74, 0.85) * mm, "end": v(-0.73, 0.85) * mm});
            skLineSegment(sketch, "E2847", {"start": v(-0.73, 0.85) * mm, "end": v(-0.73, 0.87) * mm});
            skLineSegment(sketch, "E2848", {"start": v(-0.73, 0.87) * mm, "end": v(-0.74, 0.87) * mm});
            skLineSegment(sketch, "E2849", {"start": v(-0.74, 0.87) * mm, "end": v(-0.74, 0.87) * mm});
            skLineSegment(sketch, "E2850", {"start": v(-0.74, 0.87) * mm, "end": v(-0.75, 0.87) * mm});
            skLineSegment(sketch, "E2851", {"start": v(-0.75, 0.87) * mm, "end": v(-0.75, 0.86) * mm});
            skLineSegment(sketch, "E2852", {"start": v(-0.75, 0.87) * mm, "end": v(-0.76, 0.87) * mm});
            skLineSegment(sketch, "E2853", {"start": v(-0.76, 0.87) * mm, "end": v(-0.76, 0.87) * mm});
            skLineSegment(sketch, "E2854", {"start": v(-0.76, 0.87) * mm, "end": v(-0.77, 0.87) * mm});
            skLineSegment(sketch, "E2855", {"start": v(-0.77, 0.87) * mm, "end": v(-0.77, 0.85) * mm});
            skLineSegment(sketch, "E2856", {"start": v(-0.77, 0.85) * mm, "end": v(-0.76, 0.85) * mm});
            skLineSegment(sketch, "E2857", {"start": v(-0.83, 0.85) * mm, "end": v(-0.86, 0.87) * mm});
            skLineSegment(sketch, "E2858", {"start": v(-0.86, 0.87) * mm, "end": v(-0.86, 0.87) * mm});
            skLineSegment(sketch, "E2859", {"start": v(-0.86, 0.87) * mm, "end": v(-0.87, 0.87) * mm});
            skLineSegment(sketch, "E2860", {"start": v(-0.87, 0.87) * mm, "end": v(-0.87, 0.85) * mm});
            skLineSegment(sketch, "E2861", {"start": v(-0.87, 0.85) * mm, "end": v(-0.86, 0.85) * mm});
            skLineSegment(sketch, "E2862", {"start": v(-0.86, 0.84) * mm, "end": v(-0.85, 0.84) * mm});
            skLineSegment(sketch, "E2863", {"start": v(-0.85, 0.84) * mm, "end": v(-0.84, 0.83) * mm});
            skLineSegment(sketch, "E2864", {"start": v(-0.84, 0.83) * mm, "end": v(-0.84, 0.81) * mm});
            skLineSegment(sketch, "E2865", {"start": v(-0.83, 0.81) * mm, "end": v(-0.87, 0.81) * mm});
            skLineSegment(sketch, "E2866", {"start": v(-0.87, 0.81) * mm, "end": v(-0.87, 0.83) * mm});
            skLineSegment(sketch, "E2867", {"start": v(-0.87, 0.83) * mm, "end": v(-0.86, 0.84) * mm});
            skLineSegment(sketch, "E2868", {"start": v(-0.84, 0.82) * mm, "end": v(-0.83, 0.84) * mm});
            skLineSegment(sketch, "E2869", {"start": v(-0.83, 0.85) * mm, "end": v(-0.83, 0.87) * mm});
            skLineSegment(sketch, "E2870", {"start": v(-0.93, 0.87) * mm, "end": v(-0.93, 0.85) * mm});
            skLineSegment(sketch, "E2871", {"start": v(-0.93, 0.86) * mm, "end": v(-0.97, 0.86) * mm});
            skLineSegment(sketch, "E2872", {"start": v(-0.97, 0.86) * mm, "end": v(-0.96, 0.85) * mm});
            skLineSegment(sketch, "E2873", {"start": v(-0.95, 0.84) * mm, "end": v(-0.94, 0.83) * mm});
            skLineSegment(sketch, "E2874", {"start": v(-0.94, 0.83) * mm, "end": v(-0.94, 0.81) * mm});
            skLineSegment(sketch, "E2875", {"start": v(-0.93, 0.81) * mm, "end": v(-0.97, 0.81) * mm});
            skLineSegment(sketch, "E2876", {"start": v(-0.97, 0.81) * mm, "end": v(-0.97, 0.83) * mm});
            skLineSegment(sketch, "E2877", {"start": v(-0.97, 0.83) * mm, "end": v(-0.96, 0.84) * mm});
            skLineSegment(sketch, "E2878", {"start": v(-0.96, 0.84) * mm, "end": v(-0.95, 0.84) * mm});
            skLineSegment(sketch, "E2879", {"start": v(-0.94, 0.82) * mm, "end": v(-0.93, 0.84) * mm});
            skLineSegment(sketch, "E2880", {"start": v(-1.08, 0.74) * mm, "end": v(-1.08, 0.72) * mm});
            skLineSegment(sketch, "E2881", {"start": v(-1.08, 0.72) * mm, "end": v(-1.09, 0.72) * mm});
            skLineSegment(sketch, "E2882", {"start": v(-1.09, 0.72) * mm, "end": v(-1.1, 0.72) * mm});
            skLineSegment(sketch, "E2883", {"start": v(-1.1, 0.72) * mm, "end": v(-1.1, 0.72) * mm});
            skLineSegment(sketch, "E2884", {"start": v(-1.1, 0.72) * mm, "end": v(-1.1, 0.74) * mm});
            skLineSegment(sketch, "E2885", {"start": v(-1.1, 0.74) * mm, "end": v(-1.1, 0.74) * mm});
            skLineSegment(sketch, "E2886", {"start": v(-1.1, 0.74) * mm, "end": v(-1.09, 0.74) * mm});
            skLineSegment(sketch, "E2887", {"start": v(-1.09, 0.74) * mm, "end": v(-1.08, 0.74) * mm});
            skLineSegment(sketch, "E2888", {"start": v(-1.1, 0.74) * mm, "end": v(-1.11, 0.74) * mm});
            skLineSegment(sketch, "E2889", {"start": v(-1.11, 0.74) * mm, "end": v(-1.12, 0.74) * mm});
            skLineSegment(sketch, "E2890", {"start": v(-1.12, 0.74) * mm, "end": v(-1.12, 0.72) * mm});
            skLineSegment(sketch, "E2891", {"start": v(-1.12, 0.72) * mm, "end": v(-1.11, 0.72) * mm});
            skLineSegment(sketch, "E2892", {"start": v(-1.11, 0.72) * mm, "end": v(-1.1, 0.72) * mm});
            skLineSegment(sketch, "E2893", {"start": v(-1.09, 0.7) * mm, "end": v(-1.11, 0.7) * mm});
            skLineSegment(sketch, "E2894", {"start": v(-1.11, 0.7) * mm, "end": v(-1.12, 0.7) * mm});
            skLineSegment(sketch, "E2895", {"start": v(-1.12, 0.7) * mm, "end": v(-1.12, 0.68) * mm});
            skLineSegment(sketch, "E2896", {"start": v(-1.12, 0.68) * mm, "end": v(-1.08, 0.68) * mm});
            skLineSegment(sketch, "E2897", {"start": v(-1.08, 0.68) * mm, "end": v(-1.08, 0.7) * mm});
            skLineSegment(sketch, "E2898", {"start": v(-1.08, 0.7) * mm, "end": v(-1.09, 0.7) * mm});
            skLineSegment(sketch, "E2899", {"start": v(-1.18, 0.71) * mm, "end": v(-1.19, 0.72) * mm});
            skLineSegment(sketch, "E2900", {"start": v(-1.19, 0.72) * mm, "end": v(-1.21, 0.72) * mm});
            skLineSegment(sketch, "E2901", {"start": v(-1.21, 0.72) * mm, "end": v(-1.22, 0.71) * mm});
            skLineSegment(sketch, "E2902", {"start": v(-1.22, 0.71) * mm, "end": v(-1.22, 0.7) * mm});
            skLineSegment(sketch, "E2903", {"start": v(-1.22, 0.7) * mm, "end": v(-1.18, 0.7) * mm});
            skLineSegment(sketch, "E2904", {"start": v(-1.18, 0.7) * mm, "end": v(-1.18, 0.71) * mm});
            skLineSegment(sketch, "E2905", {"start": v(-1.18, 0.73) * mm, "end": v(-1.19, 0.73) * mm});
            skLineSegment(sketch, "E2906", {"start": v(-1.19, 0.73) * mm, "end": v(-1.21, 0.75) * mm});
            skLineSegment(sketch, "E2907", {"start": v(-1.21, 0.75) * mm, "end": v(-1.22, 0.75) * mm});
            skLineSegment(sketch, "E2908", {"start": v(-1.22, 0.75) * mm, "end": v(-1.22, 0.73) * mm});
            skLineSegment(sketch, "E2909", {"start": v(-1.28, 0.72) * mm, "end": v(-1.28, 0.74) * mm});
            skLineSegment(sketch, "E2910", {"start": v(-1.28, 0.74) * mm, "end": v(-1.29, 0.74) * mm});
            skLineSegment(sketch, "E2911", {"start": v(-1.29, 0.74) * mm, "end": v(-1.31, 0.74) * mm});
            skLineSegment(sketch, "E2912", {"start": v(-1.31, 0.74) * mm, "end": v(-1.32, 0.74) * mm});
            skLineSegment(sketch, "E2913", {"start": v(-1.32, 0.74) * mm, "end": v(-1.32, 0.72) * mm});
            skLineSegment(sketch, "E2914", {"start": v(-1.32, 0.72) * mm, "end": v(-1.31, 0.72) * mm});
            skLineSegment(sketch, "E2915", {"start": v(-1.31, 0.72) * mm, "end": v(-1.3, 0.72) * mm});
            skLineSegment(sketch, "E2916", {"start": v(-1.3, 0.72) * mm, "end": v(-1.3, 0.72) * mm});
            skLineSegment(sketch, "E2917", {"start": v(-1.3, 0.72) * mm, "end": v(-1.3, 0.74) * mm});
            skLineSegment(sketch, "E2918", {"start": v(-1.28, 0.72) * mm, "end": v(-1.29, 0.72) * mm});
            skLineSegment(sketch, "E2919", {"start": v(-1.29, 0.7) * mm, "end": v(-1.31, 0.7) * mm});
            skLineSegment(sketch, "E2920", {"start": v(-1.31, 0.7) * mm, "end": v(-1.32, 0.7) * mm});
            skLineSegment(sketch, "E2921", {"start": v(-1.32, 0.7) * mm, "end": v(-1.32, 0.68) * mm});
            skLineSegment(sketch, "E2922", {"start": v(-1.32, 0.68) * mm, "end": v(-1.28, 0.68) * mm});
            skLineSegment(sketch, "E2923", {"start": v(-1.28, 0.68) * mm, "end": v(-1.28, 0.7) * mm});
            skLineSegment(sketch, "E2924", {"start": v(-1.28, 0.7) * mm, "end": v(-1.29, 0.7) * mm});
            skLineSegment(sketch, "E2925", {"start": v(-1.22, 0.13) * mm, "end": v(-1.22, 0.1) * mm});
            skLineSegment(sketch, "E2926", {"start": v(-1.22, 0.1) * mm, "end": v(-1.2, 0.1) * mm});
            skLineSegment(sketch, "E2927", {"start": v(-1.2, 0.1) * mm, "end": v(-1.2, 0.12) * mm});
            skLineSegment(sketch, "E2928", {"start": v(-1.2, 0.12) * mm, "end": v(-1.2, 0.13) * mm});
            skLineSegment(sketch, "E2929", {"start": v(-1.2, 0.13) * mm, "end": v(-1.2, 0.13) * mm});
            skLineSegment(sketch, "E2930", {"start": v(-1.2, 0.13) * mm, "end": v(-1.19, 0.13) * mm});
            skLineSegment(sketch, "E2931", {"start": v(-1.19, 0.13) * mm, "end": v(-1.18, 0.13) * mm});
            skLineSegment(sketch, "E2932", {"start": v(-1.18, 0.13) * mm, "end": v(-1.18, 0.11) * mm});
            skLineSegment(sketch, "E2933", {"start": v(-1.18, 0.11) * mm, "end": v(-1.19, 0.1) * mm});
            skLineSegment(sketch, "E2934", {"start": v(-1.19, 0.1) * mm, "end": v(-1.21, 0.1) * mm});
            skLineSegment(sketch, "E2935", {"start": v(-1.21, 0.1) * mm, "end": v(-1.22, 0.1) * mm});
            skLineSegment(sketch, "E2936", {"start": v(-1.22, 0.1) * mm, "end": v(-1.22, 0.07) * mm});
            skLineSegment(sketch, "E2937", {"start": v(-1.22, 0.07) * mm, "end": v(-1.18, 0.07) * mm});
            skLineSegment(sketch, "E2938", {"start": v(-1.18, 0.07) * mm, "end": v(-1.18, 0.1) * mm});
            skLineSegment(sketch, "E2939", {"start": v(-1.18, 0.1) * mm, "end": v(-1.19, 0.1) * mm});
            skLineSegment(sketch, "E2940", {"start": v(-1.12, 0.1) * mm, "end": v(-1.12, 0.07) * mm});
            skLineSegment(sketch, "E2941", {"start": v(-1.12, 0.07) * mm, "end": v(-1.08, 0.07) * mm});
            skLineSegment(sketch, "E2942", {"start": v(-1.08, 0.07) * mm, "end": v(-1.08, 0.1) * mm});
            skLineSegment(sketch, "E2943", {"start": v(-1.08, 0.1) * mm, "end": v(-1.09, 0.1) * mm});
            skLineSegment(sketch, "E2944", {"start": v(-1.09, 0.1) * mm, "end": v(-1.11, 0.1) * mm});
            skLineSegment(sketch, "E2945", {"start": v(-1.11, 0.1) * mm, "end": v(-1.12, 0.1) * mm});
            skLineSegment(sketch, "E2946", {"start": v(-1.1, 0.1) * mm, "end": v(-1.11, 0.12) * mm});
            skLineSegment(sketch, "E2947", {"start": v(-1.11, 0.12) * mm, "end": v(-1.12, 0.13) * mm});
            skLineSegment(sketch, "E2948", {"start": v(-1.1, 0.13) * mm, "end": v(-1.1, 0.1) * mm});
            skLineSegment(sketch, "E2949", {"start": v(-1.1, 0.1) * mm, "end": v(-1.09, 0.1) * mm});
            skLineSegment(sketch, "E2950", {"start": v(-1.09, 0.1) * mm, "end": v(-1.08, 0.11) * mm});
            skLineSegment(sketch, "E2951", {"start": v(-1.08, 0.11) * mm, "end": v(-1.08, 0.13) * mm});
            skLineSegment(sketch, "E2952", {"start": v(-1.08, 0.13) * mm, "end": v(-1.09, 0.13) * mm});
            skLineSegment(sketch, "E2953", {"start": v(-1.09, 0.13) * mm, "end": v(-1.1, 0.13) * mm});
            skLineSegment(sketch, "E2954", {"start": v(-1.1, 0.13) * mm, "end": v(-1.1, 0.13) * mm});
            skLineSegment(sketch, "E2955", {"start": v(-0.85, -0.08) * mm, "end": v(-0.83, -0.08) * mm});
            skLineSegment(sketch, "E2956", {"start": v(-0.83, -0.08) * mm, "end": v(-0.82, -0.09) * mm});
            skLineSegment(sketch, "E2957", {"start": v(-0.82, -0.09) * mm, "end": v(-0.82, -0.11) * mm});
            skLineSegment(sketch, "E2958", {"start": v(-0.82, -0.11) * mm, "end": v(-0.83, -0.12) * mm});
            skLineSegment(sketch, "E2959", {"start": v(-0.83, -0.12) * mm, "end": v(-0.85, -0.12) * mm});
            skLineSegment(sketch, "E2960", {"start": v(-0.85, -0.12) * mm, "end": v(-0.85, -0.08) * mm});
            skLineSegment(sketch, "E2961", {"start": v(-0.81, -0.1) * mm, "end": v(-0.8, -0.08) * mm});
            skLineSegment(sketch, "E2962", {"start": v(-0.8, -0.08) * mm, "end": v(-0.8, -0.12) * mm});
            skLineSegment(sketch, "E2963", {"start": v(-0.81, -0.12) * mm, "end": v(-0.79, -0.12) * mm});
            skLineSegment(sketch, "E2964", {"start": v(-0.77, -0.12) * mm, "end": v(-0.75, -0.12) * mm});
            skLineSegment(sketch, "E2965", {"start": v(-0.76, -0.12) * mm, "end": v(-0.76, -0.08) * mm});
            skLineSegment(sketch, "E2966", {"start": v(-0.76, -0.08) * mm, "end": v(-0.77, -0.1) * mm});
            skLineSegment(sketch, "E2967", {"start": v(-0.77, -0.18) * mm, "end": v(-0.76, -0.18) * mm});
            skLineSegment(sketch, "E2968", {"start": v(-0.76, -0.18) * mm, "end": v(-0.75, -0.19) * mm});
            skLineSegment(sketch, "E2969", {"start": v(-0.75, -0.19) * mm, "end": v(-0.77, -0.21) * mm});
            skLineSegment(sketch, "E2970", {"start": v(-0.77, -0.21) * mm, "end": v(-0.77, -0.22) * mm});
            skLineSegment(sketch, "E2971", {"start": v(-0.77, -0.22) * mm, "end": v(-0.76, -0.22) * mm});
            skLineSegment(sketch, "E2972", {"start": v(-0.76, -0.22) * mm, "end": v(-0.75, -0.21) * mm});
            skLineSegment(sketch, "E2973", {"start": v(-0.75, -0.21) * mm, "end": v(-0.75, -0.19) * mm});
            skLineSegment(sketch, "E2974", {"start": v(-0.77, -0.18) * mm, "end": v(-0.77, -0.19) * mm});
            skLineSegment(sketch, "E2975", {"start": v(-0.77, -0.19) * mm, "end": v(-0.77, -0.21) * mm});
            skLineSegment(sketch, "E2976", {"start": v(-0.79, -0.22) * mm, "end": v(-0.81, -0.22) * mm});
            skLineSegment(sketch, "E2977", {"start": v(-0.8, -0.22) * mm, "end": v(-0.8, -0.18) * mm});
            skLineSegment(sketch, "E2978", {"start": v(-0.8, -0.18) * mm, "end": v(-0.81, -0.2) * mm});
            skLineSegment(sketch, "E2979", {"start": v(-0.82, -0.19) * mm, "end": v(-0.83, -0.18) * mm});
            skLineSegment(sketch, "E2980", {"start": v(-0.83, -0.18) * mm, "end": v(-0.85, -0.18) * mm});
            skLineSegment(sketch, "E2981", {"start": v(-0.85, -0.18) * mm, "end": v(-0.85, -0.22) * mm});
            skLineSegment(sketch, "E2982", {"start": v(-0.85, -0.22) * mm, "end": v(-0.83, -0.22) * mm});
            skLineSegment(sketch, "E2983", {"start": v(-0.83, -0.22) * mm, "end": v(-0.82, -0.21) * mm});
            skLineSegment(sketch, "E2984", {"start": v(-0.82, -0.21) * mm, "end": v(-0.82, -0.19) * mm});
            skLineSegment(sketch, "E2985", {"start": v(-0.74, -0.57) * mm, "end": v(-0.74, -0.6) * mm});
            skLineSegment(sketch, "E2986", {"start": v(-0.74, -0.6) * mm, "end": v(-0.76, -0.57) * mm});
            skLineSegment(sketch, "E2987", {"start": v(-0.76, -0.57) * mm, "end": v(-0.72, -0.57) * mm});
            skLineSegment(sketch, "E2988", {"start": v(-0.73, -0.6) * mm, "end": v(-0.75, -0.6) * mm});
            skLineSegment(sketch, "E2989", {"start": v(-0.75, -0.6) * mm, "end": v(-0.76, -0.6) * mm});
            skLineSegment(sketch, "E2990", {"start": v(-0.76, -0.6) * mm, "end": v(-0.76, -0.63) * mm});
            skLineSegment(sketch, "E2991", {"start": v(-0.76, -0.63) * mm, "end": v(-0.72, -0.63) * mm});
            skLineSegment(sketch, "E2992", {"start": v(-0.72, -0.63) * mm, "end": v(-0.72, -0.6) * mm});
            skLineSegment(sketch, "E2993", {"start": v(-0.72, -0.6) * mm, "end": v(-0.73, -0.6) * mm});
            skLineSegment(sketch, "E2994", {"start": v(-0.92, -0.6) * mm, "end": v(-0.92, -0.63) * mm});
            skLineSegment(sketch, "E2995", {"start": v(-0.92, -0.63) * mm, "end": v(-0.96, -0.63) * mm});
            skLineSegment(sketch, "E2996", {"start": v(-0.96, -0.63) * mm, "end": v(-0.96, -0.6) * mm});
            skLineSegment(sketch, "E2997", {"start": v(-0.96, -0.6) * mm, "end": v(-0.95, -0.6) * mm});
            skLineSegment(sketch, "E2998", {"start": v(-0.95, -0.6) * mm, "end": v(-0.93, -0.6) * mm});
            skLineSegment(sketch, "E2999", {"start": v(-0.93, -0.6) * mm, "end": v(-0.92, -0.6) * mm});
            skLineSegment(sketch, "E3000", {"start": v(-0.93, -0.6) * mm, "end": v(-0.92, -0.59) * mm});
            skLineSegment(sketch, "E3001", {"start": v(-0.92, -0.59) * mm, "end": v(-0.92, -0.57) * mm});
            skLineSegment(sketch, "E3002", {"start": v(-0.92, -0.57) * mm, "end": v(-0.93, -0.57) * mm});
            skLineSegment(sketch, "E3003", {"start": v(-0.93, -0.57) * mm, "end": v(-0.93, -0.57) * mm});
            skLineSegment(sketch, "E3004", {"start": v(-0.93, -0.57) * mm, "end": v(-0.94, -0.57) * mm});
            skLineSegment(sketch, "E3005", {"start": v(-0.94, -0.57) * mm, "end": v(-0.94, -0.58) * mm});
            skLineSegment(sketch, "E3006", {"start": v(-0.94, -0.57) * mm, "end": v(-0.95, -0.57) * mm});
            skLineSegment(sketch, "E3007", {"start": v(-0.95, -0.57) * mm, "end": v(-0.95, -0.57) * mm});
            skLineSegment(sketch, "E3008", {"start": v(-0.95, -0.57) * mm, "end": v(-0.96, -0.57) * mm});
            skLineSegment(sketch, "E3009", {"start": v(-0.96, -0.57) * mm, "end": v(-0.96, -0.59) * mm});
            skLineSegment(sketch, "E3010", {"start": v(-0.96, -0.59) * mm, "end": v(-0.95, -0.6) * mm});
            skLineSegment(sketch, "E3011", {"start": v(-0.92, -1.07) * mm, "end": v(-0.92, -1.1) * mm});
            skLineSegment(sketch, "E3012", {"start": v(-0.92, -1.08) * mm, "end": v(-0.96, -1.08) * mm});
            skLineSegment(sketch, "E3013", {"start": v(-0.96, -1.08) * mm, "end": v(-0.95, -1.1) * mm});
            skLineSegment(sketch, "E3014", {"start": v(-0.95, -1.1) * mm, "end": v(-0.96, -1.1) * mm});
            skLineSegment(sketch, "E3015", {"start": v(-0.96, -1.1) * mm, "end": v(-0.96, -1.13) * mm});
            skLineSegment(sketch, "E3016", {"start": v(-0.96, -1.13) * mm, "end": v(-0.92, -1.13) * mm});
            skLineSegment(sketch, "E3017", {"start": v(-0.92, -1.13) * mm, "end": v(-0.92, -1.1) * mm});
            skLineSegment(sketch, "E3018", {"start": v(-0.92, -1.1) * mm, "end": v(-0.93, -1.1) * mm});
            skLineSegment(sketch, "E3019", {"start": v(-0.93, -1.1) * mm, "end": v(-0.95, -1.1) * mm});
            skLineSegment(sketch, "E3020", {"start": v(-0.76, -1.1) * mm, "end": v(-0.76, -1.13) * mm});
            skLineSegment(sketch, "E3021", {"start": v(-0.76, -1.13) * mm, "end": v(-0.72, -1.13) * mm});
            skLineSegment(sketch, "E3022", {"start": v(-0.72, -1.13) * mm, "end": v(-0.72, -1.1) * mm});
            skLineSegment(sketch, "E3023", {"start": v(-0.72, -1.1) * mm, "end": v(-0.73, -1.1) * mm});
            skLineSegment(sketch, "E3024", {"start": v(-0.73, -1.1) * mm, "end": v(-0.75, -1.1) * mm});
            skLineSegment(sketch, "E3025", {"start": v(-0.75, -1.1) * mm, "end": v(-0.76, -1.1) * mm});
            skLineSegment(sketch, "E3026", {"start": v(-0.75, -1.1) * mm, "end": v(-0.76, -1.09) * mm});
            skLineSegment(sketch, "E3027", {"start": v(-0.76, -1.09) * mm, "end": v(-0.76, -1.07) * mm});
            skLineSegment(sketch, "E3028", {"start": v(-0.76, -1.07) * mm, "end": v(-0.75, -1.07) * mm});
            skLineSegment(sketch, "E3029", {"start": v(-0.75, -1.07) * mm, "end": v(-0.75, -1.07) * mm});
            skLineSegment(sketch, "E3030", {"start": v(-0.75, -1.07) * mm, "end": v(-0.72, -1.1) * mm});
            skLineSegment(sketch, "E3031", {"start": v(-0.72, -1.1) * mm, "end": v(-0.72, -1.07) * mm});
            skLineSegment(sketch, "E3032", {"start": v(-0.97, 1.28) * mm, "end": v(-1, 1.28) * mm});
            skLineSegment(sketch, "E3033", {"start": v(-0.98, 1.28) * mm, "end": v(-0.98, 1.32) * mm});
            skLineSegment(sketch, "E3034", {"start": v(-0.98, 1.32) * mm, "end": v(-1, 1.3) * mm});
            skLineSegment(sketch, "E3035", {"start": v(-1, 1.31) * mm, "end": v(-1, 1.29) * mm});
            skLineSegment(sketch, "E3036", {"start": v(-1, 1.29) * mm, "end": v(-1.01, 1.28) * mm});
            skLineSegment(sketch, "E3037", {"start": v(-1.01, 1.28) * mm, "end": v(-1.02, 1.28) * mm});
            skLineSegment(sketch, "E3038", {"start": v(-1.02, 1.28) * mm, "end": v(-1.03, 1.29) * mm});
            skLineSegment(sketch, "E3039", {"start": v(-1.03, 1.29) * mm, "end": v(-1.03, 1.31) * mm});
            skLineSegment(sketch, "E3040", {"start": v(-1.03, 1.31) * mm, "end": v(-1.02, 1.32) * mm});
            skLineSegment(sketch, "E3041", {"start": v(-1.02, 1.32) * mm, "end": v(-1.01, 1.32) * mm});
            skLineSegment(sketch, "E3042", {"start": v(-1.01, 1.32) * mm, "end": v(-1, 1.31) * mm});
            skLineSegment(sketch, "E3043", {"start": v(-1.02, 1.3) * mm, "end": v(-1, 1.28) * mm});
            skLineSegment(sketch, "E3044", {"start": v(0.09, -0.6) * mm, "end": v(0.07, -0.6) * mm});
            skLineSegment(sketch, "E3045", {"start": v(0.07, -0.6) * mm, "end": v(0.07, -0.62) * mm});
            skLineSegment(sketch, "E3046", {"start": v(0.07, -0.62) * mm, "end": v(0.09, -0.63) * mm});
            skLineSegment(sketch, "E3047", {"start": v(0.09, -0.63) * mm, "end": v(0.1, -0.63) * mm});
            skLineSegment(sketch, "E3048", {"start": v(0.1, -0.63) * mm, "end": v(0.12, -0.64) * mm});
            skLineSegment(sketch, "E3049", {"start": v(0.12, -0.64) * mm, "end": v(0.12, -0.65) * mm});
            skLineSegment(sketch, "E3050", {"start": v(0.12, -0.65) * mm, "end": v(0.1, -0.66) * mm});
            skLineSegment(sketch, "E3051", {"start": v(0.1, -0.66) * mm, "end": v(0.09, -0.66) * mm});
            skLineSegment(sketch, "E3052", {"start": v(0.09, -0.66) * mm, "end": v(0.07, -0.65) * mm});
            skLineSegment(sketch, "E3053", {"start": v(0.09, -0.6) * mm, "end": v(0.1, -0.6) * mm});
            skLineSegment(sketch, "E3054", {"start": v(0.1, -0.6) * mm, "end": v(0.12, -0.6) * mm});
            skLineSegment(sketch, "E3055", {"start": v(0.14, -0.62) * mm, "end": v(0.16, -0.6) * mm});
            skLineSegment(sketch, "E3056", {"start": v(0.16, -0.6) * mm, "end": v(0.16, -0.66) * mm});
            skLineSegment(sketch, "E3057", {"start": v(0.18, -0.66) * mm, "end": v(0.14, -0.66) * mm});
            skLineSegment(sketch, "E3058", {"start": v(0.48, -0.77) * mm, "end": v(0.55, -0.77) * mm});
            skLineSegment(sketch, "E3059", {"start": v(0.55, -0.8) * mm, "end": v(0.55, -0.75) * mm});
            skLineSegment(sketch, "E3060", {"start": v(0.5, -0.8) * mm, "end": v(0.48, -0.77) * mm});
            skLineSegment(sketch, "E3061", {"start": v(0.51, -0.82) * mm, "end": v(0.51, -0.86) * mm});
            skLineSegment(sketch, "E3062", {"start": v(0.54, -0.88) * mm, "end": v(0.55, -0.9) * mm});
            skLineSegment(sketch, "E3063", {"start": v(0.55, -0.9) * mm, "end": v(0.55, -0.91) * mm});
            skLineSegment(sketch, "E3064", {"start": v(0.55, -0.91) * mm, "end": v(0.54, -0.92) * mm});
            skLineSegment(sketch, "E3065", {"start": v(0.54, -0.92) * mm, "end": v(0.5, -0.88) * mm});
            skLineSegment(sketch, "E3066", {"start": v(0.5, -0.88) * mm, "end": v(0.54, -0.88) * mm});
            skLineSegment(sketch, "E3067", {"start": v(0.5, -0.88) * mm, "end": v(0.48, -0.9) * mm});
            skLineSegment(sketch, "E3068", {"start": v(0.48, -0.9) * mm, "end": v(0.48, -0.91) * mm});
            skLineSegment(sketch, "E3069", {"start": v(0.48, -0.91) * mm, "end": v(0.5, -0.92) * mm});
            skLineSegment(sketch, "E3070", {"start": v(0.5, -0.92) * mm, "end": v(0.54, -0.92) * mm});
            skLineSegment(sketch, "E3071", {"start": v(0.54, -0.95) * mm, "end": v(0.55, -0.96) * mm});
            skLineSegment(sketch, "E3072", {"start": v(0.55, -0.96) * mm, "end": v(0.55, -0.98) * mm});
            skLineSegment(sketch, "E3073", {"start": v(0.55, -0.98) * mm, "end": v(0.54, -0.99) * mm});
            skLineSegment(sketch, "E3074", {"start": v(0.55, -1.01) * mm, "end": v(0.55, -1.03) * mm});
            skLineSegment(sketch, "E3075", {"start": v(0.55, -1.02) * mm, "end": v(0.48, -1.02) * mm});
            skLineSegment(sketch, "E3076", {"start": v(0.48, -1.03) * mm, "end": v(0.48, -1.01) * mm});
            skLineSegment(sketch, "E3077", {"start": v(0.5, -0.99) * mm, "end": v(0.48, -0.98) * mm});
            skLineSegment(sketch, "E3078", {"start": v(0.48, -0.98) * mm, "end": v(0.48, -0.96) * mm});
            skLineSegment(sketch, "E3079", {"start": v(0.48, -0.96) * mm, "end": v(0.5, -0.95) * mm});
            skLineSegment(sketch, "E3080", {"start": v(0.5, -0.95) * mm, "end": v(0.5, -0.95) * mm});
            skLineSegment(sketch, "E3081", {"start": v(0.5, -0.95) * mm, "end": v(0.51, -0.96) * mm});
            skLineSegment(sketch, "E3082", {"start": v(0.51, -0.96) * mm, "end": v(0.53, -0.95) * mm});
            skLineSegment(sketch, "E3083", {"start": v(0.53, -0.95) * mm, "end": v(0.54, -0.95) * mm});
            skLineSegment(sketch, "E3084", {"start": v(0.51, -0.96) * mm, "end": v(0.51, -0.97) * mm});
            skLineSegment(sketch, "E3085", {"start": v(0.55, -1.05) * mm, "end": v(0.55, -1.1) * mm});
            skLineSegment(sketch, "E3086", {"start": v(0.55, -1.1) * mm, "end": v(0.48, -1.1) * mm});
            skLineSegment(sketch, "E3087", {"start": v(0.48, -1.1) * mm, "end": v(0.48, -1.05) * mm});
            skLineSegment(sketch, "E3088", {"start": v(0.51, -1.08) * mm, "end": v(0.51, -1.1) * mm});
            skLineSegment(sketch, "E3089", {"start": v(0.18, -1.11) * mm, "end": v(0.12, -1.11) * mm});
            skLineSegment(sketch, "E3090", {"start": v(0.12, -1.11) * mm, "end": v(0.12, -1.08) * mm});
            skLineSegment(sketch, "E3091", {"start": v(0.12, -1.08) * mm, "end": v(0.13, -1.07) * mm});
            skLineSegment(sketch, "E3092", {"start": v(0.13, -1.07) * mm, "end": v(0.15, -1.07) * mm});
            skLineSegment(sketch, "E3093", {"start": v(0.15, -1.07) * mm, "end": v(0.16, -1.08) * mm});
            skLineSegment(sketch, "E3094", {"start": v(0.16, -1.08) * mm, "end": v(0.16, -1.11) * mm});
            skLineSegment(sketch, "E3095", {"start": v(0.18, -1.05) * mm, "end": v(0.18, -1) * mm});
            skLineSegment(sketch, "E3096", {"start": v(0.18, -1.03) * mm, "end": v(0.12, -1.03) * mm});
            skLineSegment(sketch, "E3097", {"start": v(0.12, -1.03) * mm, "end": v(0.14, -1.05) * mm});
            skLineSegment(sketch, "E3098", {"start": v(-0.57, -1.36) * mm, "end": v(-0.57, -1.36) * mm});
            skLineSegment(sketch, "E3099", {"start": v(-0.57, -1.36) * mm, "end": v(-0.58, -1.37) * mm});
            skLineSegment(sketch, "E3100", {"start": v(-0.58, -1.37) * mm, "end": v(-0.6, -1.37) * mm});
            skLineSegment(sketch, "E3101", {"start": v(-0.6, -1.35) * mm, "end": v(-0.6, -1.4) * mm});
            skLineSegment(sketch, "E3102", {"start": v(-0.6, -1.4) * mm, "end": v(-0.58, -1.4) * mm});
            skLineSegment(sketch, "E3103", {"start": v(-0.58, -1.4) * mm, "end": v(-0.57, -1.39) * mm});
            skLineSegment(sketch, "E3104", {"start": v(-0.57, -1.39) * mm, "end": v(-0.57, -1.38) * mm});
            skLineSegment(sketch, "E3105", {"start": v(-0.57, -1.38) * mm, "end": v(-0.58, -1.37) * mm});
            skLineSegment(sketch, "E3106", {"start": v(-0.57, -1.36) * mm, "end": v(-0.58, -1.35) * mm});
            skLineSegment(sketch, "E3107", {"start": v(-0.58, -1.35) * mm, "end": v(-0.6, -1.35) * mm});
            skLineSegment(sketch, "E3108", {"start": v(-0.68, -1.39) * mm, "end": v(-0.68, -1.4) * mm});
            skLineSegment(sketch, "E3109", {"start": v(-0.68, -1.4) * mm, "end": v(-0.68, -1.4) * mm});
            skLineSegment(sketch, "E3110", {"start": v(-0.68, -1.4) * mm, "end": v(-0.68, -1.39) * mm});
            skLineSegment(sketch, "E3111", {"start": v(-0.68, -1.39) * mm, "end": v(-0.68, -1.39) * mm});
            skLineSegment(sketch, "E3112", {"start": v(-0.7, -1.36) * mm, "end": v(-0.72, -1.4) * mm});
            skLineSegment(sketch, "E3113", {"start": v(-0.72, -1.4) * mm, "end": v(-0.74, -1.36) * mm});
            skLineSegment(sketch, "E3114", {"start": v(-0.75, -1.37) * mm, "end": v(-0.75, -1.38) * mm});
            skLineSegment(sketch, "E3115", {"start": v(-0.75, -1.38) * mm, "end": v(-0.79, -1.38) * mm});
            skLineSegment(sketch, "E3116", {"start": v(-0.79, -1.37) * mm, "end": v(-0.78, -1.36) * mm});
            skLineSegment(sketch, "E3117", {"start": v(-0.78, -1.36) * mm, "end": v(-0.76, -1.36) * mm});
            skLineSegment(sketch, "E3118", {"start": v(-0.76, -1.36) * mm, "end": v(-0.75, -1.37) * mm});
            skLineSegment(sketch, "E3119", {"start": v(-0.76, -1.4) * mm, "end": v(-0.78, -1.4) * mm});
            skLineSegment(sketch, "E3120", {"start": v(-0.78, -1.4) * mm, "end": v(-0.79, -1.39) * mm});
            skLineSegment(sketch, "E3121", {"start": v(-0.79, -1.39) * mm, "end": v(-0.79, -1.37) * mm});
            skLineSegment(sketch, "E3122", {"start": v(-0.8, -1.37) * mm, "end": v(-0.8, -1.36) * mm});
            skLineSegment(sketch, "E3123", {"start": v(-0.8, -1.36) * mm, "end": v(-0.81, -1.35) * mm});
            skLineSegment(sketch, "E3124", {"start": v(-0.81, -1.35) * mm, "end": v(-0.84, -1.35) * mm});
            skLineSegment(sketch, "E3125", {"start": v(-0.84, -1.35) * mm, "end": v(-0.84, -1.4) * mm});
            skLineSegment(sketch, "E3126", {"start": v(-0.84, -1.38) * mm, "end": v(-0.81, -1.38) * mm});
            skLineSegment(sketch, "E3127", {"start": v(-0.81, -1.38) * mm, "end": v(-0.8, -1.37) * mm});
            skLineSegment(sketch, "E3128", {"start": v(-0.82, -1.38) * mm, "end": v(-0.8, -1.4) * mm});
            skLineSegment(sketch, "E3129", {"start": v(-0.9, -1.37) * mm, "end": v(-0.94, -1.37) * mm});
            skLineSegment(sketch, "E3130", {"start": v(-1.01, -1.36) * mm, "end": v(-1.01, -1.4) * mm});
            skLineSegment(sketch, "E3131", {"start": v(-1.01, -1.4) * mm, "end": v(-1.02, -1.41) * mm});
            skLineSegment(sketch, "E3132", {"start": v(-1.02, -1.41) * mm, "end": v(-1.03, -1.41) * mm});
            skLineSegment(sketch, "E3133", {"start": v(-1.04, -1.4) * mm, "end": v(-1.01, -1.4) * mm});
            skLineSegment(sketch, "E3134", {"start": v(-1.04, -1.4) * mm, "end": v(-1.04, -1.39) * mm});
            skLineSegment(sketch, "E3135", {"start": v(-1.04, -1.39) * mm, "end": v(-1.04, -1.36) * mm});
            skLineSegment(sketch, "E3136", {"start": v(-1.06, -1.37) * mm, "end": v(-1.06, -1.4) * mm});
            skLineSegment(sketch, "E3137", {"start": v(-1.06, -1.4) * mm, "end": v(-1.09, -1.4) * mm});
            skLineSegment(sketch, "E3138", {"start": v(-1.09, -1.4) * mm, "end": v(-1.1, -1.39) * mm});
            skLineSegment(sketch, "E3139", {"start": v(-1.1, -1.39) * mm, "end": v(-1.09, -1.38) * mm});
            skLineSegment(sketch, "E3140", {"start": v(-1.09, -1.38) * mm, "end": v(-1.06, -1.38) * mm});
            skLineSegment(sketch, "E3141", {"start": v(-1.06, -1.37) * mm, "end": v(-1.07, -1.36) * mm});
            skLineSegment(sketch, "E3142", {"start": v(-1.07, -1.36) * mm, "end": v(-1.09, -1.36) * mm});
            skLineSegment(sketch, "E3143", {"start": v(-1.11, -1.36) * mm, "end": v(-1.11, -1.39) * mm});
            skLineSegment(sketch, "E3144", {"start": v(-1.11, -1.39) * mm, "end": v(-1.12, -1.4) * mm});
            skLineSegment(sketch, "E3145", {"start": v(-1.12, -1.4) * mm, "end": v(-1.13, -1.39) * mm});
            skLineSegment(sketch, "E3146", {"start": v(-1.13, -1.39) * mm, "end": v(-1.14, -1.4) * mm});
            skLineSegment(sketch, "E3147", {"start": v(-1.14, -1.4) * mm, "end": v(-1.15, -1.39) * mm});
            skLineSegment(sketch, "E3148", {"start": v(-1.15, -1.39) * mm, "end": v(-1.15, -1.36) * mm});
            skLineSegment(sketch, "E3149", {"start": v(-1.17, -1.37) * mm, "end": v(-1.17, -1.38) * mm});
            skLineSegment(sketch, "E3150", {"start": v(-1.17, -1.38) * mm, "end": v(-1.2, -1.38) * mm});
            skLineSegment(sketch, "E3151", {"start": v(-1.2, -1.37) * mm, "end": v(-1.2, -1.36) * mm});
            skLineSegment(sketch, "E3152", {"start": v(-1.2, -1.36) * mm, "end": v(-1.17, -1.36) * mm});
            skLineSegment(sketch, "E3153", {"start": v(-1.17, -1.36) * mm, "end": v(-1.17, -1.37) * mm});
            skLineSegment(sketch, "E3154", {"start": v(-1.17, -1.4) * mm, "end": v(-1.2, -1.4) * mm});
            skLineSegment(sketch, "E3155", {"start": v(-1.2, -1.4) * mm, "end": v(-1.2, -1.39) * mm});
            skLineSegment(sketch, "E3156", {"start": v(-1.2, -1.39) * mm, "end": v(-1.2, -1.37) * mm});
            skLineSegment(sketch, "E3157", {"start": v(-1.22, -1.36) * mm, "end": v(-1.23, -1.36) * mm});
            skLineSegment(sketch, "E3158", {"start": v(-1.23, -1.36) * mm, "end": v(-1.23, -1.39) * mm});
            skLineSegment(sketch, "E3159", {"start": v(-1.23, -1.39) * mm, "end": v(-1.22, -1.4) * mm});
            skLineSegment(sketch, "E3160", {"start": v(-1.25, -1.4) * mm, "end": v(-1.25, -1.37) * mm});
            skLineSegment(sketch, "E3161", {"start": v(-1.25, -1.37) * mm, "end": v(-1.26, -1.36) * mm});
            skLineSegment(sketch, "E3162", {"start": v(-1.26, -1.36) * mm, "end": v(-1.28, -1.36) * mm});
            skLineSegment(sketch, "E3163", {"start": v(-1.28, -1.38) * mm, "end": v(-1.25, -1.38) * mm});
            skLineSegment(sketch, "E3164", {"start": v(-1.25, -1.4) * mm, "end": v(-1.28, -1.4) * mm});
            skLineSegment(sketch, "E3165", {"start": v(-1.28, -1.4) * mm, "end": v(-1.29, -1.39) * mm});
            skLineSegment(sketch, "E3166", {"start": v(-1.29, -1.39) * mm, "end": v(-1.28, -1.38) * mm});
            skLineSegment(sketch, "E3167", {"start": v(-1.3, -1.37) * mm, "end": v(-1.32, -1.37) * mm});
            skLineSegment(sketch, "E3168", {"start": v(-1.3, -1.37) * mm, "end": v(-1.3, -1.39) * mm});
            skLineSegment(sketch, "E3169", {"start": v(-1.3, -1.39) * mm, "end": v(-1.31, -1.4) * mm});
            skLineSegment(sketch, "E3170", {"start": v(-1.31, -1.4) * mm, "end": v(-1.33, -1.4) * mm});
            skLineSegment(sketch, "E3171", {"start": v(-1.33, -1.4) * mm, "end": v(-1.34, -1.39) * mm});
            skLineSegment(sketch, "E3172", {"start": v(-1.34, -1.39) * mm, "end": v(-1.34, -1.36) * mm});
            skLineSegment(sketch, "E3173", {"start": v(-1.34, -1.36) * mm, "end": v(-1.33, -1.35) * mm});
            skLineSegment(sketch, "E3174", {"start": v(-1.33, -1.35) * mm, "end": v(-1.31, -1.35) * mm});
            skLineSegment(sketch, "E3175", {"start": v(-1.31, -1.35) * mm, "end": v(-1.3, -1.36) * mm});
            skLineSegment(sketch, "E3176", {"start": v(-1.4, -1.37) * mm, "end": v(-1.4, -1.4) * mm});
            skLineSegment(sketch, "E3177", {"start": v(-1.42, -1.4) * mm, "end": v(-1.42, -1.37) * mm});
            skLineSegment(sketch, "E3178", {"start": v(-1.42, -1.37) * mm, "end": v(-1.42, -1.36) * mm});
            skLineSegment(sketch, "E3179", {"start": v(-1.42, -1.36) * mm, "end": v(-1.4, -1.37) * mm});
            skLineSegment(sketch, "E3180", {"start": v(-1.42, -1.37) * mm, "end": v(-1.43, -1.36) * mm});
            skLineSegment(sketch, "E3181", {"start": v(-1.43, -1.36) * mm, "end": v(-1.44, -1.36) * mm});
            skLineSegment(sketch, "E3182", {"start": v(-1.44, -1.36) * mm, "end": v(-1.44, -1.4) * mm});
            skLineSegment(sketch, "E3183", {"start": v(-1.46, -1.36) * mm, "end": v(-1.47, -1.36) * mm});
            skLineSegment(sketch, "E3184", {"start": v(-1.47, -1.36) * mm, "end": v(-1.48, -1.38) * mm});
            skLineSegment(sketch, "E3185", {"start": v(-1.48, -1.36) * mm, "end": v(-1.48, -1.4) * mm});
            skLineSegment(sketch, "E3186", {"start": v(-1.5, -1.38) * mm, "end": v(-1.53, -1.38) * mm});
            skLineSegment(sketch, "E3187", {"start": v(-1.53, -1.37) * mm, "end": v(-1.53, -1.36) * mm});
            skLineSegment(sketch, "E3188", {"start": v(-1.53, -1.36) * mm, "end": v(-1.5, -1.36) * mm});
            skLineSegment(sketch, "E3189", {"start": v(-1.5, -1.36) * mm, "end": v(-1.5, -1.37) * mm});
            skLineSegment(sketch, "E3190", {"start": v(-1.5, -1.37) * mm, "end": v(-1.5, -1.38) * mm});
            skLineSegment(sketch, "E3191", {"start": v(-1.5, -1.4) * mm, "end": v(-1.53, -1.4) * mm});
            skLineSegment(sketch, "E3192", {"start": v(-1.53, -1.4) * mm, "end": v(-1.53, -1.39) * mm});
            skLineSegment(sketch, "E3193", {"start": v(-1.53, -1.39) * mm, "end": v(-1.53, -1.37) * mm});
            skLineSegment(sketch, "E3194", {"start": v(-1.55, -1.37) * mm, "end": v(-1.55, -1.4) * mm});
            skLineSegment(sketch, "E3195", {"start": v(-1.55, -1.37) * mm, "end": v(-1.56, -1.36) * mm});
            skLineSegment(sketch, "E3196", {"start": v(-1.56, -1.36) * mm, "end": v(-1.58, -1.36) * mm});
            skLineSegment(sketch, "E3197", {"start": v(-1.58, -1.36) * mm, "end": v(-1.59, -1.37) * mm});
            skLineSegment(sketch, "E3198", {"start": v(-1.6, -1.36) * mm, "end": v(-1.62, -1.36) * mm});
            skLineSegment(sketch, "E3199", {"start": v(-1.61, -1.36) * mm, "end": v(-1.61, -1.39) * mm});
            skLineSegment(sketch, "E3200", {"start": v(-1.61, -1.39) * mm, "end": v(-1.6, -1.4) * mm});
            skLineSegment(sketch, "E3201", {"start": v(-1.59, -1.4) * mm, "end": v(-1.59, -1.35) * mm});
            skLineSegment(sketch, "E3202", {"start": v(-1.64, -1.37) * mm, "end": v(-1.64, -1.4) * mm});
            skLineSegment(sketch, "E3203", {"start": v(-1.64, -1.37) * mm, "end": v(-1.65, -1.36) * mm});
            skLineSegment(sketch, "E3204", {"start": v(-1.65, -1.36) * mm, "end": v(-1.67, -1.36) * mm});
            skLineSegment(sketch, "E3205", {"start": v(-1.67, -1.36) * mm, "end": v(-1.67, -1.4) * mm});
            skLineSegment(sketch, "E3206", {"start": v(-1.7, -1.38) * mm, "end": v(-1.72, -1.38) * mm});
            skLineSegment(sketch, "E3207", {"start": v(-1.72, -1.37) * mm, "end": v(-1.72, -1.36) * mm});
            skLineSegment(sketch, "E3208", {"start": v(-1.72, -1.36) * mm, "end": v(-1.7, -1.36) * mm});
            skLineSegment(sketch, "E3209", {"start": v(-1.7, -1.36) * mm, "end": v(-1.7, -1.37) * mm});
            skLineSegment(sketch, "E3210", {"start": v(-1.7, -1.37) * mm, "end": v(-1.7, -1.38) * mm});
            skLineSegment(sketch, "E3211", {"start": v(-1.7, -1.4) * mm, "end": v(-1.72, -1.4) * mm});
            skLineSegment(sketch, "E3212", {"start": v(-1.72, -1.4) * mm, "end": v(-1.72, -1.39) * mm});
            skLineSegment(sketch, "E3213", {"start": v(-1.72, -1.39) * mm, "end": v(-1.72, -1.37) * mm});
            skLineSegment(sketch, "E3214", {"start": v(-1.74, -1.37) * mm, "end": v(-1.74, -1.39) * mm});
            skLineSegment(sketch, "E3215", {"start": v(-1.74, -1.39) * mm, "end": v(-1.75, -1.4) * mm});
            skLineSegment(sketch, "E3216", {"start": v(-1.75, -1.4) * mm, "end": v(-1.77, -1.4) * mm});
            skLineSegment(sketch, "E3217", {"start": v(-1.77, -1.41) * mm, "end": v(-1.77, -1.36) * mm});
            skLineSegment(sketch, "E3218", {"start": v(-1.77, -1.36) * mm, "end": v(-1.75, -1.36) * mm});
            skLineSegment(sketch, "E3219", {"start": v(-1.75, -1.36) * mm, "end": v(-1.74, -1.37) * mm});
            skLineSegment(sketch, "E3220", {"start": v(-1.8, -1.36) * mm, "end": v(-1.8, -1.35) * mm});
            skLineSegment(sketch, "E3221", {"start": v(-1.8, -1.35) * mm, "end": v(-1.82, -1.35) * mm});
            skLineSegment(sketch, "E3222", {"start": v(-1.82, -1.35) * mm, "end": v(-1.83, -1.36) * mm});
            skLineSegment(sketch, "E3223", {"start": v(-1.83, -1.36) * mm, "end": v(-1.83, -1.39) * mm});
            skLineSegment(sketch, "E3224", {"start": v(-1.83, -1.39) * mm, "end": v(-1.82, -1.4) * mm});
            skLineSegment(sketch, "E3225", {"start": v(-1.82, -1.4) * mm, "end": v(-1.8, -1.4) * mm});
            skLineSegment(sketch, "E3226", {"start": v(-1.8, -1.4) * mm, "end": v(-1.8, -1.39) * mm});
            skLineSegment(sketch, "E3227", {"start": v(-1.8, -1.39) * mm, "end": v(-1.8, -1.36) * mm});
            skLineSegment(sketch, "E3228", {"start": v(0.92, -1.36) * mm, "end": v(0.93, -1.35) * mm});
            skLineSegment(sketch, "E3229", {"start": v(0.93, -1.35) * mm, "end": v(0.95, -1.35) * mm});
            skLineSegment(sketch, "E3230", {"start": v(0.95, -1.35) * mm, "end": v(0.96, -1.36) * mm});
            skLineSegment(sketch, "E3231", {"start": v(0.96, -1.36) * mm, "end": v(0.96, -1.36) * mm});
            skLineSegment(sketch, "E3232", {"start": v(0.96, -1.36) * mm, "end": v(0.92, -1.4) * mm});
            skLineSegment(sketch, "E3233", {"start": v(0.92, -1.4) * mm, "end": v(0.96, -1.4) * mm});
            skLineSegment(sketch, "E3234", {"start": v(0.98, -1.39) * mm, "end": v(1, -1.36) * mm});
            skLineSegment(sketch, "E3235", {"start": v(1, -1.36) * mm, "end": v(1, -1.39) * mm});
            skLineSegment(sketch, "E3236", {"start": v(1, -1.39) * mm, "end": v(1, -1.4) * mm});
            skLineSegment(sketch, "E3237", {"start": v(1, -1.4) * mm, "end": v(0.98, -1.4) * mm});
            skLineSegment(sketch, "E3238", {"start": v(0.98, -1.4) * mm, "end": v(0.98, -1.39) * mm});
            skLineSegment(sketch, "E3239", {"start": v(0.98, -1.39) * mm, "end": v(0.98, -1.36) * mm});
            skLineSegment(sketch, "E3240", {"start": v(0.98, -1.36) * mm, "end": v(0.98, -1.35) * mm});
            skLineSegment(sketch, "E3241", {"start": v(0.98, -1.35) * mm, "end": v(1, -1.35) * mm});
            skLineSegment(sketch, "E3242", {"start": v(1, -1.35) * mm, "end": v(1, -1.36) * mm});
            skLineSegment(sketch, "E3243", {"start": v(1.03, -1.36) * mm, "end": v(1.04, -1.35) * mm});
            skLineSegment(sketch, "E3244", {"start": v(1.04, -1.35) * mm, "end": v(1.04, -1.4) * mm});
            skLineSegment(sketch, "E3245", {"start": v(1.06, -1.4) * mm, "end": v(1.03, -1.4) * mm});
            skLineSegment(sketch, "E3246", {"start": v(1.08, -1.4) * mm, "end": v(1.11, -1.36) * mm});
            skLineSegment(sketch, "E3247", {"start": v(1.11, -1.36) * mm, "end": v(1.11, -1.36) * mm});
            skLineSegment(sketch, "E3248", {"start": v(1.11, -1.36) * mm, "end": v(1.1, -1.35) * mm});
            skLineSegment(sketch, "E3249", {"start": v(1.1, -1.35) * mm, "end": v(1.09, -1.35) * mm});
            skLineSegment(sketch, "E3250", {"start": v(1.09, -1.35) * mm, "end": v(1.08, -1.36) * mm});
            skLineSegment(sketch, "E3251", {"start": v(1.08, -1.4) * mm, "end": v(1.11, -1.4) * mm});
            skLineSegment(sketch, "E3252", {"start": v(1.18, -1.37) * mm, "end": v(1.21, -1.37) * mm});
            skLineSegment(sketch, "E3253", {"start": v(1.28, -1.36) * mm, "end": v(1.3, -1.37) * mm});
            skLineSegment(sketch, "E3254", {"start": v(1.3, -1.37) * mm, "end": v(1.3, -1.37) * mm});
            skLineSegment(sketch, "E3255", {"start": v(1.3, -1.37) * mm, "end": v(1.32, -1.38) * mm});
            skLineSegment(sketch, "E3256", {"start": v(1.32, -1.38) * mm, "end": v(1.32, -1.39) * mm});
            skLineSegment(sketch, "E3257", {"start": v(1.32, -1.39) * mm, "end": v(1.3, -1.4) * mm});
            skLineSegment(sketch, "E3258", {"start": v(1.3, -1.4) * mm, "end": v(1.3, -1.4) * mm});
            skLineSegment(sketch, "E3259", {"start": v(1.3, -1.4) * mm, "end": v(1.28, -1.39) * mm});
            skLineSegment(sketch, "E3260", {"start": v(1.28, -1.36) * mm, "end": v(1.28, -1.36) * mm});
            skLineSegment(sketch, "E3261", {"start": v(1.28, -1.36) * mm, "end": v(1.3, -1.35) * mm});
            skLineSegment(sketch, "E3262", {"start": v(1.3, -1.35) * mm, "end": v(1.3, -1.35) * mm});
            skLineSegment(sketch, "E3263", {"start": v(1.3, -1.35) * mm, "end": v(1.32, -1.36) * mm});
            skLineSegment(sketch, "E3264", {"start": v(1.34, -1.37) * mm, "end": v(1.34, -1.39) * mm});
            skLineSegment(sketch, "E3265", {"start": v(1.34, -1.39) * mm, "end": v(1.34, -1.4) * mm});
            skLineSegment(sketch, "E3266", {"start": v(1.34, -1.4) * mm, "end": v(1.37, -1.4) * mm});
            skLineSegment(sketch, "E3267", {"start": v(1.39, -1.4) * mm, "end": v(1.39, -1.35) * mm});
            skLineSegment(sketch, "E3268", {"start": v(1.4, -1.36) * mm, "end": v(1.41, -1.36) * mm});
            skLineSegment(sketch, "E3269", {"start": v(1.41, -1.36) * mm, "end": v(1.42, -1.37) * mm});
            skLineSegment(sketch, "E3270", {"start": v(1.42, -1.37) * mm, "end": v(1.42, -1.4) * mm});
            skLineSegment(sketch, "E3271", {"start": v(1.44, -1.39) * mm, "end": v(1.45, -1.4) * mm});
            skLineSegment(sketch, "E3272", {"start": v(1.45, -1.4) * mm, "end": v(1.46, -1.4) * mm});
            skLineSegment(sketch, "E3273", {"start": v(1.47, -1.38) * mm, "end": v(1.44, -1.38) * mm});
            skLineSegment(sketch, "E3274", {"start": v(1.44, -1.37) * mm, "end": v(1.45, -1.36) * mm});
            skLineSegment(sketch, "E3275", {"start": v(1.45, -1.36) * mm, "end": v(1.46, -1.36) * mm});
            skLineSegment(sketch, "E3276", {"start": v(1.46, -1.36) * mm, "end": v(1.47, -1.37) * mm});
            skLineSegment(sketch, "E3277", {"start": v(1.47, -1.37) * mm, "end": v(1.47, -1.38) * mm});
            skLineSegment(sketch, "E3278", {"start": v(1.5, -1.4) * mm, "end": v(1.5, -1.4) * mm});
            skLineSegment(sketch, "E3279", {"start": v(1.5, -1.4) * mm, "end": v(1.5, -1.35) * mm});
            skLineSegment(sketch, "E3280", {"start": v(1.5, -1.35) * mm, "end": v(1.5, -1.35) * mm});
            skLineSegment(sketch, "E3281", {"start": v(1.53, -1.36) * mm, "end": v(1.54, -1.36) * mm});
            skLineSegment(sketch, "E3282", {"start": v(1.53, -1.36) * mm, "end": v(1.53, -1.39) * mm});
            skLineSegment(sketch, "E3283", {"start": v(1.53, -1.39) * mm, "end": v(1.54, -1.4) * mm});
            skLineSegment(sketch, "E3284", {"start": v(1.56, -1.39) * mm, "end": v(1.57, -1.4) * mm});
            skLineSegment(sketch, "E3285", {"start": v(1.57, -1.4) * mm, "end": v(1.58, -1.4) * mm});
            skLineSegment(sketch, "E3286", {"start": v(1.6, -1.38) * mm, "end": v(1.56, -1.38) * mm});
            skLineSegment(sketch, "E3287", {"start": v(1.56, -1.37) * mm, "end": v(1.57, -1.36) * mm});
            skLineSegment(sketch, "E3288", {"start": v(1.57, -1.36) * mm, "end": v(1.58, -1.36) * mm});
            skLineSegment(sketch, "E3289", {"start": v(1.58, -1.36) * mm, "end": v(1.6, -1.37) * mm});
            skLineSegment(sketch, "E3290", {"start": v(1.6, -1.37) * mm, "end": v(1.6, -1.38) * mm});
            skLineSegment(sketch, "E3291", {"start": v(1.56, -1.39) * mm, "end": v(1.56, -1.37) * mm});
            skLineSegment(sketch, "E3292", {"start": v(1.66, -1.37) * mm, "end": v(1.69, -1.37) * mm});
            skLineSegment(sketch, "E3293", {"start": v(1.69, -1.37) * mm, "end": v(1.7, -1.38) * mm});
            skLineSegment(sketch, "E3294", {"start": v(1.7, -1.38) * mm, "end": v(1.7, -1.39) * mm});
            skLineSegment(sketch, "E3295", {"start": v(1.7, -1.39) * mm, "end": v(1.69, -1.4) * mm});
            skLineSegment(sketch, "E3296", {"start": v(1.69, -1.4) * mm, "end": v(1.66, -1.4) * mm});
            skLineSegment(sketch, "E3297", {"start": v(1.66, -1.4) * mm, "end": v(1.66, -1.35) * mm});
            skLineSegment(sketch, "E3298", {"start": v(1.66, -1.35) * mm, "end": v(1.69, -1.35) * mm});
            skLineSegment(sketch, "E3299", {"start": v(1.69, -1.35) * mm, "end": v(1.7, -1.36) * mm});
            skLineSegment(sketch, "E3300", {"start": v(1.7, -1.36) * mm, "end": v(1.7, -1.36) * mm});
            skLineSegment(sketch, "E3301", {"start": v(1.7, -1.36) * mm, "end": v(1.69, -1.37) * mm});
            skLineSegment(sketch, "E3302", {"start": v(1.71, -1.36) * mm, "end": v(1.71, -1.4) * mm});
            skLineSegment(sketch, "E3303", {"start": v(1.71, -1.38) * mm, "end": v(1.73, -1.36) * mm});
            skLineSegment(sketch, "E3304", {"start": v(1.73, -1.36) * mm, "end": v(1.74, -1.36) * mm});
            skLineSegment(sketch, "E3305", {"start": v(1.76, -1.37) * mm, "end": v(1.76, -1.39) * mm});
            skLineSegment(sketch, "E3306", {"start": v(1.76, -1.39) * mm, "end": v(1.77, -1.4) * mm});
            skLineSegment(sketch, "E3307", {"start": v(1.77, -1.4) * mm, "end": v(1.78, -1.4) * mm});
            skLineSegment(sketch, "E3308", {"start": v(1.78, -1.4) * mm, "end": v(1.79, -1.39) * mm});
            skLineSegment(sketch, "E3309", {"start": v(1.79, -1.39) * mm, "end": v(1.79, -1.37) * mm});
            skLineSegment(sketch, "E3310", {"start": v(1.79, -1.37) * mm, "end": v(1.78, -1.36) * mm});
            skLineSegment(sketch, "E3311", {"start": v(1.78, -1.36) * mm, "end": v(1.77, -1.36) * mm});
            skLineSegment(sketch, "E3312", {"start": v(1.77, -1.36) * mm, "end": v(1.76, -1.37) * mm});
            skLineSegment(sketch, "E3313", {"start": v(1.8, -1.36) * mm, "end": v(1.8, -1.4) * mm});
            skLineSegment(sketch, "E3314", {"start": v(1.84, -1.4) * mm, "end": v(1.84, -1.37) * mm});
            skLineSegment(sketch, "E3315", {"start": v(1.84, -1.37) * mm, "end": v(1.83, -1.36) * mm});
            skLineSegment(sketch, "E3316", {"start": v(1.83, -1.36) * mm, "end": v(1.8, -1.36) * mm});
            skLineSegment(sketch, "E3317", {"start": v(1.44, -1.37) * mm, "end": v(1.44, -1.39) * mm});
            skLineSegment(sketch, "E3318", {"start": v(1.4, -1.36) * mm, "end": v(1.39, -1.37) * mm});
            skLineSegment(sketch, "E3319", {"start": v(1.37, -1.36) * mm, "end": v(1.34, -1.36) * mm});
            skLineSegment(sketch, "E3320", {"start": v(1.34, -1.36) * mm, "end": v(1.34, -1.37) * mm});
            skLineSegment(sketch, "E3321", {"start": v(0.82, -1.37) * mm, "end": v(0.82, -1.37) * mm});
            skLineSegment(sketch, "E3322", {"start": v(0.82, -1.37) * mm, "end": v(0.82, -1.36) * mm});
            skLineSegment(sketch, "E3323", {"start": v(0.82, -1.36) * mm, "end": v(0.82, -1.36) * mm});
            skLineSegment(sketch, "E3324", {"start": v(0.82, -1.36) * mm, "end": v(0.82, -1.35) * mm});
            skLineSegment(sketch, "E3325", {"start": v(0.82, -1.35) * mm, "end": v(0.83, -1.35) * mm});
            skLineSegment(sketch, "E3326", {"start": v(0.83, -1.35) * mm, "end": v(0.83, -1.35) * mm});
            skLineSegment(sketch, "E3327", {"start": v(0.83, -1.35) * mm, "end": v(0.83, -1.34) * mm});
            skLineSegment(sketch, "E3328", {"start": v(0.83, -1.34) * mm, "end": v(0.83, -1.34) * mm});
            skLineSegment(sketch, "E3329", {"start": v(0.83, -1.34) * mm, "end": v(0.84, -1.34) * mm});
            skLineSegment(sketch, "E3330", {"start": v(0.84, -1.34) * mm, "end": v(0.84, -1.34) * mm});
            skLineSegment(sketch, "E3331", {"start": v(0.84, -1.34) * mm, "end": v(0.84, -1.33) * mm});
            skLineSegment(sketch, "E3332", {"start": v(0.84, -1.33) * mm, "end": v(0.85, -1.33) * mm});
            skLineSegment(sketch, "E3333", {"start": v(0.85, -1.33) * mm, "end": v(0.85, -1.33) * mm});
            skLineSegment(sketch, "E3334", {"start": v(0.85, -1.33) * mm, "end": v(0.86, -1.33) * mm});
            skLineSegment(sketch, "E3335", {"start": v(0.86, -1.33) * mm, "end": v(0.86, -1.33) * mm});
            skLineSegment(sketch, "E3336", {"start": v(0.86, -1.33) * mm, "end": v(0.87, -1.33) * mm});
            skLineSegment(sketch, "E3337", {"start": v(0.87, -1.33) * mm, "end": v(0.87, -1.33) * mm});
            skLineSegment(sketch, "E3338", {"start": v(0.87, -1.33) * mm, "end": v(0.88, -1.33) * mm});
            skLineSegment(sketch, "E3339", {"start": v(0.88, -1.33) * mm, "end": v(0.88, -1.34) * mm});
            skLineSegment(sketch, "E3340", {"start": v(0.88, -1.34) * mm, "end": v(0.88, -1.34) * mm});
            skLineSegment(sketch, "E3341", {"start": v(0.88, -1.34) * mm, "end": v(0.89, -1.34) * mm});
            skLineSegment(sketch, "E3342", {"start": v(0.89, -1.34) * mm, "end": v(0.89, -1.34) * mm});
            skLineSegment(sketch, "E3343", {"start": v(0.89, -1.34) * mm, "end": v(0.9, -1.35) * mm});
            skLineSegment(sketch, "E3344", {"start": v(0.9, -1.35) * mm, "end": v(0.9, -1.35) * mm});
            skLineSegment(sketch, "E3345", {"start": v(0.9, -1.35) * mm, "end": v(0.9, -1.36) * mm});
            skLineSegment(sketch, "E3346", {"start": v(0.9, -1.36) * mm, "end": v(0.9, -1.36) * mm});
            skLineSegment(sketch, "E3347", {"start": v(0.9, -1.36) * mm, "end": v(0.9, -1.37) * mm});
            skLineSegment(sketch, "E3348", {"start": v(0.9, -1.37) * mm, "end": v(0.9, -1.37) * mm});
            skLineSegment(sketch, "E3349", {"start": v(0.9, -1.37) * mm, "end": v(0.9, -1.38) * mm});
            skLineSegment(sketch, "E3350", {"start": v(0.9, -1.38) * mm, "end": v(0.9, -1.38) * mm});
            skLineSegment(sketch, "E3351", {"start": v(0.9, -1.38) * mm, "end": v(0.9, -1.39) * mm});
            skLineSegment(sketch, "E3352", {"start": v(0.9, -1.39) * mm, "end": v(0.9, -1.4) * mm});
            skLineSegment(sketch, "E3353", {"start": v(0.9, -1.4) * mm, "end": v(0.9, -1.4) * mm});
            skLineSegment(sketch, "E3354", {"start": v(0.9, -1.4) * mm, "end": v(0.89, -1.4) * mm});
            skLineSegment(sketch, "E3355", {"start": v(0.89, -1.4) * mm, "end": v(0.89, -1.4) * mm});
            skLineSegment(sketch, "E3356", {"start": v(0.89, -1.4) * mm, "end": v(0.88, -1.4) * mm});
            skLineSegment(sketch, "E3357", {"start": v(0.88, -1.4) * mm, "end": v(0.88, -1.4) * mm});
            skLineSegment(sketch, "E3358", {"start": v(0.88, -1.4) * mm, "end": v(0.87, -1.4) * mm});
            skLineSegment(sketch, "E3359", {"start": v(0.87, -1.4) * mm, "end": v(0.87, -1.4) * mm});
            skLineSegment(sketch, "E3360", {"start": v(0.87, -1.4) * mm, "end": v(0.86, -1.4) * mm});
            skLineSegment(sketch, "E3361", {"start": v(0.86, -1.4) * mm, "end": v(0.86, -1.4) * mm});
            skLineSegment(sketch, "E3362", {"start": v(0.86, -1.4) * mm, "end": v(0.85, -1.4) * mm});
            skLineSegment(sketch, "E3363", {"start": v(0.85, -1.4) * mm, "end": v(0.85, -1.4) * mm});
            skLineSegment(sketch, "E3364", {"start": v(0.85, -1.4) * mm, "end": v(0.84, -1.4) * mm});
            skLineSegment(sketch, "E3365", {"start": v(0.84, -1.4) * mm, "end": v(0.84, -1.4) * mm});
            skLineSegment(sketch, "E3366", {"start": v(0.84, -1.4) * mm, "end": v(0.83, -1.4) * mm});
            skLineSegment(sketch, "E3367", {"start": v(0.83, -1.4) * mm, "end": v(0.83, -1.4) * mm});
            skLineSegment(sketch, "E3368", {"start": v(0.83, -1.4) * mm, "end": v(0.83, -1.39) * mm});
            skLineSegment(sketch, "E3369", {"start": v(0.83, -1.39) * mm, "end": v(0.82, -1.39) * mm});
            skLineSegment(sketch, "E3370", {"start": v(0.82, -1.39) * mm, "end": v(0.82, -1.38) * mm});
            skLineSegment(sketch, "E3371", {"start": v(0.82, -1.38) * mm, "end": v(0.82, -1.38) * mm});
            skLineSegment(sketch, "E3372", {"start": v(0.82, -1.38) * mm, "end": v(0.82, -1.37) * mm});
            skLineSegment(sketch, "E3373", {"start": v(0.4, 1.25) * mm, "end": v(0.4, 1.4) * mm});
            skLineSegment(sketch, "E3374", {"start": v(-0.1, 1.4) * mm, "end": v(-0.1, 1.25) * mm});
            skLineSegment(sketch, "E3375", {"start": v(-0.4, 1.25) * mm, "end": v(-0.4, 1.4) * mm});
            skLineSegment(sketch, "E3376", {"start": v(-0.6, 1.4) * mm, "end": v(-0.6, 1.25) * mm});
            skLineSegment(sketch, "E3377", {"start": v(-0.45, 1.26) * mm, "end": v(-0.43, 1.27) * mm});
            skLineSegment(sketch, "E3378", {"start": v(-0.43, 1.27) * mm, "end": v(-0.43, 1.23) * mm});
            skLineSegment(sketch, "E3379", {"start": v(-0.45, 1.23) * mm, "end": v(-0.42, 1.23) * mm});
            skLineSegment(sketch, "E3380", {"start": v(-0.07, 1.17) * mm, "end": v(-0.06, 1.18) * mm});
            skLineSegment(sketch, "E3381", {"start": v(-0.06, 1.18) * mm, "end": v(-0.06, 1.14) * mm});
            skLineSegment(sketch, "E3382", {"start": v(-0.07, 1.14) * mm, "end": v(-0.04, 1.14) * mm});
            skLineSegment(sketch, "E3383", {"start": v(0.33, 1.32) * mm, "end": v(0.34, 1.32) * mm});
            skLineSegment(sketch, "E3384", {"start": v(0.34, 1.32) * mm, "end": v(0.35, 1.32) * mm});
            skLineSegment(sketch, "E3385", {"start": v(0.35, 1.32) * mm, "end": v(0.36, 1.32) * mm});
            skLineSegment(sketch, "E3386", {"start": v(0.36, 1.32) * mm, "end": v(0.36, 1.34) * mm});
            skLineSegment(sketch, "E3387", {"start": v(0.36, 1.34) * mm, "end": v(0.35, 1.35) * mm});
            skLineSegment(sketch, "E3388", {"start": v(0.35, 1.35) * mm, "end": v(0.34, 1.35) * mm});
            skLineSegment(sketch, "E3389", {"start": v(0.34, 1.35) * mm, "end": v(0.33, 1.34) * mm});
            skLineSegment(sketch, "E3390", {"start": v(0.33, 1.34) * mm, "end": v(0.33, 1.36) * mm});
            skLineSegment(sketch, "E3391", {"start": v(0.33, 1.36) * mm, "end": v(0.36, 1.36) * mm});
            skLineSegment(sketch, "E3392", {"start": v(-0.85, 1.2) * mm, "end": v(-0.9, 1.2) * mm});
            skLineSegment(sketch, "E3393", {"start": v(-0.9, 1.2) * mm, "end": v(-0.9, 1.2) * mm});
            skLineSegment(sketch, "E3394", {"start": v(-0.9, 1.2) * mm, "end": v(-1, 1.2) * mm});
            skLineSegment(sketch, "E3395", {"start": v(-1, 1.2) * mm, "end": v(-1, 1.2) * mm});
            skLineSegment(sketch, "E3396", {"start": v(-1, 1.2) * mm, "end": v(-1.05, 1.2) * mm});
            skLineSegment(sketch, "E3397", {"start": v(-1.03, 1.26) * mm, "end": v(-0.87, 1.26) * mm});
            skLineSegment(sketch, "E3398", {"start": v(-0.87, 1.26) * mm, "end": v(-0.86, 1.26) * mm});
            skLineSegment(sketch, "E3399", {"start": v(-0.86, 1.26) * mm, "end": v(-0.86, 1.26) * mm});
            skLineSegment(sketch, "E3400", {"start": v(-0.86, 1.26) * mm, "end": v(-0.86, 1.25) * mm});
            skLineSegment(sketch, "E3401", {"start": v(-0.86, 1.25) * mm, "end": v(-0.85, 1.24) * mm});
            skLineSegment(sketch, "E3402", {"start": v(-1.04, 1.24) * mm, "end": v(-1.05, 1.24) * mm});
            skLineSegment(sketch, "E3403", {"start": v(-1.05, 1.24) * mm, "end": v(-1.05, 1.23) * mm});
            skLineSegment(sketch, "E3404", {"start": v(-1.05, 1.23) * mm, "end": v(-1.05, 1.23) * mm});
            skLineSegment(sketch, "E3405", {"start": v(-1.05, 1.23) * mm, "end": v(-1.05, 1.22) * mm});
            skLineSegment(sketch, "E3406", {"start": v(-1.05, 1.22) * mm, "end": v(-1.05, 1.22) * mm});
            skLineSegment(sketch, "E3407", {"start": v(-1.05, 1.22) * mm, "end": v(-1.05, 1.2) * mm});
            skLineSegment(sketch, "E3408", {"start": v(-1.05, 1.2) * mm, "end": v(-1.05, 1.2) * mm});
            skLineSegment(sketch, "E3409", {"start": v(-1.05, 1.2) * mm, "end": v(-1.05, 1.18) * mm});
            skLineSegment(sketch, "E3410", {"start": v(-1.05, 1.18) * mm, "end": v(-1.05, 1.18) * mm});
            skLineSegment(sketch, "E3411", {"start": v(-1.05, 1.18) * mm, "end": v(-1.05, 1.17) * mm});
            skLineSegment(sketch, "E3412", {"start": v(-1.05, 1.17) * mm, "end": v(-1.05, 1.17) * mm});
            skLineSegment(sketch, "E3413", {"start": v(-1.05, 1.17) * mm, "end": v(-1.05, 1.16) * mm});
            skLineSegment(sketch, "E3414", {"start": v(-1.05, 1.16) * mm, "end": v(-1.04, 1.16) * mm});
            skLineSegment(sketch, "E3415", {"start": v(-1.05, 1.24) * mm, "end": v(-1.04, 1.25) * mm});
            skLineSegment(sketch, "E3416", {"start": v(-1.04, 1.25) * mm, "end": v(-1.04, 1.25) * mm});
            skLineSegment(sketch, "E3417", {"start": v(-1.04, 1.25) * mm, "end": v(-1.04, 1.26) * mm});
            skLineSegment(sketch, "E3418", {"start": v(-1.04, 1.26) * mm, "end": v(-1.03, 1.26) * mm});
            skLineSegment(sketch, "E3419", {"start": v(-0.85, 1.24) * mm, "end": v(-0.85, 1.24) * mm});
            skLineSegment(sketch, "E3420", {"start": v(-0.85, 1.24) * mm, "end": v(-0.85, 1.23) * mm});
            skLineSegment(sketch, "E3421", {"start": v(-0.85, 1.23) * mm, "end": v(-0.85, 1.23) * mm});
            skLineSegment(sketch, "E3422", {"start": v(-0.85, 1.23) * mm, "end": v(-0.85, 1.22) * mm});
            skLineSegment(sketch, "E3423", {"start": v(-0.85, 1.22) * mm, "end": v(-0.85, 1.22) * mm});
            skLineSegment(sketch, "E3424", {"start": v(-0.85, 1.22) * mm, "end": v(-0.85, 1.2) * mm});
            skLineSegment(sketch, "E3425", {"start": v(-0.85, 1.2) * mm, "end": v(-0.84, 1.2) * mm});
            skLineSegment(sketch, "E3426", {"start": v(-0.84, 1.2) * mm, "end": v(-0.84, 1.2) * mm});
            skLineSegment(sketch, "E3427", {"start": v(-0.84, 1.2) * mm, "end": v(-0.85, 1.2) * mm});
            skLineSegment(sketch, "E3428", {"start": v(-0.85, 1.2) * mm, "end": v(-0.85, 1.18) * mm});
            skLineSegment(sketch, "E3429", {"start": v(-0.85, 1.18) * mm, "end": v(-0.85, 1.18) * mm});
            skLineSegment(sketch, "E3430", {"start": v(-0.85, 1.18) * mm, "end": v(-0.85, 1.17) * mm});
            skLineSegment(sketch, "E3431", {"start": v(-0.85, 1.17) * mm, "end": v(-0.85, 1.17) * mm});
            skLineSegment(sketch, "E3432", {"start": v(-0.85, 1.17) * mm, "end": v(-0.85, 1.16) * mm});
            skLineSegment(sketch, "E3433", {"start": v(-0.85, 1.16) * mm, "end": v(-0.85, 1.16) * mm});
            skLineSegment(sketch, "E3434", {"start": v(-0.85, 1.16) * mm, "end": v(-0.86, 1.15) * mm});
            skLineSegment(sketch, "E3435", {"start": v(-0.86, 1.15) * mm, "end": v(-0.86, 1.14) * mm});
            skLineSegment(sketch, "E3436", {"start": v(-0.86, 1.14) * mm, "end": v(-0.86, 1.14) * mm});
            skLineSegment(sketch, "E3437", {"start": v(-0.86, 1.14) * mm, "end": v(-0.87, 1.13) * mm});
            skLineSegment(sketch, "E3438", {"start": v(-0.87, 1.13) * mm, "end": v(-0.87, 1.13) * mm});
            skLineSegment(sketch, "E3439", {"start": v(-0.87, 1.13) * mm, "end": v(-0.88, 1.12) * mm});
            skLineSegment(sketch, "E3440", {"start": v(-0.88, 1.12) * mm, "end": v(-0.88, 1.12) * mm});
            skLineSegment(sketch, "E3441", {"start": v(-0.88, 1.12) * mm, "end": v(-0.89, 1.12) * mm});
            skLineSegment(sketch, "E3442", {"start": v(-0.89, 1.12) * mm, "end": v(-0.9, 1.11) * mm});
            skLineSegment(sketch, "E3443", {"start": v(-0.9, 1.11) * mm, "end": v(-0.9, 1.1) * mm});
            skLineSegment(sketch, "E3444", {"start": v(-0.9, 1.1) * mm, "end": v(-0.9, 1.1) * mm});
            skLineSegment(sketch, "E3445", {"start": v(-0.9, 1.1) * mm, "end": v(-0.92, 1.1) * mm});
            skLineSegment(sketch, "E3446", {"start": v(-0.92, 1.1) * mm, "end": v(-0.92, 1.1) * mm});
            skLineSegment(sketch, "E3447", {"start": v(-0.92, 1.1) * mm, "end": v(-0.93, 1.1) * mm});
            skLineSegment(sketch, "E3448", {"start": v(-0.93, 1.1) * mm, "end": v(-0.93, 1.1) * mm});
            skLineSegment(sketch, "E3449", {"start": v(-0.93, 1.1) * mm, "end": v(-0.94, 1.1) * mm});
            skLineSegment(sketch, "E3450", {"start": v(-0.94, 1.1) * mm, "end": v(-0.95, 1.1) * mm});
            skLineSegment(sketch, "E3451", {"start": v(-0.95, 1.1) * mm, "end": v(-0.95, 1.1) * mm});
            skLineSegment(sketch, "E3452", {"start": v(-0.95, 1.1) * mm, "end": v(-0.96, 1.1) * mm});
            skLineSegment(sketch, "E3453", {"start": v(-0.96, 1.1) * mm, "end": v(-0.97, 1.1) * mm});
            skLineSegment(sketch, "E3454", {"start": v(-0.97, 1.1) * mm, "end": v(-0.97, 1.1) * mm});
            skLineSegment(sketch, "E3455", {"start": v(-0.97, 1.1) * mm, "end": v(-0.98, 1.1) * mm});
            skLineSegment(sketch, "E3456", {"start": v(-0.98, 1.1) * mm, "end": v(-0.98, 1.1) * mm});
            skLineSegment(sketch, "E3457", {"start": v(-0.98, 1.1) * mm, "end": v(-1, 1.1) * mm});
            skLineSegment(sketch, "E3458", {"start": v(-1, 1.1) * mm, "end": v(-1, 1.1) * mm});
            skLineSegment(sketch, "E3459", {"start": v(-1, 1.1) * mm, "end": v(-1, 1.11) * mm});
            skLineSegment(sketch, "E3460", {"start": v(-1, 1.11) * mm, "end": v(-1.01, 1.12) * mm});
            skLineSegment(sketch, "E3461", {"start": v(-1.01, 1.12) * mm, "end": v(-1.02, 1.12) * mm});
            skLineSegment(sketch, "E3462", {"start": v(-1.02, 1.12) * mm, "end": v(-1.02, 1.12) * mm});
            skLineSegment(sketch, "E3463", {"start": v(-1.02, 1.12) * mm, "end": v(-1.03, 1.13) * mm});
            skLineSegment(sketch, "E3464", {"start": v(-1.03, 1.13) * mm, "end": v(-1.03, 1.13) * mm});
            skLineSegment(sketch, "E3465", {"start": v(-1.03, 1.13) * mm, "end": v(-1.04, 1.14) * mm});
            skLineSegment(sketch, "E3466", {"start": v(-1.04, 1.14) * mm, "end": v(-1.04, 1.14) * mm});
            skLineSegment(sketch, "E3467", {"start": v(-1.04, 1.14) * mm, "end": v(-1.04, 1.15) * mm});
            skLineSegment(sketch, "E3468", {"start": v(-1.04, 1.15) * mm, "end": v(-1.04, 1.16) * mm});
            skLineSegment(sketch, "E3469", {"start": v(-1.63, 0.4) * mm, "end": v(-1.63, 0.38) * mm});
            skLineSegment(sketch, "E3470", {"start": v(-1.63, 0.38) * mm, "end": v(-1.66, 0.4) * mm});
            skLineSegment(sketch, "E3471", {"start": v(-1.66, 0.4) * mm, "end": v(-1.66, 0.4) * mm});
            skLineSegment(sketch, "E3472", {"start": v(-1.66, 0.4) * mm, "end": v(-1.67, 0.4) * mm});
            skLineSegment(sketch, "E3473", {"start": v(-1.67, 0.4) * mm, "end": v(-1.67, 0.39) * mm});
            skLineSegment(sketch, "E3474", {"start": v(-1.67, 0.39) * mm, "end": v(-1.66, 0.38) * mm});
            skLineSegment(sketch, "E3475", {"start": v(-1.63, 0.2) * mm, "end": v(-1.63, 0.18) * mm});
            skLineSegment(sketch, "E3476", {"start": v(-1.63, 0.2) * mm, "end": v(-1.67, 0.2) * mm});
            skLineSegment(sketch, "E3477", {"start": v(-1.67, 0.2) * mm, "end": v(-1.66, 0.18) * mm});
            skLineSegment(sketch, "E3478", {"start": v(-1.66, -0.3) * mm, "end": v(-1.66, -0.3) * mm});
            skLineSegment(sketch, "E3479", {"start": v(-1.66, -0.3) * mm, "end": v(-1.67, -0.3) * mm});
            skLineSegment(sketch, "E3480", {"start": v(-1.67, -0.3) * mm, "end": v(-1.67, -0.31) * mm});
            skLineSegment(sketch, "E3481", {"start": v(-1.67, -0.31) * mm, "end": v(-1.66, -0.32) * mm});
            skLineSegment(sketch, "E3482", {"start": v(-1.66, -0.3) * mm, "end": v(-1.63, -0.32) * mm});
            skLineSegment(sketch, "E3483", {"start": v(-1.63, -0.32) * mm, "end": v(-1.63, -0.3) * mm});
            skLineSegment(sketch, "E3484", {"start": v(-1.63, -0.5) * mm, "end": v(-1.63, -0.52) * mm});
            skLineSegment(sketch, "E3485", {"start": v(-1.63, -0.5) * mm, "end": v(-1.67, -0.5) * mm});
            skLineSegment(sketch, "E3486", {"start": v(-1.67, -0.5) * mm, "end": v(-1.66, -0.52) * mm});
            skLineSegment(sketch, "E3487", {"start": v(-0.51, -0.13) * mm, "end": v(-0.51, 0.03) * mm});
            skLineSegment(sketch, "E3488", {"start": v(-0.46, 0.05) * mm, "end": v(-0.46, 0) * mm});
            skLineSegment(sketch, "E3489", {"start": v(-0.46, 0) * mm, "end": v(-0.46, 0) * mm});
            skLineSegment(sketch, "E3490", {"start": v(-0.46, 0) * mm, "end": v(-0.46, -0.1) * mm});
            skLineSegment(sketch, "E3491", {"start": v(-0.46, -0.1) * mm, "end": v(-0.46, -0.1) * mm});
            skLineSegment(sketch, "E3492", {"start": v(-0.46, -0.1) * mm, "end": v(-0.46, -0.15) * mm});
            skLineSegment(sketch, "E3493", {"start": v(-0.5, -0.15) * mm, "end": v(-0.5, -0.14) * mm});
            skLineSegment(sketch, "E3494", {"start": v(-0.5, -0.14) * mm, "end": v(-0.5, -0.14) * mm});
            skLineSegment(sketch, "E3495", {"start": v(-0.5, -0.14) * mm, "end": v(-0.51, -0.14) * mm});
            skLineSegment(sketch, "E3496", {"start": v(-0.51, -0.14) * mm, "end": v(-0.51, -0.13) * mm});
            skLineSegment(sketch, "E3497", {"start": v(-0.5, -0.15) * mm, "end": v(-0.49, -0.15) * mm});
            skLineSegment(sketch, "E3498", {"start": v(-0.49, -0.15) * mm, "end": v(-0.48, -0.15) * mm});
            skLineSegment(sketch, "E3499", {"start": v(-0.48, -0.15) * mm, "end": v(-0.48, -0.15) * mm});
            skLineSegment(sketch, "E3500", {"start": v(-0.48, -0.15) * mm, "end": v(-0.47, -0.15) * mm});
            skLineSegment(sketch, "E3501", {"start": v(-0.47, -0.15) * mm, "end": v(-0.47, -0.15) * mm});
            skLineSegment(sketch, "E3502", {"start": v(-0.47, -0.15) * mm, "end": v(-0.46, -0.15) * mm});
            skLineSegment(sketch, "E3503", {"start": v(-0.46, -0.15) * mm, "end": v(-0.45, -0.16) * mm});
            skLineSegment(sketch, "E3504", {"start": v(-0.45, -0.16) * mm, "end": v(-0.45, -0.16) * mm});
            skLineSegment(sketch, "E3505", {"start": v(-0.45, -0.16) * mm, "end": v(-0.44, -0.15) * mm});
            skLineSegment(sketch, "E3506", {"start": v(-0.44, -0.15) * mm, "end": v(-0.43, -0.15) * mm});
            skLineSegment(sketch, "E3507", {"start": v(-0.43, -0.15) * mm, "end": v(-0.43, -0.15) * mm});
            skLineSegment(sketch, "E3508", {"start": v(-0.43, -0.15) * mm, "end": v(-0.42, -0.15) * mm});
            skLineSegment(sketch, "E3509", {"start": v(-0.42, -0.15) * mm, "end": v(-0.42, -0.15) * mm});
            skLineSegment(sketch, "E3510", {"start": v(-0.42, -0.15) * mm, "end": v(-0.41, -0.15) * mm});
            skLineSegment(sketch, "E3511", {"start": v(-0.41, -0.15) * mm, "end": v(-0.4, -0.15) * mm});
            skLineSegment(sketch, "E3512", {"start": v(-0.4, 0.04) * mm, "end": v(-0.41, 0.05) * mm});
            skLineSegment(sketch, "E3513", {"start": v(-0.41, 0.05) * mm, "end": v(-0.42, 0.05) * mm});
            skLineSegment(sketch, "E3514", {"start": v(-0.42, 0.05) * mm, "end": v(-0.42, 0.05) * mm});
            skLineSegment(sketch, "E3515", {"start": v(-0.42, 0.05) * mm, "end": v(-0.43, 0.05) * mm});
            skLineSegment(sketch, "E3516", {"start": v(-0.43, 0.05) * mm, "end": v(-0.43, 0.05) * mm});
            skLineSegment(sketch, "E3517", {"start": v(-0.43, 0.05) * mm, "end": v(-0.44, 0.05) * mm});
            skLineSegment(sketch, "E3518", {"start": v(-0.44, 0.05) * mm, "end": v(-0.45, 0.05) * mm});
            skLineSegment(sketch, "E3519", {"start": v(-0.45, 0.05) * mm, "end": v(-0.45, 0.05) * mm});
            skLineSegment(sketch, "E3520", {"start": v(-0.45, 0.05) * mm, "end": v(-0.46, 0.05) * mm});
            skLineSegment(sketch, "E3521", {"start": v(-0.46, 0.05) * mm, "end": v(-0.47, 0.05) * mm});
            skLineSegment(sketch, "E3522", {"start": v(-0.47, 0.05) * mm, "end": v(-0.47, 0.05) * mm});
            skLineSegment(sketch, "E3523", {"start": v(-0.47, 0.05) * mm, "end": v(-0.48, 0.05) * mm});
            skLineSegment(sketch, "E3524", {"start": v(-0.48, 0.05) * mm, "end": v(-0.48, 0.05) * mm});
            skLineSegment(sketch, "E3525", {"start": v(-0.48, 0.05) * mm, "end": v(-0.49, 0.05) * mm});
            skLineSegment(sketch, "E3526", {"start": v(-0.49, 0.05) * mm, "end": v(-0.5, 0.04) * mm});
            skLineSegment(sketch, "E3527", {"start": v(-0.5, 0.05) * mm, "end": v(-0.5, 0.04) * mm});
            skLineSegment(sketch, "E3528", {"start": v(-0.5, 0.04) * mm, "end": v(-0.5, 0.04) * mm});
            skLineSegment(sketch, "E3529", {"start": v(-0.5, 0.04) * mm, "end": v(-0.51, 0.04) * mm});
            skLineSegment(sketch, "E3530", {"start": v(-0.51, 0.04) * mm, "end": v(-0.51, 0.03) * mm});
            skLineSegment(sketch, "E3531", {"start": v(-0.4, 0.04) * mm, "end": v(-0.4, 0.04) * mm});
            skLineSegment(sketch, "E3532", {"start": v(-0.4, 0.04) * mm, "end": v(-0.39, 0.04) * mm});
            skLineSegment(sketch, "E3533", {"start": v(-0.39, 0.04) * mm, "end": v(-0.38, 0.03) * mm});
            skLineSegment(sketch, "E3534", {"start": v(-0.38, 0.03) * mm, "end": v(-0.38, 0.03) * mm});
            skLineSegment(sketch, "E3535", {"start": v(-0.38, 0.03) * mm, "end": v(-0.37, 0.02) * mm});
            skLineSegment(sketch, "E3536", {"start": v(-0.37, 0.02) * mm, "end": v(-0.37, 0.02) * mm});
            skLineSegment(sketch, "E3537", {"start": v(-0.37, 0.02) * mm, "end": v(-0.37, 0.01) * mm});
            skLineSegment(sketch, "E3538", {"start": v(-0.37, 0.01) * mm, "end": v(-0.36, 0) * mm});
            skLineSegment(sketch, "E3539", {"start": v(-0.36, 0) * mm, "end": v(-0.36, 0) * mm});
            skLineSegment(sketch, "E3540", {"start": v(-0.36, 0) * mm, "end": v(-0.35, 0) * mm});
            skLineSegment(sketch, "E3541", {"start": v(-0.35, 0) * mm, "end": v(-0.35, -0.02) * mm});
            skLineSegment(sketch, "E3542", {"start": v(-0.35, -0.02) * mm, "end": v(-0.35, -0.02) * mm});
            skLineSegment(sketch, "E3543", {"start": v(-0.35, -0.02) * mm, "end": v(-0.35, -0.03) * mm});
            skLineSegment(sketch, "E3544", {"start": v(-0.35, -0.03) * mm, "end": v(-0.35, -0.03) * mm});
            skLineSegment(sketch, "E3545", {"start": v(-0.35, -0.03) * mm, "end": v(-0.35, -0.04) * mm});
            skLineSegment(sketch, "E3546", {"start": v(-0.35, -0.04) * mm, "end": v(-0.34, -0.05) * mm});
            skLineSegment(sketch, "E3547", {"start": v(-0.34, -0.05) * mm, "end": v(-0.34, -0.05) * mm});
            skLineSegment(sketch, "E3548", {"start": v(-0.34, -0.05) * mm, "end": v(-0.35, -0.06) * mm});
            skLineSegment(sketch, "E3549", {"start": v(-0.35, -0.06) * mm, "end": v(-0.35, -0.07) * mm});
            skLineSegment(sketch, "E3550", {"start": v(-0.35, -0.07) * mm, "end": v(-0.35, -0.07) * mm});
            skLineSegment(sketch, "E3551", {"start": v(-0.35, -0.07) * mm, "end": v(-0.35, -0.08) * mm});
            skLineSegment(sketch, "E3552", {"start": v(-0.35, -0.08) * mm, "end": v(-0.35, -0.08) * mm});
            skLineSegment(sketch, "E3553", {"start": v(-0.35, -0.08) * mm, "end": v(-0.35, -0.1) * mm});
            skLineSegment(sketch, "E3554", {"start": v(-0.35, -0.1) * mm, "end": v(-0.36, -0.1) * mm});
            skLineSegment(sketch, "E3555", {"start": v(-0.36, -0.1) * mm, "end": v(-0.36, -0.1) * mm});
            skLineSegment(sketch, "E3556", {"start": v(-0.36, -0.1) * mm, "end": v(-0.37, -0.11) * mm});
            skLineSegment(sketch, "E3557", {"start": v(-0.37, -0.11) * mm, "end": v(-0.37, -0.12) * mm});
            skLineSegment(sketch, "E3558", {"start": v(-0.37, -0.12) * mm, "end": v(-0.37, -0.12) * mm});
            skLineSegment(sketch, "E3559", {"start": v(-0.37, -0.12) * mm, "end": v(-0.38, -0.13) * mm});
            skLineSegment(sketch, "E3560", {"start": v(-0.38, -0.13) * mm, "end": v(-0.38, -0.13) * mm});
            skLineSegment(sketch, "E3561", {"start": v(-0.38, -0.13) * mm, "end": v(-0.39, -0.14) * mm});
            skLineSegment(sketch, "E3562", {"start": v(-0.39, -0.14) * mm, "end": v(-0.4, -0.14) * mm});
            skLineSegment(sketch, "E3563", {"start": v(-0.4, -0.14) * mm, "end": v(-0.4, -0.14) * mm});
            skLineSegment(sketch, "E3564", {"start": v(-0.4, -0.14) * mm, "end": v(-0.4, -0.15) * mm});
            skLineSegment(sketch, "E3565", {"start": v(-0.22, -0.13) * mm, "end": v(-0.22, 0.03) * mm});
            skLineSegment(sketch, "E3566", {"start": v(-0.16, 0.05) * mm, "end": v(-0.16, 0) * mm});
            skLineSegment(sketch, "E3567", {"start": v(-0.16, 0) * mm, "end": v(-0.16, 0) * mm});
            skLineSegment(sketch, "E3568", {"start": v(-0.16, 0) * mm, "end": v(-0.16, -0.1) * mm});
            skLineSegment(sketch, "E3569", {"start": v(-0.16, -0.1) * mm, "end": v(-0.16, -0.1) * mm});
            skLineSegment(sketch, "E3570", {"start": v(-0.16, -0.1) * mm, "end": v(-0.16, -0.15) * mm});
            skLineSegment(sketch, "E3571", {"start": v(-0.2, -0.15) * mm, "end": v(-0.2, -0.14) * mm});
            skLineSegment(sketch, "E3572", {"start": v(-0.2, -0.14) * mm, "end": v(-0.2, -0.14) * mm});
            skLineSegment(sketch, "E3573", {"start": v(-0.2, -0.14) * mm, "end": v(-0.22, -0.13) * mm});
            skLineSegment(sketch, "E3574", {"start": v(-0.2, -0.15) * mm, "end": v(-0.19, -0.15) * mm});
            skLineSegment(sketch, "E3575", {"start": v(-0.19, -0.15) * mm, "end": v(-0.18, -0.15) * mm});
            skLineSegment(sketch, "E3576", {"start": v(-0.18, -0.15) * mm, "end": v(-0.18, -0.15) * mm});
            skLineSegment(sketch, "E3577", {"start": v(-0.18, -0.15) * mm, "end": v(-0.17, -0.15) * mm});
            skLineSegment(sketch, "E3578", {"start": v(-0.17, -0.15) * mm, "end": v(-0.17, -0.15) * mm});
            skLineSegment(sketch, "E3579", {"start": v(-0.17, -0.15) * mm, "end": v(-0.16, -0.15) * mm});
            skLineSegment(sketch, "E3580", {"start": v(-0.16, -0.15) * mm, "end": v(-0.15, -0.16) * mm});
            skLineSegment(sketch, "E3581", {"start": v(-0.15, -0.16) * mm, "end": v(-0.15, -0.16) * mm});
            skLineSegment(sketch, "E3582", {"start": v(-0.15, -0.16) * mm, "end": v(-0.14, -0.15) * mm});
            skLineSegment(sketch, "E3583", {"start": v(-0.14, -0.15) * mm, "end": v(-0.13, -0.15) * mm});
            skLineSegment(sketch, "E3584", {"start": v(-0.13, -0.15) * mm, "end": v(-0.13, -0.15) * mm});
            skLineSegment(sketch, "E3585", {"start": v(-0.13, -0.15) * mm, "end": v(-0.12, -0.15) * mm});
            skLineSegment(sketch, "E3586", {"start": v(-0.12, -0.15) * mm, "end": v(-0.12, -0.15) * mm});
            skLineSegment(sketch, "E3587", {"start": v(-0.12, -0.15) * mm, "end": v(-0.11, -0.15) * mm});
            skLineSegment(sketch, "E3588", {"start": v(-0.11, -0.15) * mm, "end": v(-0.1, -0.15) * mm});
            skLineSegment(sketch, "E3589", {"start": v(-0.1, 0.04) * mm, "end": v(-0.11, 0.05) * mm});
            skLineSegment(sketch, "E3590", {"start": v(-0.11, 0.05) * mm, "end": v(-0.12, 0.05) * mm});
            skLineSegment(sketch, "E3591", {"start": v(-0.12, 0.05) * mm, "end": v(-0.12, 0.05) * mm});
            skLineSegment(sketch, "E3592", {"start": v(-0.12, 0.05) * mm, "end": v(-0.13, 0.05) * mm});
            skLineSegment(sketch, "E3593", {"start": v(-0.13, 0.05) * mm, "end": v(-0.13, 0.05) * mm});
            skLineSegment(sketch, "E3594", {"start": v(-0.13, 0.05) * mm, "end": v(-0.14, 0.05) * mm});
            skLineSegment(sketch, "E3595", {"start": v(-0.14, 0.05) * mm, "end": v(-0.15, 0.05) * mm});
            skLineSegment(sketch, "E3596", {"start": v(-0.15, 0.05) * mm, "end": v(-0.15, 0.05) * mm});
            skLineSegment(sketch, "E3597", {"start": v(-0.15, 0.05) * mm, "end": v(-0.16, 0.05) * mm});
            skLineSegment(sketch, "E3598", {"start": v(-0.16, 0.05) * mm, "end": v(-0.17, 0.05) * mm});
            skLineSegment(sketch, "E3599", {"start": v(-0.17, 0.05) * mm, "end": v(-0.17, 0.05) * mm});
            skLineSegment(sketch, "E3600", {"start": v(-0.17, 0.05) * mm, "end": v(-0.18, 0.05) * mm});
            skLineSegment(sketch, "E3601", {"start": v(-0.18, 0.05) * mm, "end": v(-0.18, 0.05) * mm});
            skLineSegment(sketch, "E3602", {"start": v(-0.18, 0.05) * mm, "end": v(-0.19, 0.05) * mm});
            skLineSegment(sketch, "E3603", {"start": v(-0.19, 0.05) * mm, "end": v(-0.2, 0.04) * mm});
            skLineSegment(sketch, "E3604", {"start": v(-0.2, 0.05) * mm, "end": v(-0.2, 0.04) * mm});
            skLineSegment(sketch, "E3605", {"start": v(-0.2, 0.04) * mm, "end": v(-0.2, 0.04) * mm});
            skLineSegment(sketch, "E3606", {"start": v(-0.2, 0.04) * mm, "end": v(-0.21, 0.04) * mm});
            skLineSegment(sketch, "E3607", {"start": v(-0.21, 0.04) * mm, "end": v(-0.22, 0.03) * mm});
            skLineSegment(sketch, "E3608", {"start": v(-0.1, 0.04) * mm, "end": v(-0.1, 0.04) * mm});
            skLineSegment(sketch, "E3609", {"start": v(-0.1, 0.04) * mm, "end": v(-0.09, 0.04) * mm});
            skLineSegment(sketch, "E3610", {"start": v(-0.09, 0.04) * mm, "end": v(-0.08, 0.03) * mm});
            skLineSegment(sketch, "E3611", {"start": v(-0.08, 0.03) * mm, "end": v(-0.08, 0.03) * mm});
            skLineSegment(sketch, "E3612", {"start": v(-0.08, 0.03) * mm, "end": v(-0.07, 0.02) * mm});
            skLineSegment(sketch, "E3613", {"start": v(-0.07, 0.02) * mm, "end": v(-0.07, 0.02) * mm});
            skLineSegment(sketch, "E3614", {"start": v(-0.07, 0.02) * mm, "end": v(-0.07, 0.01) * mm});
            skLineSegment(sketch, "E3615", {"start": v(-0.07, 0.01) * mm, "end": v(-0.06, 0) * mm});
            skLineSegment(sketch, "E3616", {"start": v(-0.06, 0) * mm, "end": v(-0.06, 0) * mm});
            skLineSegment(sketch, "E3617", {"start": v(-0.06, 0) * mm, "end": v(-0.05, 0) * mm});
            skLineSegment(sketch, "E3618", {"start": v(-0.05, 0) * mm, "end": v(-0.05, -0.02) * mm});
            skLineSegment(sketch, "E3619", {"start": v(-0.05, -0.02) * mm, "end": v(-0.05, -0.02) * mm});
            skLineSegment(sketch, "E3620", {"start": v(-0.05, -0.02) * mm, "end": v(-0.05, -0.03) * mm});
            skLineSegment(sketch, "E3621", {"start": v(-0.05, -0.03) * mm, "end": v(-0.05, -0.03) * mm});
            skLineSegment(sketch, "E3622", {"start": v(-0.05, -0.03) * mm, "end": v(-0.05, -0.04) * mm});
            skLineSegment(sketch, "E3623", {"start": v(-0.05, -0.04) * mm, "end": v(-0.04, -0.05) * mm});
            skLineSegment(sketch, "E3624", {"start": v(-0.04, -0.05) * mm, "end": v(-0.04, -0.05) * mm});
            skLineSegment(sketch, "E3625", {"start": v(-0.04, -0.05) * mm, "end": v(-0.05, -0.06) * mm});
            skLineSegment(sketch, "E3626", {"start": v(-0.05, -0.06) * mm, "end": v(-0.05, -0.07) * mm});
            skLineSegment(sketch, "E3627", {"start": v(-0.05, -0.07) * mm, "end": v(-0.05, -0.07) * mm});
            skLineSegment(sketch, "E3628", {"start": v(-0.05, -0.07) * mm, "end": v(-0.05, -0.08) * mm});
            skLineSegment(sketch, "E3629", {"start": v(-0.05, -0.08) * mm, "end": v(-0.05, -0.08) * mm});
            skLineSegment(sketch, "E3630", {"start": v(-0.05, -0.08) * mm, "end": v(-0.05, -0.1) * mm});
            skLineSegment(sketch, "E3631", {"start": v(-0.05, -0.1) * mm, "end": v(-0.06, -0.1) * mm});
            skLineSegment(sketch, "E3632", {"start": v(-0.06, -0.1) * mm, "end": v(-0.06, -0.1) * mm});
            skLineSegment(sketch, "E3633", {"start": v(-0.06, -0.1) * mm, "end": v(-0.07, -0.11) * mm});
            skLineSegment(sketch, "E3634", {"start": v(-0.07, -0.11) * mm, "end": v(-0.07, -0.12) * mm});
            skLineSegment(sketch, "E3635", {"start": v(-0.07, -0.12) * mm, "end": v(-0.07, -0.12) * mm});
            skLineSegment(sketch, "E3636", {"start": v(-0.07, -0.12) * mm, "end": v(-0.08, -0.13) * mm});
            skLineSegment(sketch, "E3637", {"start": v(-0.08, -0.13) * mm, "end": v(-0.08, -0.13) * mm});
            skLineSegment(sketch, "E3638", {"start": v(-0.08, -0.13) * mm, "end": v(-0.09, -0.14) * mm});
            skLineSegment(sketch, "E3639", {"start": v(-0.09, -0.14) * mm, "end": v(-0.1, -0.14) * mm});
            skLineSegment(sketch, "E3640", {"start": v(-0.1, -0.14) * mm, "end": v(-0.1, -0.14) * mm});
            skLineSegment(sketch, "E3641", {"start": v(-0.1, -0.14) * mm, "end": v(-0.1, -0.15) * mm});
            skLineSegment(sketch, "E3642", {"start": v(0.08, -0.13) * mm, "end": v(0.08, 0.03) * mm});
            skLineSegment(sketch, "E3643", {"start": v(0.15, 0.05) * mm, "end": v(0.15, 0) * mm});
            skLineSegment(sketch, "E3644", {"start": v(0.15, 0) * mm, "end": v(0.15, 0) * mm});
            skLineSegment(sketch, "E3645", {"start": v(0.15, 0) * mm, "end": v(0.15, -0.1) * mm});
            skLineSegment(sketch, "E3646", {"start": v(0.15, -0.1) * mm, "end": v(0.15, -0.1) * mm});
            skLineSegment(sketch, "E3647", {"start": v(0.15, -0.1) * mm, "end": v(0.15, -0.15) * mm});
            skLineSegment(sketch, "E3648", {"start": v(0.1, -0.15) * mm, "end": v(0.1, -0.14) * mm});
            skLineSegment(sketch, "E3649", {"start": v(0.1, -0.14) * mm, "end": v(0.1, -0.14) * mm});
            skLineSegment(sketch, "E3650", {"start": v(0.1, -0.14) * mm, "end": v(0.08, -0.13) * mm});
            skLineSegment(sketch, "E3651", {"start": v(0.15, -0.15) * mm, "end": v(0.15, -0.16) * mm});
            skLineSegment(sketch, "E3652", {"start": v(0.15, -0.16) * mm, "end": v(0.16, -0.15) * mm});
            skLineSegment(sketch, "E3653", {"start": v(0.16, -0.15) * mm, "end": v(0.16, -0.15) * mm});
            skLineSegment(sketch, "E3654", {"start": v(0.16, -0.15) * mm, "end": v(0.17, -0.15) * mm});
            skLineSegment(sketch, "E3655", {"start": v(0.17, -0.15) * mm, "end": v(0.18, -0.15) * mm});
            skLineSegment(sketch, "E3656", {"start": v(0.18, -0.15) * mm, "end": v(0.18, -0.15) * mm});
            skLineSegment(sketch, "E3657", {"start": v(0.18, -0.15) * mm, "end": v(0.19, -0.15) * mm});
            skLineSegment(sketch, "E3658", {"start": v(0.19, -0.15) * mm, "end": v(0.2, -0.15) * mm});
            skLineSegment(sketch, "E3659", {"start": v(0.15, -0.15) * mm, "end": v(0.14, -0.15) * mm});
            skLineSegment(sketch, "E3660", {"start": v(0.14, -0.15) * mm, "end": v(0.13, -0.15) * mm});
            skLineSegment(sketch, "E3661", {"start": v(0.13, -0.15) * mm, "end": v(0.13, -0.15) * mm});
            skLineSegment(sketch, "E3662", {"start": v(0.13, -0.15) * mm, "end": v(0.12, -0.15) * mm});
            skLineSegment(sketch, "E3663", {"start": v(0.12, -0.15) * mm, "end": v(0.12, -0.15) * mm});
            skLineSegment(sketch, "E3664", {"start": v(0.12, -0.15) * mm, "end": v(0.11, -0.15) * mm});
            skLineSegment(sketch, "E3665", {"start": v(0.11, -0.15) * mm, "end": v(0.1, -0.15) * mm});
            skLineSegment(sketch, "E3666", {"start": v(0.15, 0.05) * mm, "end": v(0.15, 0.05) * mm});
            skLineSegment(sketch, "E3667", {"start": v(0.15, 0.05) * mm, "end": v(0.16, 0.05) * mm});
            skLineSegment(sketch, "E3668", {"start": v(0.16, 0.05) * mm, "end": v(0.16, 0.05) * mm});
            skLineSegment(sketch, "E3669", {"start": v(0.16, 0.05) * mm, "end": v(0.17, 0.05) * mm});
            skLineSegment(sketch, "E3670", {"start": v(0.17, 0.05) * mm, "end": v(0.18, 0.05) * mm});
            skLineSegment(sketch, "E3671", {"start": v(0.18, 0.05) * mm, "end": v(0.18, 0.05) * mm});
            skLineSegment(sketch, "E3672", {"start": v(0.18, 0.05) * mm, "end": v(0.19, 0.05) * mm});
            skLineSegment(sketch, "E3673", {"start": v(0.19, 0.05) * mm, "end": v(0.2, 0.04) * mm});
            skLineSegment(sketch, "E3674", {"start": v(0.1, 0.05) * mm, "end": v(0.1, 0.04) * mm});
            skLineSegment(sketch, "E3675", {"start": v(0.1, 0.04) * mm, "end": v(0.1, 0.04) * mm});
            skLineSegment(sketch, "E3676", {"start": v(0.1, 0.04) * mm, "end": v(0.09, 0.04) * mm});
            skLineSegment(sketch, "E3677", {"start": v(0.09, 0.04) * mm, "end": v(0.08, 0.03) * mm});
            skLineSegment(sketch, "E3678", {"start": v(0.1, 0.04) * mm, "end": v(0.11, 0.05) * mm});
            skLineSegment(sketch, "E3679", {"start": v(0.11, 0.05) * mm, "end": v(0.12, 0.05) * mm});
            skLineSegment(sketch, "E3680", {"start": v(0.12, 0.05) * mm, "end": v(0.12, 0.05) * mm});
            skLineSegment(sketch, "E3681", {"start": v(0.12, 0.05) * mm, "end": v(0.13, 0.05) * mm});
            skLineSegment(sketch, "E3682", {"start": v(0.13, 0.05) * mm, "end": v(0.13, 0.05) * mm});
            skLineSegment(sketch, "E3683", {"start": v(0.13, 0.05) * mm, "end": v(0.14, 0.05) * mm});
            skLineSegment(sketch, "E3684", {"start": v(0.14, 0.05) * mm, "end": v(0.15, 0.05) * mm});
            skLineSegment(sketch, "E3685", {"start": v(0.2, 0.04) * mm, "end": v(0.2, 0.04) * mm});
            skLineSegment(sketch, "E3686", {"start": v(0.2, 0.04) * mm, "end": v(0.21, 0.04) * mm});
            skLineSegment(sketch, "E3687", {"start": v(0.21, 0.04) * mm, "end": v(0.22, 0.03) * mm});
            skLineSegment(sketch, "E3688", {"start": v(0.22, 0.03) * mm, "end": v(0.22, 0.03) * mm});
            skLineSegment(sketch, "E3689", {"start": v(0.22, 0.03) * mm, "end": v(0.23, 0.02) * mm});
            skLineSegment(sketch, "E3690", {"start": v(0.23, 0.02) * mm, "end": v(0.23, 0.02) * mm});
            skLineSegment(sketch, "E3691", {"start": v(0.23, 0.02) * mm, "end": v(0.23, 0.01) * mm});
            skLineSegment(sketch, "E3692", {"start": v(0.23, 0.01) * mm, "end": v(0.24, 0) * mm});
            skLineSegment(sketch, "E3693", {"start": v(0.24, 0) * mm, "end": v(0.24, 0) * mm});
            skLineSegment(sketch, "E3694", {"start": v(0.24, 0) * mm, "end": v(0.25, 0) * mm});
            skLineSegment(sketch, "E3695", {"start": v(0.25, 0) * mm, "end": v(0.25, -0.02) * mm});
            skLineSegment(sketch, "E3696", {"start": v(0.25, -0.02) * mm, "end": v(0.25, -0.02) * mm});
            skLineSegment(sketch, "E3697", {"start": v(0.25, -0.02) * mm, "end": v(0.25, -0.03) * mm});
            skLineSegment(sketch, "E3698", {"start": v(0.25, -0.03) * mm, "end": v(0.25, -0.03) * mm});
            skLineSegment(sketch, "E3699", {"start": v(0.25, -0.03) * mm, "end": v(0.25, -0.04) * mm});
            skLineSegment(sketch, "E3700", {"start": v(0.25, -0.04) * mm, "end": v(0.26, -0.05) * mm});
            skLineSegment(sketch, "E3701", {"start": v(0.26, -0.05) * mm, "end": v(0.26, -0.05) * mm});
            skLineSegment(sketch, "E3702", {"start": v(0.26, -0.05) * mm, "end": v(0.25, -0.06) * mm});
            skLineSegment(sketch, "E3703", {"start": v(0.25, -0.06) * mm, "end": v(0.25, -0.07) * mm});
            skLineSegment(sketch, "E3704", {"start": v(0.25, -0.07) * mm, "end": v(0.25, -0.07) * mm});
            skLineSegment(sketch, "E3705", {"start": v(0.25, -0.07) * mm, "end": v(0.25, -0.08) * mm});
            skLineSegment(sketch, "E3706", {"start": v(0.25, -0.08) * mm, "end": v(0.25, -0.08) * mm});
            skLineSegment(sketch, "E3707", {"start": v(0.25, -0.08) * mm, "end": v(0.25, -0.1) * mm});
            skLineSegment(sketch, "E3708", {"start": v(0.25, -0.1) * mm, "end": v(0.24, -0.1) * mm});
            skLineSegment(sketch, "E3709", {"start": v(0.24, -0.1) * mm, "end": v(0.24, -0.1) * mm});
            skLineSegment(sketch, "E3710", {"start": v(0.24, -0.1) * mm, "end": v(0.23, -0.11) * mm});
            skLineSegment(sketch, "E3711", {"start": v(0.23, -0.11) * mm, "end": v(0.23, -0.12) * mm});
            skLineSegment(sketch, "E3712", {"start": v(0.23, -0.12) * mm, "end": v(0.23, -0.12) * mm});
            skLineSegment(sketch, "E3713", {"start": v(0.23, -0.12) * mm, "end": v(0.22, -0.13) * mm});
            skLineSegment(sketch, "E3714", {"start": v(0.22, -0.13) * mm, "end": v(0.22, -0.13) * mm});
            skLineSegment(sketch, "E3715", {"start": v(0.22, -0.13) * mm, "end": v(0.21, -0.14) * mm});
            skLineSegment(sketch, "E3716", {"start": v(0.21, -0.14) * mm, "end": v(0.2, -0.14) * mm});
            skLineSegment(sketch, "E3717", {"start": v(0.2, -0.14) * mm, "end": v(0.2, -0.14) * mm});
            skLineSegment(sketch, "E3718", {"start": v(0.2, -0.14) * mm, "end": v(0.2, -0.15) * mm});
            skLineSegment(sketch, "E3719", {"start": v(0.39, -0.13) * mm, "end": v(0.39, 0.03) * mm});
            skLineSegment(sketch, "E3720", {"start": v(0.45, 0.05) * mm, "end": v(0.45, 0) * mm});
            skLineSegment(sketch, "E3721", {"start": v(0.45, 0) * mm, "end": v(0.45, 0) * mm});
            skLineSegment(sketch, "E3722", {"start": v(0.45, 0) * mm, "end": v(0.45, -0.1) * mm});
            skLineSegment(sketch, "E3723", {"start": v(0.45, -0.1) * mm, "end": v(0.45, -0.1) * mm});
            skLineSegment(sketch, "E3724", {"start": v(0.45, -0.1) * mm, "end": v(0.45, -0.15) * mm});
            skLineSegment(sketch, "E3725", {"start": v(0.4, -0.15) * mm, "end": v(0.4, -0.14) * mm});
            skLineSegment(sketch, "E3726", {"start": v(0.4, -0.14) * mm, "end": v(0.4, -0.14) * mm});
            skLineSegment(sketch, "E3727", {"start": v(0.4, -0.14) * mm, "end": v(0.39, -0.14) * mm});
            skLineSegment(sketch, "E3728", {"start": v(0.39, -0.14) * mm, "end": v(0.39, -0.13) * mm});
            skLineSegment(sketch, "E3729", {"start": v(0.4, -0.15) * mm, "end": v(0.41, -0.15) * mm});
            skLineSegment(sketch, "E3730", {"start": v(0.41, -0.15) * mm, "end": v(0.42, -0.15) * mm});
            skLineSegment(sketch, "E3731", {"start": v(0.42, -0.15) * mm, "end": v(0.42, -0.15) * mm});
            skLineSegment(sketch, "E3732", {"start": v(0.42, -0.15) * mm, "end": v(0.43, -0.15) * mm});
            skLineSegment(sketch, "E3733", {"start": v(0.43, -0.15) * mm, "end": v(0.43, -0.15) * mm});
            skLineSegment(sketch, "E3734", {"start": v(0.43, -0.15) * mm, "end": v(0.44, -0.15) * mm});
            skLineSegment(sketch, "E3735", {"start": v(0.44, -0.15) * mm, "end": v(0.45, -0.16) * mm});
            skLineSegment(sketch, "E3736", {"start": v(0.45, -0.16) * mm, "end": v(0.45, -0.16) * mm});
            skLineSegment(sketch, "E3737", {"start": v(0.45, -0.16) * mm, "end": v(0.46, -0.15) * mm});
            skLineSegment(sketch, "E3738", {"start": v(0.46, -0.15) * mm, "end": v(0.47, -0.15) * mm});
            skLineSegment(sketch, "E3739", {"start": v(0.47, -0.15) * mm, "end": v(0.47, -0.15) * mm});
            skLineSegment(sketch, "E3740", {"start": v(0.47, -0.15) * mm, "end": v(0.48, -0.15) * mm});
            skLineSegment(sketch, "E3741", {"start": v(0.48, -0.15) * mm, "end": v(0.48, -0.15) * mm});
            skLineSegment(sketch, "E3742", {"start": v(0.48, -0.15) * mm, "end": v(0.49, -0.15) * mm});
            skLineSegment(sketch, "E3743", {"start": v(0.49, -0.15) * mm, "end": v(0.5, -0.15) * mm});
            skLineSegment(sketch, "E3744", {"start": v(0.5, 0.04) * mm, "end": v(0.49, 0.05) * mm});
            skLineSegment(sketch, "E3745", {"start": v(0.49, 0.05) * mm, "end": v(0.48, 0.05) * mm});
            skLineSegment(sketch, "E3746", {"start": v(0.48, 0.05) * mm, "end": v(0.48, 0.05) * mm});
            skLineSegment(sketch, "E3747", {"start": v(0.48, 0.05) * mm, "end": v(0.47, 0.05) * mm});
            skLineSegment(sketch, "E3748", {"start": v(0.47, 0.05) * mm, "end": v(0.47, 0.05) * mm});
            skLineSegment(sketch, "E3749", {"start": v(0.47, 0.05) * mm, "end": v(0.46, 0.05) * mm});
            skLineSegment(sketch, "E3750", {"start": v(0.46, 0.05) * mm, "end": v(0.45, 0.05) * mm});
            skLineSegment(sketch, "E3751", {"start": v(0.45, 0.05) * mm, "end": v(0.45, 0.05) * mm});
            skLineSegment(sketch, "E3752", {"start": v(0.45, 0.05) * mm, "end": v(0.44, 0.05) * mm});
            skLineSegment(sketch, "E3753", {"start": v(0.44, 0.05) * mm, "end": v(0.43, 0.05) * mm});
            skLineSegment(sketch, "E3754", {"start": v(0.43, 0.05) * mm, "end": v(0.43, 0.05) * mm});
            skLineSegment(sketch, "E3755", {"start": v(0.43, 0.05) * mm, "end": v(0.42, 0.05) * mm});
            skLineSegment(sketch, "E3756", {"start": v(0.42, 0.05) * mm, "end": v(0.42, 0.05) * mm});
            skLineSegment(sketch, "E3757", {"start": v(0.42, 0.05) * mm, "end": v(0.41, 0.05) * mm});
            skLineSegment(sketch, "E3758", {"start": v(0.41, 0.05) * mm, "end": v(0.4, 0.04) * mm});
            skLineSegment(sketch, "E3759", {"start": v(0.4, 0.05) * mm, "end": v(0.4, 0.04) * mm});
            skLineSegment(sketch, "E3760", {"start": v(0.4, 0.04) * mm, "end": v(0.4, 0.04) * mm});
            skLineSegment(sketch, "E3761", {"start": v(0.4, 0.04) * mm, "end": v(0.39, 0.04) * mm});
            skLineSegment(sketch, "E3762", {"start": v(0.39, 0.04) * mm, "end": v(0.39, 0.03) * mm});
            skLineSegment(sketch, "E3763", {"start": v(0.5, 0.04) * mm, "end": v(0.5, 0.04) * mm});
            skLineSegment(sketch, "E3764", {"start": v(0.5, 0.04) * mm, "end": v(0.51, 0.04) * mm});
            skLineSegment(sketch, "E3765", {"start": v(0.51, 0.04) * mm, "end": v(0.52, 0.03) * mm});
            skLineSegment(sketch, "E3766", {"start": v(0.52, 0.03) * mm, "end": v(0.52, 0.03) * mm});
            skLineSegment(sketch, "E3767", {"start": v(0.52, 0.03) * mm, "end": v(0.53, 0.02) * mm});
            skLineSegment(sketch, "E3768", {"start": v(0.53, 0.02) * mm, "end": v(0.53, 0.02) * mm});
            skLineSegment(sketch, "E3769", {"start": v(0.53, 0.02) * mm, "end": v(0.53, 0.01) * mm});
            skLineSegment(sketch, "E3770", {"start": v(0.53, 0.01) * mm, "end": v(0.54, 0) * mm});
            skLineSegment(sketch, "E3771", {"start": v(0.54, 0) * mm, "end": v(0.54, 0) * mm});
            skLineSegment(sketch, "E3772", {"start": v(0.54, 0) * mm, "end": v(0.55, 0) * mm});
            skLineSegment(sketch, "E3773", {"start": v(0.55, 0) * mm, "end": v(0.55, -0.02) * mm});
            skLineSegment(sketch, "E3774", {"start": v(0.55, -0.02) * mm, "end": v(0.55, -0.02) * mm});
            skLineSegment(sketch, "E3775", {"start": v(0.55, -0.02) * mm, "end": v(0.55, -0.03) * mm});
            skLineSegment(sketch, "E3776", {"start": v(0.55, -0.03) * mm, "end": v(0.55, -0.03) * mm});
            skLineSegment(sketch, "E3777", {"start": v(0.55, -0.03) * mm, "end": v(0.55, -0.04) * mm});
            skLineSegment(sketch, "E3778", {"start": v(0.55, -0.04) * mm, "end": v(0.55, -0.05) * mm});
            skLineSegment(sketch, "E3779", {"start": v(0.55, -0.05) * mm, "end": v(0.55, -0.05) * mm});
            skLineSegment(sketch, "E3780", {"start": v(0.55, -0.05) * mm, "end": v(0.55, -0.06) * mm});
            skLineSegment(sketch, "E3781", {"start": v(0.55, -0.06) * mm, "end": v(0.55, -0.07) * mm});
            skLineSegment(sketch, "E3782", {"start": v(0.55, -0.07) * mm, "end": v(0.55, -0.07) * mm});
            skLineSegment(sketch, "E3783", {"start": v(0.55, -0.07) * mm, "end": v(0.55, -0.08) * mm});
            skLineSegment(sketch, "E3784", {"start": v(0.55, -0.08) * mm, "end": v(0.55, -0.08) * mm});
            skLineSegment(sketch, "E3785", {"start": v(0.55, -0.08) * mm, "end": v(0.55, -0.1) * mm});
            skLineSegment(sketch, "E3786", {"start": v(0.55, -0.1) * mm, "end": v(0.54, -0.1) * mm});
            skLineSegment(sketch, "E3787", {"start": v(0.54, -0.1) * mm, "end": v(0.54, -0.1) * mm});
            skLineSegment(sketch, "E3788", {"start": v(0.54, -0.1) * mm, "end": v(0.53, -0.11) * mm});
            skLineSegment(sketch, "E3789", {"start": v(0.53, -0.11) * mm, "end": v(0.53, -0.12) * mm});
            skLineSegment(sketch, "E3790", {"start": v(0.53, -0.12) * mm, "end": v(0.53, -0.12) * mm});
            skLineSegment(sketch, "E3791", {"start": v(0.53, -0.12) * mm, "end": v(0.52, -0.13) * mm});
            skLineSegment(sketch, "E3792", {"start": v(0.52, -0.13) * mm, "end": v(0.52, -0.13) * mm});
            skLineSegment(sketch, "E3793", {"start": v(0.52, -0.13) * mm, "end": v(0.51, -0.14) * mm});
            skLineSegment(sketch, "E3794", {"start": v(0.51, -0.14) * mm, "end": v(0.5, -0.14) * mm});
            skLineSegment(sketch, "E3795", {"start": v(0.5, -0.14) * mm, "end": v(0.5, -0.14) * mm});
            skLineSegment(sketch, "E3796", {"start": v(0.5, -0.14) * mm, "end": v(0.5, -0.15) * mm});
            skLineSegment(sketch, "E3797", {"start": v(0.8, -0.25) * mm, "end": v(0.9, -0.25) * mm});
            skLineSegment(sketch, "E3798", {"start": v(0.9, -0.25) * mm, "end": v(0.92, -0.24) * mm});
            skLineSegment(sketch, "E3799", {"start": v(0.92, -0.24) * mm, "end": v(0.92, 0.13) * mm});
            skLineSegment(sketch, "E3800", {"start": v(0.92, 0.13) * mm, "end": v(0.9, 0.14) * mm});
            skLineSegment(sketch, "E3801", {"start": v(0.9, 0.14) * mm, "end": v(0.8, 0.15) * mm});
            skLineSegment(sketch, "E3802", {"start": v(0.84, 0.06) * mm, "end": v(0.84, 0.06) * mm});
            skLineSegment(sketch, "E3803", {"start": v(0.84, 0.06) * mm, "end": v(0.85, 0.05) * mm});
            skLineSegment(sketch, "E3804", {"start": v(0.85, 0.05) * mm, "end": v(0.86, 0.06) * mm});
            skLineSegment(sketch, "E3805", {"start": v(0.86, 0.06) * mm, "end": v(0.86, 0.06) * mm});
            skLineSegment(sketch, "E3806", {"start": v(0.86, 0.06) * mm, "end": v(0.87, 0.05) * mm});
            skLineSegment(sketch, "E3807", {"start": v(0.87, 0.05) * mm, "end": v(0.87, 0.03) * mm});
            skLineSegment(sketch, "E3808", {"start": v(0.87, 0.03) * mm, "end": v(0.86, 0.03) * mm});
            skLineSegment(sketch, "E3809", {"start": v(0.85, 0.04) * mm, "end": v(0.85, 0.05) * mm});
            skLineSegment(sketch, "E3810", {"start": v(0.84, 0.06) * mm, "end": v(0.83, 0.05) * mm});
            skLineSegment(sketch, "E3811", {"start": v(0.83, 0.05) * mm, "end": v(0.83, 0.03) * mm});
            skLineSegment(sketch, "E3812", {"start": v(0.83, 0.03) * mm, "end": v(0.84, 0.03) * mm});
            skLineSegment(sketch, "E3813", {"start": v(0.84, -0.04) * mm, "end": v(0.83, -0.05) * mm});
            skLineSegment(sketch, "E3814", {"start": v(0.83, -0.05) * mm, "end": v(0.83, -0.07) * mm});
            skLineSegment(sketch, "E3815", {"start": v(0.83, -0.07) * mm, "end": v(0.84, -0.07) * mm});
            skLineSegment(sketch, "E3816", {"start": v(0.84, -0.04) * mm, "end": v(0.84, -0.04) * mm});
            skLineSegment(sketch, "E3817", {"start": v(0.84, -0.04) * mm, "end": v(0.87, -0.07) * mm});
            skLineSegment(sketch, "E3818", {"start": v(0.87, -0.07) * mm, "end": v(0.87, -0.04) * mm});
            skLineSegment(sketch, "E3819", {"start": v(0.87, -0.14) * mm, "end": v(0.87, -0.17) * mm});
            skLineSegment(sketch, "E3820", {"start": v(0.87, -0.16) * mm, "end": v(0.83, -0.16) * mm});
            skLineSegment(sketch, "E3821", {"start": v(0.83, -0.16) * mm, "end": v(0.84, -0.17) * mm});
            skLineSegment(sketch, "E3822", {"start": v(0.89, -0.23) * mm, "end": v(0.89, -0.23) * mm});
            skLineSegment(sketch, "E3823", {"start": v(0.89, -0.23) * mm, "end": v(0.89, -0.22) * mm});
            skLineSegment(sketch, "E3824", {"start": v(0.89, -0.22) * mm, "end": v(0.89, -0.22) * mm});
            skLineSegment(sketch, "E3825", {"start": v(0.89, -0.22) * mm, "end": v(0.9, -0.22) * mm});
            skLineSegment(sketch, "E3826", {"start": v(0.9, -0.22) * mm, "end": v(0.9, -0.22) * mm});
            skLineSegment(sketch, "E3827", {"start": v(0.9, -0.22) * mm, "end": v(0.9, -0.23) * mm});
            skLineSegment(sketch, "E3828", {"start": v(0.9, -0.23) * mm, "end": v(0.9, -0.23) * mm});
            skLineSegment(sketch, "E3829", {"start": v(0.9, -0.23) * mm, "end": v(0.9, -0.24) * mm});
            skLineSegment(sketch, "E3830", {"start": v(0.9, -0.24) * mm, "end": v(0.9, -0.24) * mm});
            skLineSegment(sketch, "E3831", {"start": v(0.9, -0.24) * mm, "end": v(0.89, -0.23) * mm});
            skLineSegment(sketch, "E3832", {"start": v(0.7, -0.4) * mm, "end": v(0.7, -0.4) * mm});
            skLineSegment(sketch, "E3833", {"start": v(0.7, -0.4) * mm, "end": v(0.68, -0.4) * mm});
            skLineSegment(sketch, "E3834", {"start": v(0.68, -0.4) * mm, "end": v(0.68, -0.4) * mm});
            skLineSegment(sketch, "E3835", {"start": v(0.68, -0.4) * mm, "end": v(0.68, -0.42) * mm});
            skLineSegment(sketch, "E3836", {"start": v(0.68, -0.42) * mm, "end": v(0.7, -0.42) * mm});
            skLineSegment(sketch, "E3837", {"start": v(0.7, -0.42) * mm, "end": v(0.7, -0.42) * mm});
            skLineSegment(sketch, "E3838", {"start": v(0.7, -0.42) * mm, "end": v(0.7, -0.4) * mm});
            skLineSegment(sketch, "E3839", {"start": v(0.68, -0.42) * mm, "end": v(0.66, -0.4) * mm});
            skLineSegment(sketch, "E3840", {"start": v(0.66, -0.4) * mm, "end": v(0.65, -0.4) * mm});
            skLineSegment(sketch, "E3841", {"start": v(1.08, -0.7) * mm, "end": v(1.08, -0.71) * mm});
            skLineSegment(sketch, "E3842", {"start": v(1.08, -0.71) * mm, "end": v(1.09, -0.72) * mm});
            skLineSegment(sketch, "E3843", {"start": v(1.08, -0.7) * mm, "end": v(1.09, -0.7) * mm});
            skLineSegment(sketch, "E3844", {"start": v(1.09, -0.7) * mm, "end": v(1.1, -0.7) * mm});
            skLineSegment(sketch, "E3845", {"start": v(1.1, -0.7) * mm, "end": v(1.12, -0.72) * mm});
            skLineSegment(sketch, "E3846", {"start": v(1.12, -0.72) * mm, "end": v(1.12, -0.7) * mm});
            skLineSegment(sketch, "E3847", {"start": v(1.12, -0.9) * mm, "end": v(1.12, -0.92) * mm});
            skLineSegment(sketch, "E3848", {"start": v(1.12, -0.9) * mm, "end": v(1.08, -0.9) * mm});
            skLineSegment(sketch, "E3849", {"start": v(1.08, -0.9) * mm, "end": v(1.1, -0.92) * mm});
            skLineSegment(sketch, "E3850", {"start": v(0.7, -1.3) * mm, "end": v(0.7, -1.32) * mm});
            skLineSegment(sketch, "E3851", {"start": v(0.7, -1.32) * mm, "end": v(0.7, -1.32) * mm});
            skLineSegment(sketch, "E3852", {"start": v(0.68, -1.32) * mm, "end": v(0.67, -1.3) * mm});
            skLineSegment(sketch, "E3853", {"start": v(0.67, -1.3) * mm, "end": v(0.67, -1.3) * mm});
            skLineSegment(sketch, "E3854", {"start": v(0.67, -1.3) * mm, "end": v(0.68, -1.3) * mm});
            skLineSegment(sketch, "E3855", {"start": v(0.68, -1.3) * mm, "end": v(0.7, -1.3) * mm});
            skLineSegment(sketch, "E3856", {"start": v(0.7, -1.3) * mm, "end": v(0.7, -1.3) * mm});
            skLineSegment(sketch, "E3857", {"start": v(0.68, -1.32) * mm, "end": v(0.65, -1.32) * mm});
            skLineSegment(sketch, "E3858", {"start": v(0.65, -1.32) * mm, "end": v(0.65, -1.3) * mm});
            skLineSegment(sketch, "E3859", {"start": v(-0.35, -1.3) * mm, "end": v(-0.35, -1.32) * mm});
            skLineSegment(sketch, "E3860", {"start": v(-0.35, -1.3) * mm, "end": v(-0.4, -1.3) * mm});
            skLineSegment(sketch, "E3861", {"start": v(-0.4, -1.3) * mm, "end": v(-0.38, -1.32) * mm});
            skLineSegment(sketch, "E3862", {"start": v(-0.38, -0.45) * mm, "end": v(-0.4, -0.43) * mm});
            skLineSegment(sketch, "E3863", {"start": v(-0.4, -0.43) * mm, "end": v(-0.35, -0.43) * mm});
            skLineSegment(sketch, "E3864", {"start": v(-0.35, -0.42) * mm, "end": v(-0.35, -0.45) * mm});
            skLineSegment(sketch, "E3865", {"start": v(-0.36, -0.4) * mm, "end": v(-0.39, -0.4) * mm});
            skLineSegment(sketch, "E3866", {"start": v(-0.39, -0.4) * mm, "end": v(-0.4, -0.4) * mm});
            skLineSegment(sketch, "E3867", {"start": v(-0.4, -0.4) * mm, "end": v(-0.4, -0.38) * mm});
            skLineSegment(sketch, "E3868", {"start": v(-0.4, -0.38) * mm, "end": v(-0.39, -0.37) * mm});
            skLineSegment(sketch, "E3869", {"start": v(-0.39, -0.37) * mm, "end": v(-0.36, -0.4) * mm});
            skLineSegment(sketch, "E3870", {"start": v(-0.36, -0.4) * mm, "end": v(-0.35, -0.4) * mm});
            skLineSegment(sketch, "E3871", {"start": v(-0.35, -0.4) * mm, "end": v(-0.35, -0.38) * mm});
            skLineSegment(sketch, "E3872", {"start": v(-0.35, -0.38) * mm, "end": v(-0.36, -0.37) * mm});
            skLineSegment(sketch, "E3873", {"start": v(-0.36, -0.37) * mm, "end": v(-0.39, -0.37) * mm});
            skLineSegment(sketch, "E3874", {"start": v(1.44, 0.2) * mm, "end": v(1.45, 0.18) * mm});
            skLineSegment(sketch, "E3875", {"start": v(1.44, 0.2) * mm, "end": v(1.48, 0.2) * mm});
            skLineSegment(sketch, "E3876", {"start": v(1.48, 0.18) * mm, "end": v(1.48, 0.2) * mm});
            skLineSegment(sketch, "E3877", {"start": v(1.72, -0.2) * mm, "end": v(1.72, -0.2) * mm});
            skLineSegment(sketch, "E3878", {"start": v(1.72, -0.2) * mm, "end": v(1.72, -0.22) * mm});
            skLineSegment(sketch, "E3879", {"start": v(1.72, -0.22) * mm, "end": v(1.72, -0.22) * mm});
            skLineSegment(sketch, "E3880", {"start": v(1.72, -0.22) * mm, "end": v(1.76, -0.22) * mm});
            skLineSegment(sketch, "E3881", {"start": v(1.76, -0.22) * mm, "end": v(1.72, -0.2) * mm});
            skLineSegment(sketch, "E3882", {"start": v(1.72, -0.2) * mm, "end": v(1.76, -0.2) * mm});
            skLineSegment(sketch, "E3883", {"start": v(1.76, -0.2) * mm, "end": v(1.76, -0.2) * mm});
            skLineSegment(sketch, "E3884", {"start": v(1.76, -0.2) * mm, "end": v(1.76, -0.22) * mm});
            skLineSegment(sketch, "E3885", {"start": v(1.76, -0.22) * mm, "end": v(1.76, -0.22) * mm});
            skLineSegment(sketch, "E3886", {"start": v(1.76, -0.24) * mm, "end": v(1.76, -0.27) * mm});
            skLineSegment(sketch, "E3887", {"start": v(1.76, -0.25) * mm, "end": v(1.72, -0.25) * mm});
            skLineSegment(sketch, "E3888", {"start": v(1.72, -0.25) * mm, "end": v(1.73, -0.27) * mm});
            skLineSegment(sketch, "E3889", {"start": v(0.25, 0.15) * mm, "end": v(0.25, 0.19) * mm});
            skLineSegment(sketch, "E3890", {"start": v(0.15, 0.19) * mm, "end": v(0.15, 0.15) * mm});
            skLineSegment(sketch, "E3891", {"start": v(-0.05, 0.15) * mm, "end": v(-0.05, 0.19) * mm});
            skLineSegment(sketch, "E3892", {"start": v(-0.15, 0.19) * mm, "end": v(-0.15, 0.15) * mm});
            skLineSegment(sketch, "E3893", {"start": v(-0.25, 0.15) * mm, "end": v(-0.25, 0.19) * mm});
            skLineSegment(sketch, "E3894", {"start": v(-0.35, 0.19) * mm, "end": v(-0.35, 0.15) * mm});
            skLineSegment(sketch, "E3895", {"start": v(-0.35, 0.5) * mm, "end": v(-0.35, 0.55) * mm});
            skLineSegment(sketch, "E3896", {"start": v(-0.25, 0.55) * mm, "end": v(-0.25, 0.5) * mm});
            skLineSegment(sketch, "E3897", {"start": v(-0.15, 0.5) * mm, "end": v(-0.15, 0.55) * mm});
            skLineSegment(sketch, "E3898", {"start": v(-0.05, 0.55) * mm, "end": v(-0.05, 0.5) * mm});
            skLineSegment(sketch, "E3899", {"start": v(0.15, 0.5) * mm, "end": v(0.15, 0.55) * mm});
            skLineSegment(sketch, "E3900", {"start": v(0.25, 0.55) * mm, "end": v(0.25, 0.5) * mm});
            skLineSegment(sketch, "E3901", {"start": v(-0.45, 0.65) * mm, "end": v(-0.45, 0.69) * mm});
            skLineSegment(sketch, "E3902", {"start": v(-0.55, 0.69) * mm, "end": v(-0.55, 0.65) * mm});
            skLineSegment(sketch, "E3903", {"start": v(-0.65, 0.65) * mm, "end": v(-0.65, 0.69) * mm});
            skLineSegment(sketch, "E3904", {"start": v(-0.75, 0.69) * mm, "end": v(-0.75, 0.65) * mm});
            skLineSegment(sketch, "E3905", {"start": v(-0.85, 0.65) * mm, "end": v(-0.85, 0.69) * mm});
            skLineSegment(sketch, "E3906", {"start": v(-0.95, 0.69) * mm, "end": v(-0.95, 0.65) * mm});
            skLineSegment(sketch, "E3907", {"start": v(-0.95, 1) * mm, "end": v(-0.95, 1.05) * mm});
            skLineSegment(sketch, "E3908", {"start": v(-0.85, 1.05) * mm, "end": v(-0.85, 1) * mm});
            skLineSegment(sketch, "E3909", {"start": v(-0.75, 1) * mm, "end": v(-0.75, 1.05) * mm});
            skLineSegment(sketch, "E3910", {"start": v(-0.65, 1.05) * mm, "end": v(-0.65, 1) * mm});
            skLineSegment(sketch, "E3911", {"start": v(-0.55, 1) * mm, "end": v(-0.55, 1.05) * mm});
            skLineSegment(sketch, "E3912", {"start": v(-0.45, 1.05) * mm, "end": v(-0.45, 1) * mm});
            skLineSegment(sketch, "E3913", {"start": v(-0.44, -0.31) * mm, "end": v(0.74, -0.31) * mm});
            skLineSegment(sketch, "E3914", {"start": v(0.74, -0.31) * mm, "end": v(0.74, -0.31) * mm});
            skLineSegment(sketch, "E3915", {"start": v(0.74, -0.31) * mm, "end": v(0.75, -0.31) * mm});
            skLineSegment(sketch, "E3916", {"start": v(0.75, -0.31) * mm, "end": v(0.75, -0.31) * mm});
            skLineSegment(sketch, "E3917", {"start": v(0.75, -0.31) * mm, "end": v(0.76, -0.31) * mm});
            skLineSegment(sketch, "E3918", {"start": v(0.76, -0.31) * mm, "end": v(0.76, -0.31) * mm});
            skLineSegment(sketch, "E3919", {"start": v(0.76, -0.31) * mm, "end": v(0.76, -0.32) * mm});
            skLineSegment(sketch, "E3920", {"start": v(0.76, -0.32) * mm, "end": v(0.77, -0.32) * mm});
            skLineSegment(sketch, "E3921", {"start": v(0.77, -0.32) * mm, "end": v(0.77, -0.32) * mm});
            skLineSegment(sketch, "E3922", {"start": v(0.77, -0.32) * mm, "end": v(0.78, -0.32) * mm});
            skLineSegment(sketch, "E3923", {"start": v(0.78, -0.32) * mm, "end": v(0.78, -0.33) * mm});
            skLineSegment(sketch, "E3924", {"start": v(0.78, -0.33) * mm, "end": v(0.78, -0.33) * mm});
            skLineSegment(sketch, "E3925", {"start": v(0.78, -0.33) * mm, "end": v(0.78, -0.34) * mm});
            skLineSegment(sketch, "E3926", {"start": v(0.78, -0.34) * mm, "end": v(0.79, -0.34) * mm});
            skLineSegment(sketch, "E3927", {"start": v(0.79, -0.34) * mm, "end": v(0.79, -0.34) * mm});
            skLineSegment(sketch, "E3928", {"start": v(0.79, -0.34) * mm, "end": v(0.79, -0.35) * mm});
            skLineSegment(sketch, "E3929", {"start": v(0.79, -0.35) * mm, "end": v(0.79, -0.35) * mm});
            skLineSegment(sketch, "E3930", {"start": v(0.79, -0.35) * mm, "end": v(0.79, -0.36) * mm});
            skLineSegment(sketch, "E3931", {"start": v(0.79, -0.36) * mm, "end": v(0.79, -0.36) * mm});
            skLineSegment(sketch, "E3932", {"start": v(0.79, -0.36) * mm, "end": v(0.79, -1.34) * mm});
            skLineSegment(sketch, "E3933", {"start": v(0.79, -1.34) * mm, "end": v(0.79, -1.34) * mm});
            skLineSegment(sketch, "E3934", {"start": v(0.79, -1.34) * mm, "end": v(0.79, -1.35) * mm});
            skLineSegment(sketch, "E3935", {"start": v(0.79, -1.35) * mm, "end": v(0.79, -1.35) * mm});
            skLineSegment(sketch, "E3936", {"start": v(0.79, -1.35) * mm, "end": v(0.79, -1.36) * mm});
            skLineSegment(sketch, "E3937", {"start": v(0.79, -1.36) * mm, "end": v(0.79, -1.36) * mm});
            skLineSegment(sketch, "E3938", {"start": v(0.79, -1.36) * mm, "end": v(0.78, -1.37) * mm});
            skLineSegment(sketch, "E3939", {"start": v(0.78, -1.37) * mm, "end": v(0.78, -1.37) * mm});
            skLineSegment(sketch, "E3940", {"start": v(0.78, -1.37) * mm, "end": v(0.78, -1.38) * mm});
            skLineSegment(sketch, "E3941", {"start": v(0.78, -1.38) * mm, "end": v(0.77, -1.38) * mm});
            skLineSegment(sketch, "E3942", {"start": v(0.77, -1.38) * mm, "end": v(0.77, -1.38) * mm});
            skLineSegment(sketch, "E3943", {"start": v(0.77, -1.38) * mm, "end": v(0.76, -1.38) * mm});
            skLineSegment(sketch, "E3944", {"start": v(0.76, -1.38) * mm, "end": v(0.76, -1.39) * mm});
            skLineSegment(sketch, "E3945", {"start": v(0.76, -1.39) * mm, "end": v(0.76, -1.39) * mm});
            skLineSegment(sketch, "E3946", {"start": v(0.76, -1.39) * mm, "end": v(0.75, -1.39) * mm});
            skLineSegment(sketch, "E3947", {"start": v(0.75, -1.39) * mm, "end": v(0.75, -1.39) * mm});
            skLineSegment(sketch, "E3948", {"start": v(0.75, -1.39) * mm, "end": v(0.74, -1.39) * mm});
            skLineSegment(sketch, "E3949", {"start": v(0.74, -1.39) * mm, "end": v(0.74, -1.4) * mm});
            skLineSegment(sketch, "E3950", {"start": v(0.74, -1.4) * mm, "end": v(-0.44, -1.4) * mm});
            skLineSegment(sketch, "E3951", {"start": v(-0.44, -1.4) * mm, "end": v(-0.44, -1.39) * mm});
            skLineSegment(sketch, "E3952", {"start": v(-0.44, -1.39) * mm, "end": v(-0.45, -1.39) * mm});
            skLineSegment(sketch, "E3953", {"start": v(-0.45, -1.39) * mm, "end": v(-0.45, -1.39) * mm});
            skLineSegment(sketch, "E3954", {"start": v(-0.45, -1.39) * mm, "end": v(-0.46, -1.39) * mm});
            skLineSegment(sketch, "E3955", {"start": v(-0.46, -1.39) * mm, "end": v(-0.46, -1.39) * mm});
            skLineSegment(sketch, "E3956", {"start": v(-0.46, -1.39) * mm, "end": v(-0.47, -1.38) * mm});
            skLineSegment(sketch, "E3957", {"start": v(-0.47, -1.38) * mm, "end": v(-0.47, -1.38) * mm});
            skLineSegment(sketch, "E3958", {"start": v(-0.47, -1.38) * mm, "end": v(-0.48, -1.38) * mm});
            skLineSegment(sketch, "E3959", {"start": v(-0.48, -1.38) * mm, "end": v(-0.48, -1.37) * mm});
            skLineSegment(sketch, "E3960", {"start": v(-0.48, -1.37) * mm, "end": v(-0.48, -1.37) * mm});
            skLineSegment(sketch, "E3961", {"start": v(-0.48, -1.37) * mm, "end": v(-0.49, -1.36) * mm});
            skLineSegment(sketch, "E3962", {"start": v(-0.49, -1.36) * mm, "end": v(-0.49, -1.36) * mm});
            skLineSegment(sketch, "E3963", {"start": v(-0.49, -1.36) * mm, "end": v(-0.49, -1.35) * mm});
            skLineSegment(sketch, "E3964", {"start": v(-0.49, -1.35) * mm, "end": v(-0.49, -1.35) * mm});
            skLineSegment(sketch, "E3965", {"start": v(-0.49, -1.35) * mm, "end": v(-0.49, -1.34) * mm});
            skLineSegment(sketch, "E3966", {"start": v(-0.49, -1.34) * mm, "end": v(-0.49, -1.34) * mm});
            skLineSegment(sketch, "E3967", {"start": v(-0.49, -1.34) * mm, "end": v(-0.49, -0.36) * mm});
            skLineSegment(sketch, "E3968", {"start": v(-0.49, -0.36) * mm, "end": v(-0.49, -0.36) * mm});
            skLineSegment(sketch, "E3969", {"start": v(-0.49, -0.36) * mm, "end": v(-0.49, -0.35) * mm});
            skLineSegment(sketch, "E3970", {"start": v(-0.49, -0.35) * mm, "end": v(-0.49, -0.35) * mm});
            skLineSegment(sketch, "E3971", {"start": v(-0.49, -0.35) * mm, "end": v(-0.49, -0.34) * mm});
            skLineSegment(sketch, "E3972", {"start": v(-0.49, -0.34) * mm, "end": v(-0.49, -0.34) * mm});
            skLineSegment(sketch, "E3973", {"start": v(-0.49, -0.34) * mm, "end": v(-0.48, -0.34) * mm});
            skLineSegment(sketch, "E3974", {"start": v(-0.48, -0.34) * mm, "end": v(-0.48, -0.33) * mm});
            skLineSegment(sketch, "E3975", {"start": v(-0.48, -0.33) * mm, "end": v(-0.48, -0.33) * mm});
            skLineSegment(sketch, "E3976", {"start": v(-0.48, -0.33) * mm, "end": v(-0.48, -0.32) * mm});
            skLineSegment(sketch, "E3977", {"start": v(-0.48, -0.32) * mm, "end": v(-0.47, -0.32) * mm});
            skLineSegment(sketch, "E3978", {"start": v(-0.47, -0.32) * mm, "end": v(-0.47, -0.32) * mm});
            skLineSegment(sketch, "E3979", {"start": v(-0.47, -0.32) * mm, "end": v(-0.46, -0.31) * mm});
            skLineSegment(sketch, "E3980", {"start": v(-0.46, -0.31) * mm, "end": v(-0.46, -0.31) * mm});
            skLineSegment(sketch, "E3981", {"start": v(-0.46, -0.31) * mm, "end": v(-0.45, -0.31) * mm});
            skLineSegment(sketch, "E3982", {"start": v(-0.45, -0.31) * mm, "end": v(-0.45, -0.31) * mm});
            skLineSegment(sketch, "E3983", {"start": v(-0.45, -0.31) * mm, "end": v(-0.44, -0.31) * mm});
            skLineSegment(sketch, "E3984", {"start": v(-0.44, -0.31) * mm, "end": v(-0.44, -0.31) * mm});
            skLineSegment(sketch, "E3985", {"start": v(-0.3, -0.48) * mm, "end": v(-0.16, -0.48) * mm});
            skLineSegment(sketch, "E3986", {"start": v(-0.16, -0.48) * mm, "end": v(-0.13, -0.48) * mm});
            skLineSegment(sketch, "E3987", {"start": v(-0.13, -0.48) * mm, "end": v(0.03, -0.48) * mm});
            skLineSegment(sketch, "E3988", {"start": v(0.03, -0.48) * mm, "end": v(0.26, -0.48) * mm});
            skLineSegment(sketch, "E3989", {"start": v(0.26, -0.48) * mm, "end": v(0.43, -0.48) * mm});
            skLineSegment(sketch, "E3990", {"start": v(0.43, -0.48) * mm, "end": v(0.47, -0.48) * mm});
            skLineSegment(sketch, "E3991", {"start": v(0.47, -0.48) * mm, "end": v(0.6, -0.48) * mm});
            skLineSegment(sketch, "E3992", {"start": v(0.6, -0.48) * mm, "end": v(0.6, -0.48) * mm});
            skLineSegment(sketch, "E3993", {"start": v(0.6, -0.48) * mm, "end": v(0.61, -0.48) * mm});
            skLineSegment(sketch, "E3994", {"start": v(0.61, -0.48) * mm, "end": v(0.61, -0.48) * mm});
            skLineSegment(sketch, "E3995", {"start": v(0.61, -0.48) * mm, "end": v(0.62, -0.48) * mm});
            skLineSegment(sketch, "E3996", {"start": v(0.62, -0.48) * mm, "end": v(0.62, -0.48) * mm});
            skLineSegment(sketch, "E3997", {"start": v(0.62, -0.48) * mm, "end": v(0.62, -0.49) * mm});
            skLineSegment(sketch, "E3998", {"start": v(0.62, -0.49) * mm, "end": v(0.62, -0.49) * mm});
            skLineSegment(sketch, "E3999", {"start": v(0.62, -0.49) * mm, "end": v(0.63, -0.5) * mm});
            skLineSegment(sketch, "E4000", {"start": v(0.63, -0.5) * mm, "end": v(0.63, -0.5) * mm});
            skLineSegment(sketch, "E4001", {"start": v(0.63, -0.5) * mm, "end": v(0.63, -1.2) * mm});
            skLineSegment(sketch, "E4002", {"start": v(0.63, -1.2) * mm, "end": v(0.63, -1.2) * mm});
            skLineSegment(sketch, "E4003", {"start": v(0.63, -1.2) * mm, "end": v(0.62, -1.21) * mm});
            skLineSegment(sketch, "E4004", {"start": v(0.62, -1.21) * mm, "end": v(0.62, -1.21) * mm});
            skLineSegment(sketch, "E4005", {"start": v(0.62, -1.21) * mm, "end": v(0.62, -1.22) * mm});
            skLineSegment(sketch, "E4006", {"start": v(0.62, -1.22) * mm, "end": v(0.62, -1.22) * mm});
            skLineSegment(sketch, "E4007", {"start": v(0.62, -1.22) * mm, "end": v(0.61, -1.22) * mm});
            skLineSegment(sketch, "E4008", {"start": v(0.61, -1.22) * mm, "end": v(0.61, -1.22) * mm});
            skLineSegment(sketch, "E4009", {"start": v(0.61, -1.22) * mm, "end": v(0.6, -1.22) * mm});
            skLineSegment(sketch, "E4010", {"start": v(0.6, -1.22) * mm, "end": v(0.6, -1.22) * mm});
            skLineSegment(sketch, "E4011", {"start": v(0.6, -1.22) * mm, "end": v(0.46, -1.22) * mm});
            skLineSegment(sketch, "E4012", {"start": v(0.46, -1.22) * mm, "end": v(-0.16, -1.22) * mm});
            skLineSegment(sketch, "E4013", {"start": v(-0.16, -1.22) * mm, "end": v(-0.3, -1.22) * mm});
            skLineSegment(sketch, "E4014", {"start": v(-0.3, -1.22) * mm, "end": v(-0.3, -1.22) * mm});
            skLineSegment(sketch, "E4015", {"start": v(-0.3, -1.22) * mm, "end": v(-0.31, -1.22) * mm});
            skLineSegment(sketch, "E4016", {"start": v(-0.31, -1.22) * mm, "end": v(-0.31, -1.22) * mm});
            skLineSegment(sketch, "E4017", {"start": v(-0.31, -1.22) * mm, "end": v(-0.32, -1.22) * mm});
            skLineSegment(sketch, "E4018", {"start": v(-0.32, -1.22) * mm, "end": v(-0.32, -1.22) * mm});
            skLineSegment(sketch, "E4019", {"start": v(-0.32, -1.22) * mm, "end": v(-0.32, -1.21) * mm});
            skLineSegment(sketch, "E4020", {"start": v(-0.32, -1.21) * mm, "end": v(-0.32, -1.21) * mm});
            skLineSegment(sketch, "E4021", {"start": v(-0.32, -1.21) * mm, "end": v(-0.33, -1.2) * mm});
            skLineSegment(sketch, "E4022", {"start": v(-0.33, -1.2) * mm, "end": v(-0.33, -1.2) * mm});
            skLineSegment(sketch, "E4023", {"start": v(-0.33, -1.2) * mm, "end": v(-0.33, -0.5) * mm});
            skLineSegment(sketch, "E4024", {"start": v(-0.33, -0.5) * mm, "end": v(-0.33, -0.5) * mm});
            skLineSegment(sketch, "E4025", {"start": v(-0.33, -0.5) * mm, "end": v(-0.32, -0.49) * mm});
            skLineSegment(sketch, "E4026", {"start": v(-0.32, -0.49) * mm, "end": v(-0.32, -0.49) * mm});
            skLineSegment(sketch, "E4027", {"start": v(-0.32, -0.49) * mm, "end": v(-0.32, -0.48) * mm});
            skLineSegment(sketch, "E4028", {"start": v(-0.32, -0.48) * mm, "end": v(-0.32, -0.48) * mm});
            skLineSegment(sketch, "E4029", {"start": v(-0.32, -0.48) * mm, "end": v(-0.31, -0.48) * mm});
            skLineSegment(sketch, "E4030", {"start": v(-0.31, -0.48) * mm, "end": v(-0.31, -0.48) * mm});
            skLineSegment(sketch, "E4031", {"start": v(-0.31, -0.48) * mm, "end": v(-0.3, -0.48) * mm});
            skLineSegment(sketch, "E4032", {"start": v(-0.3, -0.48) * mm, "end": v(-0.3, -0.48) * mm});
            skLineSegment(sketch, "E4033", {"start": v(0.03, -0.63) * mm, "end": v(0.03, -0.62) * mm});
            skLineSegment(sketch, "E4034", {"start": v(0.03, -0.62) * mm, "end": v(0.03, -0.62) * mm});
            skLineSegment(sketch, "E4035", {"start": v(0.03, -0.62) * mm, "end": v(0.03, -0.61) * mm});
            skLineSegment(sketch, "E4036", {"start": v(0.03, -0.61) * mm, "end": v(0.03, -0.61) * mm});
            skLineSegment(sketch, "E4037", {"start": v(0.03, -0.61) * mm, "end": v(0.03, -0.6) * mm});
            skLineSegment(sketch, "E4038", {"start": v(0.03, -0.6) * mm, "end": v(0.03, -0.6) * mm});
            skLineSegment(sketch, "E4039", {"start": v(0.03, -0.6) * mm, "end": v(0.04, -0.6) * mm});
            skLineSegment(sketch, "E4040", {"start": v(0.04, -0.6) * mm, "end": v(0.04, -0.6) * mm});
            skLineSegment(sketch, "E4041", {"start": v(0.04, -0.6) * mm, "end": v(0.05, -0.6) * mm});
            skLineSegment(sketch, "E4042", {"start": v(0.05, -0.6) * mm, "end": v(0.05, -0.6) * mm});
            skLineSegment(sketch, "E4043", {"start": v(0.05, -0.6) * mm, "end": v(0.06, -0.6) * mm});
            skLineSegment(sketch, "E4044", {"start": v(0.06, -0.6) * mm, "end": v(0.06, -0.6) * mm});
            skLineSegment(sketch, "E4045", {"start": v(0.06, -0.6) * mm, "end": v(0.07, -0.6) * mm});
            skLineSegment(sketch, "E4046", {"start": v(0.07, -0.6) * mm, "end": v(0.07, -0.6) * mm});
            skLineSegment(sketch, "E4047", {"start": v(0.07, -0.6) * mm, "end": v(0.07, -0.61) * mm});
            skLineSegment(sketch, "E4048", {"start": v(0.07, -0.61) * mm, "end": v(0.07, -0.61) * mm});
            skLineSegment(sketch, "E4049", {"start": v(0.07, -0.61) * mm, "end": v(0.07, -0.62) * mm});
            skLineSegment(sketch, "E4050", {"start": v(0.07, -0.62) * mm, "end": v(0.07, -0.62) * mm});
            skLineSegment(sketch, "E4051", {"start": v(0.07, -0.62) * mm, "end": v(0.07, -0.63) * mm});
            skLineSegment(sketch, "E4052", {"start": v(0.07, -0.63) * mm, "end": v(0.07, -0.63) * mm});
            skLineSegment(sketch, "E4053", {"start": v(0.07, -0.63) * mm, "end": v(0.07, -0.64) * mm});
            skLineSegment(sketch, "E4054", {"start": v(0.07, -0.64) * mm, "end": v(0.07, -0.64) * mm});
            skLineSegment(sketch, "E4055", {"start": v(0.07, -0.64) * mm, "end": v(0.06, -0.65) * mm});
            skLineSegment(sketch, "E4056", {"start": v(0.06, -0.65) * mm, "end": v(0.06, -0.65) * mm});
            skLineSegment(sketch, "E4057", {"start": v(0.06, -0.65) * mm, "end": v(0.05, -0.65) * mm});
            skLineSegment(sketch, "E4058", {"start": v(0.05, -0.65) * mm, "end": v(0.05, -0.65) * mm});
            skLineSegment(sketch, "E4059", {"start": v(0.05, -0.65) * mm, "end": v(0.04, -0.65) * mm});
            skLineSegment(sketch, "E4060", {"start": v(0.04, -0.65) * mm, "end": v(0.04, -0.65) * mm});
            skLineSegment(sketch, "E4061", {"start": v(0.04, -0.65) * mm, "end": v(0.03, -0.64) * mm});
            skLineSegment(sketch, "E4062", {"start": v(0.03, -0.64) * mm, "end": v(0.03, -0.64) * mm});
            skLineSegment(sketch, "E4063", {"start": v(0.03, -0.64) * mm, "end": v(0.03, -0.63) * mm});
            skLineSegment(sketch, "E4064", {"start": v(0.03, -0.63) * mm, "end": v(0.03, -0.63) * mm});
            skLineSegment(sketch, "E4065", {"start": v(0.05, -0.65) * mm, "end": v(0.05, -0.73) * mm});
            skLineSegment(sketch, "E4066", {"start": v(0.05, -0.73) * mm, "end": v(0.25, -0.73) * mm});
            skLineSegment(sketch, "E4067", {"start": v(0.25, -0.73) * mm, "end": v(0.25, -0.65) * mm});
            skLineSegment(sketch, "E4068", {"start": v(0.22, -0.63) * mm, "end": v(0.23, -0.62) * mm});
            skLineSegment(sketch, "E4069", {"start": v(0.23, -0.62) * mm, "end": v(0.23, -0.62) * mm});
            skLineSegment(sketch, "E4070", {"start": v(0.23, -0.62) * mm, "end": v(0.23, -0.61) * mm});
            skLineSegment(sketch, "E4071", {"start": v(0.23, -0.61) * mm, "end": v(0.23, -0.61) * mm});
            skLineSegment(sketch, "E4072", {"start": v(0.23, -0.61) * mm, "end": v(0.23, -0.6) * mm});
            skLineSegment(sketch, "E4073", {"start": v(0.23, -0.6) * mm, "end": v(0.23, -0.6) * mm});
            skLineSegment(sketch, "E4074", {"start": v(0.23, -0.6) * mm, "end": v(0.24, -0.6) * mm});
            skLineSegment(sketch, "E4075", {"start": v(0.24, -0.6) * mm, "end": v(0.24, -0.6) * mm});
            skLineSegment(sketch, "E4076", {"start": v(0.24, -0.6) * mm, "end": v(0.25, -0.6) * mm});
            skLineSegment(sketch, "E4077", {"start": v(0.25, -0.6) * mm, "end": v(0.25, -0.6) * mm});
            skLineSegment(sketch, "E4078", {"start": v(0.25, -0.6) * mm, "end": v(0.26, -0.6) * mm});
            skLineSegment(sketch, "E4079", {"start": v(0.26, -0.6) * mm, "end": v(0.26, -0.6) * mm});
            skLineSegment(sketch, "E4080", {"start": v(0.26, -0.6) * mm, "end": v(0.27, -0.6) * mm});
            skLineSegment(sketch, "E4081", {"start": v(0.27, -0.6) * mm, "end": v(0.27, -0.6) * mm});
            skLineSegment(sketch, "E4082", {"start": v(0.27, -0.6) * mm, "end": v(0.27, -0.61) * mm});
            skLineSegment(sketch, "E4083", {"start": v(0.27, -0.61) * mm, "end": v(0.27, -0.61) * mm});
            skLineSegment(sketch, "E4084", {"start": v(0.27, -0.61) * mm, "end": v(0.27, -0.62) * mm});
            skLineSegment(sketch, "E4085", {"start": v(0.27, -0.62) * mm, "end": v(0.27, -0.62) * mm});
            skLineSegment(sketch, "E4086", {"start": v(0.27, -0.62) * mm, "end": v(0.28, -0.63) * mm});
            skLineSegment(sketch, "E4087", {"start": v(0.28, -0.63) * mm, "end": v(0.27, -0.63) * mm});
            skLineSegment(sketch, "E4088", {"start": v(0.27, -0.63) * mm, "end": v(0.27, -0.63) * mm});
            skLineSegment(sketch, "E4089", {"start": v(0.27, -0.63) * mm, "end": v(0.27, -0.64) * mm});
            skLineSegment(sketch, "E4090", {"start": v(0.27, -0.64) * mm, "end": v(0.27, -0.64) * mm});
            skLineSegment(sketch, "E4091", {"start": v(0.27, -0.64) * mm, "end": v(0.26, -0.65) * mm});
            skLineSegment(sketch, "E4092", {"start": v(0.26, -0.65) * mm, "end": v(0.26, -0.65) * mm});
            skLineSegment(sketch, "E4093", {"start": v(0.26, -0.65) * mm, "end": v(0.25, -0.65) * mm});
            skLineSegment(sketch, "E4094", {"start": v(0.25, -0.65) * mm, "end": v(0.25, -0.65) * mm});
            skLineSegment(sketch, "E4095", {"start": v(0.25, -0.65) * mm, "end": v(0.24, -0.65) * mm});
            skLineSegment(sketch, "E4096", {"start": v(0.24, -0.65) * mm, "end": v(0.24, -0.65) * mm});
            skLineSegment(sketch, "E4097", {"start": v(0.24, -0.65) * mm, "end": v(0.23, -0.64) * mm});
            skLineSegment(sketch, "E4098", {"start": v(0.23, -0.64) * mm, "end": v(0.23, -0.64) * mm});
            skLineSegment(sketch, "E4099", {"start": v(0.23, -0.64) * mm, "end": v(0.23, -0.63) * mm});
            skLineSegment(sketch, "E4100", {"start": v(0.23, -0.63) * mm, "end": v(0.23, -0.63) * mm});
            skLineSegment(sketch, "E4101", {"start": v(0.23, -0.63) * mm, "end": v(0.22, -0.63) * mm});
            skLineSegment(sketch, "E4102", {"start": v(0.21, -0.7) * mm, "end": v(0.21, -0.7) * mm});
            skLineSegment(sketch, "E4103", {"start": v(0.21, -0.7) * mm, "end": v(0.21, -0.69) * mm});
            skLineSegment(sketch, "E4104", {"start": v(0.21, -0.69) * mm, "end": v(0.21, -0.69) * mm});
            skLineSegment(sketch, "E4105", {"start": v(0.21, -0.69) * mm, "end": v(0.22, -0.69) * mm});
            skLineSegment(sketch, "E4106", {"start": v(0.22, -0.69) * mm, "end": v(0.22, -0.69) * mm});
            skLineSegment(sketch, "E4107", {"start": v(0.22, -0.69) * mm, "end": v(0.23, -0.69) * mm});
            skLineSegment(sketch, "E4108", {"start": v(0.23, -0.69) * mm, "end": v(0.23, -0.69) * mm});
            skLineSegment(sketch, "E4109", {"start": v(0.23, -0.69) * mm, "end": v(0.23, -0.7) * mm});
            skLineSegment(sketch, "E4110", {"start": v(0.23, -0.7) * mm, "end": v(0.23, -0.7) * mm});
            skLineSegment(sketch, "E4111", {"start": v(0.23, -0.7) * mm, "end": v(0.22, -0.7) * mm});
            skLineSegment(sketch, "E4112", {"start": v(0.22, -0.7) * mm, "end": v(0.22, -0.7) * mm});
            skLineSegment(sketch, "E4113", {"start": v(0.22, -0.7) * mm, "end": v(0.21, -0.7) * mm});
            skLineSegment(sketch, "E4114", {"start": v(0.25, -0.73) * mm, "end": v(0.25, -0.8) * mm});
            skLineSegment(sketch, "E4115", {"start": v(0.25, -0.8) * mm, "end": v(0.05, -0.8) * mm});
            skLineSegment(sketch, "E4116", {"start": v(0.05, -0.8) * mm, "end": v(0.05, -0.73) * mm});
            skLineSegment(sketch, "E4117", {"start": v(0, -0.85) * mm, "end": v(0.3, -0.85) * mm});
            skLineSegment(sketch, "E4118", {"start": v(0.3, -0.9) * mm, "end": v(0.3, -0.98) * mm});
            skLineSegment(sketch, "E4119", {"start": v(0.3, -0.98) * mm, "end": v(0.3, -1.05) * mm});
            skLineSegment(sketch, "E4120", {"start": v(0.28, -1.08) * mm, "end": v(0.28, -1.07) * mm});
            skLineSegment(sketch, "E4121", {"start": v(0.28, -1.07) * mm, "end": v(0.28, -1.07) * mm});
            skLineSegment(sketch, "E4122", {"start": v(0.28, -1.07) * mm, "end": v(0.28, -1.06) * mm});
            skLineSegment(sketch, "E4123", {"start": v(0.28, -1.06) * mm, "end": v(0.28, -1.06) * mm});
            skLineSegment(sketch, "E4124", {"start": v(0.28, -1.06) * mm, "end": v(0.29, -1.05) * mm});
            skLineSegment(sketch, "E4125", {"start": v(0.29, -1.05) * mm, "end": v(0.29, -1.05) * mm});
            skLineSegment(sketch, "E4126", {"start": v(0.29, -1.05) * mm, "end": v(0.3, -1.05) * mm});
            skLineSegment(sketch, "E4127", {"start": v(0.3, -1.05) * mm, "end": v(0.3, -1.05) * mm});
            skLineSegment(sketch, "E4128", {"start": v(0.3, -1.05) * mm, "end": v(0.31, -1.05) * mm});
            skLineSegment(sketch, "E4129", {"start": v(0.31, -1.05) * mm, "end": v(0.31, -1.05) * mm});
            skLineSegment(sketch, "E4130", {"start": v(0.31, -1.05) * mm, "end": v(0.32, -1.06) * mm});
            skLineSegment(sketch, "E4131", {"start": v(0.32, -1.06) * mm, "end": v(0.32, -1.06) * mm});
            skLineSegment(sketch, "E4132", {"start": v(0.32, -1.06) * mm, "end": v(0.32, -1.07) * mm});
            skLineSegment(sketch, "E4133", {"start": v(0.32, -1.07) * mm, "end": v(0.32, -1.07) * mm});
            skLineSegment(sketch, "E4134", {"start": v(0.32, -1.07) * mm, "end": v(0.33, -1.08) * mm});
            skLineSegment(sketch, "E4135", {"start": v(0.33, -1.08) * mm, "end": v(0.32, -1.08) * mm});
            skLineSegment(sketch, "E4136", {"start": v(0.32, -1.08) * mm, "end": v(0.32, -1.08) * mm});
            skLineSegment(sketch, "E4137", {"start": v(0.32, -1.08) * mm, "end": v(0.32, -1.09) * mm});
            skLineSegment(sketch, "E4138", {"start": v(0.32, -1.09) * mm, "end": v(0.32, -1.09) * mm});
            skLineSegment(sketch, "E4139", {"start": v(0.32, -1.09) * mm, "end": v(0.32, -1.1) * mm});
            skLineSegment(sketch, "E4140", {"start": v(0.32, -1.1) * mm, "end": v(0.32, -1.1) * mm});
            skLineSegment(sketch, "E4141", {"start": v(0.32, -1.1) * mm, "end": v(0.31, -1.1) * mm});
            skLineSegment(sketch, "E4142", {"start": v(0.31, -1.1) * mm, "end": v(0.31, -1.1) * mm});
            skLineSegment(sketch, "E4143", {"start": v(0.31, -1.1) * mm, "end": v(0.3, -1.1) * mm});
            skLineSegment(sketch, "E4144", {"start": v(0.3, -1.1) * mm, "end": v(0.3, -1.1) * mm});
            skLineSegment(sketch, "E4145", {"start": v(0.3, -1.1) * mm, "end": v(0.29, -1.1) * mm});
            skLineSegment(sketch, "E4146", {"start": v(0.29, -1.1) * mm, "end": v(0.29, -1.1) * mm});
            skLineSegment(sketch, "E4147", {"start": v(0.29, -1.1) * mm, "end": v(0.28, -1.1) * mm});
            skLineSegment(sketch, "E4148", {"start": v(0.28, -1.1) * mm, "end": v(0.28, -1.1) * mm});
            skLineSegment(sketch, "E4149", {"start": v(0.28, -1.1) * mm, "end": v(0.28, -1.09) * mm});
            skLineSegment(sketch, "E4150", {"start": v(0.28, -1.09) * mm, "end": v(0.28, -1.09) * mm});
            skLineSegment(sketch, "E4151", {"start": v(0.28, -1.09) * mm, "end": v(0.28, -1.08) * mm});
            skLineSegment(sketch, "E4152", {"start": v(0.28, -1.08) * mm, "end": v(0.28, -1.08) * mm});
            skLineSegment(sketch, "E4153", {"start": v(0.26, -1) * mm, "end": v(0.26, -1) * mm});
            skLineSegment(sketch, "E4154", {"start": v(0.26, -1) * mm, "end": v(0.27, -1) * mm});
            skLineSegment(sketch, "E4155", {"start": v(0.27, -1) * mm, "end": v(0.27, -1) * mm});
            skLineSegment(sketch, "E4156", {"start": v(0.27, -1) * mm, "end": v(0.28, -1) * mm});
            skLineSegment(sketch, "E4157", {"start": v(0.28, -1) * mm, "end": v(0.28, -1) * mm});
            skLineSegment(sketch, "E4158", {"start": v(0.28, -1) * mm, "end": v(0.28, -1.01) * mm});
            skLineSegment(sketch, "E4159", {"start": v(0.28, -1.01) * mm, "end": v(0.28, -1.01) * mm});
            skLineSegment(sketch, "E4160", {"start": v(0.28, -1.01) * mm, "end": v(0.27, -1.01) * mm});
            skLineSegment(sketch, "E4161", {"start": v(0.27, -1.01) * mm, "end": v(0.27, -1.01) * mm});
            skLineSegment(sketch, "E4162", {"start": v(0.27, -1.01) * mm, "end": v(0.27, -1.02) * mm});
            skLineSegment(sketch, "E4163", {"start": v(0.27, -1.02) * mm, "end": v(0.27, -1.01) * mm});
            skLineSegment(sketch, "E4164", {"start": v(0.27, -1.01) * mm, "end": v(0.26, -1.01) * mm});
            skLineSegment(sketch, "E4165", {"start": v(0.26, -1.01) * mm, "end": v(0.26, -1.01) * mm});
            skLineSegment(sketch, "E4166", {"start": v(0.26, -1.01) * mm, "end": v(0.26, -1) * mm});
            skLineSegment(sketch, "E4167", {"start": v(0.3, -0.98) * mm, "end": v(0, -0.98) * mm});
            skLineSegment(sketch, "E4168", {"start": v(0, -0.98) * mm, "end": v(0, -1.05) * mm});
            skLineSegment(sketch, "E4169", {"start": v(-0.02, -1.08) * mm, "end": v(-0.02, -1.07) * mm});
            skLineSegment(sketch, "E4170", {"start": v(-0.02, -1.07) * mm, "end": v(-0.02, -1.07) * mm});
            skLineSegment(sketch, "E4171", {"start": v(-0.02, -1.07) * mm, "end": v(-0.02, -1.06) * mm});
            skLineSegment(sketch, "E4172", {"start": v(-0.02, -1.06) * mm, "end": v(-0.02, -1.06) * mm});
            skLineSegment(sketch, "E4173", {"start": v(-0.02, -1.06) * mm, "end": v(-0.01, -1.05) * mm});
            skLineSegment(sketch, "E4174", {"start": v(-0.01, -1.05) * mm, "end": v(-0.01, -1.05) * mm});
            skLineSegment(sketch, "E4175", {"start": v(-0.01, -1.05) * mm, "end": v(0, -1.05) * mm});
            skLineSegment(sketch, "E4176", {"start": v(0, -1.05) * mm, "end": v(0, -1.05) * mm});
            skLineSegment(sketch, "E4177", {"start": v(0, -1.05) * mm, "end": v(0.01, -1.05) * mm});
            skLineSegment(sketch, "E4178", {"start": v(0.01, -1.05) * mm, "end": v(0.01, -1.05) * mm});
            skLineSegment(sketch, "E4179", {"start": v(0.01, -1.05) * mm, "end": v(0.02, -1.06) * mm});
            skLineSegment(sketch, "E4180", {"start": v(0.02, -1.06) * mm, "end": v(0.02, -1.06) * mm});
            skLineSegment(sketch, "E4181", {"start": v(0.02, -1.06) * mm, "end": v(0.02, -1.07) * mm});
            skLineSegment(sketch, "E4182", {"start": v(0.02, -1.07) * mm, "end": v(0.02, -1.07) * mm});
            skLineSegment(sketch, "E4183", {"start": v(0.02, -1.07) * mm, "end": v(0.03, -1.08) * mm});
            skLineSegment(sketch, "E4184", {"start": v(0.03, -1.08) * mm, "end": v(0.02, -1.08) * mm});
            skLineSegment(sketch, "E4185", {"start": v(0.02, -1.08) * mm, "end": v(0.02, -1.08) * mm});
            skLineSegment(sketch, "E4186", {"start": v(0.02, -1.08) * mm, "end": v(0.02, -1.09) * mm});
            skLineSegment(sketch, "E4187", {"start": v(0.02, -1.09) * mm, "end": v(0.02, -1.09) * mm});
            skLineSegment(sketch, "E4188", {"start": v(0.02, -1.09) * mm, "end": v(0.02, -1.1) * mm});
            skLineSegment(sketch, "E4189", {"start": v(0.02, -1.1) * mm, "end": v(0.02, -1.1) * mm});
            skLineSegment(sketch, "E4190", {"start": v(0.02, -1.1) * mm, "end": v(0.01, -1.1) * mm});
            skLineSegment(sketch, "E4191", {"start": v(0.01, -1.1) * mm, "end": v(0.01, -1.1) * mm});
            skLineSegment(sketch, "E4192", {"start": v(0.01, -1.1) * mm, "end": v(0, -1.1) * mm});
            skLineSegment(sketch, "E4193", {"start": v(0, -1.1) * mm, "end": v(0, -1.1) * mm});
            skLineSegment(sketch, "E4194", {"start": v(0, -1.1) * mm, "end": v(-0.01, -1.1) * mm});
            skLineSegment(sketch, "E4195", {"start": v(-0.01, -1.1) * mm, "end": v(-0.01, -1.1) * mm});
            skLineSegment(sketch, "E4196", {"start": v(-0.01, -1.1) * mm, "end": v(-0.02, -1.1) * mm});
            skLineSegment(sketch, "E4197", {"start": v(-0.02, -1.1) * mm, "end": v(-0.02, -1.1) * mm});
            skLineSegment(sketch, "E4198", {"start": v(-0.02, -1.1) * mm, "end": v(-0.02, -1.09) * mm});
            skLineSegment(sketch, "E4199", {"start": v(-0.02, -1.09) * mm, "end": v(-0.02, -1.09) * mm});
            skLineSegment(sketch, "E4200", {"start": v(-0.02, -1.09) * mm, "end": v(-0.02, -1.08) * mm});
            skLineSegment(sketch, "E4201", {"start": v(-0.02, -1.08) * mm, "end": v(-0.02, -1.08) * mm});
            skLineSegment(sketch, "E4202", {"start": v(0, -0.98) * mm, "end": v(0, -0.9) * mm});
            skLineSegment(sketch, "E4203", {"start": v(0, -0.9) * mm, "end": v(0.3, -0.9) * mm});
            skLineSegment(sketch, "E4204", {"start": v(1.16, -0.81) * mm, "end": v(1.24, -0.89) * mm});
            skLineSegment(sketch, "E4205", {"start": v(1.24, -0.69) * mm, "end": v(1.16, -0.61) * mm});
            skLineSegment(sketch, "E4206", {"start": v(-1.51, -0.49) * mm, "end": v(-1.59, -0.41) * mm});
            skLineSegment(sketch, "E4207", {"start": v(-1.5, -0.29) * mm, "end": v(-1.59, -0.21) * mm});
            skLineSegment(sketch, "E4208", {"start": v(-1.51, 0.21) * mm, "end": v(-1.59, 0.29) * mm});
            skLineSegment(sketch, "E4209", {"start": v(-1.5, 0.41) * mm, "end": v(-1.59, 0.49) * mm});
            skLineSegment(sketch, "E4210", {"start": v(-1.05, 0.41) * mm, "end": v(-1.05, 0.45) * mm});
            skLineSegment(sketch, "E4211", {"start": v(-1.15, 0.45) * mm, "end": v(-1.15, 0.41) * mm});
            skLineSegment(sketch, "E4212", {"start": v(-1.15, 0.65) * mm, "end": v(-1.15, 0.68) * mm});
            skLineSegment(sketch, "E4213", {"start": v(-1.05, 0.68) * mm, "end": v(-1.05, 0.65) * mm});
            skLineSegment(sketch, "E4214", {"start": v(-1.05, 1.01) * mm, "end": v(-1.05, 1.05) * mm});
            skLineSegment(sketch, "E4215", {"start": v(-1.15, 1.05) * mm, "end": v(-1.15, 1.01) * mm});
            skLineSegment(sketch, "E4216", {"start": v(-1.15, 0.08) * mm, "end": v(-1.15, 0.05) * mm});
            skLineSegment(sketch, "E4217", {"start": v(-1.05, 0.05) * mm, "end": v(-1.05, 0.08) * mm});
            skLineSegment(sketch, "E4218", {"start": v(-1.25, 1) * mm, "end": v(-1.25, 1.05) * mm});
            skLineSegment(sketch, "E4219", {"start": v(-1.25, 0.7) * mm, "end": v(-1.25, 0.65) * mm});
            skLineSegment(sketch, "E4220", {"start": v(-1.15, -0.05) * mm, "end": v(-1.1, -0.05) * mm});
            skLineSegment(sketch, "E4221", {"start": v(-1.1, -0.15) * mm, "end": v(-1.15, -0.15) * mm});
            skLineSegment(sketch, "E4222", {"start": v(-0.85, -0.35) * mm, "end": v(-0.85, -0.4) * mm});
            skLineSegment(sketch, "E4223", {"start": v(-0.65, -0.4) * mm, "end": v(-0.65, -0.35) * mm});
            skLineSegment(sketch, "E4224", {"start": v(-0.75, -0.15) * mm, "end": v(-0.79, -0.15) * mm});
            skLineSegment(sketch, "E4225", {"start": v(-0.79, -0.05) * mm, "end": v(-0.75, -0.05) * mm});
            skLineSegment(sketch, "E4226", {"start": v(-0.85, -0.71) * mm, "end": v(-0.85, -0.75) * mm});
            skLineSegment(sketch, "E4227", {"start": v(-0.85, -0.85) * mm, "end": v(-0.85, -0.9) * mm});
            skLineSegment(sketch, "E4228", {"start": v(-0.65, -0.9) * mm, "end": v(-0.65, -0.85) * mm});
            skLineSegment(sketch, "E4229", {"start": v(-0.65, -0.75) * mm, "end": v(-0.65, -0.71) * mm});
            skLineSegment(sketch, "E4230", {"start": v(-0.65, -1.21) * mm, "end": v(-0.65, -1.25) * mm});
            skLineSegment(sketch, "E4231", {"start": v(-0.85, -1.25) * mm, "end": v(-0.85, -1.21) * mm});
            skArc(sketch, "E4232", {"start": v(1.7, -1.1) * mm, "mid": v(1.67, -1.06) * mm, "end": v(1.63, -1.1) * mm});
            skArc(sketch, "E4233", {"start": v(1.63, -1.1) * mm, "mid": v(1.67, -1.13) * mm, "end": v(1.7, -1.1) * mm});
            skArc(sketch, "E4234", {"start": v(1.7, 1.1) * mm, "mid": v(1.67, 1.13) * mm, "end": v(1.63, 1.1) * mm});
            skArc(sketch, "E4235", {"start": v(1.63, 1.1) * mm, "mid": v(1.67, 1.06) * mm, "end": v(1.7, 1.1) * mm});
            skArc(sketch, "E4236", {"start": v(-1.63, 1.1) * mm, "mid": v(-1.67, 1.13) * mm, "end": v(-1.7, 1.1) * mm});
            skArc(sketch, "E4237", {"start": v(-1.7, 1.1) * mm, "mid": v(-1.67, 1.06) * mm, "end": v(-1.63, 1.1) * mm});
            skArc(sketch, "E4238", {"start": v(-1.63, -1.1) * mm, "mid": v(-1.67, -1.06) * mm, "end": v(-1.7, -1.1) * mm});
            skArc(sketch, "E4239", {"start": v(-1.7, -1.1) * mm, "mid": v(-1.67, -1.13) * mm, "end": v(-1.63, -1.1) * mm});
            skLineSegment(sketch, "E4240", {"start": v(0.28, 0.16) * mm, "end": v(0.26, 0.18) * mm});
            skLineSegment(sketch, "E4241", {"start": v(0.26, 0.18) * mm, "end": v(0.24, 0.18) * mm});
            skLineSegment(sketch, "E4242", {"start": v(0.24, 0.18) * mm, "end": v(0.22, 0.16) * mm});
            skLineSegment(sketch, "E4243", {"start": v(0.22, 0.16) * mm, "end": v(0.22, 0.14) * mm});
            skLineSegment(sketch, "E4244", {"start": v(0.22, 0.14) * mm, "end": v(0.24, 0.12) * mm});
            skLineSegment(sketch, "E4245", {"start": v(0.24, 0.12) * mm, "end": v(0.26, 0.12) * mm});
            skLineSegment(sketch, "E4246", {"start": v(0.26, 0.12) * mm, "end": v(0.28, 0.14) * mm});
            skLineSegment(sketch, "E4247", {"start": v(0.28, 0.14) * mm, "end": v(0.28, 0.16) * mm});
            skLineSegment(sketch, "E4248", {"start": v(0.18, 0.16) * mm, "end": v(0.16, 0.18) * mm});
            skLineSegment(sketch, "E4249", {"start": v(0.16, 0.18) * mm, "end": v(0.14, 0.18) * mm});
            skLineSegment(sketch, "E4250", {"start": v(0.14, 0.18) * mm, "end": v(0.12, 0.16) * mm});
            skLineSegment(sketch, "E4251", {"start": v(0.12, 0.16) * mm, "end": v(0.12, 0.14) * mm});
            skLineSegment(sketch, "E4252", {"start": v(0.12, 0.14) * mm, "end": v(0.14, 0.12) * mm});
            skLineSegment(sketch, "E4253", {"start": v(0.14, 0.12) * mm, "end": v(0.16, 0.12) * mm});
            skLineSegment(sketch, "E4254", {"start": v(0.16, 0.12) * mm, "end": v(0.18, 0.14) * mm});
            skLineSegment(sketch, "E4255", {"start": v(0.18, 0.14) * mm, "end": v(0.18, 0.16) * mm});
            skLineSegment(sketch, "E4256", {"start": v(-0.02, 0.16) * mm, "end": v(-0.04, 0.18) * mm});
            skLineSegment(sketch, "E4257", {"start": v(-0.04, 0.18) * mm, "end": v(-0.06, 0.18) * mm});
            skLineSegment(sketch, "E4258", {"start": v(-0.06, 0.18) * mm, "end": v(-0.08, 0.16) * mm});
            skLineSegment(sketch, "E4259", {"start": v(-0.08, 0.16) * mm, "end": v(-0.08, 0.14) * mm});
            skLineSegment(sketch, "E4260", {"start": v(-0.08, 0.14) * mm, "end": v(-0.06, 0.12) * mm});
            skLineSegment(sketch, "E4261", {"start": v(-0.06, 0.12) * mm, "end": v(-0.04, 0.12) * mm});
            skLineSegment(sketch, "E4262", {"start": v(-0.04, 0.12) * mm, "end": v(-0.02, 0.14) * mm});
            skLineSegment(sketch, "E4263", {"start": v(-0.02, 0.14) * mm, "end": v(-0.02, 0.16) * mm});
            skLineSegment(sketch, "E4264", {"start": v(-0.12, 0.16) * mm, "end": v(-0.14, 0.18) * mm});
            skLineSegment(sketch, "E4265", {"start": v(-0.14, 0.18) * mm, "end": v(-0.16, 0.18) * mm});
            skLineSegment(sketch, "E4266", {"start": v(-0.16, 0.18) * mm, "end": v(-0.18, 0.16) * mm});
            skLineSegment(sketch, "E4267", {"start": v(-0.18, 0.16) * mm, "end": v(-0.18, 0.14) * mm});
            skLineSegment(sketch, "E4268", {"start": v(-0.18, 0.14) * mm, "end": v(-0.16, 0.12) * mm});
            skLineSegment(sketch, "E4269", {"start": v(-0.16, 0.12) * mm, "end": v(-0.14, 0.12) * mm});
            skLineSegment(sketch, "E4270", {"start": v(-0.14, 0.12) * mm, "end": v(-0.12, 0.14) * mm});
            skLineSegment(sketch, "E4271", {"start": v(-0.12, 0.14) * mm, "end": v(-0.12, 0.16) * mm});
            skLineSegment(sketch, "E4272", {"start": v(-0.22, 0.16) * mm, "end": v(-0.24, 0.18) * mm});
            skLineSegment(sketch, "E4273", {"start": v(-0.24, 0.18) * mm, "end": v(-0.26, 0.18) * mm});
            skLineSegment(sketch, "E4274", {"start": v(-0.26, 0.18) * mm, "end": v(-0.28, 0.16) * mm});
            skLineSegment(sketch, "E4275", {"start": v(-0.28, 0.16) * mm, "end": v(-0.28, 0.14) * mm});
            skLineSegment(sketch, "E4276", {"start": v(-0.28, 0.14) * mm, "end": v(-0.26, 0.12) * mm});
            skLineSegment(sketch, "E4277", {"start": v(-0.26, 0.12) * mm, "end": v(-0.24, 0.12) * mm});
            skLineSegment(sketch, "E4278", {"start": v(-0.24, 0.12) * mm, "end": v(-0.22, 0.14) * mm});
            skLineSegment(sketch, "E4279", {"start": v(-0.22, 0.14) * mm, "end": v(-0.22, 0.16) * mm});
            skLineSegment(sketch, "E4280", {"start": v(-0.32, 0.16) * mm, "end": v(-0.34, 0.18) * mm});
            skLineSegment(sketch, "E4281", {"start": v(-0.34, 0.18) * mm, "end": v(-0.36, 0.18) * mm});
            skLineSegment(sketch, "E4282", {"start": v(-0.36, 0.18) * mm, "end": v(-0.38, 0.16) * mm});
            skLineSegment(sketch, "E4283", {"start": v(-0.38, 0.16) * mm, "end": v(-0.38, 0.14) * mm});
            skLineSegment(sketch, "E4284", {"start": v(-0.38, 0.14) * mm, "end": v(-0.36, 0.12) * mm});
            skLineSegment(sketch, "E4285", {"start": v(-0.36, 0.12) * mm, "end": v(-0.34, 0.12) * mm});
            skLineSegment(sketch, "E4286", {"start": v(-0.34, 0.12) * mm, "end": v(-0.32, 0.14) * mm});
            skLineSegment(sketch, "E4287", {"start": v(-0.32, 0.14) * mm, "end": v(-0.32, 0.16) * mm});
            skLineSegment(sketch, "E4288", {"start": v(-0.32, 0.56) * mm, "end": v(-0.34, 0.58) * mm});
            skLineSegment(sketch, "E4289", {"start": v(-0.34, 0.58) * mm, "end": v(-0.36, 0.58) * mm});
            skLineSegment(sketch, "E4290", {"start": v(-0.36, 0.58) * mm, "end": v(-0.38, 0.56) * mm});
            skLineSegment(sketch, "E4291", {"start": v(-0.38, 0.56) * mm, "end": v(-0.38, 0.54) * mm});
            skLineSegment(sketch, "E4292", {"start": v(-0.38, 0.54) * mm, "end": v(-0.36, 0.52) * mm});
            skLineSegment(sketch, "E4293", {"start": v(-0.36, 0.52) * mm, "end": v(-0.34, 0.52) * mm});
            skLineSegment(sketch, "E4294", {"start": v(-0.34, 0.52) * mm, "end": v(-0.32, 0.54) * mm});
            skLineSegment(sketch, "E4295", {"start": v(-0.32, 0.54) * mm, "end": v(-0.32, 0.56) * mm});
            skLineSegment(sketch, "E4296", {"start": v(-0.22, 0.56) * mm, "end": v(-0.24, 0.58) * mm});
            skLineSegment(sketch, "E4297", {"start": v(-0.24, 0.58) * mm, "end": v(-0.26, 0.58) * mm});
            skLineSegment(sketch, "E4298", {"start": v(-0.26, 0.58) * mm, "end": v(-0.28, 0.56) * mm});
            skLineSegment(sketch, "E4299", {"start": v(-0.28, 0.56) * mm, "end": v(-0.28, 0.54) * mm});
            skLineSegment(sketch, "E4300", {"start": v(-0.28, 0.54) * mm, "end": v(-0.26, 0.52) * mm});
            skLineSegment(sketch, "E4301", {"start": v(-0.26, 0.52) * mm, "end": v(-0.24, 0.52) * mm});
            skLineSegment(sketch, "E4302", {"start": v(-0.24, 0.52) * mm, "end": v(-0.22, 0.54) * mm});
            skLineSegment(sketch, "E4303", {"start": v(-0.22, 0.54) * mm, "end": v(-0.22, 0.56) * mm});
            skLineSegment(sketch, "E4304", {"start": v(-0.12, 0.56) * mm, "end": v(-0.14, 0.58) * mm});
            skLineSegment(sketch, "E4305", {"start": v(-0.14, 0.58) * mm, "end": v(-0.16, 0.58) * mm});
            skLineSegment(sketch, "E4306", {"start": v(-0.16, 0.58) * mm, "end": v(-0.18, 0.56) * mm});
            skLineSegment(sketch, "E4307", {"start": v(-0.18, 0.56) * mm, "end": v(-0.18, 0.54) * mm});
            skLineSegment(sketch, "E4308", {"start": v(-0.18, 0.54) * mm, "end": v(-0.16, 0.52) * mm});
            skLineSegment(sketch, "E4309", {"start": v(-0.16, 0.52) * mm, "end": v(-0.14, 0.52) * mm});
            skLineSegment(sketch, "E4310", {"start": v(-0.14, 0.52) * mm, "end": v(-0.12, 0.54) * mm});
            skLineSegment(sketch, "E4311", {"start": v(-0.12, 0.54) * mm, "end": v(-0.12, 0.56) * mm});
            skLineSegment(sketch, "E4312", {"start": v(-0.02, 0.56) * mm, "end": v(-0.04, 0.58) * mm});
            skLineSegment(sketch, "E4313", {"start": v(-0.04, 0.58) * mm, "end": v(-0.06, 0.58) * mm});
            skLineSegment(sketch, "E4314", {"start": v(-0.06, 0.58) * mm, "end": v(-0.08, 0.56) * mm});
            skLineSegment(sketch, "E4315", {"start": v(-0.08, 0.56) * mm, "end": v(-0.08, 0.54) * mm});
            skLineSegment(sketch, "E4316", {"start": v(-0.08, 0.54) * mm, "end": v(-0.06, 0.52) * mm});
            skLineSegment(sketch, "E4317", {"start": v(-0.06, 0.52) * mm, "end": v(-0.04, 0.52) * mm});
            skLineSegment(sketch, "E4318", {"start": v(-0.04, 0.52) * mm, "end": v(-0.02, 0.54) * mm});
            skLineSegment(sketch, "E4319", {"start": v(-0.02, 0.54) * mm, "end": v(-0.02, 0.56) * mm});
            skLineSegment(sketch, "E4320", {"start": v(0.18, 0.56) * mm, "end": v(0.16, 0.58) * mm});
            skLineSegment(sketch, "E4321", {"start": v(0.16, 0.58) * mm, "end": v(0.14, 0.58) * mm});
            skLineSegment(sketch, "E4322", {"start": v(0.14, 0.58) * mm, "end": v(0.12, 0.56) * mm});
            skLineSegment(sketch, "E4323", {"start": v(0.12, 0.56) * mm, "end": v(0.12, 0.54) * mm});
            skLineSegment(sketch, "E4324", {"start": v(0.12, 0.54) * mm, "end": v(0.14, 0.52) * mm});
            skLineSegment(sketch, "E4325", {"start": v(0.14, 0.52) * mm, "end": v(0.16, 0.52) * mm});
            skLineSegment(sketch, "E4326", {"start": v(0.16, 0.52) * mm, "end": v(0.18, 0.54) * mm});
            skLineSegment(sketch, "E4327", {"start": v(0.18, 0.54) * mm, "end": v(0.18, 0.56) * mm});
            skLineSegment(sketch, "E4328", {"start": v(0.28, 0.56) * mm, "end": v(0.26, 0.58) * mm});
            skLineSegment(sketch, "E4329", {"start": v(0.26, 0.58) * mm, "end": v(0.24, 0.58) * mm});
            skLineSegment(sketch, "E4330", {"start": v(0.24, 0.58) * mm, "end": v(0.22, 0.56) * mm});
            skLineSegment(sketch, "E4331", {"start": v(0.22, 0.56) * mm, "end": v(0.22, 0.54) * mm});
            skLineSegment(sketch, "E4332", {"start": v(0.22, 0.54) * mm, "end": v(0.24, 0.52) * mm});
            skLineSegment(sketch, "E4333", {"start": v(0.24, 0.52) * mm, "end": v(0.26, 0.52) * mm});
            skLineSegment(sketch, "E4334", {"start": v(0.26, 0.52) * mm, "end": v(0.28, 0.54) * mm});
            skLineSegment(sketch, "E4335", {"start": v(0.28, 0.54) * mm, "end": v(0.28, 0.56) * mm});
            skLineSegment(sketch, "E4336", {"start": v(-0.42, 0.66) * mm, "end": v(-0.44, 0.68) * mm});
            skLineSegment(sketch, "E4337", {"start": v(-0.44, 0.68) * mm, "end": v(-0.46, 0.68) * mm});
            skLineSegment(sketch, "E4338", {"start": v(-0.46, 0.68) * mm, "end": v(-0.48, 0.66) * mm});
            skLineSegment(sketch, "E4339", {"start": v(-0.48, 0.66) * mm, "end": v(-0.48, 0.64) * mm});
            skLineSegment(sketch, "E4340", {"start": v(-0.48, 0.64) * mm, "end": v(-0.46, 0.62) * mm});
            skLineSegment(sketch, "E4341", {"start": v(-0.46, 0.62) * mm, "end": v(-0.44, 0.62) * mm});
            skLineSegment(sketch, "E4342", {"start": v(-0.44, 0.62) * mm, "end": v(-0.42, 0.64) * mm});
            skLineSegment(sketch, "E4343", {"start": v(-0.42, 0.64) * mm, "end": v(-0.42, 0.66) * mm});
            skLineSegment(sketch, "E4344", {"start": v(-0.52, 0.66) * mm, "end": v(-0.54, 0.68) * mm});
            skLineSegment(sketch, "E4345", {"start": v(-0.54, 0.68) * mm, "end": v(-0.56, 0.68) * mm});
            skLineSegment(sketch, "E4346", {"start": v(-0.56, 0.68) * mm, "end": v(-0.58, 0.66) * mm});
            skLineSegment(sketch, "E4347", {"start": v(-0.58, 0.66) * mm, "end": v(-0.58, 0.64) * mm});
            skLineSegment(sketch, "E4348", {"start": v(-0.58, 0.64) * mm, "end": v(-0.56, 0.62) * mm});
            skLineSegment(sketch, "E4349", {"start": v(-0.56, 0.62) * mm, "end": v(-0.54, 0.62) * mm});
            skLineSegment(sketch, "E4350", {"start": v(-0.54, 0.62) * mm, "end": v(-0.52, 0.64) * mm});
            skLineSegment(sketch, "E4351", {"start": v(-0.52, 0.64) * mm, "end": v(-0.52, 0.66) * mm});
            skLineSegment(sketch, "E4352", {"start": v(-0.62, 0.66) * mm, "end": v(-0.64, 0.68) * mm});
            skLineSegment(sketch, "E4353", {"start": v(-0.64, 0.68) * mm, "end": v(-0.66, 0.68) * mm});
            skLineSegment(sketch, "E4354", {"start": v(-0.66, 0.68) * mm, "end": v(-0.68, 0.66) * mm});
            skLineSegment(sketch, "E4355", {"start": v(-0.68, 0.66) * mm, "end": v(-0.68, 0.64) * mm});
            skLineSegment(sketch, "E4356", {"start": v(-0.68, 0.64) * mm, "end": v(-0.66, 0.62) * mm});
            skLineSegment(sketch, "E4357", {"start": v(-0.66, 0.62) * mm, "end": v(-0.64, 0.62) * mm});
            skLineSegment(sketch, "E4358", {"start": v(-0.64, 0.62) * mm, "end": v(-0.62, 0.64) * mm});
            skLineSegment(sketch, "E4359", {"start": v(-0.62, 0.64) * mm, "end": v(-0.62, 0.66) * mm});
            skLineSegment(sketch, "E4360", {"start": v(-0.72, 0.66) * mm, "end": v(-0.74, 0.68) * mm});
            skLineSegment(sketch, "E4361", {"start": v(-0.74, 0.68) * mm, "end": v(-0.76, 0.68) * mm});
            skLineSegment(sketch, "E4362", {"start": v(-0.76, 0.68) * mm, "end": v(-0.78, 0.66) * mm});
            skLineSegment(sketch, "E4363", {"start": v(-0.78, 0.66) * mm, "end": v(-0.78, 0.64) * mm});
            skLineSegment(sketch, "E4364", {"start": v(-0.78, 0.64) * mm, "end": v(-0.76, 0.62) * mm});
            skLineSegment(sketch, "E4365", {"start": v(-0.76, 0.62) * mm, "end": v(-0.74, 0.62) * mm});
            skLineSegment(sketch, "E4366", {"start": v(-0.74, 0.62) * mm, "end": v(-0.72, 0.64) * mm});
            skLineSegment(sketch, "E4367", {"start": v(-0.72, 0.64) * mm, "end": v(-0.72, 0.66) * mm});
            skLineSegment(sketch, "E4368", {"start": v(-0.82, 0.66) * mm, "end": v(-0.84, 0.68) * mm});
            skLineSegment(sketch, "E4369", {"start": v(-0.84, 0.68) * mm, "end": v(-0.86, 0.68) * mm});
            skLineSegment(sketch, "E4370", {"start": v(-0.86, 0.68) * mm, "end": v(-0.88, 0.66) * mm});
            skLineSegment(sketch, "E4371", {"start": v(-0.88, 0.66) * mm, "end": v(-0.88, 0.64) * mm});
            skLineSegment(sketch, "E4372", {"start": v(-0.88, 0.64) * mm, "end": v(-0.86, 0.62) * mm});
            skLineSegment(sketch, "E4373", {"start": v(-0.86, 0.62) * mm, "end": v(-0.84, 0.62) * mm});
            skLineSegment(sketch, "E4374", {"start": v(-0.84, 0.62) * mm, "end": v(-0.82, 0.64) * mm});
            skLineSegment(sketch, "E4375", {"start": v(-0.82, 0.64) * mm, "end": v(-0.82, 0.66) * mm});
            skLineSegment(sketch, "E4376", {"start": v(-0.92, 0.66) * mm, "end": v(-0.94, 0.68) * mm});
            skLineSegment(sketch, "E4377", {"start": v(-0.94, 0.68) * mm, "end": v(-0.96, 0.68) * mm});
            skLineSegment(sketch, "E4378", {"start": v(-0.96, 0.68) * mm, "end": v(-0.98, 0.66) * mm});
            skLineSegment(sketch, "E4379", {"start": v(-0.98, 0.66) * mm, "end": v(-0.98, 0.64) * mm});
            skLineSegment(sketch, "E4380", {"start": v(-0.98, 0.64) * mm, "end": v(-0.96, 0.62) * mm});
            skLineSegment(sketch, "E4381", {"start": v(-0.96, 0.62) * mm, "end": v(-0.94, 0.62) * mm});
            skLineSegment(sketch, "E4382", {"start": v(-0.94, 0.62) * mm, "end": v(-0.92, 0.64) * mm});
            skLineSegment(sketch, "E4383", {"start": v(-0.92, 0.64) * mm, "end": v(-0.92, 0.66) * mm});
            skLineSegment(sketch, "E4384", {"start": v(-0.92, 1.06) * mm, "end": v(-0.94, 1.08) * mm});
            skLineSegment(sketch, "E4385", {"start": v(-0.94, 1.08) * mm, "end": v(-0.96, 1.08) * mm});
            skLineSegment(sketch, "E4386", {"start": v(-0.96, 1.08) * mm, "end": v(-0.98, 1.06) * mm});
            skLineSegment(sketch, "E4387", {"start": v(-0.98, 1.06) * mm, "end": v(-0.98, 1.04) * mm});
            skLineSegment(sketch, "E4388", {"start": v(-0.98, 1.04) * mm, "end": v(-0.96, 1.02) * mm});
            skLineSegment(sketch, "E4389", {"start": v(-0.96, 1.02) * mm, "end": v(-0.94, 1.02) * mm});
            skLineSegment(sketch, "E4390", {"start": v(-0.94, 1.02) * mm, "end": v(-0.92, 1.04) * mm});
            skLineSegment(sketch, "E4391", {"start": v(-0.92, 1.04) * mm, "end": v(-0.92, 1.06) * mm});
            skLineSegment(sketch, "E4392", {"start": v(-0.82, 1.06) * mm, "end": v(-0.84, 1.08) * mm});
            skLineSegment(sketch, "E4393", {"start": v(-0.84, 1.08) * mm, "end": v(-0.86, 1.08) * mm});
            skLineSegment(sketch, "E4394", {"start": v(-0.86, 1.08) * mm, "end": v(-0.88, 1.06) * mm});
            skLineSegment(sketch, "E4395", {"start": v(-0.88, 1.06) * mm, "end": v(-0.88, 1.04) * mm});
            skLineSegment(sketch, "E4396", {"start": v(-0.88, 1.04) * mm, "end": v(-0.86, 1.02) * mm});
            skLineSegment(sketch, "E4397", {"start": v(-0.86, 1.02) * mm, "end": v(-0.84, 1.02) * mm});
            skLineSegment(sketch, "E4398", {"start": v(-0.84, 1.02) * mm, "end": v(-0.82, 1.04) * mm});
            skLineSegment(sketch, "E4399", {"start": v(-0.82, 1.04) * mm, "end": v(-0.82, 1.06) * mm});
            skLineSegment(sketch, "E4400", {"start": v(-0.72, 1.06) * mm, "end": v(-0.74, 1.08) * mm});
            skLineSegment(sketch, "E4401", {"start": v(-0.74, 1.08) * mm, "end": v(-0.76, 1.08) * mm});
            skLineSegment(sketch, "E4402", {"start": v(-0.76, 1.08) * mm, "end": v(-0.78, 1.06) * mm});
            skLineSegment(sketch, "E4403", {"start": v(-0.78, 1.06) * mm, "end": v(-0.78, 1.04) * mm});
            skLineSegment(sketch, "E4404", {"start": v(-0.78, 1.04) * mm, "end": v(-0.76, 1.02) * mm});
            skLineSegment(sketch, "E4405", {"start": v(-0.76, 1.02) * mm, "end": v(-0.74, 1.02) * mm});
            skLineSegment(sketch, "E4406", {"start": v(-0.74, 1.02) * mm, "end": v(-0.72, 1.04) * mm});
            skLineSegment(sketch, "E4407", {"start": v(-0.72, 1.04) * mm, "end": v(-0.72, 1.06) * mm});
            skLineSegment(sketch, "E4408", {"start": v(-0.62, 1.06) * mm, "end": v(-0.64, 1.08) * mm});
            skLineSegment(sketch, "E4409", {"start": v(-0.64, 1.08) * mm, "end": v(-0.66, 1.08) * mm});
            skLineSegment(sketch, "E4410", {"start": v(-0.66, 1.08) * mm, "end": v(-0.68, 1.06) * mm});
            skLineSegment(sketch, "E4411", {"start": v(-0.68, 1.06) * mm, "end": v(-0.68, 1.04) * mm});
            skLineSegment(sketch, "E4412", {"start": v(-0.68, 1.04) * mm, "end": v(-0.66, 1.02) * mm});
            skLineSegment(sketch, "E4413", {"start": v(-0.66, 1.02) * mm, "end": v(-0.64, 1.02) * mm});
            skLineSegment(sketch, "E4414", {"start": v(-0.64, 1.02) * mm, "end": v(-0.62, 1.04) * mm});
            skLineSegment(sketch, "E4415", {"start": v(-0.62, 1.04) * mm, "end": v(-0.62, 1.06) * mm});
            skLineSegment(sketch, "E4416", {"start": v(-0.52, 1.06) * mm, "end": v(-0.54, 1.08) * mm});
            skLineSegment(sketch, "E4417", {"start": v(-0.54, 1.08) * mm, "end": v(-0.56, 1.08) * mm});
            skLineSegment(sketch, "E4418", {"start": v(-0.56, 1.08) * mm, "end": v(-0.58, 1.06) * mm});
            skLineSegment(sketch, "E4419", {"start": v(-0.58, 1.06) * mm, "end": v(-0.58, 1.04) * mm});
            skLineSegment(sketch, "E4420", {"start": v(-0.58, 1.04) * mm, "end": v(-0.56, 1.02) * mm});
            skLineSegment(sketch, "E4421", {"start": v(-0.56, 1.02) * mm, "end": v(-0.54, 1.02) * mm});
            skLineSegment(sketch, "E4422", {"start": v(-0.54, 1.02) * mm, "end": v(-0.52, 1.04) * mm});
            skLineSegment(sketch, "E4423", {"start": v(-0.52, 1.04) * mm, "end": v(-0.52, 1.06) * mm});
            skLineSegment(sketch, "E4424", {"start": v(-0.42, 1.06) * mm, "end": v(-0.44, 1.08) * mm});
            skLineSegment(sketch, "E4425", {"start": v(-0.44, 1.08) * mm, "end": v(-0.46, 1.08) * mm});
            skLineSegment(sketch, "E4426", {"start": v(-0.46, 1.08) * mm, "end": v(-0.48, 1.06) * mm});
            skLineSegment(sketch, "E4427", {"start": v(-0.48, 1.06) * mm, "end": v(-0.48, 1.04) * mm});
            skLineSegment(sketch, "E4428", {"start": v(-0.48, 1.04) * mm, "end": v(-0.46, 1.02) * mm});
            skLineSegment(sketch, "E4429", {"start": v(-0.46, 1.02) * mm, "end": v(-0.44, 1.02) * mm});
            skLineSegment(sketch, "E4430", {"start": v(-0.44, 1.02) * mm, "end": v(-0.42, 1.04) * mm});
            skLineSegment(sketch, "E4431", {"start": v(-0.42, 1.04) * mm, "end": v(-0.42, 1.06) * mm});
            skLineSegment(sketch, "E4432", {"start": v(0.69, 1.21) * mm, "end": v(0.67, 1.23) * mm});
            skLineSegment(sketch, "E4433", {"start": v(0.67, 1.23) * mm, "end": v(0.65, 1.23) * mm});
            skLineSegment(sketch, "E4434", {"start": v(0.65, 1.23) * mm, "end": v(0.63, 1.21) * mm});
            skLineSegment(sketch, "E4435", {"start": v(0.63, 1.21) * mm, "end": v(0.63, 1.19) * mm});
            skLineSegment(sketch, "E4436", {"start": v(0.63, 1.19) * mm, "end": v(0.65, 1.17) * mm});
            skLineSegment(sketch, "E4437", {"start": v(0.65, 1.17) * mm, "end": v(0.67, 1.17) * mm});
            skLineSegment(sketch, "E4438", {"start": v(0.67, 1.17) * mm, "end": v(0.69, 1.19) * mm});
            skLineSegment(sketch, "E4439", {"start": v(0.69, 1.19) * mm, "end": v(0.69, 1.21) * mm});
            skLineSegment(sketch, "E4440", {"start": v(0.89, 1.21) * mm, "end": v(0.87, 1.23) * mm});
            skLineSegment(sketch, "E4441", {"start": v(0.87, 1.23) * mm, "end": v(0.85, 1.23) * mm});
            skLineSegment(sketch, "E4442", {"start": v(0.85, 1.23) * mm, "end": v(0.83, 1.21) * mm});
            skLineSegment(sketch, "E4443", {"start": v(0.83, 1.21) * mm, "end": v(0.83, 1.19) * mm});
            skLineSegment(sketch, "E4444", {"start": v(0.83, 1.19) * mm, "end": v(0.85, 1.17) * mm});
            skLineSegment(sketch, "E4445", {"start": v(0.85, 1.17) * mm, "end": v(0.87, 1.17) * mm});
            skLineSegment(sketch, "E4446", {"start": v(0.87, 1.17) * mm, "end": v(0.89, 1.19) * mm});
            skLineSegment(sketch, "E4447", {"start": v(0.89, 1.19) * mm, "end": v(0.89, 1.21) * mm});
            skLineSegment(sketch, "E4448", {"start": v(1.09, 1.21) * mm, "end": v(1.07, 1.23) * mm});
            skLineSegment(sketch, "E4449", {"start": v(1.07, 1.23) * mm, "end": v(1.05, 1.23) * mm});
            skLineSegment(sketch, "E4450", {"start": v(1.05, 1.23) * mm, "end": v(1.03, 1.21) * mm});
            skLineSegment(sketch, "E4451", {"start": v(1.03, 1.21) * mm, "end": v(1.03, 1.19) * mm});
            skLineSegment(sketch, "E4452", {"start": v(1.03, 1.19) * mm, "end": v(1.05, 1.17) * mm});
            skLineSegment(sketch, "E4453", {"start": v(1.05, 1.17) * mm, "end": v(1.07, 1.17) * mm});
            skLineSegment(sketch, "E4454", {"start": v(1.07, 1.17) * mm, "end": v(1.09, 1.19) * mm});
            skLineSegment(sketch, "E4455", {"start": v(1.09, 1.19) * mm, "end": v(1.09, 1.21) * mm});
            skLineSegment(sketch, "E4456", {"start": v(1.29, 1.21) * mm, "end": v(1.27, 1.23) * mm});
            skLineSegment(sketch, "E4457", {"start": v(1.27, 1.23) * mm, "end": v(1.25, 1.23) * mm});
            skLineSegment(sketch, "E4458", {"start": v(1.25, 1.23) * mm, "end": v(1.23, 1.21) * mm});
            skLineSegment(sketch, "E4459", {"start": v(1.23, 1.21) * mm, "end": v(1.23, 1.19) * mm});
            skLineSegment(sketch, "E4460", {"start": v(1.23, 1.19) * mm, "end": v(1.25, 1.17) * mm});
            skLineSegment(sketch, "E4461", {"start": v(1.25, 1.17) * mm, "end": v(1.27, 1.17) * mm});
            skLineSegment(sketch, "E4462", {"start": v(1.27, 1.17) * mm, "end": v(1.29, 1.19) * mm});
            skLineSegment(sketch, "E4463", {"start": v(1.29, 1.19) * mm, "end": v(1.29, 1.21) * mm});
            skArc(sketch, "E4464", {"start": v(0.75, 1.2) * mm, "mid": v(0.74, 1.21) * mm, "end": v(0.73, 1.2) * mm});
            skArc(sketch, "E4465", {"start": v(0.73, 1.2) * mm, "mid": v(0.74, 1.19) * mm, "end": v(0.75, 1.2) * mm});
            skArc(sketch, "E4466", {"start": v(0.95, 1.2) * mm, "mid": v(0.94, 1.21) * mm, "end": v(0.93, 1.2) * mm});
            skArc(sketch, "E4467", {"start": v(0.93, 1.2) * mm, "mid": v(0.94, 1.19) * mm, "end": v(0.95, 1.2) * mm});
            skArc(sketch, "E4468", {"start": v(1.15, 1.2) * mm, "mid": v(1.14, 1.21) * mm, "end": v(1.13, 1.2) * mm});
            skArc(sketch, "E4469", {"start": v(1.13, 1.2) * mm, "mid": v(1.14, 1.19) * mm, "end": v(1.15, 1.2) * mm});
            skArc(sketch, "E4470", {"start": v(1.35, 1.2) * mm, "mid": v(1.34, 1.21) * mm, "end": v(1.33, 1.2) * mm});
            skArc(sketch, "E4471", {"start": v(1.33, 1.2) * mm, "mid": v(1.34, 1.19) * mm, "end": v(1.35, 1.2) * mm});
            skLineSegment(sketch, "E4472", {"start": v(0.62, -0.42) * mm, "end": v(0.58, -0.38) * mm});
            skLineSegment(sketch, "E4473", {"start": v(0.58, -0.38) * mm, "end": v(0.51, -0.38) * mm});
            skLineSegment(sketch, "E4474", {"start": v(0.51, -0.38) * mm, "end": v(0.47, -0.42) * mm});
            skLineSegment(sketch, "E4475", {"start": v(0.47, -0.42) * mm, "end": v(0.47, -0.49) * mm});
            skLineSegment(sketch, "E4476", {"start": v(0.47, -0.49) * mm, "end": v(0.51, -0.53) * mm});
            skLineSegment(sketch, "E4477", {"start": v(0.51, -0.53) * mm, "end": v(0.58, -0.53) * mm});
            skLineSegment(sketch, "E4478", {"start": v(0.58, -0.53) * mm, "end": v(0.62, -0.49) * mm});
            skLineSegment(sketch, "E4479", {"start": v(0.62, -0.49) * mm, "end": v(0.62, -0.42) * mm});
            skLineSegment(sketch, "E4480", {"start": v(0.42, -0.42) * mm, "end": v(0.38, -0.38) * mm});
            skLineSegment(sketch, "E4481", {"start": v(0.38, -0.38) * mm, "end": v(0.32, -0.38) * mm});
            skLineSegment(sketch, "E4482", {"start": v(0.32, -0.38) * mm, "end": v(0.27, -0.42) * mm});
            skLineSegment(sketch, "E4483", {"start": v(0.27, -0.42) * mm, "end": v(0.27, -0.49) * mm});
            skLineSegment(sketch, "E4484", {"start": v(0.27, -0.49) * mm, "end": v(0.32, -0.53) * mm});
            skLineSegment(sketch, "E4485", {"start": v(0.32, -0.53) * mm, "end": v(0.38, -0.53) * mm});
            skLineSegment(sketch, "E4486", {"start": v(0.38, -0.53) * mm, "end": v(0.42, -0.49) * mm});
            skLineSegment(sketch, "E4487", {"start": v(0.42, -0.49) * mm, "end": v(0.42, -0.42) * mm});
            skLineSegment(sketch, "E4488", {"start": v(0.03, -0.42) * mm, "end": v(-0.02, -0.38) * mm});
            skLineSegment(sketch, "E4489", {"start": v(-0.02, -0.38) * mm, "end": v(-0.08, -0.38) * mm});
            skLineSegment(sketch, "E4490", {"start": v(-0.08, -0.38) * mm, "end": v(-0.12, -0.42) * mm});
            skLineSegment(sketch, "E4491", {"start": v(-0.12, -0.42) * mm, "end": v(-0.12, -0.49) * mm});
            skLineSegment(sketch, "E4492", {"start": v(-0.12, -0.49) * mm, "end": v(-0.08, -0.53) * mm});
            skLineSegment(sketch, "E4493", {"start": v(-0.08, -0.53) * mm, "end": v(-0.02, -0.53) * mm});
            skLineSegment(sketch, "E4494", {"start": v(-0.02, -0.53) * mm, "end": v(0.03, -0.49) * mm});
            skLineSegment(sketch, "E4495", {"start": v(0.03, -0.49) * mm, "end": v(0.03, -0.42) * mm});
            skLineSegment(sketch, "E4496", {"start": v(-0.17, -0.42) * mm, "end": v(-0.21, -0.38) * mm});
            skLineSegment(sketch, "E4497", {"start": v(-0.21, -0.38) * mm, "end": v(-0.28, -0.38) * mm});
            skLineSegment(sketch, "E4498", {"start": v(-0.28, -0.38) * mm, "end": v(-0.32, -0.42) * mm});
            skLineSegment(sketch, "E4499", {"start": v(-0.32, -0.42) * mm, "end": v(-0.32, -0.49) * mm});
            skLineSegment(sketch, "E4500", {"start": v(-0.32, -0.49) * mm, "end": v(-0.28, -0.53) * mm});
            skLineSegment(sketch, "E4501", {"start": v(-0.28, -0.53) * mm, "end": v(-0.21, -0.53) * mm});
            skLineSegment(sketch, "E4502", {"start": v(-0.21, -0.53) * mm, "end": v(-0.17, -0.49) * mm});
            skLineSegment(sketch, "E4503", {"start": v(-0.17, -0.49) * mm, "end": v(-0.17, -0.42) * mm});
            skLineSegment(sketch, "E4504", {"start": v(-0.17, -1.21) * mm, "end": v(-0.21, -1.17) * mm});
            skLineSegment(sketch, "E4505", {"start": v(-0.21, -1.17) * mm, "end": v(-0.28, -1.17) * mm});
            skLineSegment(sketch, "E4506", {"start": v(-0.28, -1.17) * mm, "end": v(-0.32, -1.21) * mm});
            skLineSegment(sketch, "E4507", {"start": v(-0.32, -1.21) * mm, "end": v(-0.32, -1.28) * mm});
            skLineSegment(sketch, "E4508", {"start": v(-0.32, -1.28) * mm, "end": v(-0.28, -1.32) * mm});
            skLineSegment(sketch, "E4509", {"start": v(-0.28, -1.32) * mm, "end": v(-0.21, -1.32) * mm});
            skLineSegment(sketch, "E4510", {"start": v(-0.21, -1.32) * mm, "end": v(-0.17, -1.28) * mm});
            skLineSegment(sketch, "E4511", {"start": v(-0.17, -1.28) * mm, "end": v(-0.17, -1.21) * mm});
            skLineSegment(sketch, "E4512", {"start": v(0.62, -1.21) * mm, "end": v(0.58, -1.17) * mm});
            skLineSegment(sketch, "E4513", {"start": v(0.58, -1.17) * mm, "end": v(0.51, -1.17) * mm});
            skLineSegment(sketch, "E4514", {"start": v(0.51, -1.17) * mm, "end": v(0.47, -1.21) * mm});
            skLineSegment(sketch, "E4515", {"start": v(0.47, -1.21) * mm, "end": v(0.47, -1.28) * mm});
            skLineSegment(sketch, "E4516", {"start": v(0.47, -1.28) * mm, "end": v(0.51, -1.32) * mm});
            skLineSegment(sketch, "E4517", {"start": v(0.51, -1.32) * mm, "end": v(0.58, -1.32) * mm});
            skLineSegment(sketch, "E4518", {"start": v(0.58, -1.32) * mm, "end": v(0.62, -1.28) * mm});
            skLineSegment(sketch, "E4519", {"start": v(0.62, -1.28) * mm, "end": v(0.62, -1.21) * mm});
            skArc(sketch, "E4520", {"start": v(-0.63, -1.25) * mm, "mid": v(-0.65, -1.23) * mm, "end": v(-0.67, -1.25) * mm});
            skArc(sketch, "E4521", {"start": v(-0.67, -1.25) * mm, "mid": v(-0.65, -1.27) * mm, "end": v(-0.63, -1.25) * mm});
            skArc(sketch, "E4522", {"start": v(-0.83, -1.25) * mm, "mid": v(-0.85, -1.23) * mm, "end": v(-0.87, -1.25) * mm});
            skArc(sketch, "E4523", {"start": v(-0.87, -1.25) * mm, "mid": v(-0.85, -1.27) * mm, "end": v(-0.83, -1.25) * mm});
            skArc(sketch, "E4524", {"start": v(-0.83, -0.85) * mm, "mid": v(-0.85, -0.83) * mm, "end": v(-0.87, -0.85) * mm});
            skArc(sketch, "E4525", {"start": v(-0.87, -0.85) * mm, "mid": v(-0.85, -0.87) * mm, "end": v(-0.83, -0.85) * mm});
            skArc(sketch, "E4526", {"start": v(-0.83, -0.75) * mm, "mid": v(-0.85, -0.73) * mm, "end": v(-0.87, -0.75) * mm});
            skArc(sketch, "E4527", {"start": v(-0.87, -0.75) * mm, "mid": v(-0.85, -0.77) * mm, "end": v(-0.83, -0.75) * mm});
            skArc(sketch, "E4528", {"start": v(-0.63, -0.75) * mm, "mid": v(-0.65, -0.73) * mm, "end": v(-0.67, -0.75) * mm});
            skArc(sketch, "E4529", {"start": v(-0.67, -0.75) * mm, "mid": v(-0.65, -0.77) * mm, "end": v(-0.63, -0.75) * mm});
            skArc(sketch, "E4530", {"start": v(-0.63, -0.85) * mm, "mid": v(-0.65, -0.83) * mm, "end": v(-0.67, -0.85) * mm});
            skArc(sketch, "E4531", {"start": v(-0.67, -0.85) * mm, "mid": v(-0.65, -0.87) * mm, "end": v(-0.63, -0.85) * mm});
            skArc(sketch, "E4532", {"start": v(-0.63, -0.35) * mm, "mid": v(-0.65, -0.33) * mm, "end": v(-0.67, -0.35) * mm});
            skArc(sketch, "E4533", {"start": v(-0.67, -0.35) * mm, "mid": v(-0.65, -0.37) * mm, "end": v(-0.63, -0.35) * mm});
            skArc(sketch, "E4534", {"start": v(-0.83, -0.35) * mm, "mid": v(-0.85, -0.33) * mm, "end": v(-0.87, -0.35) * mm});
            skArc(sketch, "E4535", {"start": v(-0.87, -0.35) * mm, "mid": v(-0.85, -0.37) * mm, "end": v(-0.83, -0.35) * mm});
            skArc(sketch, "E4536", {"start": v(-0.73, -0.15) * mm, "mid": v(-0.75, -0.13) * mm, "end": v(-0.77, -0.15) * mm});
            skArc(sketch, "E4537", {"start": v(-0.77, -0.15) * mm, "mid": v(-0.75, -0.17) * mm, "end": v(-0.73, -0.15) * mm});
            skArc(sketch, "E4538", {"start": v(-0.73, -0.05) * mm, "mid": v(-0.75, -0.03) * mm, "end": v(-0.77, -0.05) * mm});
            skArc(sketch, "E4539", {"start": v(-0.77, -0.05) * mm, "mid": v(-0.75, -0.07) * mm, "end": v(-0.73, -0.05) * mm});
            skArc(sketch, "E4540", {"start": v(-1.13, -0.05) * mm, "mid": v(-1.15, -0.03) * mm, "end": v(-1.17, -0.05) * mm});
            skArc(sketch, "E4541", {"start": v(-1.17, -0.05) * mm, "mid": v(-1.15, -0.07) * mm, "end": v(-1.13, -0.05) * mm});
            skArc(sketch, "E4542", {"start": v(-1.13, -0.15) * mm, "mid": v(-1.15, -0.13) * mm, "end": v(-1.17, -0.15) * mm});
            skArc(sketch, "E4543", {"start": v(-1.17, -0.15) * mm, "mid": v(-1.15, -0.17) * mm, "end": v(-1.13, -0.15) * mm});
            skArc(sketch, "E4544", {"start": v(-1.23, 0.65) * mm, "mid": v(-1.25, 0.67) * mm, "end": v(-1.27, 0.65) * mm});
            skArc(sketch, "E4545", {"start": v(-1.27, 0.65) * mm, "mid": v(-1.25, 0.63) * mm, "end": v(-1.23, 0.65) * mm});
            skArc(sketch, "E4546", {"start": v(-1.23, 1.05) * mm, "mid": v(-1.25, 1.07) * mm, "end": v(-1.27, 1.05) * mm});
            skArc(sketch, "E4547", {"start": v(-1.27, 1.05) * mm, "mid": v(-1.25, 1.03) * mm, "end": v(-1.23, 1.05) * mm});
            skArc(sketch, "E4548", {"start": v(0.88, 0.3) * mm, "mid": v(0.85, 0.33) * mm, "end": v(0.82, 0.3) * mm});
            skArc(sketch, "E4549", {"start": v(0.82, 0.3) * mm, "mid": v(0.85, 0.27) * mm, "end": v(0.88, 0.3) * mm});
            skLineSegment(sketch, "E4550", {"start": v(0.9, 0.52) * mm, "end": v(0.87, 0.55) * mm});
            skLineSegment(sketch, "E4551", {"start": v(0.87, 0.55) * mm, "end": v(0.83, 0.55) * mm});
            skLineSegment(sketch, "E4552", {"start": v(0.83, 0.55) * mm, "end": v(0.8, 0.52) * mm});
            skLineSegment(sketch, "E4553", {"start": v(0.8, 0.52) * mm, "end": v(0.8, 0.48) * mm});
            skLineSegment(sketch, "E4554", {"start": v(0.8, 0.48) * mm, "end": v(0.83, 0.45) * mm});
            skLineSegment(sketch, "E4555", {"start": v(0.83, 0.45) * mm, "end": v(0.87, 0.45) * mm});
            skLineSegment(sketch, "E4556", {"start": v(0.87, 0.45) * mm, "end": v(0.9, 0.48) * mm});
            skLineSegment(sketch, "E4557", {"start": v(0.9, 0.48) * mm, "end": v(0.9, 0.52) * mm});
            skLineSegment(sketch, "E4558", {"start": v(0.58, 0.26) * mm, "end": v(0.56, 0.28) * mm});
            skLineSegment(sketch, "E4559", {"start": v(0.56, 0.28) * mm, "end": v(0.54, 0.28) * mm});
            skLineSegment(sketch, "E4560", {"start": v(0.54, 0.28) * mm, "end": v(0.52, 0.26) * mm});
            skLineSegment(sketch, "E4561", {"start": v(0.52, 0.26) * mm, "end": v(0.52, 0.24) * mm});
            skLineSegment(sketch, "E4562", {"start": v(0.52, 0.24) * mm, "end": v(0.54, 0.22) * mm});
            skLineSegment(sketch, "E4563", {"start": v(0.54, 0.22) * mm, "end": v(0.56, 0.22) * mm});
            skLineSegment(sketch, "E4564", {"start": v(0.56, 0.22) * mm, "end": v(0.58, 0.24) * mm});
            skLineSegment(sketch, "E4565", {"start": v(0.58, 0.24) * mm, "end": v(0.58, 0.26) * mm});
            skArc(sketch, "E4566", {"start": v(0.47, 0.25) * mm, "mid": v(0.45, 0.27) * mm, "end": v(0.43, 0.25) * mm});
            skArc(sketch, "E4567", {"start": v(0.43, 0.25) * mm, "mid": v(0.45, 0.23) * mm, "end": v(0.47, 0.25) * mm});
            skLineSegment(sketch, "E4568", {"start": v(1.58, 0.21) * mm, "end": v(1.56, 0.23) * mm});
            skLineSegment(sketch, "E4569", {"start": v(1.56, 0.23) * mm, "end": v(1.54, 0.23) * mm});
            skLineSegment(sketch, "E4570", {"start": v(1.54, 0.23) * mm, "end": v(1.52, 0.21) * mm});
            skLineSegment(sketch, "E4571", {"start": v(1.52, 0.21) * mm, "end": v(1.52, 0.19) * mm});
            skLineSegment(sketch, "E4572", {"start": v(1.52, 0.19) * mm, "end": v(1.54, 0.17) * mm});
            skLineSegment(sketch, "E4573", {"start": v(1.54, 0.17) * mm, "end": v(1.56, 0.17) * mm});
            skLineSegment(sketch, "E4574", {"start": v(1.56, 0.17) * mm, "end": v(1.58, 0.19) * mm});
            skLineSegment(sketch, "E4575", {"start": v(1.58, 0.19) * mm, "end": v(1.58, 0.21) * mm});
            skLineSegment(sketch, "E4576", {"start": v(1.58, 0.11) * mm, "end": v(1.56, 0.13) * mm});
            skLineSegment(sketch, "E4577", {"start": v(1.56, 0.13) * mm, "end": v(1.54, 0.13) * mm});
            skLineSegment(sketch, "E4578", {"start": v(1.54, 0.13) * mm, "end": v(1.52, 0.11) * mm});
            skLineSegment(sketch, "E4579", {"start": v(1.52, 0.11) * mm, "end": v(1.52, 0.09) * mm});
            skLineSegment(sketch, "E4580", {"start": v(1.52, 0.09) * mm, "end": v(1.54, 0.07) * mm});
            skLineSegment(sketch, "E4581", {"start": v(1.54, 0.07) * mm, "end": v(1.56, 0.07) * mm});
            skLineSegment(sketch, "E4582", {"start": v(1.56, 0.07) * mm, "end": v(1.58, 0.09) * mm});
            skLineSegment(sketch, "E4583", {"start": v(1.58, 0.09) * mm, "end": v(1.58, 0.11) * mm});
            skLineSegment(sketch, "E4584", {"start": v(1.58, 0.01) * mm, "end": v(1.56, 0.03) * mm});
            skLineSegment(sketch, "E4585", {"start": v(1.56, 0.03) * mm, "end": v(1.54, 0.03) * mm});
            skLineSegment(sketch, "E4586", {"start": v(1.54, 0.03) * mm, "end": v(1.52, 0.01) * mm});
            skLineSegment(sketch, "E4587", {"start": v(1.52, 0.01) * mm, "end": v(1.52, -0.01) * mm});
            skLineSegment(sketch, "E4588", {"start": v(1.52, -0.01) * mm, "end": v(1.54, -0.03) * mm});
            skLineSegment(sketch, "E4589", {"start": v(1.54, -0.03) * mm, "end": v(1.56, -0.03) * mm});
            skLineSegment(sketch, "E4590", {"start": v(1.56, -0.03) * mm, "end": v(1.58, -0.01) * mm});
            skLineSegment(sketch, "E4591", {"start": v(1.58, -0.01) * mm, "end": v(1.58, 0.01) * mm});
            skLineSegment(sketch, "E4592", {"start": v(1.68, 0.01) * mm, "end": v(1.66, 0.03) * mm});
            skLineSegment(sketch, "E4593", {"start": v(1.66, 0.03) * mm, "end": v(1.64, 0.03) * mm});
            skLineSegment(sketch, "E4594", {"start": v(1.64, 0.03) * mm, "end": v(1.62, 0.01) * mm});
            skLineSegment(sketch, "E4595", {"start": v(1.62, 0.01) * mm, "end": v(1.62, -0.01) * mm});
            skLineSegment(sketch, "E4596", {"start": v(1.62, -0.01) * mm, "end": v(1.64, -0.03) * mm});
            skLineSegment(sketch, "E4597", {"start": v(1.64, -0.03) * mm, "end": v(1.66, -0.03) * mm});
            skLineSegment(sketch, "E4598", {"start": v(1.66, -0.03) * mm, "end": v(1.68, -0.01) * mm});
            skLineSegment(sketch, "E4599", {"start": v(1.68, -0.01) * mm, "end": v(1.68, 0.01) * mm});
            skLineSegment(sketch, "E4600", {"start": v(1.68, 0.11) * mm, "end": v(1.66, 0.13) * mm});
            skLineSegment(sketch, "E4601", {"start": v(1.66, 0.13) * mm, "end": v(1.64, 0.13) * mm});
            skLineSegment(sketch, "E4602", {"start": v(1.64, 0.13) * mm, "end": v(1.62, 0.11) * mm});
            skLineSegment(sketch, "E4603", {"start": v(1.62, 0.11) * mm, "end": v(1.62, 0.09) * mm});
            skLineSegment(sketch, "E4604", {"start": v(1.62, 0.09) * mm, "end": v(1.64, 0.07) * mm});
            skLineSegment(sketch, "E4605", {"start": v(1.64, 0.07) * mm, "end": v(1.66, 0.07) * mm});
            skLineSegment(sketch, "E4606", {"start": v(1.66, 0.07) * mm, "end": v(1.68, 0.09) * mm});
            skLineSegment(sketch, "E4607", {"start": v(1.68, 0.09) * mm, "end": v(1.68, 0.11) * mm});
            skLineSegment(sketch, "E4608", {"start": v(1.68, 0.21) * mm, "end": v(1.66, 0.23) * mm});
            skLineSegment(sketch, "E4609", {"start": v(1.66, 0.23) * mm, "end": v(1.64, 0.23) * mm});
            skLineSegment(sketch, "E4610", {"start": v(1.64, 0.23) * mm, "end": v(1.62, 0.21) * mm});
            skLineSegment(sketch, "E4611", {"start": v(1.62, 0.21) * mm, "end": v(1.62, 0.19) * mm});
            skLineSegment(sketch, "E4612", {"start": v(1.62, 0.19) * mm, "end": v(1.64, 0.17) * mm});
            skLineSegment(sketch, "E4613", {"start": v(1.64, 0.17) * mm, "end": v(1.66, 0.17) * mm});
            skLineSegment(sketch, "E4614", {"start": v(1.66, 0.17) * mm, "end": v(1.68, 0.19) * mm});
            skLineSegment(sketch, "E4615", {"start": v(1.68, 0.19) * mm, "end": v(1.68, 0.21) * mm});
            skLineSegment(sketch, "E4616", {"start": v(1.68, -0.09) * mm, "end": v(1.66, -0.07) * mm});
            skLineSegment(sketch, "E4617", {"start": v(1.66, -0.07) * mm, "end": v(1.64, -0.07) * mm});
            skLineSegment(sketch, "E4618", {"start": v(1.64, -0.07) * mm, "end": v(1.62, -0.09) * mm});
            skLineSegment(sketch, "E4619", {"start": v(1.62, -0.09) * mm, "end": v(1.62, -0.11) * mm});
            skLineSegment(sketch, "E4620", {"start": v(1.62, -0.11) * mm, "end": v(1.64, -0.13) * mm});
            skLineSegment(sketch, "E4621", {"start": v(1.64, -0.13) * mm, "end": v(1.66, -0.13) * mm});
            skLineSegment(sketch, "E4622", {"start": v(1.66, -0.13) * mm, "end": v(1.68, -0.11) * mm});
            skLineSegment(sketch, "E4623", {"start": v(1.68, -0.11) * mm, "end": v(1.68, -0.09) * mm});
            skLineSegment(sketch, "E4624", {"start": v(1.68, -0.19) * mm, "end": v(1.66, -0.17) * mm});
            skLineSegment(sketch, "E4625", {"start": v(1.66, -0.17) * mm, "end": v(1.64, -0.17) * mm});
            skLineSegment(sketch, "E4626", {"start": v(1.64, -0.17) * mm, "end": v(1.62, -0.19) * mm});
            skLineSegment(sketch, "E4627", {"start": v(1.62, -0.19) * mm, "end": v(1.62, -0.21) * mm});
            skLineSegment(sketch, "E4628", {"start": v(1.62, -0.21) * mm, "end": v(1.64, -0.23) * mm});
            skLineSegment(sketch, "E4629", {"start": v(1.64, -0.23) * mm, "end": v(1.66, -0.23) * mm});
            skLineSegment(sketch, "E4630", {"start": v(1.66, -0.23) * mm, "end": v(1.68, -0.21) * mm});
            skLineSegment(sketch, "E4631", {"start": v(1.68, -0.21) * mm, "end": v(1.68, -0.19) * mm});
            skLineSegment(sketch, "E4632", {"start": v(1.58, -0.19) * mm, "end": v(1.56, -0.17) * mm});
            skLineSegment(sketch, "E4633", {"start": v(1.56, -0.17) * mm, "end": v(1.54, -0.17) * mm});
            skLineSegment(sketch, "E4634", {"start": v(1.54, -0.17) * mm, "end": v(1.52, -0.19) * mm});
            skLineSegment(sketch, "E4635", {"start": v(1.52, -0.19) * mm, "end": v(1.52, -0.21) * mm});
            skLineSegment(sketch, "E4636", {"start": v(1.52, -0.21) * mm, "end": v(1.54, -0.23) * mm});
            skLineSegment(sketch, "E4637", {"start": v(1.54, -0.23) * mm, "end": v(1.56, -0.23) * mm});
            skLineSegment(sketch, "E4638", {"start": v(1.56, -0.23) * mm, "end": v(1.58, -0.21) * mm});
            skLineSegment(sketch, "E4639", {"start": v(1.58, -0.21) * mm, "end": v(1.58, -0.19) * mm});
            skLineSegment(sketch, "E4640", {"start": v(1.58, -0.09) * mm, "end": v(1.56, -0.07) * mm});
            skLineSegment(sketch, "E4641", {"start": v(1.56, -0.07) * mm, "end": v(1.54, -0.07) * mm});
            skLineSegment(sketch, "E4642", {"start": v(1.54, -0.07) * mm, "end": v(1.52, -0.09) * mm});
            skLineSegment(sketch, "E4643", {"start": v(1.52, -0.09) * mm, "end": v(1.52, -0.11) * mm});
            skLineSegment(sketch, "E4644", {"start": v(1.52, -0.11) * mm, "end": v(1.54, -0.13) * mm});
            skLineSegment(sketch, "E4645", {"start": v(1.54, -0.13) * mm, "end": v(1.56, -0.13) * mm});
            skLineSegment(sketch, "E4646", {"start": v(1.56, -0.13) * mm, "end": v(1.58, -0.11) * mm});
            skLineSegment(sketch, "E4647", {"start": v(1.58, -0.11) * mm, "end": v(1.58, -0.09) * mm});
            skLineSegment(sketch, "E4648", {"start": v(0.48, -0.15) * mm, "end": v(0.42, -0.15) * mm});
            skLineSegment(sketch, "E4649", {"start": v(0.42, -0.05) * mm, "end": v(0.48, -0.05) * mm});
            skLineSegment(sketch, "E4650", {"start": v(0.48, 0.05) * mm, "end": v(0.42, 0.05) * mm});
            skLineSegment(sketch, "E4651", {"start": v(0.18, 0.05) * mm, "end": v(0.12, 0.05) * mm});
            skLineSegment(sketch, "E4652", {"start": v(0.12, -0.05) * mm, "end": v(0.18, -0.05) * mm});
            skLineSegment(sketch, "E4653", {"start": v(0.18, -0.15) * mm, "end": v(0.12, -0.15) * mm});
            skLineSegment(sketch, "E4654", {"start": v(-0.12, -0.15) * mm, "end": v(-0.18, -0.15) * mm});
            skLineSegment(sketch, "E4655", {"start": v(-0.18, -0.05) * mm, "end": v(-0.12, -0.05) * mm});
            skLineSegment(sketch, "E4656", {"start": v(-0.12, 0.05) * mm, "end": v(-0.18, 0.05) * mm});
            skLineSegment(sketch, "E4657", {"start": v(-0.42, 0.05) * mm, "end": v(-0.48, 0.05) * mm});
            skLineSegment(sketch, "E4658", {"start": v(-0.55, 0.1) * mm, "end": v(-0.55, 0.15) * mm});
            skLineSegment(sketch, "E4659", {"start": v(-0.65, 0.15) * mm, "end": v(-0.65, 0.1) * mm});
            skLineSegment(sketch, "E4660", {"start": v(-0.75, 0.1) * mm, "end": v(-0.75, 0.15) * mm});
            skLineSegment(sketch, "E4661", {"start": v(-0.85, 0.15) * mm, "end": v(-0.85, 0.1) * mm});
            skLineSegment(sketch, "E4662", {"start": v(-1.05, 0.08) * mm, "end": v(-1.05, 0.02) * mm});
            skLineSegment(sketch, "E4663", {"start": v(-1.15, 0.02) * mm, "end": v(-1.15, 0.08) * mm});
            skLineSegment(sketch, "E4664", {"start": v(-1.15, 0.42) * mm, "end": v(-1.15, 0.48) * mm});
            skLineSegment(sketch, "E4665", {"start": v(-1.05, 0.48) * mm, "end": v(-1.05, 0.42) * mm});
            skLineSegment(sketch, "E4666", {"start": v(-0.85, 0.45) * mm, "end": v(-0.85, 0.5) * mm});
            skLineSegment(sketch, "E4667", {"start": v(-0.75, 0.5) * mm, "end": v(-0.75, 0.45) * mm});
            skLineSegment(sketch, "E4668", {"start": v(-0.65, 0.45) * mm, "end": v(-0.65, 0.5) * mm});
            skLineSegment(sketch, "E4669", {"start": v(-0.55, 0.5) * mm, "end": v(-0.55, 0.45) * mm});
            skLineSegment(sketch, "E4670", {"start": v(-0.35, 0.72) * mm, "end": v(-0.35, 0.78) * mm});
            skLineSegment(sketch, "E4671", {"start": v(-0.25, 0.78) * mm, "end": v(-0.25, 0.72) * mm});
            skLineSegment(sketch, "E4672", {"start": v(-0.15, 0.72) * mm, "end": v(-0.15, 0.78) * mm});
            skLineSegment(sketch, "E4673", {"start": v(-0.05, 0.78) * mm, "end": v(-0.05, 0.72) * mm});
            skLineSegment(sketch, "E4674", {"start": v(0.05, 0.72) * mm, "end": v(0.05, 0.78) * mm});
            skLineSegment(sketch, "E4675", {"start": v(0.15, 0.78) * mm, "end": v(0.15, 0.72) * mm});
            skLineSegment(sketch, "E4676", {"start": v(0.25, 0.72) * mm, "end": v(0.25, 0.78) * mm});
            skLineSegment(sketch, "E4677", {"start": v(0.35, 0.78) * mm, "end": v(0.35, 0.72) * mm});
            skLineSegment(sketch, "E4678", {"start": v(0.45, 0.72) * mm, "end": v(0.45, 0.78) * mm});
            skLineSegment(sketch, "E4679", {"start": v(0.65, 0.78) * mm, "end": v(0.65, 0.72) * mm});
            skLineSegment(sketch, "E4680", {"start": v(0.75, 0.72) * mm, "end": v(0.75, 0.78) * mm});
            skLineSegment(sketch, "E4681", {"start": v(0.85, 0.78) * mm, "end": v(0.85, 0.72) * mm});
            skLineSegment(sketch, "E4682", {"start": v(0.95, 0.72) * mm, "end": v(0.95, 0.78) * mm});
            skLineSegment(sketch, "E4683", {"start": v(1.05, 0.78) * mm, "end": v(1.05, 0.72) * mm});
            skLineSegment(sketch, "E4684", {"start": v(1.15, 0.72) * mm, "end": v(1.15, 0.78) * mm});
            skLineSegment(sketch, "E4685", {"start": v(1.25, 0.78) * mm, "end": v(1.25, 0.72) * mm});
            skLineSegment(sketch, "E4686", {"start": v(1.35, 0.72) * mm, "end": v(1.35, 0.78) * mm});
            skLineSegment(sketch, "E4687", {"start": v(1.35, 1.02) * mm, "end": v(1.35, 1.08) * mm});
            skLineSegment(sketch, "E4688", {"start": v(1.25, 1.08) * mm, "end": v(1.25, 1.02) * mm});
            skLineSegment(sketch, "E4689", {"start": v(1.15, 1.02) * mm, "end": v(1.15, 1.08) * mm});
            skLineSegment(sketch, "E4690", {"start": v(1.05, 1.08) * mm, "end": v(1.05, 1.02) * mm});
            skLineSegment(sketch, "E4691", {"start": v(0.95, 1.02) * mm, "end": v(0.95, 1.08) * mm});
            skLineSegment(sketch, "E4692", {"start": v(0.85, 1.08) * mm, "end": v(0.85, 1.02) * mm});
            skLineSegment(sketch, "E4693", {"start": v(0.75, 1.02) * mm, "end": v(0.75, 1.08) * mm});
            skLineSegment(sketch, "E4694", {"start": v(0.65, 1.08) * mm, "end": v(0.65, 1.02) * mm});
            skLineSegment(sketch, "E4695", {"start": v(0.45, 1.02) * mm, "end": v(0.45, 1.08) * mm});
            skLineSegment(sketch, "E4696", {"start": v(0.35, 1.08) * mm, "end": v(0.35, 1.02) * mm});
            skLineSegment(sketch, "E4697", {"start": v(0.25, 1.02) * mm, "end": v(0.25, 1.08) * mm});
            skLineSegment(sketch, "E4698", {"start": v(0.15, 1.08) * mm, "end": v(0.15, 1.02) * mm});
            skLineSegment(sketch, "E4699", {"start": v(0.05, 1.02) * mm, "end": v(0.05, 1.08) * mm});
            skLineSegment(sketch, "E4700", {"start": v(-0.05, 1.08) * mm, "end": v(-0.05, 1.02) * mm});
            skLineSegment(sketch, "E4701", {"start": v(-0.15, 1.02) * mm, "end": v(-0.15, 1.08) * mm});
            skLineSegment(sketch, "E4702", {"start": v(-0.25, 1.08) * mm, "end": v(-0.25, 1.02) * mm});
            skLineSegment(sketch, "E4703", {"start": v(-0.35, 1.02) * mm, "end": v(-0.35, 1.08) * mm});
            skLineSegment(sketch, "E4704", {"start": v(-0.85, 1.17) * mm, "end": v(-0.85, 1.23) * mm});
            skLineSegment(sketch, "E4705", {"start": v(-0.95, 1.23) * mm, "end": v(-0.95, 1.17) * mm});
            skLineSegment(sketch, "E4706", {"start": v(-1.05, 1.17) * mm, "end": v(-1.05, 1.23) * mm});
            skLineSegment(sketch, "E4707", {"start": v(-1.05, 1.08) * mm, "end": v(-1.05, 1.02) * mm});
            skLineSegment(sketch, "E4708", {"start": v(-1.15, 1.02) * mm, "end": v(-1.15, 1.08) * mm});
            skLineSegment(sketch, "E4709", {"start": v(-1.15, 0.68) * mm, "end": v(-1.15, 0.62) * mm});
            skLineSegment(sketch, "E4710", {"start": v(-1.05, 0.62) * mm, "end": v(-1.05, 0.68) * mm});
            skLineSegment(sketch, "E4711", {"start": v(-0.48, -0.05) * mm, "end": v(-0.42, -0.05) * mm});
            skLineSegment(sketch, "E4712", {"start": v(-0.42, -0.15) * mm, "end": v(-0.48, -0.15) * mm});
            skLineSegment(sketch, "E4713", {"start": v(1.24, -0.65) * mm, "end": v(1.16, -0.65) * mm});
            skLineSegment(sketch, "E4714", {"start": v(1.16, -0.85) * mm, "end": v(1.24, -0.85) * mm});
            skLineSegment(sketch, "E4715", {"start": v(-1.51, -0.45) * mm, "end": v(-1.59, -0.45) * mm});
            skLineSegment(sketch, "E4716", {"start": v(-1.59, -0.25) * mm, "end": v(-1.51, -0.25) * mm});
            skLineSegment(sketch, "E4717", {"start": v(-1.51, 0.25) * mm, "end": v(-1.59, 0.25) * mm});
            skLineSegment(sketch, "E4718", {"start": v(-1.59, 0.45) * mm, "end": v(-1.51, 0.45) * mm});
            skArc(sketch, "E4719", {"start": v(0.87, 0.3) * mm, "mid": v(0.85, 0.32) * mm, "end": v(0.82, 0.3) * mm});
            skArc(sketch, "E4720", {"start": v(0.82, 0.3) * mm, "mid": v(0.85, 0.27) * mm, "end": v(0.87, 0.3) * mm});
            skLineSegment(sketch, "E4721", {"start": v(0.88, 0.05) * mm, "end": v(0.82, 0.05) * mm});
            skLineSegment(sketch, "E4722", {"start": v(0.82, -0.05) * mm, "end": v(0.88, -0.05) * mm});
            skLineSegment(sketch, "E4723", {"start": v(0.88, -0.15) * mm, "end": v(0.82, -0.15) * mm});
            skLineSegment(sketch, "E4724", {"start": v(0.35, 1.22) * mm, "end": v(0.35, 1.28) * mm});
            skLineSegment(sketch, "E4725", {"start": v(0.25, 1.28) * mm, "end": v(0.25, 1.22) * mm});
            skLineSegment(sketch, "E4726", {"start": v(0.15, 1.22) * mm, "end": v(0.15, 1.28) * mm});
            skLineSegment(sketch, "E4727", {"start": v(0.05, 1.28) * mm, "end": v(0.05, 1.22) * mm});
            skLineSegment(sketch, "E4728", {"start": v(-0.05, 1.22) * mm, "end": v(-0.05, 1.28) * mm});
            skLineSegment(sketch, "E4729", {"start": v(-0.15, 1.28) * mm, "end": v(-0.15, 1.22) * mm});
            skLineSegment(sketch, "E4730", {"start": v(-0.25, 1.22) * mm, "end": v(-0.25, 1.28) * mm});
            skLineSegment(sketch, "E4731", {"start": v(-0.35, 1.28) * mm, "end": v(-0.35, 1.22) * mm});
            skLineSegment(sketch, "E4732", {"start": v(-0.45, 1.22) * mm, "end": v(-0.45, 1.28) * mm});
            skLineSegment(sketch, "E4733", {"start": v(-0.55, 1.28) * mm, "end": v(-0.55, 1.22) * mm});
            skLineSegment(sketch, "E4734", {"start": v(-0.55, 1.2) * mm, "end": v(-0.5, 1.15) * mm});
            skLineSegment(sketch, "E4735", {"start": v(-0.5, 1.15) * mm, "end": v(-0.5, 0.7) * mm});
            skLineSegment(sketch, "E4736", {"start": v(-0.5, 0.7) * mm, "end": v(-0.45, 0.65) * mm});
            skLineSegment(sketch, "E4737", {"start": v(-0.5, 0.7) * mm, "end": v(-0.6, 0.7) * mm});
            skLineSegment(sketch, "E4738", {"start": v(-0.6, 0.7) * mm, "end": v(-0.65, 0.65) * mm});
            skLineSegment(sketch, "E4739", {"start": v(0.05, 1) * mm, "end": v(0.05, 1.05) * mm});
            skLineSegment(sketch, "E4740", {"start": v(0.05, 1) * mm, "end": v(0.1, 0.95) * mm});
            skLineSegment(sketch, "E4741", {"start": v(0.1, 0.95) * mm, "end": v(0.2, 0.95) * mm});
            skLineSegment(sketch, "E4742", {"start": v(0.2, 0.95) * mm, "end": v(0.3, 0.85) * mm});
            skLineSegment(sketch, "E4743", {"start": v(0.3, 0.85) * mm, "end": v(0.3, 0.65) * mm});
            skLineSegment(sketch, "E4744", {"start": v(0.3, 0.65) * mm, "end": v(0.45, 0.5) * mm});
            skLineSegment(sketch, "E4745", {"start": v(0.45, 0.5) * mm, "end": v(0.45, 0.25) * mm});
            skLineSegment(sketch, "E4746", {"start": v(0.45, 0.25) * mm, "end": v(0.45, 0.2) * mm});
            skLineSegment(sketch, "E4747", {"start": v(0.45, 0.2) * mm, "end": v(0.6, 0.05) * mm});
            skLineSegment(sketch, "E4748", {"start": v(0.6, 0.05) * mm, "end": v(0.85, 0.05) * mm});
            skLineSegment(sketch, "E4749", {"start": v(0.95, -0.1) * mm, "end": v(0.9, -0.15) * mm});
            skLineSegment(sketch, "E4750", {"start": v(0.9, -0.15) * mm, "end": v(0.85, -0.15) * mm});
            skLineSegment(sketch, "E4751", {"start": v(0.85, -0.15) * mm, "end": v(0.45, -0.15) * mm});
            skLineSegment(sketch, "E4752", {"start": v(0.45, -0.15) * mm, "end": v(0.35, -0.15) * mm});
            skLineSegment(sketch, "E4753", {"start": v(0.35, -0.15) * mm, "end": v(0.35, -0.05) * mm});
            skLineSegment(sketch, "E4754", {"start": v(0.35, -0.05) * mm, "end": v(0.15, 0.15) * mm});
            skLineSegment(sketch, "E4755", {"start": v(0.35, -0.15) * mm, "end": v(0.25, -0.25) * mm});
            skLineSegment(sketch, "E4756", {"start": v(0.25, -0.25) * mm, "end": v(-0.15, -0.25) * mm});
            skLineSegment(sketch, "E4757", {"start": v(-0.15, -0.25) * mm, "end": v(-0.15, -0.15) * mm});
            skLineSegment(sketch, "E4758", {"start": v(-0.15, -0.25) * mm, "end": v(-0.55, -0.25) * mm});
            skLineSegment(sketch, "E4759", {"start": v(-0.55, -0.25) * mm, "end": v(-0.65, -0.35) * mm});
            skLineSegment(sketch, "E4760", {"start": v(0.75, 0.75) * mm, "end": v(0.75, 0.8) * mm});
            skLineSegment(sketch, "E4761", {"start": v(0.75, 0.8) * mm, "end": v(0.8, 0.85) * mm});
            skLineSegment(sketch, "E4762", {"start": v(0.8, 0.85) * mm, "end": v(0.8, 1.15) * mm});
            skLineSegment(sketch, "E4763", {"start": v(0.8, 1.15) * mm, "end": v(0.75, 1.2) * mm});
            skLineSegment(sketch, "E4764", {"start": v(0.75, 1.2) * mm, "end": v(0.74, 1.2) * mm});
            skLineSegment(sketch, "E4765", {"start": v(0.85, 0.3) * mm, "end": v(0.95, 0.2) * mm});
            skLineSegment(sketch, "E4766", {"start": v(0.95, 0.2) * mm, "end": v(0.95, -0.1) * mm});
            skLineSegment(sketch, "E4767", {"start": v(-0.55, 1.2) * mm, "end": v(-0.55, 1.25) * mm});
            skLineSegment(sketch, "E4768", {"start": v(-0.45, 1.25) * mm, "end": v(-0.45, 1.2) * mm});
            skLineSegment(sketch, "E4769", {"start": v(-0.45, 1.2) * mm, "end": v(-0.4, 1.15) * mm});
            skLineSegment(sketch, "E4770", {"start": v(-0.4, 1.15) * mm, "end": v(-0.25, 1.15) * mm});
            skLineSegment(sketch, "E4771", {"start": v(-0.25, 1.15) * mm, "end": v(-0.2, 1.1) * mm});
            skLineSegment(sketch, "E4772", {"start": v(-0.2, 1.1) * mm, "end": v(-0.2, 0.95) * mm});
            skLineSegment(sketch, "E4773", {"start": v(-0.2, 0.95) * mm, "end": v(-0.05, 0.8) * mm});
            skLineSegment(sketch, "E4774", {"start": v(-0.05, 0.8) * mm, "end": v(-0.05, 0.75) * mm});
            skLineSegment(sketch, "E4775", {"start": v(-0.05, 0.75) * mm, "end": v(-0.05, 0.65) * mm});
            skLineSegment(sketch, "E4776", {"start": v(-0.05, 0.65) * mm, "end": v(0.2, 0.65) * mm});
            skLineSegment(sketch, "E4777", {"start": v(0.2, 0.65) * mm, "end": v(0.25, 0.7) * mm});
            skLineSegment(sketch, "E4778", {"start": v(0.25, 0.7) * mm, "end": v(0.25, 0.75) * mm});
            skLineSegment(sketch, "E4779", {"start": v(0.35, 0.75) * mm, "end": v(0.35, 0.7) * mm});
            skLineSegment(sketch, "E4780", {"start": v(0.35, 0.7) * mm, "end": v(0.4, 0.65) * mm});
            skLineSegment(sketch, "E4781", {"start": v(0.4, 0.65) * mm, "end": v(0.9, 0.65) * mm});
            skLineSegment(sketch, "E4782", {"start": v(0.9, 0.65) * mm, "end": v(0.95, 0.7) * mm});
            skLineSegment(sketch, "E4783", {"start": v(0.95, 0.7) * mm, "end": v(0.95, 0.75) * mm});
            skLineSegment(sketch, "E4784", {"start": v(1.05, 0.75) * mm, "end": v(1.05, 0.3) * mm});
            skLineSegment(sketch, "E4785", {"start": v(1.05, 0.3) * mm, "end": v(1.35, 0) * mm});
            skLineSegment(sketch, "E4786", {"start": v(1.35, 0) * mm, "end": v(1.55, 0) * mm});
            skLineSegment(sketch, "E4787", {"start": v(1.55, 0.1) * mm, "end": v(1.4, 0.1) * mm});
            skLineSegment(sketch, "E4788", {"start": v(1.4, 0.1) * mm, "end": v(1.15, 0.35) * mm});
            skLineSegment(sketch, "E4789", {"start": v(1.15, 0.35) * mm, "end": v(1.15, 0.75) * mm});
            skLineSegment(sketch, "E4790", {"start": v(1.15, 1.05) * mm, "end": v(1.15, 1.1) * mm});
            skLineSegment(sketch, "E4791", {"start": v(1.15, 1.1) * mm, "end": v(1.25, 1.2) * mm});
            skLineSegment(sketch, "E4792", {"start": v(1.25, 1.2) * mm, "end": v(1.26, 1.2) * mm});
            skLineSegment(sketch, "E4793", {"start": v(0.45, 0.8) * mm, "end": v(0.45, 0.75) * mm});
            skLineSegment(sketch, "E4794", {"start": v(0.45, 0.8) * mm, "end": v(0.4, 0.85) * mm});
            skLineSegment(sketch, "E4795", {"start": v(0.4, 0.85) * mm, "end": v(0.4, 1.1) * mm});
            skLineSegment(sketch, "E4796", {"start": v(0.4, 1.1) * mm, "end": v(0.35, 1.15) * mm});
            skLineSegment(sketch, "E4797", {"start": v(0.35, 1.15) * mm, "end": v(0.35, 1.25) * mm});
            skLineSegment(sketch, "E4798", {"start": v(-0.25, 1.05) * mm, "end": v(-0.25, 1) * mm});
            skLineSegment(sketch, "E4799", {"start": v(-0.25, 1) * mm, "end": v(-0.3, 0.95) * mm});
            skLineSegment(sketch, "E4800", {"start": v(-0.3, 0.95) * mm, "end": v(-0.4, 0.95) * mm});
            skLineSegment(sketch, "E4801", {"start": v(-0.4, 0.95) * mm, "end": v(-0.45, 1) * mm});
            skLineSegment(sketch, "E4802", {"start": v(-0.45, 1) * mm, "end": v(-0.45, 1.05) * mm});
            skLineSegment(sketch, "E4803", {"start": v(-0.65, 1.05) * mm, "end": v(-0.65, 0.95) * mm});
            skLineSegment(sketch, "E4804", {"start": v(-0.65, 0.85) * mm, "end": v(-0.65, 1.05) * mm});
            skLineSegment(sketch, "E4805", {"start": v(-0.75, 1.05) * mm, "end": v(-0.75, 1) * mm});
            skLineSegment(sketch, "E4806", {"start": v(-0.75, 1) * mm, "end": v(-0.8, 0.95) * mm});
            skLineSegment(sketch, "E4807", {"start": v(-0.8, 0.95) * mm, "end": v(-1.2, 0.95) * mm});
            skLineSegment(sketch, "E4808", {"start": v(-1.2, 0.95) * mm, "end": v(-1.25, 1) * mm});
            skLineSegment(sketch, "E4809", {"start": v(-1.25, 0.65) * mm, "end": v(-1.25, 0.6) * mm});
            skLineSegment(sketch, "E4810", {"start": v(-1.25, 0.6) * mm, "end": v(-1.2, 0.55) * mm});
            skLineSegment(sketch, "E4811", {"start": v(-1.2, 0.55) * mm, "end": v(-0.85, 0.55) * mm});
            skLineSegment(sketch, "E4812", {"start": v(-0.85, 0.55) * mm, "end": v(-0.85, 0.45) * mm});
            skLineSegment(sketch, "E4813", {"start": v(-0.85, 0.45) * mm, "end": v(-0.85, 0.4) * mm});
            skLineSegment(sketch, "E4814", {"start": v(-0.85, 0.4) * mm, "end": v(-1.05, 0.2) * mm});
            skLineSegment(sketch, "E4815", {"start": v(-1.05, 0.2) * mm, "end": v(-1.05, 0.05) * mm});
            skLineSegment(sketch, "E4816", {"start": v(-0.85, 0.15) * mm, "end": v(-0.85, 0.2) * mm});
            skLineSegment(sketch, "E4817", {"start": v(-0.85, 0.2) * mm, "end": v(-0.7, 0.35) * mm});
            skLineSegment(sketch, "E4818", {"start": v(-0.7, 0.35) * mm, "end": v(-0.7, 0.8) * mm});
            skLineSegment(sketch, "E4819", {"start": v(-0.7, 0.8) * mm, "end": v(-0.65, 0.85) * mm});
            skLineSegment(sketch, "E4820", {"start": v(-0.55, 0.65) * mm, "end": v(-0.6, 0.6) * mm});
            skLineSegment(sketch, "E4821", {"start": v(-0.6, 0.6) * mm, "end": v(-0.6, 0.35) * mm});
            skLineSegment(sketch, "E4822", {"start": v(-0.6, 0.35) * mm, "end": v(-0.45, 0.2) * mm});
            skLineSegment(sketch, "E4823", {"start": v(-0.45, 0.2) * mm, "end": v(-0.45, 0.05) * mm});
            skLineSegment(sketch, "E4824", {"start": v(-0.45, 0.05) * mm, "end": v(-0.5, 0.05) * mm});
            skLineSegment(sketch, "E4825", {"start": v(-0.5, 0.05) * mm, "end": v(-0.6, -0.05) * mm});
            skLineSegment(sketch, "E4826", {"start": v(-0.6, -0.05) * mm, "end": v(-0.6, -0.15) * mm});
            skLineSegment(sketch, "E4827", {"start": v(-0.6, -0.15) * mm, "end": v(-0.7, -0.25) * mm});
            skLineSegment(sketch, "E4828", {"start": v(-0.7, -0.25) * mm, "end": v(-1.55, -0.25) * mm});
            skLineSegment(sketch, "E4829", {"start": v(-0.55, 0.4) * mm, "end": v(-0.5, 0.35) * mm});
            skLineSegment(sketch, "E4830", {"start": v(-0.5, 0.35) * mm, "end": v(-0.4, 0.35) * mm});
            skLineSegment(sketch, "E4831", {"start": v(-0.4, 0.35) * mm, "end": v(-0.25, 0.2) * mm});
            skLineSegment(sketch, "E4832", {"start": v(-0.25, 0.2) * mm, "end": v(-0.25, 0.15) * mm});
            skLineSegment(sketch, "E4833", {"start": v(-0.15, -0.05) * mm, "end": v(-0.1, -0.05) * mm});
            skLineSegment(sketch, "E4834", {"start": v(-0.1, -0.05) * mm, "end": v(0.05, 0.1) * mm});
            skLineSegment(sketch, "E4835", {"start": v(0.05, 0.1) * mm, "end": v(0.05, 0.3) * mm});
            skLineSegment(sketch, "E4836", {"start": v(0.05, 0.3) * mm, "end": v(0.15, 0.4) * mm});
            skLineSegment(sketch, "E4837", {"start": v(0.15, 0.4) * mm, "end": v(0.15, 0.55) * mm});
            skLineSegment(sketch, "E4838", {"start": v(-0.05, 0.55) * mm, "end": v(-0.05, 0.65) * mm});
            skLineSegment(sketch, "E4839", {"start": v(-0.15, 0.55) * mm, "end": v(-0.15, 0.75) * mm});
            skLineSegment(sketch, "E4840", {"start": v(-0.25, 0.75) * mm, "end": v(-0.25, 0.55) * mm});
            skLineSegment(sketch, "E4841", {"start": v(-0.55, 0.45) * mm, "end": v(-0.55, 0.4) * mm});
            skLineSegment(sketch, "E4842", {"start": v(-0.85, 0.55) * mm, "end": v(-0.85, 0.65) * mm});
            skLineSegment(sketch, "E4843", {"start": v(-0.5, 1.15) * mm, "end": v(-0.4, 1.15) * mm});
            skLineSegment(sketch, "E4844", {"start": v(-0.4, 1.15) * mm, "end": v(-0.35, 1.2) * mm});
            skLineSegment(sketch, "E4845", {"start": v(-0.05, 1.2) * mm, "end": v(-0.05, 1.25) * mm});
            skLineSegment(sketch, "E4846", {"start": v(-0.05, 1.2) * mm, "end": v(0.05, 1.1) * mm});
            skLineSegment(sketch, "E4847", {"start": v(0.05, 1.1) * mm, "end": v(0.05, 1.05) * mm});
            skLineSegment(sketch, "E4848", {"start": v(0.05, 0.75) * mm, "end": v(0.05, 0.65) * mm});
            skLineSegment(sketch, "E4849", {"start": v(0.05, 0.65) * mm, "end": v(-0.35, 0.65) * mm});
            skLineSegment(sketch, "E4850", {"start": v(-0.35, 0.65) * mm, "end": v(-0.35, 0.55) * mm});
            skLineSegment(sketch, "E4851", {"start": v(-0.35, 0.65) * mm, "end": v(-0.45, 0.65) * mm});
            skLineSegment(sketch, "E4852", {"start": v(-0.65, 0.65) * mm, "end": v(-0.65, 0.45) * mm});
            skLineSegment(sketch, "E4853", {"start": v(-0.7, 0.25) * mm, "end": v(-0.05, 0.25) * mm});
            skLineSegment(sketch, "E4854", {"start": v(-0.05, 0.25) * mm, "end": v(0.05, 0.25) * mm});
            skLineSegment(sketch, "E4855", {"start": v(0.05, 0.25) * mm, "end": v(0.45, 0.25) * mm});
            skLineSegment(sketch, "E4856", {"start": v(0.55, 0.25) * mm, "end": v(0.7, 0.25) * mm});
            skLineSegment(sketch, "E4857", {"start": v(0.7, 0.25) * mm, "end": v(0.7, 0.35) * mm});
            skLineSegment(sketch, "E4858", {"start": v(0.7, 0.35) * mm, "end": v(0.85, 0.5) * mm});
            skLineSegment(sketch, "E4859", {"start": v(0.85, 0.5) * mm, "end": v(0.85, 0.65) * mm});
            skLineSegment(sketch, "E4860", {"start": v(0.85, 0.65) * mm, "end": v(0.75, 0.65) * mm});
            skLineSegment(sketch, "E4861", {"start": v(0.75, 0.65) * mm, "end": v(0.05, 0.65) * mm});
            skLineSegment(sketch, "E4862", {"start": v(0.05, 0.25) * mm, "end": v(0.05, 0) * mm});
            skLineSegment(sketch, "E4863", {"start": v(0.05, 0) * mm, "end": v(0.1, -0.05) * mm});
            skLineSegment(sketch, "E4864", {"start": v(0.1, -0.05) * mm, "end": v(0.15, -0.05) * mm});
            skLineSegment(sketch, "E4865", {"start": v(-0.05, 0.15) * mm, "end": v(-0.05, 0.25) * mm});
            skLineSegment(sketch, "E4866", {"start": v(-0.7, 0.25) * mm, "end": v(-0.75, 0.2) * mm});
            skLineSegment(sketch, "E4867", {"start": v(-0.75, 0.2) * mm, "end": v(-0.75, 0.15) * mm});
            skLineSegment(sketch, "E4868", {"start": v(-0.95, -0.25) * mm, "end": v(-1.05, -0.35) * mm});
            skLineSegment(sketch, "E4869", {"start": v(-1.05, -0.35) * mm, "end": v(-1.05, -0.45) * mm});
            skLineSegment(sketch, "E4870", {"start": v(-1.05, -0.45) * mm, "end": v(-1.55, -0.45) * mm});
            skLineSegment(sketch, "E4871", {"start": v(-1.05, -0.45) * mm, "end": v(-1.05, -1.15) * mm});
            skLineSegment(sketch, "E4872", {"start": v(-1.05, -1.15) * mm, "end": v(-0.95, -1.25) * mm});
            skLineSegment(sketch, "E4873", {"start": v(-0.95, -1.25) * mm, "end": v(-0.85, -1.25) * mm});
            skLineSegment(sketch, "E4874", {"start": v(-0.85, -1.25) * mm, "end": v(-0.65, -1.25) * mm});
            skLineSegment(sketch, "E4875", {"start": v(-0.65, -0.85) * mm, "end": v(-0.65, -0.75) * mm});
            skLineSegment(sketch, "E4876", {"start": v(-0.65, -0.75) * mm, "end": v(0.05, -0.75) * mm});
            skLineSegment(sketch, "E4877", {"start": v(0.05, -0.75) * mm, "end": v(0.3, -0.5) * mm});
            skLineSegment(sketch, "E4878", {"start": v(0.3, -0.5) * mm, "end": v(0.35, -0.46) * mm});
            skLineSegment(sketch, "E4879", {"start": v(0.55, -0.25) * mm, "end": v(0.7, -0.1) * mm});
            skLineSegment(sketch, "E4880", {"start": v(0.7, -0.1) * mm, "end": v(0.7, -0.05) * mm});
            skLineSegment(sketch, "E4881", {"start": v(0.7, -0.05) * mm, "end": v(0.85, -0.05) * mm});
            skLineSegment(sketch, "E4882", {"start": v(0.85, -0.05) * mm, "end": v(1.15, -0.05) * mm});
            skLineSegment(sketch, "E4883", {"start": v(1.15, -0.05) * mm, "end": v(1.3, -0.2) * mm});
            skLineSegment(sketch, "E4884", {"start": v(1.3, -0.2) * mm, "end": v(1.55, -0.2) * mm});
            skLineSegment(sketch, "E4885", {"start": v(0.95, 0.05) * mm, "end": v(1.35, 0.45) * mm});
            skLineSegment(sketch, "E4886", {"start": v(1.35, 0.45) * mm, "end": v(1.35, 0.75) * mm});
            skLineSegment(sketch, "E4887", {"start": v(1.25, 0.75) * mm, "end": v(1.25, 0.7) * mm});
            skLineSegment(sketch, "E4888", {"start": v(1.25, 0.7) * mm, "end": v(1.2, 0.65) * mm});
            skLineSegment(sketch, "E4889", {"start": v(1.2, 0.65) * mm, "end": v(0.85, 0.65) * mm});
            skLineSegment(sketch, "E4890", {"start": v(0.75, 0.65) * mm, "end": v(0.75, 0.75) * mm});
            skLineSegment(sketch, "E4891", {"start": v(0.75, 1.2) * mm, "end": v(0.8, 1.25) * mm});
            skLineSegment(sketch, "E4892", {"start": v(0.8, 1.25) * mm, "end": v(1, 1.25) * mm});
            skLineSegment(sketch, "E4893", {"start": v(1, 1.25) * mm, "end": v(1.05, 1.2) * mm});
            skLineSegment(sketch, "E4894", {"start": v(1.05, 1.2) * mm, "end": v(1.06, 1.2) * mm});
            skLineSegment(sketch, "E4895", {"start": v(0.7, 0.25) * mm, "end": v(0.7, -0.05) * mm});
            skLineSegment(sketch, "E4896", {"start": v(0.85, 0.05) * mm, "end": v(0.95, 0.05) * mm});
            skLineSegment(sketch, "E4897", {"start": v(0.55, -0.25) * mm, "end": v(-0.95, -0.25) * mm});
            skLineSegment(sketch, "E4898", {"start": v(-0.85, -0.35) * mm, "end": v(-0.65, -0.35) * mm});
            skLineSegment(sketch, "E4899", {"start": v(-0.75, -0.65) * mm, "end": v(-0.15, -0.65) * mm});
            skLineSegment(sketch, "E4900", {"start": v(-0.15, -0.65) * mm, "end": v(-0.05, -0.55) * mm});
            skLineSegment(sketch, "E4901", {"start": v(-0.05, -0.55) * mm, "end": v(-0.05, -0.46) * mm});
            skLineSegment(sketch, "E4902", {"start": v(-0.75, -0.65) * mm, "end": v(-0.85, -0.75) * mm});
            skLineSegment(sketch, "E4903", {"start": v(-0.85, -0.75) * mm, "end": v(-0.85, -0.85) * mm});
            skLineSegment(sketch, "E4904", {"start": v(-0.85, -0.15) * mm, "end": v(-0.75, -0.15) * mm});
            skLineSegment(sketch, "E4905", {"start": v(-0.75, -0.15) * mm, "end": v(-0.65, -0.15) * mm});
            skLineSegment(sketch, "E4906", {"start": v(-0.65, -0.15) * mm, "end": v(-0.55, -0.05) * mm});
            skLineSegment(sketch, "E4907", {"start": v(-0.55, -0.05) * mm, "end": v(-0.55, 0.15) * mm});
            skLineSegment(sketch, "E4908", {"start": v(-0.65, 0.15) * mm, "end": v(-0.65, 0) * mm});
            skLineSegment(sketch, "E4909", {"start": v(-0.65, 0) * mm, "end": v(-0.7, -0.05) * mm});
            skLineSegment(sketch, "E4910", {"start": v(-0.7, -0.05) * mm, "end": v(-0.75, -0.05) * mm});
            skLineSegment(sketch, "E4911", {"start": v(-0.85, -0.15) * mm, "end": v(-0.95, -0.05) * mm});
            skLineSegment(sketch, "E4912", {"start": v(-0.95, -0.05) * mm, "end": v(-0.95, 0.65) * mm});
            skLineSegment(sketch, "E4913", {"start": v(-0.95, 0.65) * mm, "end": v(-0.9, 0.7) * mm});
            skLineSegment(sketch, "E4914", {"start": v(-0.9, 0.7) * mm, "end": v(-0.9, 1.1) * mm});
            skLineSegment(sketch, "E4915", {"start": v(-0.9, 1.1) * mm, "end": v(-0.95, 1.15) * mm});
            skLineSegment(sketch, "E4916", {"start": v(-0.95, 1.15) * mm, "end": v(-0.95, 1.2) * mm});
            skLineSegment(sketch, "E4917", {"start": v(-0.85, 1.2) * mm, "end": v(-0.85, 1.15) * mm});
            skLineSegment(sketch, "E4918", {"start": v(-0.85, 1.15) * mm, "end": v(-0.75, 1.05) * mm});
            skLineSegment(sketch, "E4919", {"start": v(-0.85, 1.05) * mm, "end": v(-0.85, 0.9) * mm});
            skLineSegment(sketch, "E4920", {"start": v(-0.85, 0.9) * mm, "end": v(-0.75, 0.8) * mm});
            skLineSegment(sketch, "E4921", {"start": v(-0.75, 0.8) * mm, "end": v(-0.75, 0.65) * mm});
            skLineSegment(sketch, "E4922", {"start": v(-0.75, 0.65) * mm, "end": v(-0.75, 0.45) * mm});
            skLineSegment(sketch, "E4923", {"start": v(-1.05, 0.45) * mm, "end": v(-1.05, 0.35) * mm});
            skLineSegment(sketch, "E4924", {"start": v(-1.05, 0.35) * mm, "end": v(-1.15, 0.25) * mm});
            skLineSegment(sketch, "E4925", {"start": v(-1.15, 0.25) * mm, "end": v(-1.55, 0.25) * mm});
            skLineSegment(sketch, "E4926", {"start": v(-1.55, 0.45) * mm, "end": v(-1.15, 0.45) * mm});
            skLineSegment(sketch, "E4927", {"start": v(-1.15, 0.45) * mm, "end": v(-1.15, 0.65) * mm});
            skLineSegment(sketch, "E4928", {"start": v(-1.05, 0.65) * mm, "end": v(-1.05, 0.45) * mm});
            skLineSegment(sketch, "E4929", {"start": v(-1.05, 0.05) * mm, "end": v(-1.15, 0.05) * mm});
            skLineSegment(sketch, "E4930", {"start": v(-1.15, 0.05) * mm, "end": v(-1.15, -0.05) * mm});
            skLineSegment(sketch, "E4931", {"start": v(-1.15, -0.05) * mm, "end": v(-1.15, -0.15) * mm});
            skLineSegment(sketch, "E4932", {"start": v(-0.45, -0.15) * mm, "end": v(-0.35, -0.15) * mm});
            skLineSegment(sketch, "E4933", {"start": v(-0.35, -0.15) * mm, "end": v(-0.25, -0.05) * mm});
            skLineSegment(sketch, "E4934", {"start": v(-0.25, -0.05) * mm, "end": v(-0.15, -0.05) * mm});
            skLineSegment(sketch, "E4935", {"start": v(-0.05, 0) * mm, "end": v(-0.05, 0.05) * mm});
            skLineSegment(sketch, "E4936", {"start": v(-0.05, 0.05) * mm, "end": v(-0.15, 0.15) * mm});
            skLineSegment(sketch, "E4937", {"start": v(-0.15, 0.05) * mm, "end": v(-0.1, 0.05) * mm});
            skLineSegment(sketch, "E4938", {"start": v(-0.15, 0.05) * mm, "end": v(-0.35, 0.05) * mm});
            skLineSegment(sketch, "E4939", {"start": v(-0.35, 0.05) * mm, "end": v(-0.35, 0.15) * mm});
            skLineSegment(sketch, "E4940", {"start": v(-0.35, 0.05) * mm, "end": v(-0.35, 0) * mm});
            skLineSegment(sketch, "E4941", {"start": v(-0.35, 0) * mm, "end": v(-0.4, -0.05) * mm});
            skLineSegment(sketch, "E4942", {"start": v(-0.4, -0.05) * mm, "end": v(-0.45, -0.05) * mm});
            skLineSegment(sketch, "E4943", {"start": v(-0.05, 0) * mm, "end": v(0.1, -0.15) * mm});
            skLineSegment(sketch, "E4944", {"start": v(0.1, -0.15) * mm, "end": v(0.15, -0.15) * mm});
            skLineSegment(sketch, "E4945", {"start": v(0.35, -0.05) * mm, "end": v(0.45, -0.05) * mm});
            skLineSegment(sketch, "E4946", {"start": v(0.35, -0.05) * mm, "end": v(0.25, 0.05) * mm});
            skLineSegment(sketch, "E4947", {"start": v(0.25, 0.05) * mm, "end": v(0.15, 0.05) * mm});
            skLineSegment(sketch, "E4948", {"start": v(0.25, 0.15) * mm, "end": v(0.35, 0.05) * mm});
            skLineSegment(sketch, "E4949", {"start": v(0.35, 0.05) * mm, "end": v(0.45, 0.05) * mm});
            skLineSegment(sketch, "E4950", {"start": v(0.25, 0.55) * mm, "end": v(0.15, 0.55) * mm});
            skLineSegment(sketch, "E4951", {"start": v(0.4, 0.95) * mm, "end": v(0.35, 1) * mm});
            skLineSegment(sketch, "E4952", {"start": v(0.35, 1) * mm, "end": v(0.35, 1.05) * mm});
            skLineSegment(sketch, "E4953", {"start": v(0.45, 1.05) * mm, "end": v(0.45, 1.1) * mm});
            skLineSegment(sketch, "E4954", {"start": v(0.45, 1.1) * mm, "end": v(0.4, 1.15) * mm});
            skLineSegment(sketch, "E4955", {"start": v(0.4, 1.15) * mm, "end": v(0.3, 1.15) * mm});
            skLineSegment(sketch, "E4956", {"start": v(0.3, 1.15) * mm, "end": v(0.25, 1.2) * mm});
            skLineSegment(sketch, "E4957", {"start": v(0.25, 1.2) * mm, "end": v(0.25, 1.25) * mm});
            skLineSegment(sketch, "E4958", {"start": v(0.15, 1.25) * mm, "end": v(0.15, 1.2) * mm});
            skLineSegment(sketch, "E4959", {"start": v(0.15, 1.2) * mm, "end": v(0.25, 1.1) * mm});
            skLineSegment(sketch, "E4960", {"start": v(0.25, 1.1) * mm, "end": v(0.25, 1.05) * mm});
            skLineSegment(sketch, "E4961", {"start": v(0.15, 1.05) * mm, "end": v(0.15, 1.1) * mm});
            skLineSegment(sketch, "E4962", {"start": v(0.15, 1.1) * mm, "end": v(0.05, 1.2) * mm});
            skLineSegment(sketch, "E4963", {"start": v(0.05, 1.2) * mm, "end": v(0.05, 1.25) * mm});
            skLineSegment(sketch, "E4964", {"start": v(-0.05, 1.1) * mm, "end": v(-0.05, 1.05) * mm});
            skLineSegment(sketch, "E4965", {"start": v(-0.05, 1.1) * mm, "end": v(-0.15, 1.2) * mm});
            skLineSegment(sketch, "E4966", {"start": v(-0.15, 1.2) * mm, "end": v(-0.15, 1.25) * mm});
            skLineSegment(sketch, "E4967", {"start": v(-0.25, 1.25) * mm, "end": v(-0.25, 1.2) * mm});
            skLineSegment(sketch, "E4968", {"start": v(-0.25, 1.2) * mm, "end": v(-0.15, 1.1) * mm});
            skLineSegment(sketch, "E4969", {"start": v(-0.15, 1.1) * mm, "end": v(-0.15, 1.05) * mm});
            skLineSegment(sketch, "E4970", {"start": v(-0.35, 1.05) * mm, "end": v(-0.35, 1) * mm});
            skLineSegment(sketch, "E4971", {"start": v(-0.35, 1) * mm, "end": v(-0.4, 0.95) * mm});
            skLineSegment(sketch, "E4972", {"start": v(-0.4, 0.95) * mm, "end": v(-0.6, 0.95) * mm});
            skLineSegment(sketch, "E4973", {"start": v(-0.6, 0.95) * mm, "end": v(-0.65, 1) * mm});
            skLineSegment(sketch, "E4974", {"start": v(-0.65, 1) * mm, "end": v(-0.65, 1.05) * mm});
            skLineSegment(sketch, "E4975", {"start": v(-0.55, 1.05) * mm, "end": v(-0.45, 1.05) * mm});
            skLineSegment(sketch, "E4976", {"start": v(-0.45, 1.05) * mm, "end": v(-0.55, 1.05) * mm});
            skLineSegment(sketch, "E4977", {"start": v(-0.35, 1.2) * mm, "end": v(-0.35, 1.25) * mm});
            skLineSegment(sketch, "E4978", {"start": v(-0.95, 1.05) * mm, "end": v(-1.05, 1.05) * mm});
            skLineSegment(sketch, "E4979", {"start": v(-1.05, 1.05) * mm, "end": v(-1.05, 1.2) * mm});
            skLineSegment(sketch, "E4980", {"start": v(-1.05, 1.05) * mm, "end": v(-1.15, 1.05) * mm});
            skLineSegment(sketch, "E4981", {"start": v(0.4, 0.95) * mm, "end": v(0.7, 0.95) * mm});
            skLineSegment(sketch, "E4982", {"start": v(0.7, 0.95) * mm, "end": v(0.85, 0.8) * mm});
            skLineSegment(sketch, "E4983", {"start": v(0.85, 0.8) * mm, "end": v(0.85, 0.75) * mm});
            skLineSegment(sketch, "E4984", {"start": v(0.85, 1.05) * mm, "end": v(0.85, 1.1) * mm});
            skLineSegment(sketch, "E4985", {"start": v(0.85, 1.1) * mm, "end": v(0.8, 1.15) * mm});
            skLineSegment(sketch, "E4986", {"start": v(0.8, 1.15) * mm, "end": v(0.75, 1.15) * mm});
            skLineSegment(sketch, "E4987", {"start": v(0.75, 1.15) * mm, "end": v(0.7, 1.15) * mm});
            skLineSegment(sketch, "E4988", {"start": v(0.7, 1.15) * mm, "end": v(0.65, 1.2) * mm});
            skLineSegment(sketch, "E4989", {"start": v(0.65, 1.2) * mm, "end": v(0.66, 1.2) * mm});
            skLineSegment(sketch, "E4990", {"start": v(0.74, 1.2) * mm, "end": v(0.75, 1.2) * mm});
            skLineSegment(sketch, "E4991", {"start": v(0.85, 1.2) * mm, "end": v(0.86, 1.2) * mm});
            skLineSegment(sketch, "E4992", {"start": v(0.85, 1.2) * mm, "end": v(0.95, 1.1) * mm});
            skLineSegment(sketch, "E4993", {"start": v(0.95, 1.1) * mm, "end": v(0.95, 1.05) * mm});
            skLineSegment(sketch, "E4994", {"start": v(1.05, 1.05) * mm, "end": v(1.05, 1.1) * mm});
            skLineSegment(sketch, "E4995", {"start": v(1.05, 1.1) * mm, "end": v(0.95, 1.2) * mm});
            skLineSegment(sketch, "E4996", {"start": v(0.95, 1.2) * mm, "end": v(0.94, 1.2) * mm});
            skLineSegment(sketch, "E4997", {"start": v(1.14, 1.2) * mm, "end": v(1.15, 1.2) * mm});
            skLineSegment(sketch, "E4998", {"start": v(1.15, 1.2) * mm, "end": v(1.25, 1.1) * mm});
            skLineSegment(sketch, "E4999", {"start": v(1.25, 1.1) * mm, "end": v(1.25, 1.05) * mm});
            skLineSegment(sketch, "E5000", {"start": v(1.35, 1.05) * mm, "end": v(1.35, 1.2) * mm});
            skLineSegment(sketch, "E5001", {"start": v(1.35, 1.2) * mm, "end": v(1.34, 1.2) * mm});
            skLineSegment(sketch, "E5002", {"start": v(0.75, 1.05) * mm, "end": v(0.65, 1.05) * mm});
            skLineSegment(sketch, "E5003", {"start": v(0.95, -0.65) * mm, "end": v(1.2, -0.65) * mm});
            skLineSegment(sketch, "E5004", {"start": v(1.2, -0.85) * mm, "end": v(1.05, -0.85) * mm});
            skLineSegment(sketch, "E5005", {"start": v(1.05, -0.85) * mm, "end": v(0.65, -1.25) * mm});
            skLineSegment(sketch, "E5006", {"start": v(0.65, -1.25) * mm, "end": v(0.55, -1.25) * mm});
            skLineSegment(sketch, "E5007", {"start": v(0.55, -1.25) * mm, "end": v(0.54, -1.24) * mm});
            skLineSegment(sketch, "E5008", {"start": v(0.55, -1.05) * mm, "end": v(0.95, -0.65) * mm});
            skLineSegment(sketch, "E5009", {"start": v(0.55, -1.05) * mm, "end": v(-0.05, -1.05) * mm});
            skLineSegment(sketch, "E5010", {"start": v(-0.05, -1.05) * mm, "end": v(-0.24, -1.24) * mm});
            skSolve(sketch);
        }
        {
            var Q0;
            Q0=qCreatedBy(makeId("Front.planeOp"),FACE);
            var sketch = newSketch(context, id + "F1", { "sketchPlane" : qUnion([Q0])});
            skPoint(sketch, "E5011.0", {"position": v(1.67, 1.1) * mm});
            skPoint(sketch, "E5012.0", {"position": v(-1.67, 1.1) * mm});
            skPoint(sketch, "E5013.0", {"position": v(-1.9, 1.47) * mm});
            skPoint(sketch, "E5014.0", {"position": v(-1.67, -1.1) * mm});
            skPoint(sketch, "E5015.0", {"position": v(-1.9, -1.47) * mm});
            skPoint(sketch, "E5016.0", {"position": v(1.9, -1.47) * mm});
            skPoint(sketch, "E5017.0", {"position": v(1.67, -1.1) * mm});
            skPoint(sketch, "E5018.0", {"position": v(1.9, 1.47) * mm});
            skLineSegment(sketch, "E5019", {"start": v(-1.9, 1.47) * mm, "end": v(1.9, 1.47) * mm});
            skLineSegment(sketch, "E5020", {"start": v(1.9, -1.47) * mm, "end": v(1.9, 1.47) * mm});
            skLineSegment(sketch, "E5021", {"start": v(1.9, -1.47) * mm, "end": v(-1.9, -1.47) * mm});
            skLineSegment(sketch, "E5022", {"start": v(-1.9, 1.47) * mm, "end": v(-1.9, -1.47) * mm});
            skPoint(sketch, "E5023.0", {"position": v(-1.7, 1.05) * mm});
            skPoint(sketch, "E5024.0", {"position": v(1.67, 1.03) * mm});
            skPoint(sketch, "E5025.0", {"position": v(1.67, -1.16) * mm});
            skPoint(sketch, "E5026.0", {"position": v(-1.7, -1.15) * mm});
            skCircle(sketch, "E5027", {"center": v(-1.67, -1.1) * mm, "radius": 0.06 * mm});
            skCircle(sketch, "E5028", {"center": v(1.67, -1.1) * mm, "radius": 0.06 * mm});
            skCircle(sketch, "E5029", {"center": v(1.67, 1.1) * mm, "radius": 0.06 * mm});
            skCircle(sketch, "E5030", {"center": v(-1.67, 1.1) * mm, "radius": 0.06 * mm});
            skSolve(sketch);
        }
        {
            var Q0;
            Q0 = qSketchRegion(id + "F1", true);
            extrude(context, id + "F2", {"entities" : qUnion([Q0]), "depth" : 0.06 * mm, "offsetDistance" : 25 * mm});
        }
        {
            var Q0;
            Q0=makeQuery(id+"F2.opExtrude","SWEPT_BODY",BODY,{"disambiguationData":[OSD([sQuery(id+"F1.wireOp",EDGE,"E5019"),sQuery(id+"F1.wireOp",EDGE,"E5020"),sQuery(id+"F1.wireOp",EDGE,"E5021"),sQuery(id+"F1.wireOp",EDGE,"E5022"),sQuery(id+"F1.wireOp",EDGE,"E5027"),sQuery(id+"F1.wireOp",EDGE,"E5028"),sQuery(id+"F1.wireOp",EDGE,"E5029"),sQuery(id+"F1.wireOp",EDGE,"E5030")])]});
            var Q1;
            Q1=makeQuery(id+"F2.opExtrude","CAP_VERTEX",VERTEX,{"disambiguationData":[OSD([sQuery(id+"F1.wireOp",EDGE,"E5020"),sQuery(id+"F1.wireOp",EDGE,"E5021")])],"isStart":false});
            transform(context, id + "F3", {"entities" : qUnion([Q0]), "transformType" : TransformType.SCALE_UNIFORMLY, "scale" : 25.4, "scalePoint" : qUnion([Q1]), "makeCopy" : false});
        }
    });
